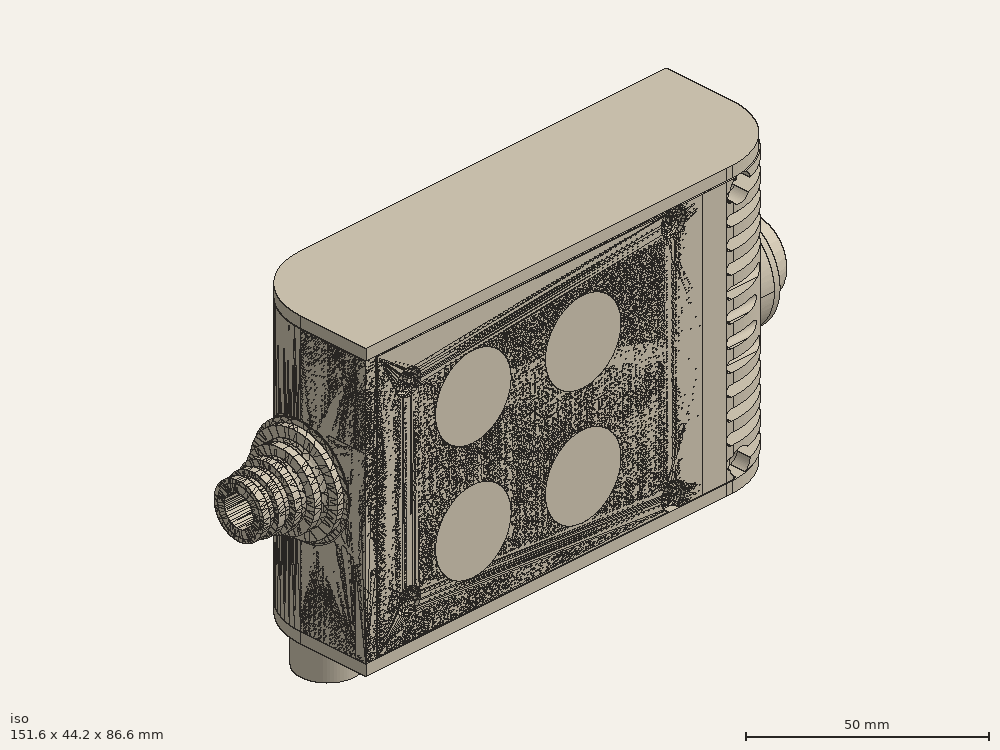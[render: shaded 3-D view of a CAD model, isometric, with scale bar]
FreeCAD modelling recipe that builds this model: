
FCSTD DOCUMENT  (FreeCAD 0.19R0.19.2)
Label: enclosure_207FCStd
License: All rights reserved
LicenseURL: http://en.wikipedia.org/wiki/All_rights_reserved
objects: Part::Revolution×152, Part::MultiFuse×146, Part::Feature×146, Sketcher::SketchObject×84, Part::Cut×70, Part::Cylinder×70, Part::Extrusion×69, Part::Fillet×58, Part::Box×36, App::MeasureDistance×4, Part::FeaturePython×2, Image::ImagePlane×1, PartDesign::Body×1, Part::Mirroring×1
note: 835 computed .brp shape members not serialized (recipe doc carries the construction recipe); baked Part::Feature solids carry a one-line shape summary decoded from their .brp

FEATURE [Sketcher::SketchObject] Sketch  label="topSketch"
  FullyConstrained = true
  sketch-geometry (20):
    g0: LineSegment StartX=5.21097e-06 StartY=3 StartZ=0 EndX=5.21097e-06 EndY=19 EndZ=0
    g1: ArcOfCircle CenterX=19 CenterY=19 CenterZ=0 NormalX=0 NormalY=0 NormalZ=1 AngleXU=0 Radius=19 StartAngle=1.5708 EndAngle=3.14159
    g2: ArcOfCircle CenterX=19 CenterY=19 CenterZ=0 NormalX=0 NormalY=0 NormalZ=1 AngleXU=0 Radius=16 StartAngle=1.5708 EndAngle=3.14159
    g3: LineSegment StartX=114 StartY=35 StartZ=0 EndX=19 EndY=35 EndZ=0
    g4: LineSegment StartX=5.21097e-06 StartY=3 StartZ=0 EndX=5.21097e-06 EndY=0 EndZ=0
    g5: LineSegment StartX=3 StartY=0 StartZ=0 EndX=5.21097e-06 EndY=0 EndZ=0
    g6: LineSegment StartX=3 StartY=19 StartZ=0 EndX=3 EndY=0 EndZ=0
    g7: LineSegment StartX=19 StartY=38 StartZ=0 EndX=124 EndY=38 EndZ=0
    g8: Circle CenterX=119 CenterY=35 CenterZ=0 NormalX=0 NormalY=0 NormalZ=1 AngleXU=0 Radius=1
    g9: Circle CenterX=121 CenterY=35 CenterZ=0 NormalX=0 NormalY=0 NormalZ=1 AngleXU=0 Radius=1
    g10: Circle CenterX=121 CenterY=33 CenterZ=0 NormalX=0 NormalY=0 NormalZ=1 AngleXU=0 Radius=1
    g11: BSplineCurve PolesCount=3 KnotsCount=2 Degree=2 IsPeriodic=0
    g12: GeomPoint X=119 Y=35 Z=0
    g13: GeomPoint X=121 Y=33 Z=0
    g14: LineSegment StartX=119 StartY=35 StartZ=0 EndX=114 EndY=35 EndZ=0
    g15: ArcOfCircle CenterX=105 CenterY=19 CenterZ=0 NormalX=0 NormalY=0 NormalZ=1 AngleXU=0 Radius=19 StartAngle=5.7297 EndAngle=6.28319
    g16: ArcOfCircle CenterX=105 CenterY=19 CenterZ=0 NormalX=0 NormalY=0 NormalZ=1 AngleXU=0 Radius=16 StartAngle=5.60905 EndAngle=6.28319
    g17: LineSegment StartX=121 StartY=33 StartZ=0 EndX=121 EndY=19 EndZ=0
    g18: LineSegment StartX=124 StartY=38 StartZ=0 EndX=124 EndY=19 EndZ=0
    g19: LineSegment StartX=117.5 StartY=9.01251 StartZ=0 EndX=121.163 EndY=9.0125 EndZ=0
  constraints (46):
    c: Vertical(g0)
    c: Block(g0)
    c: Coincident(g1,g0)
    c: Block(g1)
    c: Coincident(g2,g1)
    c: Block(g2)
    c: Coincident(g3,g2)
    c: Horizontal(g3)
    c: Tangent(g3,g2)
    c: Coincident(g4,g0)
    c: Distance(g4) = 3
    c: Vertical(g4)
    c: Coincident(g5,g4)
    c: Horizontal(g5)
    c: Coincident(g6,g2)
    c: Coincident(g6,g5)
    c: Vertical(g6)
    c: Horizontal(g7)
    c: Distance(g7) = 105
    c: Coincident(g7,g1)
    c: Block(g3)
    c: Weight(g8) = 1
    c: Equal(g8,g9)
    c: Equal(g8,g10)
    c: InternalAlignment(g8,g11)
    c: InternalAlignment(g9,g11)
    c: InternalAlignment(g10,g11)
    c: InternalAlignment(g12,g11)
    c: InternalAlignment(g13,g11)
    c: Block(g11)
    c: Coincident(g14,g11)
    c: Coincident(g14,g3)
    c: Horizontal(g14)
    c: Block(g15)
    c: Coincident(g16,g15)
    c: Block(g16)
    c: Coincident(g17,g11)
    c: Coincident(g17,g16)
    c: Vertical(g17)
    c: Distance(g17) = 14
    c: Coincident(g18,g7)
    c: Coincident(g18,g15)
    c: Vertical(g18)
    c: Distance(g18) = 19
    c: Coincident(g19,g16)
    c: Coincident(g19,g15)
FEATURE [Sketcher::SketchObject] Sketch001  label="bottomSketch"
  FullyConstrained = true
  sketch-geometry (32):
    g0: LineSegment StartX=3.3 StartY=-6.03275e-07 StartZ=0 EndX=98 EndY=-6.03275e-07 EndZ=0
    g1: ArcOfCircle CenterX=98 CenterY=19 CenterZ=0 NormalX=0 NormalY=0 NormalZ=1 AngleXU=0 Radius=19 StartAngle=4.71239 EndAngle=5.71103
    g2: LineSegment StartX=6.3 StartY=8 StartZ=0 EndX=3.3 EndY=8 EndZ=0
    g3: LineSegment StartX=3.3 StartY=8 StartZ=0 EndX=3.3 EndY=-6.03275e-07 EndZ=0
    g4: ArcOfCircle CenterX=8.3 CenterY=5 CenterZ=0 NormalX=0 NormalY=0 NormalZ=1 AngleXU=0 Radius=2 StartAngle=3.14159 EndAngle=4.71239
    g5: LineSegment StartX=6.3 StartY=8 StartZ=0 EndX=6.3 EndY=5 EndZ=0
    g6: ArcOfCircle CenterX=98 CenterY=19 CenterZ=0 NormalX=0 NormalY=0 NormalZ=1 AngleXU=0 Radius=12.7 StartAngle=4.71239 EndAngle=6.28319
    g7: LineSegment StartX=94.7 StartY=3 StartZ=0 EndX=8.3 EndY=3 EndZ=0
    g8-g12: Circle x5 (B-spline internal-alignment scaffolding for g13; pole/knot coordinates omitted)
    g13: BSplineCurve PolesCount=5 KnotsCount=3 Degree=3 IsPeriodic=0
    g14: GeomPoint X=98 Y=6.3 Z=0
    g15: GeomPoint X=96.3938 Y=4.71946 Z=0
    g16: GeomPoint X=94.7 Y=3 Z=0
    g17-g23: Circle x7 (B-spline internal-alignment scaffolding for g24; pole/knot coordinates omitted)
    g24: BSplineCurve PolesCount=7 KnotsCount=5 Degree=3 IsPeriodic=0
    g25-g29: GeomPoint x5 (B-spline internal-alignment scaffolding for g24; pole/knot coordinates omitted)
    g30: ArcOfCircle CenterX=98 CenterY=19 CenterZ=0 NormalX=0 NormalY=0 NormalZ=1 AngleXU=0 Radius=15.7 StartAngle=5.81226 EndAngle=6.28319
    g31: LineSegment StartX=110.7 StartY=19 StartZ=0 EndX=113.7 EndY=19 EndZ=0
  constraints (41):
    c: Horizontal(g0)
    c: Coincident(g1,g0)
    c: Block(g1)
    c: Horizontal(g2)
    c: Distance(g2) = 3
    c: Coincident(g3,g2)
    c: Vertical(g3)
    c: Coincident(g3,g0)
    c: Block(g4)
    c: Block(g2)
    c: Coincident(g5,g2)
    c: Coincident(g5,g4)
    c: Vertical(g5)
    c: Coincident(g6,g1)
    c: Block(g6)
    c: Coincident(g7,g4)
    c: Horizontal(g7)
    c: Block(g0)
    c: Block(g7)
    c: Block(g3)
    c: Coincident(g13,g6)
    c: Weight(g8) = 1
    c: Equal(g8, g9-g12) x4
    c: Coincident(g13,g7)
    c: InternalAlignment(g8-g12 -> g13) x5
    c: InternalAlignment(g14,g13)
    c: InternalAlignment(g15,g13)
    c: InternalAlignment(g16,g13)
    c: Block(g13)
    c: Weight(g17) = 1
    c: Equal(g17, g18-g23) x6
    c: Coincident(g24,g1)
    c: InternalAlignment(g17-g23 -> g24) x7
    c: InternalAlignment(g25-g29 -> g24) x5
    c: Block(g24)
    c: Coincident(g30,g24)
    c: Coincident(g31,g6)
    c: Coincident(g31,g30)
    c: Horizontal(g31)
    c: Block(g31)
    c: Block(g30)
FEATURE [Part::Extrusion] Extrude  label="top"
  Base = -> Sketch
  Dir = (0,0,1)
  DirMode = 2
  FaceMakerClass = Part::FaceMakerBullseye
  LengthFwd = 72
  LengthRev = 0
  Solid = true
  Symmetric = false
FEATURE [Part::Extrusion] Extrude001  label="bottom"
  Base = -> Sketch001
  Dir = (0,0,1)
  DirMode = 2
  FaceMakerClass = Part::FaceMakerBullseye
  LengthFwd = 71.4
  LengthRev = 0
  Placement = pos=(0,0,0.3) rot=(0,0,1;0rad)
  Solid = true
  Symmetric = false
FEATURE [Sketcher::SketchObject] Sketch002  label="topSketch001"
  FullyConstrained = true
  sketch-geometry (8):
    g0: ArcOfCircle CenterX=19 CenterY=19.0975 CenterZ=0 NormalX=0 NormalY=0 NormalZ=1 AngleXU=0 Radius=18.9025 StartAngle=1.5708 EndAngle=3.14674
    g1: LineSegment StartX=0.0977805 StartY=19.0003 StartZ=0 EndX=0.0977805 EndY=0.000251602 EndZ=0
    g2: LineSegment StartX=19 StartY=38 StartZ=0 EndX=124 EndY=38 EndZ=0
    g3: LineSegment StartX=0.0977805 StartY=0.000251602 StartZ=0 EndX=105.098 EndY=0.000251602 EndZ=0
    g4: LineSegment StartX=124 StartY=38 StartZ=0 EndX=125.616 EndY=38 EndZ=0
    g5: LineSegment StartX=105.098 StartY=0.000251602 StartZ=0 EndX=106.713 EndY=0.000251602 EndZ=0
    g6: ArcOfCircle CenterX=106.616 CenterY=19 CenterZ=0 NormalX=0 NormalY=0 NormalZ=1 AngleXU=0 Radius=19 StartAngle=4.71754 EndAngle=6.28319
    g7: LineSegment StartX=125.616 StartY=38 StartZ=0 EndX=125.616 EndY=19 EndZ=0
  constraints (21):
    c: Block(g0)
    c: Coincident(g1,g0)
    c: Vertical(g1)
    c: Horizontal(g2)
    c: Distance(g2) = 105
    c: Coincident(g2,g0)
    c: Distance(g1) = 19
    c: Coincident(g3,g1)
    c: Horizontal(g3)
    c: Distance(g3) = 105
    c: Coincident(g4,g2)
    c: Horizontal(g4)
    c: Distance(g4) = 1.61553
    c: Horizontal(g5)
    c: Equal(g4,g5) = 1.61553
    c: Coincident(g5,g3)
    c: Block(g6)
    c: Coincident(g6,g5)
    c: Coincident(g7,g4)
    c: Coincident(g7,g6)
    c: Vertical(g7)
FEATURE [Part::Extrusion] Extrude002  label="sideA"
  Base = -> Sketch002
  Dir = (0,0,1)
  DirMode = 2
  FaceMakerClass = Part::FaceMakerBullseye
  LengthFwd = 3
  LengthRev = 0
  Placement = pos=(0,0,-3) rot=(0,0,1;0rad)
  Solid = true
  Symmetric = false
FEATURE [Sketcher::SketchObject] Sketch003  label="topSketch002"
  FullyConstrained = true
  sketch-geometry (6):
    g0: LineSegment StartX=19 StartY=38 StartZ=0 EndX=117 EndY=38 EndZ=0
    g1: ArcOfCircle CenterX=19 CenterY=19 CenterZ=0 NormalX=0 NormalY=0 NormalZ=1 AngleXU=0 Radius=19 StartAngle=1.5708 EndAngle=3.14159
    g2: LineSegment StartX=117 StartY=38 StartZ=0 EndX=117 EndY=19 EndZ=0
    g3: LineSegment StartX=98 StartY=1.0161e-12 StartZ=0 EndX=5.22862e-06 EndY=1.0161e-12 EndZ=0
    g4: LineSegment StartX=5.22862e-06 StartY=19 StartZ=0 EndX=5.22862e-06 EndY=1.0161e-12 EndZ=0
    g5: ArcOfCircle CenterX=98 CenterY=19 CenterZ=0 NormalX=0 NormalY=0 NormalZ=1 AngleXU=0 Radius=19 StartAngle=4.71239 EndAngle=6.28319
  constraints (16):
    c: Horizontal(g0)
    c: Distance(g0) = 98
    c: Coincident(g1,g0)
    c: Block(g1)
    c: Coincident(g2,g0)
    c: Vertical(g2)
    c: Distance(g2) = 19
    c: Horizontal(g3)
    c: Coincident(g4,g1)
    c: Vertical(g4)
    c: Coincident(g3,g4)
    c: Block(g3)
    c: Coincident(g5,g2)
    c: Coincident(g5,g3)
    c: Block(g0)
    c: Block(g5)
FEATURE [Sketcher::SketchObject] Sketch004
  FullyConstrained = true
  MapMode = 3
  Placement = pos=(0,0,0) rot=(1,0,0;1.5708rad)
  Support = -> [Extrude]
  sketch-geometry (8):
    g0: Circle CenterX=80.351 CenterY=-67.6202 CenterZ=0 NormalX=0 NormalY=0 NormalZ=1 AngleXU=0 Radius=2
    g1: Circle CenterX=80.351 CenterY=-67.6202 CenterZ=0 NormalX=0 NormalY=0 NormalZ=1 AngleXU=0 Radius=3
    g2: Circle CenterX=80.351 CenterY=-4.92017 CenterZ=0 NormalX=0 NormalY=0 NormalZ=1 AngleXU=0 Radius=2
    g3: Circle CenterX=80.351 CenterY=-4.92017 CenterZ=0 NormalX=0 NormalY=0 NormalZ=1 AngleXU=0 Radius=3
    g4: Circle CenterX=23.851 CenterY=-4.92017 CenterZ=0 NormalX=0 NormalY=0 NormalZ=1 AngleXU=0 Radius=2
    g5: Circle CenterX=23.851 CenterY=-4.92017 CenterZ=0 NormalX=0 NormalY=0 NormalZ=1 AngleXU=0 Radius=3
    g6: Circle CenterX=23.851 CenterY=-67.6202 CenterZ=0 NormalX=0 NormalY=0 NormalZ=1 AngleXU=0 Radius=2
    g7: Circle CenterX=23.851 CenterY=-67.6202 CenterZ=0 NormalX=0 NormalY=0 NormalZ=1 AngleXU=0 Radius=3
  constraints (8):
    c: Block(g3)
    c: Block(g2)
    c: Block(g1)
    c: Block(g0)
    c: Block(g6)
    c: Block(g7)
    c: Block(g4)
    c: Block(g5)
FEATURE [Part::Extrusion] Extrude004
  Base = -> Sketch004
  Dir = (0,-1,2e-16)
  DirMode = 2
  FaceMakerClass = Part::FaceMakerBullseye
  LengthFwd = 6
  LengthRev = 0
  Placement = pos=(0,9,0) rot=(0,0,1;0rad)
  Solid = true
  Symmetric = false
FEATURE [Sketcher::SketchObject] Sketch005
  FullyConstrained = true
  MapMode = 3
  Placement = pos=(0,0,0) rot=(1,0,0;1.5708rad)
  Support = -> [Extrude]
  sketch-geometry (8):
    g0: Circle CenterX=80.351 CenterY=-67.6202 CenterZ=0 NormalX=0 NormalY=0 NormalZ=1 AngleXU=0 Radius=3
    g1: Circle CenterX=80.351 CenterY=-4.92017 CenterZ=0 NormalX=0 NormalY=0 NormalZ=1 AngleXU=0 Radius=3
    g2: Circle CenterX=23.851 CenterY=-4.92017 CenterZ=0 NormalX=0 NormalY=0 NormalZ=1 AngleXU=0 Radius=3
    g3: Circle CenterX=23.851 CenterY=-67.6202 CenterZ=0 NormalX=0 NormalY=0 NormalZ=1 AngleXU=0 Radius=3
    g4: Circle CenterX=23.851 CenterY=-67.6202 CenterZ=0 NormalX=0 NormalY=0 NormalZ=1 AngleXU=0 Radius=5
    g5: Circle CenterX=80.351 CenterY=-67.6202 CenterZ=0 NormalX=0 NormalY=0 NormalZ=1 AngleXU=0 Radius=5
    g6: Circle CenterX=23.851 CenterY=-4.92017 CenterZ=0 NormalX=0 NormalY=0 NormalZ=1 AngleXU=0 Radius=5
    g7: Circle CenterX=80.351 CenterY=-4.92017 CenterZ=0 NormalX=0 NormalY=0 NormalZ=1 AngleXU=0 Radius=5
  constraints (8):
    c: Block(g1)
    c: Block(g0)
    c: Block(g3)
    c: Block(g2)
    c: Block(g5)
    c: Block(g4)
    c: Block(g6)
    c: Block(g7)
FEATURE [Part::Extrusion] Extrude005
  Base = -> Sketch005
  Dir = (0,-1,2e-16)
  DirMode = 2
  FaceMakerClass = Part::FaceMakerBullseye
  LengthFwd = 2
  LengthRev = 0
  Solid = true
  Symmetric = false
FEATURE [Sketcher::SketchObject] Sketch006
  FullyConstrained = true
  MapMode = 3
  Placement = pos=(0,0,0) rot=(1,0,0;1.5708rad)
  sketch-geometry (8):
    g0: Circle CenterX=80.351 CenterY=-67.6202 CenterZ=0 NormalX=0 NormalY=0 NormalZ=1 AngleXU=0 Radius=3
    g1: Circle CenterX=80.351 CenterY=-4.92017 CenterZ=0 NormalX=0 NormalY=0 NormalZ=1 AngleXU=0 Radius=3
    g2: Circle CenterX=23.851 CenterY=-4.92017 CenterZ=0 NormalX=0 NormalY=0 NormalZ=1 AngleXU=0 Radius=3
    g3: Circle CenterX=23.851 CenterY=-67.6202 CenterZ=0 NormalX=0 NormalY=0 NormalZ=1 AngleXU=0 Radius=3
    g4: Circle CenterX=23.851 CenterY=-67.6202 CenterZ=0 NormalX=0 NormalY=0 NormalZ=1 AngleXU=0 Radius=5
    g5: Circle CenterX=80.351 CenterY=-67.6202 CenterZ=0 NormalX=0 NormalY=0 NormalZ=1 AngleXU=0 Radius=5
    g6: Circle CenterX=23.851 CenterY=-4.92017 CenterZ=0 NormalX=0 NormalY=0 NormalZ=1 AngleXU=0 Radius=5
    g7: Circle CenterX=80.351 CenterY=-4.92017 CenterZ=0 NormalX=0 NormalY=0 NormalZ=1 AngleXU=0 Radius=5
  constraints (8):
    c: Block(g1)
    c: Block(g0)
    c: Block(g3)
    c: Block(g2)
    c: Block(g5)
    c: Block(g4)
    c: Block(g6)
    c: Block(g7)
FEATURE [Part::Extrusion] Extrude007
  Base = -> Sketch006
  Dir = (0,-1,2e-16)
  DirMode = 2
  FaceMakerClass = Part::FaceMakerBullseye
  LengthFwd = 2
  LengthRev = 0
  Solid = true
  Symmetric = false
FEATURE [Part::Fillet] Fillet
  Base = -> Extrude007
  Edges = 4 edges r=1.99: [Edge6,Edge12,Edge18,Edge24]
FEATURE [Part::Cut] Cut
  Base = -> Extrude005
  Placement = pos=(0,5,0) rot=(0,0,1;0rad)
  Tool = -> Fillet
FEATURE [Part::MultiFuse] Fusion  label="pCBScrews"
  Placement = pos=(-2.5,0,72.3) rot=(0,0,1;0rad)
  Shapes = -> [Extrude004,Cut]
FEATURE [App::MeasureDistance] Distance  label="Distance: 0.69 mm"
  Distance = 0.685967
  P1 = (24.0138,2.9647,0.3)
  P2 = (23.8901,3,-0.373787)
FEATURE [App::MeasureDistance] Distance001  label="Distance: 0.53 mm"
  Distance = 0.533607
  P1 = (80.2939,3,72.2334)
  P2 = (80.281,2.99661,71.7)
FEATURE [Part::Fillet] Fillet001
  Base = -> Extrude001
  Edges = 1 edges r=2.4: [Edge17]
FEATURE [Part::Fillet] Fillet002  label="bottom001"
  Base = -> Fillet001
  Edges = 1 edges r=2.4: [Edge36]
FEATURE [Part::Fillet] Fillet003  label="top001"
  Base = -> Extrude
  Edges = 1 edges r=2: [Edge1]
FEATURE [Sketcher::SketchObject] Sketch007
  FullyConstrained = true
  sketch-geometry (16):
    g0: LineSegment StartX=4 StartY=0 StartZ=0 EndX=4 EndY=2.4 EndZ=0
    g1: LineSegment StartX=4 StartY=2.4 StartZ=0 EndX=7 EndY=2.4 EndZ=0
    g2: LineSegment StartX=4 StartY=0 StartZ=0 EndX=5.7 EndY=0 EndZ=0
    g3: LineSegment StartX=5.7 StartY=0 StartZ=0 EndX=5.7 EndY=-5.6 EndZ=0
    g4-g8: Circle x5 (B-spline internal-alignment scaffolding for g9; pole/knot coordinates omitted)
    g9: BSplineCurve PolesCount=5 KnotsCount=3 Degree=3 IsPeriodic=0
    g10: GeomPoint X=7 Y=2.4 Z=0
    g11: GeomPoint X=10.4582 Y=-1.55472 Z=0
    g12: GeomPoint X=14 Y=-5.6 Z=0
    g13: LineSegment StartX=14 StartY=-5.6 StartZ=0 EndX=14 EndY=-14.1 EndZ=0
    g14: LineSegment StartX=14 StartY=-14.1 StartZ=0 EndX=6.5 EndY=-14.1 EndZ=0
    g15: LineSegment StartX=5.7 StartY=-5.6 StartZ=0 EndX=6.5 EndY=-14.1 EndZ=0
  constraints (28):
    c: Distance(g0) = 2.4
    c: Vertical(g0)
    c: Block(g0)
    c: Coincident(g1,g0)
    c: Horizontal(g1)
    c: Distance(g1) = 3
    c: Coincident(g2,g0)
    c: Horizontal(g2)
    c: Distance(g2) = 1.7
    c: Coincident(g3,g2)
    c: Vertical(g3)
    c: Distance(g3) = 5.6
    c: Coincident(g9,g1)
    c: Weight(g4) = 1
    c: Equal(g4, g5-g8) x4
    c: InternalAlignment(g4-g8 -> g9) x5
    c: InternalAlignment(g10,g9)
    c: InternalAlignment(g11,g9)
    c: InternalAlignment(g12,g9)
    c: Block(g9)
    c: Coincident(g13,g9)
    c: Vertical(g13)
    c: Distance(g13) = 8.5
    c: Coincident(g14,g13)
    c: Horizontal(g14)
    c: Distance(g14) = 7.5
    c: Coincident(g15,g3)
    c: Coincident(g15,g14)
FEATURE [Part::Feature] Face
  shape: bbox 10 x 16.5 x 2e-07 mm, 1 faces, 0 solids (baked)
FEATURE [Part::Revolution] Revolve  label="plugHousing"
  Angle = 360
  Axis = (0,1,0)
  Base = (0,0,0)
  FaceMakerClass = Part::FaceMakerBullseye
  Placement = pos=(0,0,36.15) rot=(0,0,1;0rad)
  Solid = false
  Source = -> Face
  Symmetric = false
FEATURE [Part::Feature] Face001
  shape: bbox 10 x 16.5 x 2e-07 mm, 1 faces, 0 solids (baked)
FEATURE [Part::Revolution] Revolve001  label="plugHousing001"
  Angle = 360
  Axis = (0,1,0)
  Base = (0,0,0)
  FaceMakerClass = Part::FaceMakerBullseye
  Placement = pos=(0,0,36.15) rot=(0,0,1;0rad)
  Solid = false
  Source = -> Face001
  Symmetric = false
FEATURE [Part::MultiFuse] Fusion001  label="plugHousing002"
  Placement = pos=(0,0,0) rot=(0,0,1;1.5708rad)
  Shapes = -> [Revolve001,Revolve]
FEATURE [Part::Feature] Face002
  shape: bbox 10 x 16.5 x 2e-07 mm, 1 faces, 0 solids (baked)
FEATURE [Part::Revolution] Revolve003  label="plugHousing005"
  Angle = 360
  Axis = (0,1,0)
  Base = (0,0,0)
  FaceMakerClass = Part::FaceMakerBullseye
  Placement = pos=(0,0,36.15) rot=(0,0,1;0rad)
  Solid = false
  Source = -> Face002
  Symmetric = false
FEATURE [Part::Feature] Face003
  shape: bbox 10 x 16.5 x 2e-07 mm, 1 faces, 0 solids (baked)
FEATURE [Part::Revolution] Revolve002  label="plugHousing003"
  Angle = 360
  Axis = (0,1,0)
  Base = (0,0,0)
  FaceMakerClass = Part::FaceMakerBullseye
  Placement = pos=(0,0,36.15) rot=(0,0,1;0rad)
  Solid = false
  Source = -> Face003
  Symmetric = false
FEATURE [Part::MultiFuse] Fusion002  label="plugHousing004"
  Placement = pos=(0,0,0) rot=(0,0,1;1.5708rad)
  Shapes = -> [Revolve002,Revolve003]
FEATURE [Part::MultiFuse] Fusion003  label="plugHousing006"
  Placement = pos=(0,19,0) rot=(0,0,1;3.14159rad)
  Shapes = -> [Fusion002,Fusion001]
FEATURE [Part::Feature] Face004
  shape: bbox 10 x 16.5 x 2e-07 mm, 1 faces, 0 solids (baked)
FEATURE [Part::Revolution] Revolve006  label="plugHousing010"
  Angle = 360
  Axis = (0,1,0)
  Base = (0,0,0)
  FaceMakerClass = Part::FaceMakerBullseye
  Placement = pos=(0,0,36.15) rot=(0,0,1;0rad)
  Solid = false
  Source = -> Face004
  Symmetric = false
FEATURE [Part::Feature] Face005
  shape: bbox 10 x 16.5 x 2e-07 mm, 1 faces, 0 solids (baked)
FEATURE [Part::Revolution] Revolve007  label="plugHousing011"
  Angle = 360
  Axis = (0,1,0)
  Base = (0,0,0)
  FaceMakerClass = Part::FaceMakerBullseye
  Placement = pos=(0,0,36.15) rot=(0,0,1;0rad)
  Solid = false
  Source = -> Face005
  Symmetric = false
FEATURE [Part::Feature] Face006
  shape: bbox 10 x 16.5 x 2e-07 mm, 1 faces, 0 solids (baked)
FEATURE [Part::Revolution] Revolve004  label="plugHousing007"
  Angle = 360
  Axis = (0,1,0)
  Base = (0,0,0)
  FaceMakerClass = Part::FaceMakerBullseye
  Placement = pos=(0,0,36.15) rot=(0,0,1;0rad)
  Solid = false
  Source = -> Face006
  Symmetric = false
FEATURE [Part::MultiFuse] Fusion004  label="plugHousing009"
  Placement = pos=(0,0,0) rot=(0,0,1;1.5708rad)
  Shapes = -> [Revolve004,Revolve007]
FEATURE [Part::Feature] Face007
  shape: bbox 10 x 16.5 x 2e-07 mm, 1 faces, 0 solids (baked)
FEATURE [Part::Revolution] Revolve005  label="plugHousing008"
  Angle = 360
  Axis = (0,1,0)
  Base = (0,0,0)
  FaceMakerClass = Part::FaceMakerBullseye
  Placement = pos=(0,0,36.15) rot=(0,0,1;0rad)
  Solid = false
  Source = -> Face007
  Symmetric = false
FEATURE [Part::MultiFuse] Fusion005  label="plugHousing012"
  Placement = pos=(0,0,0) rot=(0,0,1;1.5708rad)
  Shapes = -> [Revolve006,Revolve005]
FEATURE [Part::MultiFuse] Fusion006  label="plugHousing013"
  Placement = pos=(0,19,0) rot=(0,0,1;3.14159rad)
  Shapes = -> [Fusion005,Fusion004]
FEATURE [Part::MultiFuse] Fusion007  label="plugHousing014"
  Placement = pos=(122.621,0,-0.15) rot=(0,0,1;0rad)
  Shapes = -> [Fusion003,Fusion006]
FEATURE [Part::Cylinder] Cylinder002
  Angle = 360
  AttacherType = Attacher::AttachEngine3D
  Height = 20
  Placement = pos=(0,0,36.15) rot=(0,0,1;0rad)
  Radius = 4
FEATURE [Part::Cylinder] Cylinder003
  Angle = 360
  AttacherType = Attacher::AttachEngine3D
  Height = 10
  Placement = pos=(0,0,36.15) rot=(0,0,1;0rad)
  Radius = 4
FEATURE [Part::MultiFuse] Fusion009  label="removeToCreateHoleForPlugHousing"
  Placement = pos=(70,19,36.15) rot=(0,1,0;1.5708rad)
  Shapes = -> [Cylinder002,Cylinder003]
FEATURE [Part::Cylinder] Cylinder004
  Angle = 360
  AttacherType = Attacher::AttachEngine3D
  Height = 20
  Placement = pos=(0,0,36.15) rot=(0,0,1;0rad)
  Radius = 4
FEATURE [Part::Cylinder] Cylinder005
  Angle = 360
  AttacherType = Attacher::AttachEngine3D
  Height = 10
  Placement = pos=(0,0,36.15) rot=(0,0,1;0rad)
  Radius = 4
FEATURE [Part::MultiFuse] Fusion010  label="removeToCreateHoleForPlugHousing001"
  Placement = pos=(70,19,36.15) rot=(0,1,0;1.5708rad)
  Shapes = -> [Cylinder004,Cylinder005]
FEATURE [Part::Cut] Cut001
  Base = -> Fillet003
  Tool = -> Fusion010
FEATURE [Part::Cut] Cut002  label="Bottom"
  Base = -> Fillet002
  Tool = -> Fusion009
FEATURE [Part::Feature] Face008
  shape: bbox 10 x 16.5 x 2e-07 mm, 1 faces, 0 solids (baked)
FEATURE [Part::Revolution] Revolve011  label="plugHousing021"
  Angle = 360
  Axis = (0,1,0)
  Base = (0,0,0)
  FaceMakerClass = Part::FaceMakerBullseye
  Placement = pos=(0,0,36.15) rot=(0,0,1;0rad)
  Solid = false
  Source = -> Face008
  Symmetric = false
FEATURE [Part::Feature] Face009
  shape: bbox 10 x 16.5 x 2e-07 mm, 1 faces, 0 solids (baked)
FEATURE [Part::Revolution] Revolve012  label="plugHousing022"
  Angle = 360
  Axis = (0,1,0)
  Base = (0,0,0)
  FaceMakerClass = Part::FaceMakerBullseye
  Placement = pos=(0,0,36.15) rot=(0,0,1;0rad)
  Solid = false
  Source = -> Face009
  Symmetric = false
FEATURE [Part::Feature] Face010 .. Face013  x4 (patterned run collapsed; names and placements below)
  shape: bbox 10 x 16.5 x 2e-07 mm, 1 faces, 0 solids (baked)
FEATURE [Part::Revolution] Revolve015  label="plugHousing027"
  Angle = 360
  Axis = (0,1,0)
  Base = (0,0,0)
  FaceMakerClass = Part::FaceMakerBullseye
  Placement = pos=(0,0,36.15) rot=(0,0,1;0rad)
  Solid = false
  Source = -> Face013
  Symmetric = false
FEATURE [Part::Feature] Face014
  shape: bbox 10 x 16.5 x 2e-07 mm, 1 faces, 0 solids (baked)
FEATURE [Part::Feature] Face015
  shape: bbox 10 x 16.5 x 2e-07 mm, 1 faces, 0 solids (baked)
FEATURE [Part::Feature] Face016
  shape: bbox 10 x 16.5 x 2e-07 mm, 1 faces, 0 solids (baked)
FEATURE [Part::Revolution] Revolve019  label="plugHousing033"
  Angle = 360
  Axis = (0,1,0)
  Base = (0,0,0)
  FaceMakerClass = Part::FaceMakerBullseye
  Placement = pos=(0,0,36.15) rot=(0,0,1;0rad)
  Solid = false
  Source = -> Face016
  Symmetric = false
FEATURE [Part::Feature] Face017
  shape: bbox 10 x 16.5 x 2e-07 mm, 1 faces, 0 solids (baked)
FEATURE [Part::Revolution] Revolve020  label="plugHousing034"
  Angle = 360
  Axis = (0,1,0)
  Base = (0,0,0)
  FaceMakerClass = Part::FaceMakerBullseye
  Placement = pos=(0,0,36.15) rot=(0,0,1;0rad)
  Solid = false
  Source = -> Face017
  Symmetric = false
FEATURE [Part::Feature] Face018
  shape: bbox 10 x 16.5 x 2e-07 mm, 1 faces, 0 solids (baked)
FEATURE [Part::Revolution] Revolve016  label="plugHousing030"
  Angle = 360
  Axis = (0,1,0)
  Base = (0,0,0)
  FaceMakerClass = Part::FaceMakerBullseye
  Placement = pos=(0,0,36.15) rot=(0,0,1;0rad)
  Solid = false
  Source = -> Face018
  Symmetric = false
FEATURE [Part::MultiFuse] Fusion020  label="plugHousing038"
  Placement = pos=(0,0,0) rot=(0,0,1;1.5708rad)
  Shapes = -> [Revolve016,Revolve020]
FEATURE [Part::Feature] Face019
  shape: bbox 10 x 16.5 x 2e-07 mm, 1 faces, 0 solids (baked)
FEATURE [Part::Feature] Face020
  shape: bbox 10 x 16.5 x 2e-07 mm, 1 faces, 0 solids (baked)
FEATURE [Part::Revolution] Revolve017  label="plugHousing031"
  Angle = 360
  Axis = (0,1,0)
  Base = (0,0,0)
  FaceMakerClass = Part::FaceMakerBullseye
  Placement = pos=(0,0,36.15) rot=(0,0,1;0rad)
  Solid = false
  Source = -> Face020
  Symmetric = false
FEATURE [Part::MultiFuse] Fusion021  label="plugHousing039"
  Placement = pos=(0,0,0) rot=(0,0,1;1.5708rad)
  Shapes = -> [Revolve019,Revolve017]
FEATURE [Part::MultiFuse] Fusion023  label="plugHousing041"
  Placement = pos=(0,19,0) rot=(0,0,1;3.14159rad)
  Shapes = -> [Fusion021,Fusion020]
FEATURE [Part::Revolution] Revolve022  label="plugHousing043"
  Angle = 360
  Axis = (0,1,0)
  Base = (0,0,0)
  FaceMakerClass = Part::FaceMakerBullseye
  Placement = pos=(0,0,36.15) rot=(0,0,1;0rad)
  Solid = false
  Source = -> Face019
  Symmetric = false
FEATURE [Part::Feature] Face021
  shape: bbox 10 x 16.5 x 2e-07 mm, 1 faces, 0 solids (baked)
FEATURE [Part::Revolution] Revolve023  label="plugHousing044"
  Angle = 360
  Axis = (0,1,0)
  Base = (0,0,0)
  FaceMakerClass = Part::FaceMakerBullseye
  Placement = pos=(0,0,36.15) rot=(0,0,1;0rad)
  Solid = false
  Source = -> Face021
  Symmetric = false
FEATURE [Part::Feature] Face022
  shape: bbox 10 x 16.5 x 2e-07 mm, 1 faces, 0 solids (baked)
FEATURE [Part::Revolution] Revolve018  label="plugHousing032"
  Angle = 360
  Axis = (0,1,0)
  Base = (0,0,0)
  FaceMakerClass = Part::FaceMakerBullseye
  Placement = pos=(0,0,36.15) rot=(0,0,1;0rad)
  Solid = false
  Source = -> Face022
  Symmetric = false
FEATURE [Part::MultiFuse] Fusion022  label="plugHousing040"
  Placement = pos=(0,0,0) rot=(0,0,1;1.5708rad)
  Shapes = -> [Revolve018,Revolve023]
FEATURE [Part::Feature] Face023
  shape: bbox 10 x 16.5 x 2e-07 mm, 1 faces, 0 solids (baked)
FEATURE [Part::Revolution] Revolve021  label="plugHousing035"
  Angle = 360
  Axis = (0,1,0)
  Base = (0,0,0)
  FaceMakerClass = Part::FaceMakerBullseye
  Placement = pos=(0,0,36.15) rot=(0,0,1;0rad)
  Solid = false
  Source = -> Face023
  Symmetric = false
FEATURE [Part::MultiFuse] Fusion018  label="plugHousing036"
  Placement = pos=(0,0,0) rot=(0,0,1;1.5708rad)
  Shapes = -> [Revolve022,Revolve021]
FEATURE [Part::MultiFuse] Fusion019  label="plugHousing037"
  Placement = pos=(0,19,0) rot=(0,0,1;3.14159rad)
  Shapes = -> [Fusion018,Fusion022]
FEATURE [Part::MultiFuse] Fusion024  label="plugHousing042"
  Placement = pos=(122.621,0,-0.15) rot=(0,0,1;0rad)
  Shapes = -> [Fusion023,Fusion019]
FEATURE [Part::Cylinder] Cylinder006
  Angle = 360
  AttacherType = Attacher::AttachEngine3D
  Height = 20
  Placement = pos=(0,0,36.15) rot=(0,0,1;0rad)
  Radius = 14.3
FEATURE [Part::Cylinder] Cylinder007
  Angle = 360
  AttacherType = Attacher::AttachEngine3D
  Height = 10
  Placement = pos=(0,0,36.15) rot=(0,0,1;0rad)
  Radius = 4
FEATURE [Part::MultiFuse] Fusion026  label="removeToCreteHoleForPlugHousing"
  Placement = pos=(70,19,36) rot=(0,1,0;1.5708rad)
  Shapes = -> [Cylinder006,Cylinder007]
FEATURE [Part::Box] Box001  label="Cube001"
  AttacherType = Attacher::AttachEngine3D
  Height = 28
  Length = 3
  Placement = pos=(110.7,19,22) rot=(0,0,1;0rad)
  Width = 15.7
FEATURE [Part::Cut] Cut003  label="top002"
  Base = -> Cut001
  Tool = -> Fusion007
FEATURE [Part::Revolution] Revolve008  label="plugHousing015"
  Angle = 360
  Axis = (0,1,0)
  Base = (0,0,0)
  FaceMakerClass = Part::FaceMakerBullseye
  Placement = pos=(0,0,36.15) rot=(0,0,1;0rad)
  Solid = false
  Source = -> Face010
  Symmetric = false
FEATURE [Part::MultiFuse] Fusion013  label="plugHousing020"
  Placement = pos=(0,0,0) rot=(0,0,1;1.5708rad)
  Shapes = -> [Revolve008,Revolve012]
FEATURE [Part::Cut] Cut004  label="top003"
  Base = -> Cut003
  Placement = pos=(1,0,0) rot=(0,0,1;0rad)
  Tool = -> Fusion026
FEATURE [Part::Cylinder] Cylinder008
  Angle = 360
  AttacherType = Attacher::AttachEngine3D
  Height = 20
  Placement = pos=(0,0,36.15) rot=(0,0,1;0rad)
  Radius = 10.3
FEATURE [Part::Cylinder] Cylinder009
  Angle = 360
  AttacherType = Attacher::AttachEngine3D
  Height = 10
  Placement = pos=(0,0,36.15) rot=(0,0,1;0rad)
  Radius = 4
FEATURE [Part::MultiFuse] Fusion027  label="removeToCreteHoleForPlugHousing001"
  Placement = pos=(70,19,36) rot=(0,1,0;1.5708rad)
  Shapes = -> [Cylinder008,Cylinder009]
FEATURE [Part::Cut] Cut005  label="plugHousingTab"
  Base = -> Box001
  Tool = -> Fusion027
FEATURE [Part::MultiFuse] Fusion028  label="plugHousing045"
  Shapes = -> [Fusion024,Cut005]
FEATURE [Part::Box] Box002  label="Cube002"
  AttacherType = Attacher::AttachEngine3D
  Height = 28.8
  Length = 3
  Placement = pos=(107.3,28,21.6) rot=(0,0,1;0rad)
  Width = 7
FEATURE [Part::Box] Box003  label="Cube003"
  AttacherType = Attacher::AttachEngine3D
  Height = 3
  Length = 6.4
  Placement = pos=(107.3,28,18.6) rot=(0,0,1;0rad)
  Width = 7
FEATURE [Part::Box] Box004  label="Cube004"
  AttacherType = Attacher::AttachEngine3D
  Height = 3
  Length = 6.4
  Placement = pos=(107.3,28,50.4) rot=(0,0,1;0rad)
  Width = 7
FEATURE [Part::MultiFuse] Fusion029  label="plugHousingBracketHolder"
  Shapes = -> [Box004,Box002,Box003]
FEATURE [Part::Cylinder] Cylinder010
  Angle = 360
  AttacherType = Attacher::AttachEngine3D
  Height = 20
  Placement = pos=(0,0,36.15) rot=(0,0,1;0rad)
  Radius = 14.3
FEATURE [Part::Cylinder] Cylinder011
  Angle = 360
  AttacherType = Attacher::AttachEngine3D
  Height = 10
  Placement = pos=(0,0,36.15) rot=(0,0,1;0rad)
  Radius = 4
FEATURE [Part::MultiFuse] Fusion030  label="removeToCreteHoleForPlugHousing002"
  Placement = pos=(70,19,36) rot=(0,1,0;1.5708rad)
  Shapes = -> [Cylinder010,Cylinder011]
FEATURE [Part::Cut] Cut006  label="plugHousingBracketHolder001"
  Base = -> Fusion029
  Tool = -> Fusion030
FEATURE [Part::Cylinder] Cylinder012
  Angle = 360
  AttacherType = Attacher::AttachEngine3D
  Height = 20
  Placement = pos=(0,0,36.15) rot=(0,0,1;0rad)
  Radius = 7
FEATURE [Part::Cylinder] Cylinder013
  Angle = 360
  AttacherType = Attacher::AttachEngine3D
  Height = 10
  Placement = pos=(0,0,36.15) rot=(0,0,1;0rad)
  Radius = 4
FEATURE [Part::MultiFuse] Fusion032  label="removeToCreteHoleForPlugHousing003"
  Placement = pos=(70,19,36) rot=(0,1,0;1.5708rad)
  Shapes = -> [Cylinder012,Cylinder013]
FEATURE [Part::Cut] Cut007  label="bottom002"
  Base = -> Cut002
  Tool = -> Fusion032
FEATURE [Sketcher::SketchObject] Sketch008
  FullyConstrained = true
  sketch-geometry (54):
    g0: LineSegment StartX=-4.2 StartY=0 StartZ=0 EndX=-6.2 EndY=0 EndZ=0
    g1: LineSegment StartX=-14 StartY=-18 StartZ=0 EndX=-14 EndY=-26.5 EndZ=0
    g2: LineSegment StartX=-4.2 StartY=0 StartZ=0 EndX=-4.2 EndY=-13.4877 EndZ=0
    g3: Circle CenterX=-4.2 CenterY=-13.4877 CenterZ=0 NormalX=0 NormalY=0 NormalZ=1 AngleXU=0 Radius=1
    g4: Circle CenterX=-4.2 CenterY=-26.5 CenterZ=0 NormalX=0 NormalY=0 NormalZ=1 AngleXU=0 Radius=1
    g5: Circle CenterX=-8.2 CenterY=-26.5 CenterZ=0 NormalX=0 NormalY=0 NormalZ=1 AngleXU=0 Radius=1
    g6: BSplineCurve PolesCount=3 KnotsCount=2 Degree=2 IsPeriodic=0
    g7: GeomPoint X=-4.2 Y=-13.4877 Z=0
    g8: GeomPoint X=-8.2 Y=-26.5 Z=0
    g9: LineSegment StartX=-14 StartY=-26.5 StartZ=0 EndX=-8.2 EndY=-26.5 EndZ=0
    g10: LineSegment StartX=-10.15 StartY=-12 StartZ=0 EndX=-10.15 EndY=-14 EndZ=0
    g11: LineSegment StartX=-12.8401 StartY=-16 StartZ=0 EndX=-10.1571 EndY=-16 EndZ=0
    g12: LineSegment StartX=-10.15 StartY=-14 StartZ=0 EndX=-8.70761 EndY=-14 EndZ=0
    g13: LineSegment StartX=-12.8401 StartY=-16 StartZ=0 EndX=-12.8401 EndY=-17.6958 EndZ=0
    g14: LineSegment StartX=-10.15 StartY=-12 StartZ=0 EndX=-7.79258 EndY=-12 EndZ=0
    g15: Circle CenterX=-6.2215 CenterY=-2 CenterZ=0 NormalX=0 NormalY=0 NormalZ=1 AngleXU=0 Radius=1
    g16: Circle CenterX=-6.22762 CenterY=-2.58724 CenterZ=0 NormalX=0 NormalY=0 NormalZ=1 AngleXU=0 Radius=1
    g17: Circle CenterX=-6.32538 CenterY=-4 CenterZ=0 NormalX=0 NormalY=0 NormalZ=1 AngleXU=0 Radius=1
    g18: BSplineCurve PolesCount=3 KnotsCount=2 Degree=2 IsPeriodic=0
    g19: GeomPoint X=-6.2215 Y=-2 Z=0
    g20: GeomPoint X=-6.32538 Y=-4 Z=0
    g21: Circle CenterX=-6.48644 CenterY=-5.99526 CenterZ=0 NormalX=0 NormalY=0 NormalZ=1 AngleXU=0 Radius=1
    g22: Circle CenterX=-6.58486 CenterY=-6.99526 CenterZ=0 NormalX=0 NormalY=0 NormalZ=1 AngleXU=0 Radius=1
    g23: Circle CenterX=-6.77343 CenterY=-8 CenterZ=0 NormalX=0 NormalY=0 NormalZ=1 AngleXU=0 Radius=1
    g24: BSplineCurve PolesCount=3 KnotsCount=2 Degree=2 IsPeriodic=0
    g25: GeomPoint X=-6.48644 Y=-5.99526 Z=0
    g26: GeomPoint X=-6.77343 Y=-8 Z=0
    g27: Circle CenterX=-7.19003 CenterY=-10 CenterZ=0 NormalX=0 NormalY=0 NormalZ=1 AngleXU=0 Radius=1
    g28: Circle CenterX=-7.44407 CenterY=-11.0915 CenterZ=0 NormalX=0 NormalY=0 NormalZ=1 AngleXU=0 Radius=1
    g29: Circle CenterX=-7.79258 CenterY=-12 CenterZ=0 NormalX=0 NormalY=0 NormalZ=1 AngleXU=0 Radius=1
    g30: BSplineCurve PolesCount=3 KnotsCount=2 Degree=2 IsPeriodic=0
    g31: GeomPoint X=-7.19003 Y=-10 Z=0
    g32: GeomPoint X=-7.79258 Y=-12 Z=0
    g33: Circle CenterX=-8.70761 CenterY=-14 CenterZ=0 NormalX=0 NormalY=0 NormalZ=1 AngleXU=0 Radius=1
    g34: Circle CenterX=-9.33087 CenterY=-15.1837 CenterZ=0 NormalX=0 NormalY=0 NormalZ=1 AngleXU=0 Radius=1
    g35: Circle CenterX=-10.1571 CenterY=-16 CenterZ=0 NormalX=0 NormalY=0 NormalZ=1 AngleXU=0 Radius=1
    g36: BSplineCurve PolesCount=3 KnotsCount=2 Degree=2 IsPeriodic=0
    g37: GeomPoint X=-8.70761 Y=-14 Z=0
    g38: GeomPoint X=-10.1571 Y=-16 Z=0
    g39: Circle CenterX=-12.8401 CenterY=-17.6958 CenterZ=0 NormalX=0 NormalY=0 NormalZ=1 AngleXU=0 Radius=1
    g40: Circle CenterX=-13.3521 CenterY=-17.9027 CenterZ=0 NormalX=0 NormalY=0 NormalZ=1 AngleXU=0 Radius=1
    g41: Circle CenterX=-14 CenterY=-18 CenterZ=0 NormalX=0 NormalY=0 NormalZ=1 AngleXU=0 Radius=1
    g42: BSplineCurve PolesCount=3 KnotsCount=2 Degree=2 IsPeriodic=0
    g43: GeomPoint X=-12.8401 Y=-17.6958 Z=0
    g44: GeomPoint X=-14 Y=-18 Z=0
    g45: LineSegment StartX=-6.2 StartY=0 StartZ=0 EndX=-7.2 EndY=0 EndZ=0
    g46: LineSegment StartX=-7.2 StartY=0 StartZ=0 EndX=-7.2 EndY=-2 EndZ=0
    g47: LineSegment StartX=-7.2 StartY=-2 StartZ=0 EndX=-6.2215 EndY=-2 EndZ=0
    g48: LineSegment StartX=-6.32538 StartY=-4 StartZ=0 EndX=-7.65538 EndY=-4 EndZ=0
    g49: LineSegment StartX=-7.65538 StartY=-4 StartZ=0 EndX=-7.65538 EndY=-5.99526 EndZ=0
    g50: LineSegment StartX=-7.65538 StartY=-5.99526 StartZ=0 EndX=-6.48644 EndY=-5.99526 EndZ=0
    g51: LineSegment StartX=-6.77343 StartY=-8 StartZ=0 EndX=-8.43343 EndY=-8 EndZ=0
    g52: LineSegment StartX=-8.43343 StartY=-8 StartZ=0 EndX=-8.43343 EndY=-10 EndZ=0
    g53: LineSegment StartX=-8.43343 StartY=-10 StartZ=0 EndX=-7.19003 EndY=-10 EndZ=0
  constraints (112):
    c: Horizontal(g0)
    c: Distance(g0) = 2
    c: Block(g0)
    c: Vertical(g1)
    c: Coincident(g2,g0)
    c: Vertical(g2)
    c: Block(g2)
    c: Coincident(g6,g2)
    c: Weight(g3) = 1
    c: Equal(g3,g4)
    c: Equal(g3,g5)
    c: InternalAlignment(g3,g6)
    c: InternalAlignment(g4,g6)
    c: InternalAlignment(g5,g6)
    c: InternalAlignment(g7,g6)
    c: InternalAlignment(g8,g6)
    c: Block(g6)
    c: Coincident(g9,g1)
    c: Coincident(g9,g6)
    c: Horizontal(g9)
    c: Vertical(g10)
    c: Block(g10)
    c: Horizontal(g11)
    c: Block(g11)
    c: Coincident(g12,g10)
    c: Horizontal(g12)
    c: Block(g12)
    c: Coincident(g13,g11)
    c: Vertical(g13)
    c: Block(g13)
    c: Coincident(g14,g10)
    c: Horizontal(g14)
    c: Block(g14)
    c: Block(g9)
    c: Block(g1)
    c: Weight(g15) = 1
    c: Equal(g15,g16)
    c: Equal(g15,g17)
    c: InternalAlignment(g15,g18)
    c: InternalAlignment(g16,g18)
    c: InternalAlignment(g17,g18)
    c: InternalAlignment(g19,g18)
    c: InternalAlignment(g20,g18)
    c: Weight(g21) = 1
    c: Equal(g21,g22)
    c: Equal(g21,g23)
    c: InternalAlignment(g21,g24)
    c: InternalAlignment(g22,g24)
    c: InternalAlignment(g23,g24)
    c: InternalAlignment(g25,g24)
    c: InternalAlignment(g26,g24)
    c: Weight(g27) = 1
    c: Equal(g27,g28)
    c: Equal(g27,g29)
    c: Coincident(g30,g14)
    c: InternalAlignment(g27,g30)
    c: InternalAlignment(g28,g30)
    c: InternalAlignment(g29,g30)
    c: InternalAlignment(g31,g30)
    c: InternalAlignment(g32,g30)
    c: Coincident(g36,g12)
    c: Weight(g33) = 1
    c: Equal(g33,g34)
    c: Equal(g33,g35)
    c: Coincident(g36,g11)
    c: InternalAlignment(g33,g36)
    c: InternalAlignment(g34,g36)
    c: InternalAlignment(g35,g36)
    c: InternalAlignment(g37,g36)
    c: InternalAlignment(g38,g36)
    c: Coincident(g42,g13)
    c: Weight(g39) = 1
    c: Equal(g39,g40)
    c: Equal(g39,g41)
    c: Coincident(g42,g1)
    c: InternalAlignment(g39,g42)
    c: InternalAlignment(g40,g42)
    c: InternalAlignment(g41,g42)
    c: InternalAlignment(g43,g42)
    c: InternalAlignment(g44,g42)
    c: Block(g18)
    c: Block(g24)
    c: Block(g30)
    c: Block(g36)
    c: Block(g42)
    c: Horizontal(g45)
    c: Coincident(g45,g0)
    c: Vertical(g46)
    c: Coincident(g46,g45)
    c: Coincident(g47,g46)
    c: Coincident(g47,g18)
    c: Horizontal(g47)
    c: Block(g46)
    c: Coincident(g48,g18)
    c: Horizontal(g48)
    c: Distance(g48) = 1.33
    c: Vertical(g49)
    c: Coincident(g49,g48)
    c: Coincident(g50,g49)
    c: Coincident(g50,g24)
    c: Horizontal(g50)
    c: Tangent(g50,g22)
    c: Horizontal(g51)
    c: Coincident(g51,g24)
    c: Block(g51)
    c: Vertical(g52)
    c: Block(g52)
    c: Coincident(g52,g51)
    c: Coincident(g53,g52)
    c: Coincident(g53,g30)
    c: Horizontal(g53)
    c: Distance(g1) = 8.5
FEATURE [Part::Feature] Face024
  shape: bbox 9.8 x 26.5 x 2e-07 mm, 1 faces, 0 solids (baked)
FEATURE [Part::Revolution] Revolve024
  Angle = 360
  Axis = (0,1,0)
  Base = (0,0,0)
  FaceMakerClass = Part::FaceMakerBullseye
  Placement = pos=(0,0,0) rot=(0,0,1;1.5708rad)
  Solid = false
  Source = -> Face024
  Symmetric = false
FEATURE [Part::Feature] Face025
  shape: bbox 9.8 x 26.5 x 2e-07 mm, 1 faces, 0 solids (baked)
FEATURE [Part::Revolution] Revolve025
  Angle = 360
  Axis = (0,1,0)
  Base = (0,0,0)
  FaceMakerClass = Part::FaceMakerBullseye
  Placement = pos=(0,0,0) rot=(0,0,1;1.5708rad)
  Solid = false
  Source = -> Face025
  Symmetric = false
FEATURE [Part::MultiFuse] Fusion033
  Placement = pos=(-18,19,36) rot=(0,0,1;0rad)
  Shapes = -> [Revolve025,Revolve024]
FEATURE [Part::Cylinder] Cylinder014
  Angle = 360
  AttacherType = Attacher::AttachEngine3D
  Height = 20
  Placement = pos=(0,0,36.15) rot=(0,0,1;0rad)
  Radius = 14.3
FEATURE [Part::Cylinder] Cylinder015
  Angle = 360
  AttacherType = Attacher::AttachEngine3D
  Height = 10
  Placement = pos=(0,0,36.15) rot=(0,0,1;0rad)
  Radius = 4
FEATURE [Part::MultiFuse] Fusion034  label="removeToCreteHoleForPlugHousing004"
  Placement = pos=(-42,19,36) rot=(0,1,0;1.5708rad)
  Shapes = -> [Cylinder014,Cylinder015]
FEATURE [Part::Cut] Cut008  label="top004"
  Base = -> Cut004
  Placement = pos=(-1,0,0) rot=(0,0,1;0rad)
  Tool = -> Fusion034
FEATURE [Part::Box] Box005  label="Cube005"
  AttacherType = Attacher::AttachEngine3D
  Height = 28
  Length = 3
  Placement = pos=(110.7,19,22) rot=(0,0,1;0rad)
  Width = 15.7
FEATURE [Part::Cylinder] Cylinder016
  Angle = 360
  AttacherType = Attacher::AttachEngine3D
  Height = 10
  Placement = pos=(0,0,36.15) rot=(0,0,1;0rad)
  Radius = 4
FEATURE [Part::Cylinder] Cylinder017
  Angle = 360
  AttacherType = Attacher::AttachEngine3D
  Height = 20
  Placement = pos=(0,0,36.15) rot=(0,0,1;0rad)
  Radius = 10.3
FEATURE [Part::MultiFuse] Fusion035  label="removeToCreteHoleForPlugHousing005"
  Placement = pos=(70,19,36) rot=(0,1,0;1.5708rad)
  Shapes = -> [Cylinder017,Cylinder016]
FEATURE [Part::Cut] Cut009  label="plugHousingTab001"
  Base = -> Box005
  Placement = pos=(-107.4,-14,0) rot=(0,0,1;0rad)
  Tool = -> Fusion035
FEATURE [Part::Box] Box006  label="Cube006"
  AttacherType = Attacher::AttachEngine3D
  Height = 28
  Length = 3
  Placement = pos=(110.7,19,22) rot=(0,0,1;0rad)
  Width = 15.7
FEATURE [Part::Cylinder] Cylinder018
  Angle = 360
  AttacherType = Attacher::AttachEngine3D
  Height = 10
  Placement = pos=(0,0,36.15) rot=(0,0,1;0rad)
  Radius = 4
FEATURE [Part::Cylinder] Cylinder019
  Angle = 360
  AttacherType = Attacher::AttachEngine3D
  Height = 20
  Placement = pos=(0,0,36.15) rot=(0,0,1;0rad)
  Radius = 10.3
FEATURE [Part::MultiFuse] Fusion036  label="removeToCreteHoleForPlugHousing006"
  Placement = pos=(70,19,36) rot=(0,1,0;1.5708rad)
  Shapes = -> [Cylinder019,Cylinder018]
FEATURE [Part::Cut] Cut010  label="plugHousingTab002"
  Base = -> Box006
  Placement = pos=(-107.4,-14,0) rot=(0,0,1;0rad)
  Tool = -> Fusion036
FEATURE [Part::MultiFuse] Fusion037
  Placement = pos=(9.6,23,0) rot=(0,0,1;3.14159rad)
  Shapes = -> [Cut009,Cut010]
FEATURE [Part::Box] Box  label="Cube"
  AttacherType = Attacher::AttachEngine3D
  Height = 10
  Length = 3
  Placement = pos=(3.3,4,12) rot=(0,0,1;0rad)
  Width = 10
FEATURE [Part::Fillet] Fillet004
  Base = -> Fusion028
  Edges = 1 edges r=2: [Edge25]
FEATURE [Part::Fillet] Fillet005  label="plugHousing046"
  Base = -> Fillet004
  Edges = 1 edges r=2: [Edge8]
FEATURE [Part::Fillet] Fillet006
  Base = -> Box
  Edges = 1 edges r=2: [Edge11]
FEATURE [Part::Box] Box007  label="Cube007"
  AttacherType = Attacher::AttachEngine3D
  Height = 10
  Length = 3
  Placement = pos=(3.3,4,50) rot=(0,0,1;0rad)
  Width = 10
FEATURE [Part::Fillet] Fillet007
  Base = -> Box007
  Edges = 1 edges r=2: [Edge12]
FEATURE [Part::Box] Box008  label="Cube008"
  AttacherType = Attacher::AttachEngine3D
  Height = 28
  Length = 4
  Placement = pos=(5,0,22) rot=(0,0,1;0rad)
  Width = 10
FEATURE [Part::Fillet] Fillet008
  Base = -> Box008
  Edges = 1 edges r=1: [Edge7]
FEATURE [Part::Fillet] Fillet009
  Base = -> Fillet008
  Edges = 1 edges r=2: [Edge5]
FEATURE [Part::Fillet] Fillet010
  Base = -> Fillet009
  Edges = 1 edges r=2: [Edge2]
FEATURE [Sketcher::SketchObject] Sketch009  label="topSketch003"
  FullyConstrained = true
  sketch-geometry (4):
    g0: LineSegment StartX=16.8446 StartY=31.512 StartZ=0 EndX=16.3251 EndY=34.4666 EndZ=0
    g1: ArcOfCircle CenterX=19 CenterY=19.2524 CenterZ=0 NormalX=0 NormalY=0 NormalZ=1 AngleXU=0 Radius=15.4476 StartAngle=1.74483 EndAngle=2.72717
    g2: ArcOfCircle CenterX=19 CenterY=19.2524 CenterZ=0 NormalX=0 NormalY=0 NormalZ=1 AngleXU=0 Radius=12.4476 StartAngle=1.74483 EndAngle=2.73189
    g3: LineSegment StartX=4.86004 StartY=25.4725 StartZ=0 EndX=7.58253 EndY=24.2107 EndZ=0
  constraints (7):
    c: Block(g0)
    c: Coincident(g1,g0)
    c: Coincident(g2,g0)
    c: Coincident(g3,g1)
    c: Coincident(g3,g2)
    c: Block(g1)
    c: Block(g2)
FEATURE [Part::Extrusion] Extrude008
  Base = -> Sketch009
  Dir = (0,0,1)
  DirMode = 2
  FaceMakerClass = Part::FaceMakerBullseye
  LengthFwd = 10
  LengthRev = 0
  Placement = pos=(0,0,31) rot=(0,0,1;0rad)
  Solid = true
  Symmetric = false
FEATURE [Part::Cylinder] Cylinder020
  Angle = 360
  AttacherType = Attacher::AttachEngine3D
  Height = 20
  Placement = pos=(0,0,36.15) rot=(0,0,1;0rad)
  Radius = 8.2
FEATURE [Part::Cylinder] Cylinder021
  Angle = 360
  AttacherType = Attacher::AttachEngine3D
  Height = 10
  Placement = pos=(0,0,36.15) rot=(0,0,1;0rad)
  Radius = 4
FEATURE [Part::MultiFuse] Fusion038  label="removeToCreteHoleForPlugHousing007"
  Placement = pos=(-42,19,36) rot=(0,1,0;1.5708rad)
  Shapes = -> [Cylinder020,Cylinder021]
FEATURE [Part::Cut] Cut011
  Base = -> Extrude008
  Tool = -> Fusion038
FEATURE [Part::Fillet] Fillet011
  Base = -> Cut011
  Edges = 1 edges r=2: [Edge1]
FEATURE [Part::Fillet] Fillet012
  Base = -> Fillet011
  Edges = 1 edges r=2.5: [Edge1]
FEATURE [Part::Fillet] Fillet013
  Base = -> Fillet012
  Edges = 1 edges r=2.5: [Edge2]
FEATURE [Part::Box] Box010  label="Cube010"
  AttacherType = Attacher::AttachEngine3D
  Height = 16
  Length = 8
  Placement = pos=(12.7,31.52,28) rot=(0,0,1;0rad)
  Width = 4
FEATURE [Sketcher::SketchObject] Sketch010  label="topSketch004"
  FullyConstrained = true
  sketch-geometry (4):
    g0: LineSegment StartX=16.8446 StartY=31.512 StartZ=0 EndX=16.3251 EndY=34.4666 EndZ=0
    g1: ArcOfCircle CenterX=19 CenterY=19.2524 CenterZ=0 NormalX=0 NormalY=0 NormalZ=1 AngleXU=0 Radius=15.4476 StartAngle=1.74483 EndAngle=2.72717
    g2: ArcOfCircle CenterX=19 CenterY=19.2524 CenterZ=0 NormalX=0 NormalY=0 NormalZ=1 AngleXU=0 Radius=12.4476 StartAngle=1.74483 EndAngle=2.73189
    g3: LineSegment StartX=4.86004 StartY=25.4725 StartZ=0 EndX=7.58253 EndY=24.2107 EndZ=0
  constraints (7):
    c: Block(g0)
    c: Coincident(g1,g0)
    c: Coincident(g2,g0)
    c: Coincident(g3,g1)
    c: Coincident(g3,g2)
    c: Block(g1)
    c: Block(g2)
FEATURE [Part::Cylinder] Cylinder022
  Angle = 360
  AttacherType = Attacher::AttachEngine3D
  Height = 10
  Placement = pos=(0,0,36.15) rot=(0,0,1;0rad)
  Radius = 4
FEATURE [Sketcher::SketchObject] Sketch011  label="topSketch005"
  FullyConstrained = true
  sketch-geometry (4):
    g0: LineSegment StartX=16.8446 StartY=31.512 StartZ=0 EndX=16.3251 EndY=34.4666 EndZ=0
    g1: ArcOfCircle CenterX=19 CenterY=19.2524 CenterZ=0 NormalX=0 NormalY=0 NormalZ=1 AngleXU=0 Radius=15.4476 StartAngle=1.74483 EndAngle=2.72717
    g2: ArcOfCircle CenterX=19 CenterY=19.2524 CenterZ=0 NormalX=0 NormalY=0 NormalZ=1 AngleXU=0 Radius=12.4476 StartAngle=1.74483 EndAngle=2.73189
    g3: LineSegment StartX=4.86004 StartY=25.4725 StartZ=0 EndX=7.58253 EndY=24.2107 EndZ=0
  constraints (7):
    c: Block(g0)
    c: Coincident(g1,g0)
    c: Coincident(g2,g0)
    c: Coincident(g3,g1)
    c: Coincident(g3,g2)
    c: Block(g1)
    c: Block(g2)
FEATURE [Part::Extrusion] Extrude010
  Base = -> Sketch011
  Dir = (0,0,1)
  DirMode = 2
  FaceMakerClass = Part::FaceMakerBullseye
  LengthFwd = 10.6
  LengthRev = 0
  Placement = pos=(0,0,31) rot=(0,0,1;0rad)
  Solid = true
  Symmetric = false
FEATURE [Part::Cylinder] Cylinder023
  Angle = 360
  AttacherType = Attacher::AttachEngine3D
  Height = 20
  Placement = pos=(0,0,36.15) rot=(0,0,1;0rad)
  Radius = 8.2
FEATURE [Part::MultiFuse] Fusion039  label="removeToCreteHoleForPlugHousing008"
  Placement = pos=(-42,19,36) rot=(0,1,0;1.5708rad)
  Shapes = -> [Cylinder023,Cylinder022]
FEATURE [Part::Cut] Cut012
  Base = -> Extrude010
  Placement = pos=(0,0,-0.3) rot=(0,0,1;0rad)
  Tool = -> Fusion039
FEATURE [Part::Cut] Cut013
  Base = -> Box010
  Tool = -> Cut012
FEATURE [Part::Fillet] Fillet014
  Base = -> Cut013
  Edges = 1 edges r=0.7: [Edge13]
FEATURE [Part::Fillet] Fillet015
  Base = -> Fillet014
  Edges = 1 edges r=0.7: [Edge13]
FEATURE [Part::Fillet] Fillet016
  Base = -> Fillet015
  Edges = 1 edges r=0.7: [Edge16]
FEATURE [Part::Fillet] Fillet017
  Base = -> Fillet016
  Edges = 1 edges r=0.7: [Edge11]
FEATURE [Part::Fillet] Fillet018
  Base = -> Fillet017
  Edges = 1 edges r=0.7: [Edge10]
FEATURE [Part::Fillet] Fillet019
  Base = -> Fillet018
  Edges = 1 edges r=1.2: [Edge5]
FEATURE [Part::Fillet] Fillet020
  Base = -> Fillet019
  Edges = 1 edges r=1.2: [Edge12]
FEATURE [Part::Fillet] Fillet021
  Base = -> Fillet020
  Edges = 1 edges r=2: [Edge1]
  Placement = pos=(0.3,0,0) rot=(0,0,1;0rad)
FEATURE [Part::MultiFuse] Fusion040  label="top005"
  Shapes = -> [Cut008,Fillet021]
FEATURE [Part::MultiFuse] Fusion041  label="wireHolder"
  Shapes = -> [Fusion033,Fillet013]
FEATURE [Part::MultiFuse] Fusion042
  Shapes = -> [Fillet007,Fusion041]
FEATURE [Part::MultiFuse] Fusion043  label="wireHolder001"
  Shapes = -> [Fusion042,Fillet010]
FEATURE [Part::MultiFuse] Fusion044  label="wireHolder002"
  Shapes = -> [Fillet006,Fusion037,Fusion043]
FEATURE [Part::Feature] Face026
  shape: bbox 11 x 6 x 2e-07 mm, 1 faces, 0 solids (baked)
FEATURE [Part::Revolution] Revolve026
  Angle = 360
  Axis = (0,1,0)
  Base = (0,0,0)
  FaceMakerClass = Part::FaceMakerBullseye
  Placement = pos=(30.3,-1,19.7) rot=(0,0,1;0rad)
  Solid = false
  Source = -> Face026
  Symmetric = false
FEATURE [Sketcher::SketchObject] Sketch013  label="topSketch006"
  FullyConstrained = true
  sketch-geometry (13):
    g0: LineSegment StartX=117 StartY=19 StartZ=0 EndX=117 EndY=38 EndZ=0
    g1: ArcOfCircle CenterX=98 CenterY=19 CenterZ=0 NormalX=0 NormalY=0 NormalZ=1 AngleXU=0 Radius=19 StartAngle=5.7297 EndAngle=6.28319
    g2: LineSegment StartX=0 StartY=3 StartZ=0 EndX=0 EndY=19 EndZ=0
    g3: LineSegment StartX=19 StartY=38 StartZ=0 EndX=117 EndY=38 EndZ=0
    g4: ArcOfCircle CenterX=19 CenterY=19 CenterZ=0 NormalX=0 NormalY=0 NormalZ=1 AngleXU=0 Radius=19 StartAngle=1.5708 EndAngle=3.14159
    g5: ArcOfCircle CenterX=19 CenterY=19 CenterZ=0 NormalX=0 NormalY=0 NormalZ=1 AngleXU=0 Radius=16 StartAngle=1.5708 EndAngle=3.14159
    g6: ArcOfCircle CenterX=98 CenterY=19 CenterZ=0 NormalX=0 NormalY=0 NormalZ=1 AngleXU=0 Radius=16 StartAngle=5.60905 EndAngle=6.28319
    g7: LineSegment StartX=114 StartY=19 StartZ=0 EndX=114 EndY=35 EndZ=0
    g8: LineSegment StartX=110.5 StartY=9.01251 StartZ=0 EndX=114.163 EndY=9.01251 EndZ=0
    g9: LineSegment StartX=114 StartY=35 StartZ=0 EndX=19 EndY=35 EndZ=0
    g10: LineSegment StartX=0 StartY=3 StartZ=0 EndX=0 EndY=0 EndZ=0
    g11: LineSegment StartX=3 StartY=0 StartZ=0 EndX=0 EndY=0 EndZ=0
    g12: LineSegment StartX=3 StartY=19 StartZ=0 EndX=3 EndY=0 EndZ=0
  constraints (33):
    c: Vertical(g0)
    c: Distance(g0) = 19
    c: Block(g0)
    c: Coincident(g1,g0)
    c: Block(g1)
    c: Vertical(g2)
    c: Block(g2)
    c: Coincident(g3,g0)
    c: Horizontal(g3)
    c: Distance(g3) = 98
    c: Coincident(g4,g3)
    c: Coincident(g4,g2)
    c: Block(g4)
    c: Coincident(g5,g4)
    c: Coincident(g6,g1)
    c: Block(g6)
    c: Block(g5)
    c: Coincident(g7,g6)
    c: Vertical(g7)
    c: Coincident(g8,g6)
    c: Coincident(g8,g1)
    c: Coincident(g9,g7)
    c: Coincident(g9,g5)
    c: Horizontal(g9)
    c: Tangent(g9,g5)
    c: Coincident(g10,g2)
    c: Distance(g10) = 3
    c: Vertical(g10)
    c: Coincident(g11,g10)
    c: Horizontal(g11)
    c: Coincident(g12,g5)
    c: Coincident(g12,g11)
    c: Vertical(g12)
FEATURE [Part::Extrusion] Extrude011  label="top006"
  Base = -> Sketch013
  Dir = (0,0,1)
  DirMode = 2
  FaceMakerClass = Part::FaceMakerBullseye
  LengthFwd = 72
  LengthRev = 0
  Solid = true
  Symmetric = false
FEATURE [Sketcher::SketchObject] Sketch014
  FullyConstrained = true
  MapMode = 3
  Placement = pos=(0,0,0) rot=(1,0,0;1.5708rad)
  Support = -> [Extrude011]
  sketch-geometry (8):
    g0: Circle CenterX=80.351 CenterY=-67.6202 CenterZ=0 NormalX=0 NormalY=0 NormalZ=1 AngleXU=0 Radius=2
    g1: Circle CenterX=80.351 CenterY=-67.6202 CenterZ=0 NormalX=0 NormalY=0 NormalZ=1 AngleXU=0 Radius=3
    g2: Circle CenterX=80.351 CenterY=-4.92017 CenterZ=0 NormalX=0 NormalY=0 NormalZ=1 AngleXU=0 Radius=2
    g3: Circle CenterX=80.351 CenterY=-4.92017 CenterZ=0 NormalX=0 NormalY=0 NormalZ=1 AngleXU=0 Radius=3
    g4: Circle CenterX=23.851 CenterY=-4.92017 CenterZ=0 NormalX=0 NormalY=0 NormalZ=1 AngleXU=0 Radius=2
    g5: Circle CenterX=23.851 CenterY=-4.92017 CenterZ=0 NormalX=0 NormalY=0 NormalZ=1 AngleXU=0 Radius=3
    g6: Circle CenterX=23.851 CenterY=-67.6202 CenterZ=0 NormalX=0 NormalY=0 NormalZ=1 AngleXU=0 Radius=2
    g7: Circle CenterX=23.851 CenterY=-67.6202 CenterZ=0 NormalX=0 NormalY=0 NormalZ=1 AngleXU=0 Radius=3
  constraints (8):
    c: Block(g3)
    c: Block(g2)
    c: Block(g1)
    c: Block(g0)
    c: Block(g6)
    c: Block(g7)
    c: Block(g4)
    c: Block(g5)
FEATURE [Part::Feature] Face027
  shape: bbox 11 x 6 x 2e-07 mm, 1 faces, 0 solids (baked)
FEATURE [Part::Revolution] Revolve027
  Angle = 360
  Axis = (0,1,0)
  Base = (0,0,0)
  FaceMakerClass = Part::FaceMakerBullseye
  Placement = pos=(30.3,-1,51.7) rot=(0,0,1;0rad)
  Solid = false
  Source = -> Face027
  Symmetric = false
FEATURE [Part::Feature] Face028
  shape: bbox 11 x 6 x 2e-07 mm, 1 faces, 0 solids (baked)
FEATURE [Part::Revolution] Revolve028
  Angle = 360
  Axis = (0,1,0)
  Base = (0,0,0)
  FaceMakerClass = Part::FaceMakerBullseye
  Placement = pos=(62.3,-1,19.7) rot=(0,0,1;0rad)
  Solid = false
  Source = -> Face028
  Symmetric = false
FEATURE [Part::Feature] Face029
  shape: bbox 11 x 6 x 2e-07 mm, 1 faces, 0 solids (baked)
FEATURE [Part::Revolution] Revolve029
  Angle = 360
  Axis = (0,1,0)
  Base = (0,0,0)
  FaceMakerClass = Part::FaceMakerBullseye
  Placement = pos=(62.3,-1,51.7) rot=(0,0,1;0rad)
  Solid = false
  Source = -> Face029
  Symmetric = false
FEATURE [Part::Feature] Wire
  shape: bbox 11 x 5.2 x 2e-07 mm, 0 faces, 0 solids (baked)
FEATURE [Part::Revolution] Revolve030
  Angle = 360
  Axis = (0,1,0)
  Base = (0,0,0)
  FaceMakerClass = Part::FaceMakerBullseye
  Placement = pos=(30.3,38,19.7) rot=(0,0,1;0rad)
  Solid = true
  Source = -> Wire
  Symmetric = false
FEATURE [Part::Feature] Wire001
  shape: bbox 11 x 5.2 x 2e-07 mm, 0 faces, 0 solids (baked)
FEATURE [Part::Revolution] Revolve031
  Angle = 360
  Axis = (0,1,0)
  Base = (0,0,0)
  FaceMakerClass = Part::FaceMakerBullseye
  Placement = pos=(30.3,38,51.7) rot=(0,0,1;0rad)
  Solid = true
  Source = -> Wire001
  Symmetric = false
FEATURE [Part::Feature] Wire002
  shape: bbox 11 x 5.2 x 2e-07 mm, 0 faces, 0 solids (baked)
FEATURE [Part::Revolution] Revolve032
  Angle = 360
  Axis = (0,1,0)
  Base = (0,0,0)
  FaceMakerClass = Part::FaceMakerBullseye
  Placement = pos=(62.3,38,51.7) rot=(0,0,1;0rad)
  Solid = true
  Source = -> Wire002
  Symmetric = false
FEATURE [Part::Feature] Wire003
  shape: bbox 11 x 5.2 x 2e-07 mm, 0 faces, 0 solids (baked)
FEATURE [Part::Revolution] Revolve033
  Angle = 360
  Axis = (0,1,0)
  Base = (0,0,0)
  FaceMakerClass = Part::FaceMakerBullseye
  Placement = pos=(62.3,38,19.7) rot=(0,0,1;0rad)
  Solid = true
  Source = -> Wire003
  Symmetric = false
FEATURE [Part::MultiFuse] Fusion045  label="altRandScrewHousing"
  Shapes = -> [Revolve029,Revolve027,Revolve028,Revolve026]
FEATURE [Part::MultiFuse] Fusion046  label="fanScrewHousing"
  Shapes = -> [Revolve033,Revolve032,Revolve031,Revolve030]
FEATURE [Sketcher::SketchObject] Sketch015
  FullyConstrained = true
  sketch-geometry (17):
    g0: Circle CenterX=-3.5 CenterY=23.5 CenterZ=0 NormalX=0 NormalY=0 NormalZ=1 AngleXU=0 Radius=1
    g1: Circle CenterX=-1 CenterY=15.25 CenterZ=0 NormalX=0 NormalY=0 NormalZ=1 AngleXU=0 Radius=1
    g2: Circle CenterX=-3.5 CenterY=7 CenterZ=0 NormalX=0 NormalY=0 NormalZ=1 AngleXU=0 Radius=1
    g3: BSplineCurve PolesCount=3 KnotsCount=2 Degree=2 IsPeriodic=0
    g4: GeomPoint X=-3.5 Y=23.5 Z=0
    g5: GeomPoint X=-3.5 Y=7 Z=0
    g6: Circle CenterX=-4.8 CenterY=30.5 CenterZ=0 NormalX=0 NormalY=0 NormalZ=1 AngleXU=0 Radius=1
    g7: Circle CenterX=-3.5 CenterY=30.5 CenterZ=0 NormalX=0 NormalY=0 NormalZ=1 AngleXU=0 Radius=1
    g8: Circle CenterX=-3.5 CenterY=29.2 CenterZ=0 NormalX=0 NormalY=0 NormalZ=1 AngleXU=0 Radius=1
    g9: BSplineCurve PolesCount=3 KnotsCount=2 Degree=2 IsPeriodic=0
    g10: GeomPoint X=-4.8 Y=30.5 Z=0
    g11: GeomPoint X=-3.5 Y=29.2 Z=0
    g12: LineSegment StartX=-3.5 StartY=29.2 StartZ=0 EndX=-3.5 EndY=23.5 EndZ=0
    g13: LineSegment StartX=-4.8 StartY=30.5 StartZ=0 EndX=0 EndY=30.5 EndZ=0
    g14: LineSegment StartX=-3.5 StartY=0.3 StartZ=0 EndX=0 EndY=0.3 EndZ=0
    g15: LineSegment StartX=-3.5 StartY=0.3 StartZ=0 EndX=-3.5 EndY=7 EndZ=0
    g16: LineSegment StartX=0 StartY=0.3 StartZ=0 EndX=0 EndY=30.5 EndZ=0
  constraints (33):
    c: Weight(g0) = 1
    c: Equal(g0,g1)
    c: Equal(g0,g2)
    c: InternalAlignment(g0,g3)
    c: InternalAlignment(g1,g3)
    c: InternalAlignment(g2,g3)
    c: InternalAlignment(g4,g3)
    c: InternalAlignment(g5,g3)
    c: Block(g3)
    c: Weight(g6) = 1
    c: Equal(g6,g7)
    c: Equal(g6,g8)
    c: InternalAlignment(g6,g9)
    c: InternalAlignment(g7,g9)
    c: InternalAlignment(g8,g9)
    c: InternalAlignment(g10,g9)
    c: InternalAlignment(g11,g9)
    c: Block(g9)
    c: Coincident(g12,g9)
    c: Coincident(g12,g3)
    c: Vertical(g12)
    c: Coincident(g13,g9)
    c: Horizontal(g13)
    c: Distance(g13) = 4.8
    c: Horizontal(g14)
    c: Block(g14)
    c: Coincident(g15,g14)
    c: Coincident(g15,g3)
    c: Vertical(g15)
    c: Coincident(g16,g14)
    c: Coincident(g16,g13)
    c: Vertical(g16)
    c: Tangent(g16,g1)
FEATURE [Sketcher::SketchObject] Sketch016
  FullyConstrained = true
  sketch-geometry (16):
    g0: Circle CenterX=-3.5 CenterY=23.5 CenterZ=0 NormalX=0 NormalY=0 NormalZ=1 AngleXU=0 Radius=1
    g1: Circle CenterX=-1 CenterY=15.25 CenterZ=0 NormalX=0 NormalY=0 NormalZ=1 AngleXU=0 Radius=1
    g2: Circle CenterX=-3.5 CenterY=7 CenterZ=0 NormalX=0 NormalY=0 NormalZ=1 AngleXU=0 Radius=1
    g3: BSplineCurve PolesCount=3 KnotsCount=2 Degree=2 IsPeriodic=0
    g4: GeomPoint X=-3.5 Y=23.5 Z=0
    g5: GeomPoint X=-3.5 Y=7 Z=0
    g6: LineSegment StartX=-3.5 StartY=28.2 StartZ=0 EndX=-3.5 EndY=23.5 EndZ=0
    g7: LineSegment StartX=0 StartY=29.5 StartZ=0 EndX=0 EndY=30 EndZ=0
    g8: LineSegment StartX=-3.5 StartY=28.2 StartZ=0 EndX=-3.5 EndY=30 EndZ=0
    g9: LineSegment StartX=0 StartY=30 StartZ=0 EndX=0 EndY=30.5 EndZ=0
    g10: LineSegment StartX=0 StartY=30.5 StartZ=0 EndX=-3.5 EndY=30.5 EndZ=0
    g11: LineSegment StartX=-3.5 StartY=30.5 StartZ=0 EndX=-3.5 EndY=30 EndZ=0
    g12: LineSegment StartX=0 StartY=29.5 StartZ=0 EndX=0 EndY=5 EndZ=0
    g13: LineSegment StartX=-3.5 StartY=0.3 StartZ=0 EndX=-3.5 EndY=7 EndZ=0
    g14: LineSegment StartX=-3.5 StartY=0.3 StartZ=0 EndX=0 EndY=0.3 EndZ=0
    g15: LineSegment StartX=0 StartY=5 StartZ=0 EndX=0 EndY=0.3 EndZ=0
  constraints (39):
    c: Weight(g0) = 1
    c: Equal(g0,g1)
    c: Equal(g0,g2)
    c: InternalAlignment(g0,g3)
    c: InternalAlignment(g1,g3)
    c: InternalAlignment(g2,g3)
    c: InternalAlignment(g4,g3)
    c: InternalAlignment(g5,g3)
    c: Block(g3)
    c: Coincident(g6,g3)
    c: Vertical(g6)
    c: Vertical(g7)
    c: Distance(g7) = 0.5
    c: Coincident(g8,g6)
    c: Vertical(g8)
    c: Block(g6)
    c: Block(g7)
    c: Vertical(g9)
    c: Equal(g7,g9) = 0.5
    c: Block(g9)
    c: Coincident(g9,g7)
    c: Horizontal(g10)
    c: Coincident(g10,g9)
    c: Coincident(g11,g10)
    c: Coincident(g11,g8)
    c: Vertical(g11)
    c: Block(g11)
    c: Coincident(g12,g7)
    c: Vertical(g12)
    c: Coincident(g13,g3)
    c: Vertical(g13)
    c: Distance(g13) = 6.7
    c: Coincident(g14,g13)
    c: Horizontal(g14)
    c: Block(g14)
    c: Coincident(g15,g12)
    c: Coincident(g15,g14)
    c: Vertical(g15)
    c: Block(g15)
FEATURE [Sketcher::SketchObject] Sketch017
  FullyConstrained = true
  sketch-geometry (11):
    g0: LineSegment StartX=-3.5 StartY=1e-16 StartZ=0 EndX=-1.6 EndY=1e-16 EndZ=0
    g1: LineSegment StartX=-1.6 StartY=1e-16 StartZ=0 EndX=-1.6 EndY=1.5 EndZ=0
    g2: LineSegment StartX=-3.5 StartY=1.5 StartZ=0 EndX=-1.6 EndY=1.5 EndZ=0
    g3: LineSegment StartX=-3.5 StartY=1e-16 StartZ=0 EndX=-4.8 EndY=1e-16 EndZ=0
    g4: Circle CenterX=-3.5 CenterY=1.3 CenterZ=0 NormalX=0 NormalY=0 NormalZ=1 AngleXU=0 Radius=1
    g5: Circle CenterX=-3.5 CenterY=1e-16 CenterZ=0 NormalX=0 NormalY=0 NormalZ=1 AngleXU=0 Radius=1
    g6: Circle CenterX=-4.8 CenterY=1e-16 CenterZ=0 NormalX=0 NormalY=0 NormalZ=1 AngleXU=0 Radius=1
    g7: BSplineCurve PolesCount=3 KnotsCount=2 Degree=2 IsPeriodic=0
    g8: GeomPoint X=-3.5 Y=1.3 Z=0
    g9: GeomPoint X=-4.8 Y=1e-16 Z=0
    g10: LineSegment StartX=-3.5 StartY=1.3 StartZ=0 EndX=-3.5 EndY=1.5 EndZ=0
  constraints (24):
    c: Horizontal(g0)
    c: Distance(g0) = 1.9
    c: Block(g0)
    c: Coincident(g1,g0)
    c: Vertical(g1)
    c: Coincident(g2,g1)
    c: Horizontal(g2)
    c: Coincident(g3,g0)
    c: Horizontal(g3)
    c: Distance(g3) = 1.3
    c: Weight(g4) = 1
    c: Equal(g4,g5)
    c: Coincident(g5,g0)
    c: Equal(g4,g6)
    c: Coincident(g7,g3)
    c: InternalAlignment(g4,g7)
    c: InternalAlignment(g5,g7)
    c: InternalAlignment(g6,g7)
    c: InternalAlignment(g8,g7)
    c: InternalAlignment(g9,g7)
    c: Coincident(g10,g7)
    c: Coincident(g10,g2)
    c: Vertical(g10)
    c: Block(g10)
FEATURE [Part::Feature] Face035
  shape: bbox 3.2 x 1.5 x 2e-07 mm, 1 faces, 0 solids (baked)
FEATURE [Part::Revolution] Revolve039  label="backCaseScrewRetainer"
  Angle = 360
  Axis = (0,1,0)
  Base = (0,0,0)
  FaceMakerClass = Part::FaceMakerBullseye
  Placement = pos=(12.5,3,62) rot=(0,0,1;0rad)
  Solid = false
  Source = -> Face035
  Symmetric = false
FEATURE [Part::Feature] Face036
  shape: bbox 3.2 x 1.5 x 2e-07 mm, 1 faces, 0 solids (baked)
FEATURE [Part::Feature] Face039
  shape: bbox 4.8 x 30.2 x 2e-07 mm, 1 faces, 0 solids (baked)
FEATURE [Part::Revolution] Revolve043  label="frontCaseScrewPost002"
  Angle = 360
  Axis = (0,1,0)
  Base = (0,0,0)
  FaceMakerClass = Part::FaceMakerBullseye
  Placement = pos=(89.5,4.5,3.5) rot=(0,0,1;0rad)
  Solid = false
  Source = -> Face039
  Symmetric = false
FEATURE [Part::Feature] Face042
  shape: bbox 4.8 x 30.2 x 2e-07 mm, 1 faces, 0 solids (baked)
FEATURE [Part::Revolution] Revolve046  label="frontCaseScrewPost003"
  Angle = 360
  Axis = (0,1,0)
  Base = (0,0,0)
  FaceMakerClass = Part::FaceMakerBullseye
  Placement = pos=(89.5,4.5,68.5) rot=(0,0,1;0rad)
  Solid = false
  Source = -> Face042
  Symmetric = false
FEATURE [Part::Feature] Face043
  shape: bbox 3.2 x 1.5 x 2e-07 mm, 1 faces, 0 solids (baked)
FEATURE [Part::Revolution] Revolve047  label="frontCaseScrewRetainer002"
  Angle = 360
  Axis = (0,1,0)
  Base = (0,0,0)
  FaceMakerClass = Part::FaceMakerBullseye
  Placement = pos=(89.5,3,68.5) rot=(0,0,1;0rad)
  Solid = false
  Source = -> Face043
  Symmetric = false
FEATURE [Part::Feature] Face044
  shape: bbox 3.2 x 1.5 x 2e-07 mm, 1 faces, 0 solids (baked)
FEATURE [Part::Revolution] Revolve048  label="frontCaseScrewRetainer003"
  Angle = 360
  Axis = (0,1,0)
  Base = (0,0,0)
  FaceMakerClass = Part::FaceMakerBullseye
  Placement = pos=(89.5,3,3.5) rot=(0,0,1;0rad)
  Solid = false
  Source = -> Face044
  Symmetric = false
FEATURE [App::MeasureDistance] Distance002  label="Distance: 1.67 mm"
  Distance = 1.66921
  P1 = (99.2361,4.7524,71.7)
  P2 = (99.2347,6.42161,71.7)
FEATURE [Sketcher::SketchObject] Sketch018
  FullyConstrained = true
  sketch-geometry (7):
    g0: LineSegment StartX=0 StartY=0 StartZ=0 EndX=0 EndY=6 EndZ=0
    g1: Circle CenterX=0 CenterY=0 CenterZ=0 NormalX=0 NormalY=0 NormalZ=1 AngleXU=0 Radius=1
    g2: Circle CenterX=8 CenterY=6 CenterZ=0 NormalX=0 NormalY=0 NormalZ=1 AngleXU=0 Radius=1
    g3: BSplineCurve PolesCount=3 KnotsCount=2 Degree=2 IsPeriodic=0
    g4: GeomPoint X=0 Y=0 Z=0
    g5: GeomPoint X=8 Y=6 Z=0
    g6: LineSegment StartX=0 StartY=6 StartZ=0 EndX=8 EndY=6 EndZ=0
  constraints (14):
    c: Coincident(g0,g-1)
    c: Distance(g0) = 6
    c: Vertical(g0)
    c: Coincident(g3,g0)
    c: Weight(g1) = 1
    c: Equal(g1,g2)
    c: InternalAlignment(g1,g3)
    c: InternalAlignment(g2,g3)
    c: InternalAlignment(g4,g3)
    c: InternalAlignment(g5,g3)
    c: Block(g3)
    c: Coincident(g6,g0)
    c: Coincident(g6,g3)
    c: Horizontal(g6)
FEATURE [Part::Extrusion] Extrude012  label="caseScrewPillarBracket"
  Base = -> Sketch018
  Dir = (0,0,1)
  DirMode = 2
  FaceMakerClass = Part::FaceMakerBullseye
  LengthFwd = 2.4
  LengthRev = 0
  Placement = pos=(15.76,29,8.8) rot=(0,1,0;0rad)
  Solid = true
  Symmetric = false
FEATURE [Sketcher::SketchObject] Sketch019
  FullyConstrained = true
  sketch-geometry (7):
    g0: LineSegment StartX=0 StartY=0 StartZ=0 EndX=0 EndY=6 EndZ=0
    g1: Circle CenterX=0 CenterY=0 CenterZ=0 NormalX=0 NormalY=0 NormalZ=1 AngleXU=0 Radius=1
    g2: Circle CenterX=8 CenterY=6 CenterZ=0 NormalX=0 NormalY=0 NormalZ=1 AngleXU=0 Radius=1
    g3: BSplineCurve PolesCount=3 KnotsCount=2 Degree=2 IsPeriodic=0
    g4: GeomPoint X=0 Y=0 Z=0
    g5: GeomPoint X=8 Y=6 Z=0
    g6: LineSegment StartX=0 StartY=6 StartZ=0 EndX=8 EndY=6 EndZ=0
  constraints (14):
    c: Coincident(g0,g-1)
    c: Distance(g0) = 6
    c: Vertical(g0)
    c: Coincident(g3,g0)
    c: Weight(g1) = 1
    c: Equal(g1,g2)
    c: InternalAlignment(g1,g3)
    c: InternalAlignment(g2,g3)
    c: InternalAlignment(g4,g3)
    c: InternalAlignment(g5,g3)
    c: Block(g3)
    c: Coincident(g6,g0)
    c: Coincident(g6,g3)
    c: Horizontal(g6)
FEATURE [Part::Extrusion] Extrude013  label="caseScrewPillarBracket001"
  Base = -> Sketch019
  Dir = (0,0,1)
  DirMode = 2
  FaceMakerClass = Part::FaceMakerBullseye
  LengthFwd = 2.4
  LengthRev = 0
  Placement = pos=(15.76,29,60.8) rot=(0,0,1;0rad)
  Solid = true
  Symmetric = false
FEATURE [Sketcher::SketchObject] Sketch020
  FullyConstrained = true
  sketch-geometry (7):
    g0: LineSegment StartX=0 StartY=0 StartZ=0 EndX=0 EndY=6 EndZ=0
    g1: Circle CenterX=0 CenterY=0 CenterZ=0 NormalX=0 NormalY=0 NormalZ=1 AngleXU=0 Radius=1
    g2: Circle CenterX=8 CenterY=6 CenterZ=0 NormalX=0 NormalY=0 NormalZ=1 AngleXU=0 Radius=1
    g3: BSplineCurve PolesCount=3 KnotsCount=2 Degree=2 IsPeriodic=0
    g4: GeomPoint X=0 Y=0 Z=0
    g5: GeomPoint X=8 Y=6 Z=0
    g6: LineSegment StartX=0 StartY=6 StartZ=0 EndX=8 EndY=6 EndZ=0
  constraints (14):
    c: Coincident(g0,g-1)
    c: Distance(g0) = 6
    c: Vertical(g0)
    c: Coincident(g3,g0)
    c: Weight(g1) = 1
    c: Equal(g1,g2)
    c: InternalAlignment(g1,g3)
    c: InternalAlignment(g2,g3)
    c: InternalAlignment(g4,g3)
    c: InternalAlignment(g5,g3)
    c: Block(g3)
    c: Coincident(g6,g0)
    c: Coincident(g6,g3)
    c: Horizontal(g6)
FEATURE [Part::Extrusion] Extrude014  label="caseScrewPillarBracket002"
  Base = -> Sketch020
  Dir = (0,0,1)
  DirMode = 2
  FaceMakerClass = Part::FaceMakerBullseye
  LengthFwd = 2.4
  LengthRev = 0
  Placement = pos=(13.7,29,13.26) rot=(0,-1,0;1.5708rad)
  Solid = true
  Symmetric = false
FEATURE [Sketcher::SketchObject] Sketch021
  FullyConstrained = true
  sketch-geometry (7):
    g0: LineSegment StartX=0 StartY=0 StartZ=0 EndX=0 EndY=6 EndZ=0
    g1: Circle CenterX=0 CenterY=0 CenterZ=0 NormalX=0 NormalY=0 NormalZ=1 AngleXU=0 Radius=1
    g2: Circle CenterX=8 CenterY=6 CenterZ=0 NormalX=0 NormalY=0 NormalZ=1 AngleXU=0 Radius=1
    g3: BSplineCurve PolesCount=3 KnotsCount=2 Degree=2 IsPeriodic=0
    g4: GeomPoint X=0 Y=0 Z=0
    g5: GeomPoint X=8 Y=6 Z=0
    g6: LineSegment StartX=0 StartY=6 StartZ=0 EndX=8 EndY=6 EndZ=0
  constraints (14):
    c: Coincident(g0,g-1)
    c: Distance(g0) = 6
    c: Vertical(g0)
    c: Coincident(g3,g0)
    c: Weight(g1) = 1
    c: Equal(g1,g2)
    c: InternalAlignment(g1,g3)
    c: InternalAlignment(g2,g3)
    c: InternalAlignment(g4,g3)
    c: InternalAlignment(g5,g3)
    c: Block(g3)
    c: Coincident(g6,g0)
    c: Coincident(g6,g3)
    c: Horizontal(g6)
FEATURE [Part::Extrusion] Extrude015  label="caseScrewPillarBracket003"
  Base = -> Sketch021
  Dir = (0,0,1)
  DirMode = 2
  FaceMakerClass = Part::FaceMakerBullseye
  LengthFwd = 2.4
  LengthRev = 0
  Placement = pos=(11.3,29,58.74) rot=(0,1,0;1.5708rad)
  Solid = true
  Symmetric = false
FEATURE [Sketcher::SketchObject] Sketch022
  FullyConstrained = true
  sketch-geometry (7):
    g0: LineSegment StartX=0 StartY=0 StartZ=0 EndX=0 EndY=6 EndZ=0
    g1: Circle CenterX=0 CenterY=0 CenterZ=0 NormalX=0 NormalY=0 NormalZ=1 AngleXU=0 Radius=1
    g2: Circle CenterX=8 CenterY=6 CenterZ=0 NormalX=0 NormalY=0 NormalZ=1 AngleXU=0 Radius=1
    g3: BSplineCurve PolesCount=3 KnotsCount=2 Degree=2 IsPeriodic=0
    g4: GeomPoint X=0 Y=0 Z=0
    g5: GeomPoint X=8 Y=6 Z=0
    g6: LineSegment StartX=0 StartY=6 StartZ=0 EndX=8 EndY=6 EndZ=0
  constraints (14):
    c: Coincident(g0,g-1)
    c: Distance(g0) = 6
    c: Vertical(g0)
    c: Coincident(g3,g0)
    c: Weight(g1) = 1
    c: Equal(g1,g2)
    c: InternalAlignment(g1,g3)
    c: InternalAlignment(g2,g3)
    c: InternalAlignment(g4,g3)
    c: InternalAlignment(g5,g3)
    c: Block(g3)
    c: Coincident(g6,g0)
    c: Coincident(g6,g3)
    c: Horizontal(g6)
FEATURE [Part::Extrusion] Extrude016  label="caseScrewPillarBracket004"
  Base = -> Sketch022
  Dir = (0,0,1)
  DirMode = 2
  FaceMakerClass = Part::FaceMakerBullseye
  LengthFwd = 2.4
  LengthRev = 0
  Placement = pos=(88.3,29,65.23) rot=(0,1,0;1.5708rad)
  Solid = true
  Symmetric = false
FEATURE [Sketcher::SketchObject] Sketch023
  FullyConstrained = true
  sketch-geometry (7):
    g0: LineSegment StartX=0 StartY=0 StartZ=0 EndX=0 EndY=6 EndZ=0
    g1: Circle CenterX=0 CenterY=0 CenterZ=0 NormalX=0 NormalY=0 NormalZ=1 AngleXU=0 Radius=1
    g2: Circle CenterX=8 CenterY=6 CenterZ=0 NormalX=0 NormalY=0 NormalZ=1 AngleXU=0 Radius=1
    g3: BSplineCurve PolesCount=3 KnotsCount=2 Degree=2 IsPeriodic=0
    g4: GeomPoint X=0 Y=0 Z=0
    g5: GeomPoint X=8 Y=6 Z=0
    g6: LineSegment StartX=0 StartY=6 StartZ=0 EndX=8 EndY=6 EndZ=0
  constraints (14):
    c: Coincident(g0,g-1)
    c: Distance(g0) = 6
    c: Vertical(g0)
    c: Coincident(g3,g0)
    c: Weight(g1) = 1
    c: Equal(g1,g2)
    c: InternalAlignment(g1,g3)
    c: InternalAlignment(g2,g3)
    c: InternalAlignment(g4,g3)
    c: InternalAlignment(g5,g3)
    c: Block(g3)
    c: Coincident(g6,g0)
    c: Coincident(g6,g3)
    c: Horizontal(g6)
FEATURE [Part::Extrusion] Extrude017  label="caseScrewPillarBracket005"
  Base = -> Sketch023
  Dir = (0,0,1)
  DirMode = 2
  FaceMakerClass = Part::FaceMakerBullseye
  LengthFwd = 2.4
  LengthRev = 0
  Placement = pos=(90.7,29,6.77) rot=(0,-1,0;1.5708rad)
  Solid = true
  Symmetric = false
FEATURE [Sketcher::SketchObject] Sketch024
  FullyConstrained = true
  sketch-geometry (7):
    g0: LineSegment StartX=0 StartY=0 StartZ=0 EndX=0 EndY=6 EndZ=0
    g1: Circle CenterX=0 CenterY=0 CenterZ=0 NormalX=0 NormalY=0 NormalZ=1 AngleXU=0 Radius=1
    g2: Circle CenterX=8 CenterY=6 CenterZ=0 NormalX=0 NormalY=0 NormalZ=1 AngleXU=0 Radius=1
    g3: BSplineCurve PolesCount=3 KnotsCount=2 Degree=2 IsPeriodic=0
    g4: GeomPoint X=0 Y=0 Z=0
    g5: GeomPoint X=8 Y=6 Z=0
    g6: LineSegment StartX=0 StartY=6 StartZ=0 EndX=8 EndY=6 EndZ=0
  constraints (14):
    c: Coincident(g0,g-1)
    c: Distance(g0) = 6
    c: Vertical(g0)
    c: Coincident(g3,g0)
    c: Weight(g1) = 1
    c: Equal(g1,g2)
    c: InternalAlignment(g1,g3)
    c: InternalAlignment(g2,g3)
    c: InternalAlignment(g4,g3)
    c: InternalAlignment(g5,g3)
    c: Block(g3)
    c: Coincident(g6,g0)
    c: Coincident(g6,g3)
    c: Horizontal(g6)
FEATURE [Part::Extrusion] Extrude018  label="caseScrewPillarBracket006"
  Base = -> Sketch024
  Dir = (0,0,1)
  DirMode = 2
  FaceMakerClass = Part::FaceMakerBullseye
  LengthFwd = 2.4
  LengthRev = 0
  Placement = pos=(103.7,29,6.77) rot=(0,-1,0;1.5708rad)
  Solid = true
  Symmetric = false
FEATURE [Sketcher::SketchObject] Sketch025
  FullyConstrained = true
  sketch-geometry (7):
    g0: LineSegment StartX=0 StartY=0 StartZ=0 EndX=0 EndY=6 EndZ=0
    g1: Circle CenterX=0 CenterY=0 CenterZ=0 NormalX=0 NormalY=0 NormalZ=1 AngleXU=0 Radius=1
    g2: Circle CenterX=8 CenterY=6 CenterZ=0 NormalX=0 NormalY=0 NormalZ=1 AngleXU=0 Radius=1
    g3: BSplineCurve PolesCount=3 KnotsCount=2 Degree=2 IsPeriodic=0
    g4: GeomPoint X=0 Y=0 Z=0
    g5: GeomPoint X=8 Y=6 Z=0
    g6: LineSegment StartX=0 StartY=6 StartZ=0 EndX=8 EndY=6 EndZ=0
  constraints (14):
    c: Coincident(g0,g-1)
    c: Distance(g0) = 6
    c: Vertical(g0)
    c: Coincident(g3,g0)
    c: Weight(g1) = 1
    c: Equal(g1,g2)
    c: InternalAlignment(g1,g3)
    c: InternalAlignment(g2,g3)
    c: InternalAlignment(g4,g3)
    c: InternalAlignment(g5,g3)
    c: Block(g3)
    c: Coincident(g6,g0)
    c: Coincident(g6,g3)
    c: Horizontal(g6)
FEATURE [Part::Extrusion] Extrude019  label="caseScrewPillarBracket007"
  Base = -> Sketch025
  Dir = (0,0,1)
  DirMode = 2
  FaceMakerClass = Part::FaceMakerBullseye
  LengthFwd = 2.4
  LengthRev = 0
  Placement = pos=(101.3,29,65.23) rot=(0,1,0;1.5708rad)
  Solid = true
  Symmetric = false
FEATURE [Part::Box] Box011  label="frontCaseScrewPillarBracket"
  AttacherType = Attacher::AttachEngine3D
  Height = 2.4
  Length = 16
  Placement = pos=(87,28,2.3) rot=(0,0,1;0rad)
  Width = 7
FEATURE [Part::Box] Box012  label="frontCaseScrewPillarBracket001"
  AttacherType = Attacher::AttachEngine3D
  Height = 2.4
  Length = 16
  Placement = pos=(87,28,67.3) rot=(0,0,1;0rad)
  Width = 7
FEATURE [Sketcher::SketchObject] Sketch026
  FullyConstrained = true
  sketch-geometry (17):
    g0: Circle CenterX=-3.5 CenterY=23.5 CenterZ=0 NormalX=0 NormalY=0 NormalZ=1 AngleXU=0 Radius=1
    g1: Circle CenterX=-1 CenterY=15.25 CenterZ=0 NormalX=0 NormalY=0 NormalZ=1 AngleXU=0 Radius=1
    g2: Circle CenterX=-3.5 CenterY=7 CenterZ=0 NormalX=0 NormalY=0 NormalZ=1 AngleXU=0 Radius=1
    g3: BSplineCurve PolesCount=3 KnotsCount=2 Degree=2 IsPeriodic=0
    g4: GeomPoint X=-3.5 Y=23.5 Z=0
    g5: GeomPoint X=-3.5 Y=7 Z=0
    g6: Circle CenterX=-4.8 CenterY=30.5 CenterZ=0 NormalX=0 NormalY=0 NormalZ=1 AngleXU=0 Radius=1
    g7: Circle CenterX=-3.5 CenterY=30.5 CenterZ=0 NormalX=0 NormalY=0 NormalZ=1 AngleXU=0 Radius=1
    g8: Circle CenterX=-3.5 CenterY=29.2 CenterZ=0 NormalX=0 NormalY=0 NormalZ=1 AngleXU=0 Radius=1
    g9: BSplineCurve PolesCount=3 KnotsCount=2 Degree=2 IsPeriodic=0
    g10: GeomPoint X=-4.8 Y=30.5 Z=0
    g11: GeomPoint X=-3.5 Y=29.2 Z=0
    g12: LineSegment StartX=-3.5 StartY=29.2 StartZ=0 EndX=-3.5 EndY=23.5 EndZ=0
    g13: LineSegment StartX=-4.8 StartY=30.5 StartZ=0 EndX=0 EndY=30.5 EndZ=0
    g14: LineSegment StartX=-3.5 StartY=5 StartZ=0 EndX=-3.5 EndY=7 EndZ=0
    g15: LineSegment StartX=0 StartY=5 StartZ=0 EndX=0 EndY=30.5 EndZ=0
    g16: LineSegment StartX=-3.5 StartY=5 StartZ=0 EndX=0 EndY=5 EndZ=0
  constraints (33):
    c: Weight(g0) = 1
    c: Equal(g0,g1)
    c: Equal(g0,g2)
    c: InternalAlignment(g0,g3)
    c: InternalAlignment(g1,g3)
    c: InternalAlignment(g2,g3)
    c: InternalAlignment(g4,g3)
    c: InternalAlignment(g5,g3)
    c: Block(g3)
    c: Weight(g6) = 1
    c: Equal(g6,g7)
    c: Equal(g6,g8)
    c: InternalAlignment(g6,g9)
    c: InternalAlignment(g7,g9)
    c: InternalAlignment(g8,g9)
    c: InternalAlignment(g10,g9)
    c: InternalAlignment(g11,g9)
    c: Block(g9)
    c: Coincident(g12,g9)
    c: Coincident(g12,g3)
    c: Vertical(g12)
    c: Coincident(g13,g9)
    c: Horizontal(g13)
    c: Distance(g13) = 4.8
    c: Coincident(g14,g3)
    c: Vertical(g14)
    c: Coincident(g15,g13)
    c: Vertical(g15)
    c: Tangent(g15,g1)
    c: Distance(g14) = 2
    c: Coincident(g16,g14)
    c: Horizontal(g16)
    c: Coincident(g15,g16)
FEATURE [Part::Feature] Face050
  shape: bbox 4.8 x 25.5 x 2e-07 mm, 1 faces, 0 solids (baked)
FEATURE [Part::Revolution] Revolve054  label="moreFrontCaseScrewPost001"
  Angle = 360
  Axis = (0,1,0)
  Base = (0,0,0)
  FaceMakerClass = Part::FaceMakerBullseye
  Placement = pos=(102.5,4.5,3.5) rot=(0,0,1;0rad)
  Solid = false
  Source = -> Face050
  Symmetric = false
FEATURE [Part::Feature] Face051
  shape: bbox 4.8 x 25.5 x 2e-07 mm, 1 faces, 0 solids (baked)
FEATURE [Part::Revolution] Revolve055  label="moreFrontCaseScrewPost002"
  Angle = 360
  Axis = (0,1,0)
  Base = (0,0,0)
  FaceMakerClass = Part::FaceMakerBullseye
  Placement = pos=(102.5,4.5,68.5) rot=(0,0,1;0rad)
  Solid = false
  Source = -> Face051
  Symmetric = false
FEATURE [Sketcher::SketchObject] Sketch027
  FullyConstrained = true
  sketch-geometry (10):
    g0: LineSegment StartX=-1.6 StartY=4.7 StartZ=0 EndX=-1.6 EndY=1.7 EndZ=0
    g1: LineSegment StartX=-3.5 StartY=4.7 StartZ=0 EndX=-1.6 EndY=4.7 EndZ=0
    g2: LineSegment StartX=-1.6 StartY=1.7 StartZ=0 EndX=-1.6 EndY=1.5 EndZ=0
    g3: LineSegment StartX=-1.6 StartY=1.5 StartZ=0 EndX=-5.2 EndY=1.5 EndZ=0
    g4: Circle CenterX=-3.5 CenterY=4.7 CenterZ=0 NormalX=0 NormalY=0 NormalZ=1 AngleXU=0 Radius=1
    g5: Circle CenterX=-3.59627 CenterY=2.99743 CenterZ=0 NormalX=0 NormalY=0 NormalZ=1 AngleXU=0 Radius=1
    g6: Circle CenterX=-5.2 CenterY=1.5 CenterZ=0 NormalX=0 NormalY=0 NormalZ=1 AngleXU=0 Radius=1
    g7: BSplineCurve PolesCount=3 KnotsCount=2 Degree=2 IsPeriodic=0
    g8: GeomPoint X=-3.5 Y=4.7 Z=0
    g9: GeomPoint X=-5.2 Y=1.5 Z=0
  constraints (23):
    c: Vertical(g0)
    c: Distance(g0) = 3
    c: Coincident(g1,g0)
    c: Horizontal(g1)
    c: Block(g0)
    c: Block(g1)
    c: Coincident(g2,g0)
    c: Vertical(g2)
    c: Distance(g2) = 0.2
    c: Coincident(g3,g2)
    c: Horizontal(g3)
    c: Block(g3)
    c: Coincident(g7,g1)
    c: Weight(g4) = 1
    c: Equal(g4,g5)
    c: Equal(g4,g6)
    c: Coincident(g7,g3)
    c: InternalAlignment(g4,g7)
    c: InternalAlignment(g5,g7)
    c: InternalAlignment(g6,g7)
    c: InternalAlignment(g8,g7)
    c: InternalAlignment(g9,g7)
    c: Block(g7)
FEATURE [Sketcher::SketchObject] Sketch028
  FullyConstrained = true
  sketch-geometry (18):
    g0: LineSegment StartX=0 StartY=3e-16 StartZ=0 EndX=0 EndY=1.7 EndZ=0
    g1: LineSegment StartX=-3.5 StartY=0 StartZ=0 EndX=-3.5 EndY=0.9 EndZ=0
    g2: Circle CenterX=-2.7 CenterY=1.7 CenterZ=0 NormalX=0 NormalY=0 NormalZ=1 AngleXU=0 Radius=1
    g3: Circle CenterX=-3.5 CenterY=1.7 CenterZ=0 NormalX=0 NormalY=0 NormalZ=1 AngleXU=0 Radius=1
    g4: Circle CenterX=-3.5 CenterY=0.9 CenterZ=0 NormalX=0 NormalY=0 NormalZ=1 AngleXU=0 Radius=1
    g5: BSplineCurve PolesCount=3 KnotsCount=2 Degree=2 IsPeriodic=0
    g6: GeomPoint X=-2.7 Y=1.7 Z=0
    g7: GeomPoint X=-3.5 Y=0.9 Z=0
    g8: LineSegment StartX=-3.5 StartY=0 StartZ=0 EndX=-3.5 EndY=-7 EndZ=0
    g9: LineSegment StartX=0 StartY=3e-16 StartZ=0 EndX=0 EndY=-7 EndZ=0
    g10: LineSegment StartX=-3.5 StartY=-7 StartZ=0 EndX=0 EndY=-7 EndZ=0
    g11: LineSegment StartX=-2.7 StartY=1.7 StartZ=0 EndX=-1.6 EndY=1.7 EndZ=0
    g12: LineSegment StartX=0 StartY=1.7 StartZ=0 EndX=0 EndY=4.5 EndZ=0
    g13: LineSegment StartX=0 StartY=4.5 StartZ=0 EndX=0 EndY=10.8 EndZ=0
    g14: LineSegment StartX=0 StartY=10.8 StartZ=0 EndX=-2 EndY=10.8 EndZ=0
    g15: LineSegment StartX=-1.6 StartY=4.7 StartZ=0 EndX=-1.6 EndY=1.7 EndZ=0
    g16: LineSegment StartX=-1.6 StartY=4.7 StartZ=0 EndX=-2 EndY=4.7 EndZ=0
    g17: LineSegment StartX=-2 StartY=4.7 StartZ=0 EndX=-2 EndY=10.8 EndZ=0
  constraints (44):
    c: Vertical(g0)
    c: Vertical(g1)
    c: Distance(g1) = 0.9
    c: Block(g0)
    c: Distance(g0) = 1.7
    c: Weight(g2) = 1
    c: Equal(g2,g3)
    c: Equal(g2,g4)
    c: Coincident(g5,g1)
    c: InternalAlignment(g2,g5)
    c: InternalAlignment(g3,g5)
    c: InternalAlignment(g4,g5)
    c: InternalAlignment(g6,g5)
    c: InternalAlignment(g7,g5)
    c: Block(g5)
    c: Coincident(g8,g1)
    c: Vertical(g8)
    c: Distance(g8) = 7
    c: Vertical(g9)
    c: Equal(g8,g9) = 7
    c: Coincident(g9,g0)
    c: Coincident(g10,g8)
    c: Coincident(g10,g9)
    c: Horizontal(g10)
    c: Coincident(g11,g5)
    c: Horizontal(g11)
    c: Coincident(g12,g0)
    c: Vertical(g12)
    c: Distance(g12) = 2.8
    c: Coincident(g13,g12)
    c: Vertical(g13)
    c: Distance(g13) = 6.3
    c: Coincident(g14,g13)
    c: Horizontal(g14)
    c: Distance(g14) = 2
    c: Vertical(g15)
    c: Distance(g15) = 3
    c: Block(g11)
    c: Coincident(g15,g11)
    c: Coincident(g16,g15)
    c: Horizontal(g16)
    c: Coincident(g17,g16)
    c: Coincident(g17,g14)
    c: Vertical(g17)
FEATURE [Part::Revolution] Revolve040  label="backCaseScrewRetainer001"
  Angle = 360
  Axis = (0,1,0)
  Base = (0,0,0)
  FaceMakerClass = Part::FaceMakerBullseye
  Placement = pos=(12.5,3,10) rot=(0,0,1;0rad)
  Solid = false
  Source = -> Face036
  Symmetric = false
FEATURE [Part::Feature] Face055
  shape: bbox 3.5 x 30.2 x 2e-07 mm, 1 faces, 0 solids (baked)
FEATURE [Part::Revolution] Revolve059  label="backCaseScrewPost"
  Angle = 360
  Axis = (0,1,0)
  Base = (0,0,0)
  FaceMakerClass = Part::FaceMakerBullseye
  Placement = pos=(12.5,4.5,10) rot=(0,0,1;0rad)
  Solid = false
  Source = -> Face055
  Symmetric = false
FEATURE [Part::Feature] Face056
  shape: bbox 3.5 x 30.2 x 2e-07 mm, 1 faces, 0 solids (baked)
FEATURE [Part::Revolution] Revolve060  label="backCaseScrewPost001"
  Angle = 360
  Axis = (0,1,0)
  Base = (0,0,0)
  FaceMakerClass = Part::FaceMakerBullseye
  Placement = pos=(12.5,4.5,62) rot=(0,0,1;0rad)
  Solid = false
  Source = -> Face056
  Symmetric = false
FEATURE [Part::Feature] Face057
  shape: bbox 3.5 x 17.8 x 2e-07 mm, 1 faces, 0 solids (baked)
FEATURE [Part::Revolution] Revolve061  label="removeToCreateScrewAndThreadedInsertHole"
  Angle = 360
  Axis = (0,1,0)
  Base = (0,0,0)
  FaceMakerClass = Part::FaceMakerBullseye
  Placement = pos=(12.5,0,10) rot=(0,0,1;0rad)
  Solid = false
  Source = -> Face057
  Symmetric = false
FEATURE [Part::Feature] Face058
  shape: bbox 3.5 x 17.8 x 2e-07 mm, 1 faces, 0 solids (baked)
FEATURE [Part::Revolution] Revolve062  label="removeToCreateScrewAndThreadedInsertHole001"
  Angle = 360
  Axis = (0,1,0)
  Base = (0,0,0)
  FaceMakerClass = Part::FaceMakerBullseye
  Placement = pos=(12.5,0,62) rot=(0,0,1;0rad)
  Solid = false
  Source = -> Face058
  Symmetric = false
FEATURE [Part::Feature] Face059
  shape: bbox 3.5 x 17.8 x 2e-07 mm, 1 faces, 0 solids (baked)
FEATURE [Part::Revolution] Revolve063  label="removeToCreateScrewAndThreadedInsertHole002"
  Angle = 360
  Axis = (0,1,0)
  Base = (0,0,0)
  FaceMakerClass = Part::FaceMakerBullseye
  Placement = pos=(89.5,0,68.5) rot=(0,0,1;0rad)
  Solid = false
  Source = -> Face059
  Symmetric = false
FEATURE [Part::Feature] Face060
  shape: bbox 3.5 x 17.8 x 2e-07 mm, 1 faces, 0 solids (baked)
FEATURE [Part::Revolution] Revolve064  label="removeToCreateScrewAndThreadedInsertHole003"
  Angle = 360
  Axis = (0,1,0)
  Base = (0,0,0)
  FaceMakerClass = Part::FaceMakerBullseye
  Placement = pos=(89.5,0,3.5) rot=(0,0,1;0rad)
  Solid = false
  Source = -> Face060
  Symmetric = false
FEATURE [Part::Feature] Face061
  shape: bbox 3.5 x 17.8 x 2e-07 mm, 1 faces, 0 solids (baked)
FEATURE [Part::Revolution] Revolve065  label="removeToCreateScrewAndThreadedInsertHole004"
  Angle = 360
  Axis = (0,1,0)
  Base = (0,0,0)
  FaceMakerClass = Part::FaceMakerBullseye
  Placement = pos=(102.5,4.7,3.5) rot=(0,0,1;0rad)
  Solid = false
  Source = -> Face061
  Symmetric = false
FEATURE [Part::Feature] Face062
  shape: bbox 3.5 x 17.8 x 2e-07 mm, 1 faces, 0 solids (baked)
FEATURE [Part::Revolution] Revolve066  label="removeToCreateScrewAndThreadedInsertHole005"
  Angle = 360
  Axis = (0,1,0)
  Base = (0,0,0)
  FaceMakerClass = Part::FaceMakerBullseye
  Placement = pos=(102.5,4.7,68.5) rot=(0,0,1;0rad)
  Solid = false
  Source = -> Face062
  Symmetric = false
FEATURE [Part::MultiFuse] Fusion047  label="makeHoles"
  Shapes = -> [Revolve066,Revolve065,Revolve064,Revolve063,Revolve062,Revolve061]
FEATURE [Part::Feature] Face063
  shape: bbox 3.6 x 3.2 x 2e-07 mm, 1 faces, 0 solids (baked)
FEATURE [Part::Revolution] Revolve067  label="moreFrontCaseScrewRetainer002"
  Angle = 360
  Axis = (0,1,0)
  Base = (0,0,0)
  FaceMakerClass = Part::FaceMakerBullseye
  Placement = pos=(102.5,4.5,68.5) rot=(0,0,1;0rad)
  Solid = false
  Source = -> Face063
  Symmetric = false
FEATURE [Part::Feature] Face064
  shape: bbox 3.6 x 3.2 x 2e-07 mm, 1 faces, 0 solids (baked)
FEATURE [Part::Revolution] Revolve068  label="moreFrontCaseScrewRetainer003"
  Angle = 360
  Axis = (0,1,0)
  Base = (0,0,0)
  FaceMakerClass = Part::FaceMakerBullseye
  Placement = pos=(102.5,4.5,3.5) rot=(0,0,1;0rad)
  Solid = false
  Source = -> Face064
  Symmetric = false
FEATURE [Part::Feature] Face065
  shape: bbox 3.5 x 17.8 x 2e-07 mm, 1 faces, 0 solids (baked)
FEATURE [Part::Revolution] Revolve069  label="removeToCreateScrewAndThreadedInsertHole006"
  Angle = 360
  Axis = (0,1,0)
  Base = (0,0,0)
  FaceMakerClass = Part::FaceMakerBullseye
  Placement = pos=(12.5,0,10) rot=(0,0,1;0rad)
  Solid = false
  Source = -> Face065
  Symmetric = false
FEATURE [Part::Feature] Face066
  shape: bbox 3.5 x 17.8 x 2e-07 mm, 1 faces, 0 solids (baked)
FEATURE [Part::Revolution] Revolve070  label="removeToCreateScrewAndThreadedInsertHole007"
  Angle = 360
  Axis = (0,1,0)
  Base = (0,0,0)
  FaceMakerClass = Part::FaceMakerBullseye
  Placement = pos=(12.5,0,62) rot=(0,0,1;0rad)
  Solid = false
  Source = -> Face066
  Symmetric = false
FEATURE [Part::Feature] Face067
  shape: bbox 3.5 x 17.8 x 2e-07 mm, 1 faces, 0 solids (baked)
FEATURE [Part::Revolution] Revolve071  label="removeToCreateScrewAndThreadedInsertHole008"
  Angle = 360
  Axis = (0,1,0)
  Base = (0,0,0)
  FaceMakerClass = Part::FaceMakerBullseye
  Placement = pos=(89.5,0,68.5) rot=(0,0,1;0rad)
  Solid = false
  Source = -> Face067
  Symmetric = false
FEATURE [Part::Feature] Face068
  shape: bbox 3.5 x 17.8 x 2e-07 mm, 1 faces, 0 solids (baked)
FEATURE [Part::Revolution] Revolve072  label="removeToCreateScrewAndThreadedInsertHole009"
  Angle = 360
  Axis = (0,1,0)
  Base = (0,0,0)
  FaceMakerClass = Part::FaceMakerBullseye
  Placement = pos=(89.5,0,3.5) rot=(0,0,1;0rad)
  Solid = false
  Source = -> Face068
  Symmetric = false
FEATURE [Part::Feature] Face069
  shape: bbox 3.5 x 17.8 x 2e-07 mm, 1 faces, 0 solids (baked)
FEATURE [Part::Feature] Face070
  shape: bbox 3.5 x 17.8 x 2e-07 mm, 1 faces, 0 solids (baked)
FEATURE [Part::Revolution] Revolve073  label="removeToCreateScrewAndThreadedInsertHole010"
  Angle = 360
  Axis = (0,1,0)
  Base = (0,0,0)
  FaceMakerClass = Part::FaceMakerBullseye
  Placement = pos=(102.5,4.7,3.5) rot=(0,0,1;0rad)
  Solid = false
  Source = -> Face069
  Symmetric = false
FEATURE [Part::Revolution] Revolve074  label="removeToCreateScrewAndThreadedInsertHole011"
  Angle = 360
  Axis = (0,1,0)
  Base = (0,0,0)
  FaceMakerClass = Part::FaceMakerBullseye
  Placement = pos=(102.5,4.7,68.5) rot=(0,0,1;0rad)
  Solid = false
  Source = -> Face070
  Symmetric = false
FEATURE [Part::MultiFuse] Fusion048  label="makeHoles001"
  Shapes = -> [Revolve074,Revolve073,Revolve072,Revolve071,Revolve070,Revolve069]
FEATURE [Part::MultiFuse] Fusion049  label="caseScrewRetainers"
  Shapes = -> [Revolve067,Revolve068,Revolve048,Revolve047,Revolve039,Revolve040]
FEATURE [Part::Cut] Cut015  label="caseScrewRetainers001"
  Base = -> Fusion049
  Tool = -> Fusion048
FEATURE [Part::MultiFuse] Fusion050  label="casePillars"
  Shapes = -> [Revolve055,Revolve054,Revolve043,Revolve046,Revolve059,Revolve060]
FEATURE [Part::Feature] Face071 .. Face076  x6 (patterned run collapsed; names and placements below)
  shape: bbox 3.5 x 17.8 x 2e-07 mm, 1 faces, 0 solids (baked)
FEATURE [Part::Revolution] Revolve075  label="removeToCreateScrewAndThreadedInsertHole012"
  Angle = 360
  Axis = (0,1,0)
  Base = (0,0,0)
  FaceMakerClass = Part::FaceMakerBullseye
  Placement = pos=(12.5,0,10) rot=(0,0,1;0rad)
  Solid = false
  Source = -> Face071
  Symmetric = false
FEATURE [Part::Revolution] Revolve076  label="removeToCreateScrewAndThreadedInsertHole013"
  Angle = 360
  Axis = (0,1,0)
  Base = (0,0,0)
  FaceMakerClass = Part::FaceMakerBullseye
  Placement = pos=(12.5,0,62) rot=(0,0,1;0rad)
  Solid = false
  Source = -> Face072
  Symmetric = false
FEATURE [Part::Revolution] Revolve077  label="removeToCreateScrewAndThreadedInsertHole014"
  Angle = 360
  Axis = (0,1,0)
  Base = (0,0,0)
  FaceMakerClass = Part::FaceMakerBullseye
  Placement = pos=(89.5,0,68.5) rot=(0,0,1;0rad)
  Solid = false
  Source = -> Face073
  Symmetric = false
FEATURE [Part::Revolution] Revolve078  label="removeToCreateScrewAndThreadedInsertHole015"
  Angle = 360
  Axis = (0,1,0)
  Base = (0,0,0)
  FaceMakerClass = Part::FaceMakerBullseye
  Placement = pos=(89.5,0,3.5) rot=(0,0,1;0rad)
  Solid = false
  Source = -> Face074
  Symmetric = false
FEATURE [Part::Revolution] Revolve079  label="removeToCreateScrewAndThreadedInsertHole016"
  Angle = 360
  Axis = (0,1,0)
  Base = (0,0,0)
  FaceMakerClass = Part::FaceMakerBullseye
  Placement = pos=(102.5,4.7,3.5) rot=(0,0,1;0rad)
  Solid = false
  Source = -> Face075
  Symmetric = false
FEATURE [Part::Revolution] Revolve080  label="removeToCreateScrewAndThreadedInsertHole017"
  Angle = 360
  Axis = (0,1,0)
  Base = (0,0,0)
  FaceMakerClass = Part::FaceMakerBullseye
  Placement = pos=(102.5,4.7,68.5) rot=(0,0,1;0rad)
  Solid = false
  Source = -> Face076
  Symmetric = false
FEATURE [Part::MultiFuse] Fusion051  label="makeHoles002"
  Shapes = -> [Revolve080,Revolve079,Revolve078,Revolve077,Revolve076,Revolve075]
FEATURE [Part::Cut] Cut016  label="caesPillars"
  Base = -> Fusion050
  Tool = -> Fusion051
FEATURE [Part::Revolution] Revolve009  label="plugHousing016"
  Angle = 360
  Axis = (0,1,0)
  Base = (0,0,0)
  FaceMakerClass = Part::FaceMakerBullseye
  Placement = pos=(0,0,36.15) rot=(0,0,1;0rad)
  Solid = false
  Source = -> Face012
  Symmetric = false
FEATURE [Part::MultiFuse] Fusion014  label="plugHousing023"
  Placement = pos=(0,0,0) rot=(0,0,1;1.5708rad)
  Shapes = -> [Revolve011,Revolve009]
FEATURE [Part::Revolution] Revolve010  label="plugHousing017"
  Angle = 360
  Axis = (0,1,0)
  Base = (0,0,0)
  FaceMakerClass = Part::FaceMakerBullseye
  Placement = pos=(0,0,36.15) rot=(0,0,1;0rad)
  Solid = false
  Source = -> Face014
  Symmetric = false
FEATURE [Part::MultiFuse] Fusion015  label="plugHousing024"
  Placement = pos=(0,0,0) rot=(0,0,1;1.5708rad)
  Shapes = -> [Revolve010,Revolve015]
FEATURE [Part::Revolution] Revolve014  label="plugHousing026"
  Angle = 360
  Axis = (0,1,0)
  Base = (0,0,0)
  FaceMakerClass = Part::FaceMakerBullseye
  Placement = pos=(0,0,36.15) rot=(0,0,1;0rad)
  Solid = false
  Source = -> Face011
  Symmetric = false
FEATURE [Part::Revolution] Revolve013  label="plugHousing025"
  Angle = 360
  Axis = (0,1,0)
  Base = (0,0,0)
  FaceMakerClass = Part::FaceMakerBullseye
  Placement = pos=(0,0,36.15) rot=(0,0,1;0rad)
  Solid = false
  Source = -> Face015
  Symmetric = false
FEATURE [Part::MultiFuse] Fusion016  label="plugHousing028"
  Placement = pos=(0,19,0) rot=(0,0,1;3.14159rad)
  Shapes = -> [Fusion014,Fusion013]
FEATURE [Part::MultiFuse] Fusion011  label="plugHousing018"
  Placement = pos=(0,0,0) rot=(0,0,1;1.5708rad)
  Shapes = -> [Revolve014,Revolve013]
FEATURE [Part::MultiFuse] Fusion012  label="plugHousing019"
  Placement = pos=(0,19,0) rot=(0,0,1;3.14159rad)
  Shapes = -> [Fusion011,Fusion015]
FEATURE [Part::MultiFuse] Fusion017  label="plugHousing029"
  Placement = pos=(122.621,0,-0.15) rot=(0,0,1;0rad)
  Shapes = -> [Fusion016,Fusion012]
FEATURE [Part::MultiFuse] Fusion052  label="casePillarRetainers"
  Shapes = -> [Extrude012,Extrude013,Extrude014,Extrude015,Extrude016,Extrude017,Extrude018,Extrude019,Box011,Box012]
FEATURE [Part::Feature] Face077
  shape: bbox 3.5 x 17.8 x 2e-07 mm, 1 faces, 0 solids (baked)
FEATURE [Part::Revolution] Revolve081  label="removeToCreateScrewAndThreadedInsertHole018"
  Angle = 360
  Axis = (0,1,0)
  Base = (0,0,0)
  FaceMakerClass = Part::FaceMakerBullseye
  Placement = pos=(62.3,30.3,19.7) rot=(0,0,1;0rad)
  Solid = false
  Source = -> Face077
  Symmetric = false
FEATURE [Part::Feature] Face078
  shape: bbox 3.5 x 17.8 x 2e-07 mm, 1 faces, 0 solids (baked)
FEATURE [Part::Revolution] Revolve082  label="removeToCreateScrewAndThreadedInsertHole019"
  Angle = 360
  Axis = (0,1,0)
  Base = (0,0,0)
  FaceMakerClass = Part::FaceMakerBullseye
  Placement = pos=(62.3,30.3,51.7) rot=(0,0,1;0rad)
  Solid = false
  Source = -> Face078
  Symmetric = false
FEATURE [Part::Feature] Face079
  shape: bbox 3.5 x 17.8 x 2e-07 mm, 1 faces, 0 solids (baked)
FEATURE [Part::Revolution] Revolve083  label="removeToCreateScrewAndThreadedInsertHole020"
  Angle = 360
  Axis = (0,1,0)
  Base = (0,0,0)
  FaceMakerClass = Part::FaceMakerBullseye
  Placement = pos=(30.3,30.3,19.7) rot=(0,0,1;0rad)
  Solid = false
  Source = -> Face079
  Symmetric = false
FEATURE [Part::Feature] Face080
  shape: bbox 3.5 x 17.8 x 2e-07 mm, 1 faces, 0 solids (baked)
FEATURE [Part::Revolution] Revolve084  label="removeToCreateScrewAndThreadedInsertHole021"
  Angle = 360
  Axis = (0,1,0)
  Base = (0,0,0)
  FaceMakerClass = Part::FaceMakerBullseye
  Placement = pos=(30.3,30.3,51.7) rot=(0,0,1;0rad)
  Solid = false
  Source = -> Face080
  Symmetric = false
FEATURE [Part::MultiFuse] Fusion053  label="createThreadedInsertHolesForFan"
  Shapes = -> [Revolve081,Revolve082,Revolve083,Revolve084]
FEATURE [Part::Cut] Cut017  label="fanScrewHousing001"
  Base = -> Fusion046
  Tool = -> Fusion053
FEATURE [Part::Feature] Face081
  shape: bbox 3.5 x 17.8 x 2e-07 mm, 1 faces, 0 solids (baked)
FEATURE [Part::Revolution] Revolve085  label="removeToCreateScrewAndThreadedInsertHole022"
  Angle = 360
  Axis = (0,1,0)
  Base = (0,0,0)
  FaceMakerClass = Part::FaceMakerBullseye
  Placement = pos=(62.3,30.3,19.7) rot=(0,0,1;0rad)
  Solid = false
  Source = -> Face081
  Symmetric = false
FEATURE [Part::Feature] Face082
  shape: bbox 3.5 x 17.8 x 2e-07 mm, 1 faces, 0 solids (baked)
FEATURE [Part::Revolution] Revolve086  label="removeToCreateScrewAndThreadedInsertHole023"
  Angle = 360
  Axis = (0,1,0)
  Base = (0,0,0)
  FaceMakerClass = Part::FaceMakerBullseye
  Placement = pos=(62.3,30.3,51.7) rot=(0,0,1;0rad)
  Solid = false
  Source = -> Face082
  Symmetric = false
FEATURE [Part::Feature] Face083
  shape: bbox 3.5 x 17.8 x 2e-07 mm, 1 faces, 0 solids (baked)
FEATURE [Part::Revolution] Revolve087  label="removeToCreateScrewAndThreadedInsertHole024"
  Angle = 360
  Axis = (0,1,0)
  Base = (0,0,0)
  FaceMakerClass = Part::FaceMakerBullseye
  Placement = pos=(30.3,30.3,19.7) rot=(0,0,1;0rad)
  Solid = false
  Source = -> Face083
  Symmetric = false
FEATURE [Part::Feature] Face084
  shape: bbox 3.5 x 17.8 x 2e-07 mm, 1 faces, 0 solids (baked)
FEATURE [Part::Revolution] Revolve088  label="removeToCreateScrewAndThreadedInsertHole025"
  Angle = 360
  Axis = (0,1,0)
  Base = (0,0,0)
  FaceMakerClass = Part::FaceMakerBullseye
  Placement = pos=(30.3,30.3,51.7) rot=(0,0,1;0rad)
  Solid = false
  Source = -> Face084
  Symmetric = false
FEATURE [Part::MultiFuse] Fusion054  label="createThreadedInsertHolesForFan001"
  Shapes = -> [Revolve085,Revolve086,Revolve087,Revolve088]
FEATURE [Part::Cut] Cut018  label="top007"
  Base = -> Fusion040
  Tool = -> Fusion054
FEATURE [Sketcher::SketchObject] Sketch029
  FullyConstrained = false
  Placement = pos=(0,0,0) rot=(1,0,0;1.5708rad)
  sketch-geometry (24):
    g0: ArcOfCircle CenterX=-4 CenterY=-10.5 CenterZ=0 NormalX=0 NormalY=0 NormalZ=1 AngleXU=0 Radius=1.5 StartAngle=6e-16 EndAngle=3.14159
    g1: ArcOfCircle CenterX=-34.2 CenterY=-10.5 CenterZ=0 NormalX=0 NormalY=0 NormalZ=1 AngleXU=0 Radius=1.5 StartAngle=0 EndAngle=3.14159
    g2: ArcOfCircle CenterX=-34.2 CenterY=-27.7 CenterZ=0 NormalX=0 NormalY=0 NormalZ=1 AngleXU=0 Radius=1.5 StartAngle=3.14159 EndAngle=6.28319
    g3: ArcOfCircle CenterX=-4 CenterY=-27.7 CenterZ=0 NormalX=0 NormalY=0 NormalZ=1 AngleXU=0 Radius=1.5 StartAngle=3.1416 EndAngle=6.28319
    g4: ArcOfCircle CenterX=-10 CenterY=-4.3 CenterZ=0 NormalX=0 NormalY=0 NormalZ=1 AngleXU=0 Radius=1.5 StartAngle=2e-16 EndAngle=3.14159
    g5: ArcOfCircle CenterX=-16.1 CenterY=-1.8 CenterZ=0 NormalX=0 NormalY=0 NormalZ=1 AngleXU=0 Radius=1.5 StartAngle=5e-16 EndAngle=3.14159
    g6: ArcOfCircle CenterX=-22.1 CenterY=-1.8 CenterZ=0 NormalX=0 NormalY=0 NormalZ=1 AngleXU=0 Radius=1.5 StartAngle=5e-16 EndAngle=3.14159
    g7: ArcOfCircle CenterX=-28.2 CenterY=-4.3 CenterZ=0 NormalX=0 NormalY=0 NormalZ=1 AngleXU=0 Radius=1.5 StartAngle=2e-16 EndAngle=3.14159
    g8: ArcOfCircle CenterX=-10 CenterY=-33.9 CenterZ=0 NormalX=0 NormalY=0 NormalZ=1 AngleXU=0 Radius=1.5 StartAngle=3.14159 EndAngle=6.28319
    g9: ArcOfCircle CenterX=-16.1 CenterY=-36.4 CenterZ=0 NormalX=0 NormalY=0 NormalZ=1 AngleXU=0 Radius=1.5 StartAngle=3.14159 EndAngle=6.28319
    g10: ArcOfCircle CenterX=-22.1 CenterY=-36.4 CenterZ=0 NormalX=0 NormalY=0 NormalZ=1 AngleXU=0 Radius=1.5 StartAngle=3.14159 EndAngle=6.28319
    g11: ArcOfCircle CenterX=-28.2 CenterY=-33.9 CenterZ=0 NormalX=0 NormalY=0 NormalZ=1 AngleXU=0 Radius=1.5 StartAngle=3.14159 EndAngle=6.28319
    g12: LineSegment StartX=-35.7 StartY=-10.5 StartZ=0 EndX=-35.7 EndY=-27.7 EndZ=0
    g13: LineSegment StartX=-32.7 StartY=-10.5 StartZ=0 EndX=-32.7 EndY=-27.7 EndZ=0
    g14: LineSegment StartX=-29.7 StartY=-33.9 StartZ=0 EndX=-29.7 EndY=-4.3 EndZ=0
    g15: LineSegment StartX=-26.7 StartY=-33.9 StartZ=0 EndX=-26.7 EndY=-4.3 EndZ=0
    g16: LineSegment StartX=-2.5 StartY=-10.5 StartZ=0 EndX=-2.5 EndY=-27.7 EndZ=0
    g17: LineSegment StartX=-8.5 StartY=-4.3 StartZ=0 EndX=-8.5 EndY=-33.9 EndZ=0
    g18: LineSegment StartX=-5.5 StartY=-10.5 StartZ=0 EndX=-5.5 EndY=-27.7 EndZ=0
    g19: LineSegment StartX=-11.5 StartY=-4.3 StartZ=0 EndX=-11.5 EndY=-33.9 EndZ=0
    g20: LineSegment StartX=-14.6 StartY=-1.8 StartZ=0 EndX=-14.6 EndY=-36.4 EndZ=0
    g21: LineSegment StartX=-17.6 StartY=-1.8 StartZ=0 EndX=-17.6 EndY=-36.4 EndZ=0
    g22: LineSegment StartX=-20.6 StartY=-36.4 StartZ=0 EndX=-20.6 EndY=-1.8 EndZ=0
    g23: LineSegment StartX=-23.6 StartY=-1.8 StartZ=0 EndX=-23.6 EndY=-36.4 EndZ=0
  constraints (48):
    c: Block(g0)
    c: Block(g1)
    c: Block(g2)
    c: Block(g3)
    c: Block(g4)
    c: Block(g5)
    c: Block(g6)
    c: Block(g7)
    c: Block(g8)
    c: Block(g9)
    c: Block(g10)
    c: Block(g11)
    c: Coincident(g12,g1)
    c: Coincident(g12,g2)
    c: Vertical(g12)
    c: Coincident(g13,g1)
    c: Coincident(g13,g2)
    c: Vertical(g13)
    c: Coincident(g14,g11)
    c: Coincident(g14,g7)
    c: Vertical(g14)
    c: Coincident(g15,g11)
    c: Coincident(g15,g7)
    c: Vertical(g15)
    c: Coincident(g16,g0)
    c: Coincident(g16,g3)
    c: Vertical(g16)
    c: Coincident(g17,g4)
    c: Coincident(g17,g8)
    c: Vertical(g17)
    c: Coincident(g18,g0)
    c: Coincident(g18,g3)
    c: Vertical(g18)
    c: Coincident(g19,g4)
    c: Coincident(g19,g8)
    c: Vertical(g19)
    c: Coincident(g20,g5)
    c: Coincident(g20,g9)
    c: Vertical(g20)
    c: Coincident(g21,g5)
    c: Coincident(g21,g9)
    c: Vertical(g21)
    c: Coincident(g22,g10)
    c: Coincident(g22,g6)
    c: Vertical(g22)
    c: Coincident(g23,g6)
    c: Coincident(g23,g10)
    c: Vertical(g23)
FEATURE [Part::Extrusion] Extrude020  label="removeToCreateFanGrillHoles"
  Base = -> Sketch029
  Dir = (0,-1,6e-16)
  DirMode = 2
  FaceMakerClass = Part::FaceMakerBullseye
  LengthFwd = 10
  LengthRev = 0
  Placement = pos=(65.4,44,54.82) rot=(0,0,1;0rad)
  Solid = true
  Symmetric = false
FEATURE [Part::MultiFuse] Fusion055  label="top008"
  Shapes = -> [Cut017,Cut018]
FEATURE [Part::Cut] Cut019  label="top009"
  Base = -> Fusion055
  Tool = -> Extrude020
FEATURE [App::MeasureDistance] Distance003  label="Distance: 71.95 mm"
  Distance = 71.9513
  P1 = (117,38,72)
  P2 = (117,38,0.0487319)
FEATURE [Sketcher::SketchObject] Sketch030
  FullyConstrained = true
  Placement = pos=(117,19,0) rot=(0.57735,0.57735,0.57735;2.0944rad)
  sketch-geometry (48):
    g0: LineSegment StartX=-49.19 StartY=69.25 StartZ=0 EndX=-49.19 EndY=66.25 EndZ=0
    g1: LineSegment StartX=-49.19 StartY=63.5 StartZ=0 EndX=-49.19 EndY=60.5 EndZ=0
    g2: LineSegment StartX=-49.19 StartY=57.75 StartZ=0 EndX=-49.19 EndY=54.75 EndZ=0
    g3: LineSegment StartX=-49.19 StartY=52 StartZ=0 EndX=-49.19 EndY=49 EndZ=0
    g4: LineSegment StartX=-49.19 StartY=46.25 StartZ=0 EndX=-49.19 EndY=43.25 EndZ=0
    g5: LineSegment StartX=-49.19 StartY=40.5 StartZ=0 EndX=-49.19 EndY=37.5 EndZ=0
    g6: LineSegment StartX=-49.19 StartY=34.5 StartZ=0 EndX=-49.19 EndY=31.5 EndZ=0
    g7: LineSegment StartX=-49.19 StartY=28.75 StartZ=0 EndX=-49.19 EndY=25.75 EndZ=0
    g8: LineSegment StartX=-49.19 StartY=23 StartZ=0 EndX=-49.19 EndY=20 EndZ=0
    g9: LineSegment StartX=-49.19 StartY=17.25 StartZ=0 EndX=-49.19 EndY=14.25 EndZ=0
    g10: LineSegment StartX=-49.19 StartY=11.5 StartZ=0 EndX=-49.19 EndY=8.5 EndZ=0
    g11: LineSegment StartX=-49.19 StartY=5.75 StartZ=0 EndX=-49.19 EndY=2.75 EndZ=0
    g12: ArcOfCircle CenterX=-1.5 CenterY=67.75 CenterZ=0 NormalX=0 NormalY=0 NormalZ=1 AngleXU=0 Radius=1.5 StartAngle=4.71239 EndAngle=7.85398
    g13: ArcOfCircle CenterX=-1.5 CenterY=62 CenterZ=0 NormalX=0 NormalY=0 NormalZ=1 AngleXU=0 Radius=1.5 StartAngle=4.71239 EndAngle=7.85398
    g14: ArcOfCircle CenterX=-1.5 CenterY=56.25 CenterZ=0 NormalX=0 NormalY=0 NormalZ=1 AngleXU=0 Radius=1.5 StartAngle=4.71239 EndAngle=7.85398
    g15: ArcOfCircle CenterX=-11.49 CenterY=50.5 CenterZ=0 NormalX=0 NormalY=0 NormalZ=1 AngleXU=0 Radius=1.5 StartAngle=4.71239 EndAngle=7.85398
    g16: ArcOfCircle CenterX=-16.28 CenterY=44.75 CenterZ=0 NormalX=0 NormalY=0 NormalZ=1 AngleXU=0 Radius=1.5 StartAngle=4.71239 EndAngle=7.85398
    g17: ArcOfCircle CenterX=-18.2337 CenterY=39 CenterZ=0 NormalX=0 NormalY=0 NormalZ=1 AngleXU=0 Radius=1.5 StartAngle=4.71485 EndAngle=7.85398
    g18: ArcOfCircle CenterX=-16.2837 CenterY=27.25 CenterZ=0 NormalX=0 NormalY=0 NormalZ=1 AngleXU=0 Radius=1.5 StartAngle=4.71485 EndAngle=7.85398
    g19: ArcOfCircle CenterX=-18.2337 CenterY=33 CenterZ=0 NormalX=0 NormalY=0 NormalZ=1 AngleXU=0 Radius=1.5 StartAngle=4.71485 EndAngle=7.85398
    g20: ArcOfCircle CenterX=-11.49 CenterY=21.5 CenterZ=0 NormalX=0 NormalY=0 NormalZ=1 AngleXU=0 Radius=1.5 StartAngle=4.71239 EndAngle=7.85398
    g21: ArcOfCircle CenterX=-1.5 CenterY=4.25 CenterZ=0 NormalX=0 NormalY=0 NormalZ=1 AngleXU=0 Radius=1.5 StartAngle=4.71239 EndAngle=7.85398
    g22: ArcOfCircle CenterX=-1.5 CenterY=10 CenterZ=0 NormalX=0 NormalY=0 NormalZ=1 AngleXU=0 Radius=1.5 StartAngle=4.71239 EndAngle=7.85398
    g23: ArcOfCircle CenterX=-1.5 CenterY=15.75 CenterZ=0 NormalX=0 NormalY=0 NormalZ=1 AngleXU=0 Radius=1.5 StartAngle=4.71239 EndAngle=7.85398
    g24: LineSegment StartX=-49.19 StartY=69.25 StartZ=0 EndX=-1.5 EndY=69.25 EndZ=0
    g25: LineSegment StartX=-49.19 StartY=66.25 StartZ=0 EndX=-1.5 EndY=66.25 EndZ=0
    g26: LineSegment StartX=-49.19 StartY=63.5 StartZ=0 EndX=-1.5 EndY=63.5 EndZ=0
    g27: LineSegment StartX=-49.19 StartY=60.5 StartZ=0 EndX=-1.5 EndY=60.5 EndZ=0
    g28: LineSegment StartX=-49.19 StartY=57.75 StartZ=0 EndX=-1.5 EndY=57.75 EndZ=0
    g29: LineSegment StartX=-49.19 StartY=54.75 StartZ=0 EndX=-1.5 EndY=54.75 EndZ=0
    g30: LineSegment StartX=-49.19 StartY=52 StartZ=0 EndX=-11.49 EndY=52 EndZ=0
    g31: LineSegment StartX=-49.19 StartY=49 StartZ=0 EndX=-11.49 EndY=49 EndZ=0
    g32: LineSegment StartX=-49.19 StartY=46.25 StartZ=0 EndX=-16.28 EndY=46.25 EndZ=0
    g33: LineSegment StartX=-49.19 StartY=43.25 StartZ=0 EndX=-16.28 EndY=43.25 EndZ=0
    g34: LineSegment StartX=-49.19 StartY=40.5 StartZ=0 EndX=-18.2337 EndY=40.5 EndZ=0
    g35: LineSegment StartX=-49.19 StartY=37.5 StartZ=0 EndX=-18.23 EndY=37.5 EndZ=0
    g36: LineSegment StartX=-49.19 StartY=34.5 StartZ=0 EndX=-18.2337 EndY=34.5 EndZ=0
    g37: LineSegment StartX=-49.19 StartY=31.5 StartZ=0 EndX=-18.23 EndY=31.5 EndZ=0
    g38: LineSegment StartX=-49.19 StartY=28.75 StartZ=0 EndX=-16.2837 EndY=28.75 EndZ=0
    g39: LineSegment StartX=-49.19 StartY=25.75 StartZ=0 EndX=-16.28 EndY=25.75 EndZ=0
    g40: LineSegment StartX=-49.19 StartY=23 StartZ=0 EndX=-11.49 EndY=23 EndZ=0
    g41: LineSegment StartX=-49.19 StartY=20 StartZ=0 EndX=-11.49 EndY=20 EndZ=0
    g42: LineSegment StartX=-49.19 StartY=17.25 StartZ=0 EndX=-1.5 EndY=17.25 EndZ=0
    g43: LineSegment StartX=-49.19 StartY=14.25 StartZ=0 EndX=-1.5 EndY=14.25 EndZ=0
    g44: LineSegment StartX=-49.19 StartY=11.5 StartZ=0 EndX=-1.5 EndY=11.5 EndZ=0
    g45: LineSegment StartX=-49.19 StartY=8.5 StartZ=0 EndX=-1.5 EndY=8.5 EndZ=0
    g46: LineSegment StartX=-49.19 StartY=5.75 StartZ=0 EndX=-1.5 EndY=5.75 EndZ=0
    g47: LineSegment StartX=-49.19 StartY=2.75 StartZ=0 EndX=-1.5 EndY=2.75 EndZ=0
  constraints (120):
    c: Vertical(g0)
    c: Distance(g0) = 3
    c: Block(g0)
    c: Vertical(g1)
    c: Distance(g1) = 3
    c: Vertical(g2)
    c: Equal(g0,g2) = 3
    c: Block(g2)
    c: Vertical(g3)
    c: Equal(g1,g3) = 3
    c: Vertical(g4)
    c: Equal(g0,g4) = 3
    c: Block(g4)
    c: Vertical(g5)
    c: Equal(g1,g5) = 3
    c: Vertical(g6)
    c: Equal(g0,g6) = 3
    c: Block(g6)
    c: Vertical(g7)
    c: Equal(g1,g7) = 3
    c: Vertical(g8)
    c: Equal(g0,g8) = 3
    c: Block(g8)
    c: Vertical(g9)
    c: Equal(g1,g9) = 3
    c: Vertical(g10)
    c: Equal(g0,g10) = 3
    c: Block(g10)
    c: Vertical(g11)
    c: Equal(g1,g11) = 3
    c: Block(g12)
    c: Block(g13)
    c: Block(g14)
    c: Block(g15)
    c: Block(g16)
    c: Block(g17)
    c: Block(g18)
    c: Block(g19)
    c: Block(g20)
    c: Block(g21)
    c: Block(g22)
    c: Block(g23)
    c: Block(g11)
    c: Block(g9)
    c: Block(g7)
    c: Block(g5)
    c: Block(g3)
    c: Block(g1)
    c: Coincident(g24,g0)
    c: Coincident(g24,g12)
    c: Horizontal(g24)
    c: Coincident(g25,g0)
    c: Coincident(g25,g12)
    c: Horizontal(g25)
    c: Coincident(g26,g1)
    c: Coincident(g26,g13)
    c: Horizontal(g26)
    c: Coincident(g27,g1)
    c: Coincident(g27,g13)
    c: Horizontal(g27)
    c: Coincident(g28,g2)
    c: Coincident(g28,g14)
    c: Horizontal(g28)
    c: Coincident(g29,g2)
    c: Coincident(g29,g14)
    c: Horizontal(g29)
    c: Coincident(g30,g3)
    c: Coincident(g30,g15)
    c: Horizontal(g30)
    c: Coincident(g31,g3)
    c: Coincident(g31,g15)
    c: Horizontal(g31)
    c: Coincident(g32,g4)
    c: Coincident(g32,g16)
    c: Horizontal(g32)
    c: Coincident(g33,g4)
    c: Coincident(g33,g16)
    c: Horizontal(g33)
    c: Coincident(g34,g5)
    c: Coincident(g34,g17)
    c: Horizontal(g34)
    c: Coincident(g35,g5)
    c: Coincident(g35,g17)
    c: Horizontal(g35)
    c: Coincident(g36,g6)
    c: Coincident(g36,g19)
    c: Horizontal(g36)
    c: Coincident(g37,g6)
    c: Coincident(g37,g19)
    c: Horizontal(g37)
    c: Coincident(g38,g7)
    c: Coincident(g38,g18)
    c: Horizontal(g38)
    c: Coincident(g39,g7)
    c: Coincident(g39,g18)
    c: Horizontal(g39)
    c: Coincident(g40,g8)
    c: Coincident(g40,g20)
    c: Horizontal(g40)
    c: Coincident(g41,g8)
    c: Coincident(g41,g20)
    c: Horizontal(g41)
    c: Coincident(g42,g9)
    c: Coincident(g42,g23)
    c: Horizontal(g42)
    c: Coincident(g43,g9)
    c: Coincident(g43,g23)
    c: Horizontal(g43)
    c: Coincident(g44,g10)
    c: Coincident(g44,g22)
    c: Horizontal(g44)
    c: Coincident(g45,g10)
    c: Coincident(g45,g22)
    c: Horizontal(g45)
    c: Coincident(g46,g11)
    c: Coincident(g46,g21)
    c: Horizontal(g46)
    c: Coincident(g47,g11)
    c: Coincident(g47,g21)
    c: Horizontal(g47)
FEATURE [Sketcher::SketchObject] Sketch031
  FullyConstrained = true
  Placement = pos=(117,19,0) rot=(0.57735,0.57735,0.57735;2.0944rad)
  sketch-geometry (24):
    g0: ArcOfCircle CenterX=-49.19 CenterY=67.75 CenterZ=0 NormalX=0 NormalY=0 NormalZ=1 AngleXU=0 Radius=1.5 StartAngle=1.5708 EndAngle=4.71239
    g1: ArcOfCircle CenterX=-49.19 CenterY=62 CenterZ=0 NormalX=0 NormalY=0 NormalZ=1 AngleXU=0 Radius=1.5 StartAngle=1.5708 EndAngle=4.71239
    g2: ArcOfCircle CenterX=-49.19 CenterY=56.25 CenterZ=0 NormalX=0 NormalY=0 NormalZ=1 AngleXU=0 Radius=1.5 StartAngle=1.5708 EndAngle=4.71239
    g3: ArcOfCircle CenterX=-49.19 CenterY=50.5 CenterZ=0 NormalX=0 NormalY=0 NormalZ=1 AngleXU=0 Radius=1.5 StartAngle=1.5708 EndAngle=4.71239
    g4: ArcOfCircle CenterX=-49.19 CenterY=44.75 CenterZ=0 NormalX=0 NormalY=0 NormalZ=1 AngleXU=0 Radius=1.5 StartAngle=1.5708 EndAngle=4.71239
    g5: ArcOfCircle CenterX=-49.19 CenterY=39 CenterZ=0 NormalX=0 NormalY=0 NormalZ=1 AngleXU=0 Radius=1.5 StartAngle=1.5708 EndAngle=4.71239
    g6: ArcOfCircle CenterX=-49.19 CenterY=33 CenterZ=0 NormalX=0 NormalY=0 NormalZ=1 AngleXU=0 Radius=1.5 StartAngle=1.5708 EndAngle=4.71239
    g7: ArcOfCircle CenterX=-49.19 CenterY=27.25 CenterZ=0 NormalX=0 NormalY=0 NormalZ=1 AngleXU=0 Radius=1.5 StartAngle=1.5708 EndAngle=4.71239
    g8: ArcOfCircle CenterX=-49.19 CenterY=21.5 CenterZ=0 NormalX=0 NormalY=0 NormalZ=1 AngleXU=0 Radius=1.5 StartAngle=1.5708 EndAngle=4.71239
    g9: ArcOfCircle CenterX=-49.19 CenterY=15.75 CenterZ=0 NormalX=0 NormalY=0 NormalZ=1 AngleXU=0 Radius=1.5 StartAngle=1.5708 EndAngle=4.71239
    g10: ArcOfCircle CenterX=-49.19 CenterY=10 CenterZ=0 NormalX=0 NormalY=0 NormalZ=1 AngleXU=0 Radius=1.5 StartAngle=1.5708 EndAngle=4.71239
    g11: ArcOfCircle CenterX=-49.19 CenterY=4.25 CenterZ=0 NormalX=0 NormalY=0 NormalZ=1 AngleXU=0 Radius=1.5 StartAngle=1.5708 EndAngle=4.71239
    g12: LineSegment StartX=-49.19 StartY=69.25 StartZ=0 EndX=-49.19 EndY=66.25 EndZ=0
    g13: LineSegment StartX=-49.19 StartY=63.5 StartZ=0 EndX=-49.19 EndY=60.5 EndZ=0
    g14: LineSegment StartX=-49.19 StartY=57.75 StartZ=0 EndX=-49.19 EndY=54.75 EndZ=0
    g15: LineSegment StartX=-49.19 StartY=52 StartZ=0 EndX=-49.19 EndY=49 EndZ=0
    g16: LineSegment StartX=-49.19 StartY=46.25 StartZ=0 EndX=-49.19 EndY=43.25 EndZ=0
    g17: LineSegment StartX=-49.19 StartY=40.5 StartZ=0 EndX=-49.19 EndY=37.5 EndZ=0
    g18: LineSegment StartX=-49.19 StartY=34.5 StartZ=0 EndX=-49.19 EndY=31.5 EndZ=0
    g19: LineSegment StartX=-49.19 StartY=28.75 StartZ=0 EndX=-49.19 EndY=25.75 EndZ=0
    g20: LineSegment StartX=-49.19 StartY=23 StartZ=0 EndX=-49.19 EndY=20 EndZ=0
    g21: LineSegment StartX=-49.19 StartY=17.25 StartZ=0 EndX=-49.19 EndY=14.25 EndZ=0
    g22: LineSegment StartX=-49.19 StartY=11.5 StartZ=0 EndX=-49.19 EndY=8.5 EndZ=0
    g23: LineSegment StartX=-49.19 StartY=5.75 StartZ=0 EndX=-49.19 EndY=2.75 EndZ=0
  constraints (48):
    c: Block(g0)
    c: Block(g1)
    c: Block(g2)
    c: Block(g3)
    c: Block(g4)
    c: Block(g5)
    c: Block(g6)
    c: Block(g7)
    c: Block(g8)
    c: Block(g9)
    c: Block(g10)
    c: Block(g11)
    c: Coincident(g12,g0)
    c: Coincident(g12,g0)
    c: Vertical(g12)
    c: Vertical(g13)
    c: Coincident(g13,g1)
    c: Vertical(g14)
    c: Coincident(g14,g2)
    c: Vertical(g15)
    c: Coincident(g15,g3)
    c: Vertical(g16)
    c: Coincident(g16,g4)
    c: Vertical(g17)
    c: Coincident(g17,g5)
    c: Vertical(g18)
    c: Coincident(g18,g6)
    c: Vertical(g19)
    c: Coincident(g19,g7)
    c: Vertical(g20)
    c: Coincident(g20,g8)
    c: Vertical(g21)
    c: Coincident(g21,g9)
    c: Vertical(g22)
    c: Coincident(g22,g10)
    c: Vertical(g23)
    c: Coincident(g23,g11)
    c: Block(g23)
    c: Block(g22)
    c: Block(g21)
    c: Block(g20)
    c: Block(g13)
    c: Block(g14)
    c: Block(g15)
    c: Block(g16)
    c: Block(g17)
    c: Block(g18)
    c: Block(g19)
FEATURE [Part::Extrusion] Extrude022
  Base = -> Sketch030
  Dir = (1,-2e-16,2e-16)
  DirMode = 2
  FaceMakerClass = Part::FaceMakerBullseye
  LengthFwd = 19
  LengthRev = 0
  Placement = pos=(-19,0,0) rot=(0,0,1;0rad)
  Solid = true
  Symmetric = false
FEATURE [Part::Fillet] Fillet022
  Base = -> Extrude022
  Edges = 24 edges r=1.49: [Edge6,Edge11,Edge18,Edge23,Edge30,Edge35,Edge42,Edge47,Edge54,Edge59,Edge66,Edge71,Edge78,Edge83,Edge90,Edge95,Edge102,Edge107,Edge114,Edge119,Edge126,Edge131,Edge138,Edge143]
FEATURE [Part::Cut] Cut020  label="top010"
  Base = -> Cut019
  Tool = -> Fillet022
FEATURE [Sketcher::SketchObject] Sketch032
  FullyConstrained = true
  Placement = pos=(117,19,0) rot=(0.57735,0.57735,0.57735;2.0944rad)
  sketch-geometry (48):
    g0: LineSegment StartX=-49.19 StartY=69.25 StartZ=0 EndX=-49.19 EndY=66.25 EndZ=0
    g1: LineSegment StartX=-49.19 StartY=63.5 StartZ=0 EndX=-49.19 EndY=60.5 EndZ=0
    g2: LineSegment StartX=-49.19 StartY=57.75 StartZ=0 EndX=-49.19 EndY=54.75 EndZ=0
    g3: LineSegment StartX=-49.19 StartY=52 StartZ=0 EndX=-49.19 EndY=49 EndZ=0
    g4: LineSegment StartX=-49.19 StartY=46.25 StartZ=0 EndX=-49.19 EndY=43.25 EndZ=0
    g5: LineSegment StartX=-49.19 StartY=40.5 StartZ=0 EndX=-49.19 EndY=37.5 EndZ=0
    g6: LineSegment StartX=-49.19 StartY=34.5 StartZ=0 EndX=-49.19 EndY=31.5 EndZ=0
    g7: LineSegment StartX=-49.19 StartY=28.75 StartZ=0 EndX=-49.19 EndY=25.75 EndZ=0
    g8: LineSegment StartX=-49.19 StartY=23 StartZ=0 EndX=-49.19 EndY=20 EndZ=0
    g9: LineSegment StartX=-49.19 StartY=17.25 StartZ=0 EndX=-49.19 EndY=14.25 EndZ=0
    g10: LineSegment StartX=-49.19 StartY=11.5 StartZ=0 EndX=-49.19 EndY=8.5 EndZ=0
    g11: LineSegment StartX=-49.19 StartY=5.75 StartZ=0 EndX=-49.19 EndY=2.75 EndZ=0
    g12: ArcOfCircle CenterX=-1.5 CenterY=67.75 CenterZ=0 NormalX=0 NormalY=0 NormalZ=1 AngleXU=0 Radius=1.5 StartAngle=4.71239 EndAngle=7.85398
    g13: ArcOfCircle CenterX=-1.5 CenterY=62 CenterZ=0 NormalX=0 NormalY=0 NormalZ=1 AngleXU=0 Radius=1.5 StartAngle=4.71239 EndAngle=7.85398
    g14: ArcOfCircle CenterX=-1.5 CenterY=56.25 CenterZ=0 NormalX=0 NormalY=0 NormalZ=1 AngleXU=0 Radius=1.5 StartAngle=4.71239 EndAngle=7.85398
    g15: ArcOfCircle CenterX=-11.49 CenterY=50.5 CenterZ=0 NormalX=0 NormalY=0 NormalZ=1 AngleXU=0 Radius=1.5 StartAngle=4.71239 EndAngle=7.85398
    g16: ArcOfCircle CenterX=-16.28 CenterY=44.75 CenterZ=0 NormalX=0 NormalY=0 NormalZ=1 AngleXU=0 Radius=1.5 StartAngle=4.71239 EndAngle=7.85398
    g17: ArcOfCircle CenterX=-18.2337 CenterY=39 CenterZ=0 NormalX=0 NormalY=0 NormalZ=1 AngleXU=0 Radius=1.5 StartAngle=4.71485 EndAngle=7.85398
    g18: ArcOfCircle CenterX=-16.2837 CenterY=27.25 CenterZ=0 NormalX=0 NormalY=0 NormalZ=1 AngleXU=0 Radius=1.5 StartAngle=4.71485 EndAngle=7.85398
    g19: ArcOfCircle CenterX=-18.2337 CenterY=33 CenterZ=0 NormalX=0 NormalY=0 NormalZ=1 AngleXU=0 Radius=1.5 StartAngle=4.71485 EndAngle=7.85398
    g20: ArcOfCircle CenterX=-11.49 CenterY=21.5 CenterZ=0 NormalX=0 NormalY=0 NormalZ=1 AngleXU=0 Radius=1.5 StartAngle=4.71239 EndAngle=7.85398
    g21: ArcOfCircle CenterX=-1.5 CenterY=4.25 CenterZ=0 NormalX=0 NormalY=0 NormalZ=1 AngleXU=0 Radius=1.5 StartAngle=4.71239 EndAngle=7.85398
    g22: ArcOfCircle CenterX=-1.5 CenterY=10 CenterZ=0 NormalX=0 NormalY=0 NormalZ=1 AngleXU=0 Radius=1.5 StartAngle=4.71239 EndAngle=7.85398
    g23: ArcOfCircle CenterX=-1.5 CenterY=15.75 CenterZ=0 NormalX=0 NormalY=0 NormalZ=1 AngleXU=0 Radius=1.5 StartAngle=4.71239 EndAngle=7.85398
    g24: LineSegment StartX=-49.19 StartY=69.25 StartZ=0 EndX=-1.5 EndY=69.25 EndZ=0
    g25: LineSegment StartX=-49.19 StartY=66.25 StartZ=0 EndX=-1.5 EndY=66.25 EndZ=0
    g26: LineSegment StartX=-49.19 StartY=63.5 StartZ=0 EndX=-1.5 EndY=63.5 EndZ=0
    g27: LineSegment StartX=-49.19 StartY=60.5 StartZ=0 EndX=-1.5 EndY=60.5 EndZ=0
    g28: LineSegment StartX=-49.19 StartY=57.75 StartZ=0 EndX=-1.5 EndY=57.75 EndZ=0
    g29: LineSegment StartX=-49.19 StartY=54.75 StartZ=0 EndX=-1.5 EndY=54.75 EndZ=0
    g30: LineSegment StartX=-49.19 StartY=52 StartZ=0 EndX=-11.49 EndY=52 EndZ=0
    g31: LineSegment StartX=-49.19 StartY=49 StartZ=0 EndX=-11.49 EndY=49 EndZ=0
    g32: LineSegment StartX=-49.19 StartY=46.25 StartZ=0 EndX=-16.28 EndY=46.25 EndZ=0
    g33: LineSegment StartX=-49.19 StartY=43.25 StartZ=0 EndX=-16.28 EndY=43.25 EndZ=0
    g34: LineSegment StartX=-49.19 StartY=40.5 StartZ=0 EndX=-18.2337 EndY=40.5 EndZ=0
    g35: LineSegment StartX=-49.19 StartY=37.5 StartZ=0 EndX=-18.23 EndY=37.5 EndZ=0
    g36: LineSegment StartX=-49.19 StartY=34.5 StartZ=0 EndX=-18.2337 EndY=34.5 EndZ=0
    g37: LineSegment StartX=-49.19 StartY=31.5 StartZ=0 EndX=-18.23 EndY=31.5 EndZ=0
    g38: LineSegment StartX=-49.19 StartY=28.75 StartZ=0 EndX=-16.2837 EndY=28.75 EndZ=0
    g39: LineSegment StartX=-49.19 StartY=25.75 StartZ=0 EndX=-16.28 EndY=25.75 EndZ=0
    g40: LineSegment StartX=-49.19 StartY=23 StartZ=0 EndX=-11.49 EndY=23 EndZ=0
    g41: LineSegment StartX=-49.19 StartY=20 StartZ=0 EndX=-11.49 EndY=20 EndZ=0
    g42: LineSegment StartX=-49.19 StartY=17.25 StartZ=0 EndX=-1.5 EndY=17.25 EndZ=0
    g43: LineSegment StartX=-49.19 StartY=14.25 StartZ=0 EndX=-1.5 EndY=14.25 EndZ=0
    g44: LineSegment StartX=-49.19 StartY=11.5 StartZ=0 EndX=-1.5 EndY=11.5 EndZ=0
    g45: LineSegment StartX=-49.19 StartY=8.5 StartZ=0 EndX=-1.5 EndY=8.5 EndZ=0
    g46: LineSegment StartX=-49.19 StartY=5.75 StartZ=0 EndX=-1.5 EndY=5.75 EndZ=0
    g47: LineSegment StartX=-49.19 StartY=2.75 StartZ=0 EndX=-1.5 EndY=2.75 EndZ=0
  constraints (120):
    c: Vertical(g0)
    c: Distance(g0) = 3
    c: Block(g0)
    c: Vertical(g1)
    c: Distance(g1) = 3
    c: Vertical(g2)
    c: Equal(g0,g2) = 3
    c: Block(g2)
    c: Vertical(g3)
    c: Equal(g1,g3) = 3
    c: Vertical(g4)
    c: Equal(g0,g4) = 3
    c: Block(g4)
    c: Vertical(g5)
    c: Equal(g1,g5) = 3
    c: Vertical(g6)
    c: Equal(g0,g6) = 3
    c: Block(g6)
    c: Vertical(g7)
    c: Equal(g1,g7) = 3
    c: Vertical(g8)
    c: Equal(g0,g8) = 3
    c: Block(g8)
    c: Vertical(g9)
    c: Equal(g1,g9) = 3
    c: Vertical(g10)
    c: Equal(g0,g10) = 3
    c: Block(g10)
    c: Vertical(g11)
    c: Equal(g1,g11) = 3
    c: Block(g12)
    c: Block(g13)
    c: Block(g14)
    c: Block(g15)
    c: Block(g16)
    c: Block(g17)
    c: Block(g18)
    c: Block(g19)
    c: Block(g20)
    c: Block(g21)
    c: Block(g22)
    c: Block(g23)
    c: Block(g11)
    c: Block(g9)
    c: Block(g7)
    c: Block(g5)
    c: Block(g3)
    c: Block(g1)
    c: Coincident(g24,g0)
    c: Coincident(g24,g12)
    c: Horizontal(g24)
    c: Coincident(g25,g0)
    c: Coincident(g25,g12)
    c: Horizontal(g25)
    c: Coincident(g26,g1)
    c: Coincident(g26,g13)
    c: Horizontal(g26)
    c: Coincident(g27,g1)
    c: Coincident(g27,g13)
    c: Horizontal(g27)
    c: Coincident(g28,g2)
    c: Coincident(g28,g14)
    c: Horizontal(g28)
    c: Coincident(g29,g2)
    c: Coincident(g29,g14)
    c: Horizontal(g29)
    c: Coincident(g30,g3)
    c: Coincident(g30,g15)
    c: Horizontal(g30)
    c: Coincident(g31,g3)
    c: Coincident(g31,g15)
    c: Horizontal(g31)
    c: Coincident(g32,g4)
    c: Coincident(g32,g16)
    c: Horizontal(g32)
    c: Coincident(g33,g4)
    c: Coincident(g33,g16)
    c: Horizontal(g33)
    c: Coincident(g34,g5)
    c: Coincident(g34,g17)
    c: Horizontal(g34)
    c: Coincident(g35,g5)
    c: Coincident(g35,g17)
    c: Horizontal(g35)
    c: Coincident(g36,g6)
    c: Coincident(g36,g19)
    c: Horizontal(g36)
    c: Coincident(g37,g6)
    c: Coincident(g37,g19)
    c: Horizontal(g37)
    c: Coincident(g38,g7)
    c: Coincident(g38,g18)
    c: Horizontal(g38)
    c: Coincident(g39,g7)
    c: Coincident(g39,g18)
    c: Horizontal(g39)
    c: Coincident(g40,g8)
    c: Coincident(g40,g20)
    c: Horizontal(g40)
    c: Coincident(g41,g8)
    c: Coincident(g41,g20)
    c: Horizontal(g41)
    c: Coincident(g42,g9)
    c: Coincident(g42,g23)
    c: Horizontal(g42)
    c: Coincident(g43,g9)
    c: Coincident(g43,g23)
    c: Horizontal(g43)
    c: Coincident(g44,g10)
    c: Coincident(g44,g22)
    c: Horizontal(g44)
    c: Coincident(g45,g10)
    c: Coincident(g45,g22)
    c: Horizontal(g45)
    c: Coincident(g46,g11)
    c: Coincident(g46,g21)
    c: Horizontal(g46)
    c: Coincident(g47,g11)
    c: Coincident(g47,g21)
    c: Horizontal(g47)
FEATURE [Part::Extrusion] Extrude023
  Base = -> Sketch032
  Dir = (1,-2e-16,2e-16)
  DirMode = 2
  FaceMakerClass = Part::FaceMakerBullseye
  LengthFwd = 19
  LengthRev = 0
  Placement = pos=(-19,0,0) rot=(0,0,1;0rad)
  Solid = true
  Symmetric = false
FEATURE [Part::Fillet] Fillet023
  Base = -> Extrude023
  Edges = <same value as first occurrence — deduplicated (x6 in doc)>
  Placement = pos=(0,0.05,0) rot=(0,0,1;0rad)
FEATURE [Part::Cut] Cut014  label="bottom003"
  Base = -> Cut007
  Tool = -> Fusion047
FEATURE [Part::Cut] Cut021  label="bottom004"
  Base = -> Cut014
  Tool = -> Fillet023
FEATURE [Sketcher::SketchObject] Sketch033
  FullyConstrained = true
  Placement = pos=(117,19,0) rot=(0.57735,0.57735,0.57735;2.0944rad)
  sketch-geometry (8):
    g0: LineSegment StartX=-49.19 StartY=69.25 StartZ=0 EndX=-49.19 EndY=66.25 EndZ=0
    g1: LineSegment StartX=-49.19 StartY=5.75 StartZ=0 EndX=-49.19 EndY=2.75 EndZ=0
    g2: ArcOfCircle CenterX=-1.5 CenterY=67.75 CenterZ=0 NormalX=0 NormalY=0 NormalZ=1 AngleXU=0 Radius=1.5 StartAngle=4.71239 EndAngle=7.85398
    g3: ArcOfCircle CenterX=-1.5 CenterY=4.25 CenterZ=0 NormalX=0 NormalY=0 NormalZ=1 AngleXU=0 Radius=1.5 StartAngle=4.71239 EndAngle=7.85398
    g4: LineSegment StartX=-49.19 StartY=69.25 StartZ=0 EndX=-1.5 EndY=69.25 EndZ=0
    g5: LineSegment StartX=-49.19 StartY=66.25 StartZ=0 EndX=-1.5 EndY=66.25 EndZ=0
    g6: LineSegment StartX=-49.19 StartY=5.75 StartZ=0 EndX=-1.5 EndY=5.75 EndZ=0
    g7: LineSegment StartX=-49.19 StartY=2.75 StartZ=0 EndX=-1.5 EndY=2.75 EndZ=0
  constraints (19):
    c: Vertical(g0)
    c: Distance(g0) = 3
    c: Block(g0)
    c: Vertical(g1)
    c: Block(g2)
    c: Block(g3)
    c: Block(g1)
    c: Coincident(g4,g0)
    c: Coincident(g4,g2)
    c: Horizontal(g4)
    c: Coincident(g5,g0)
    c: Coincident(g5,g2)
    c: Horizontal(g5)
    c: Coincident(g6,g1)
    c: Coincident(g6,g3)
    c: Horizontal(g6)
    c: Coincident(g7,g1)
    c: Coincident(g7,g3)
    c: Horizontal(g7)
FEATURE [Sketcher::SketchObject] Sketch034
  FullyConstrained = true
  Placement = pos=(117,19,0) rot=(0.57735,0.57735,0.57735;2.0944rad)
  sketch-geometry (8):
    g0: LineSegment StartX=-49.19 StartY=63.5 StartZ=0 EndX=-49.19 EndY=60.5 EndZ=0
    g1: LineSegment StartX=-49.19 StartY=11.5 StartZ=0 EndX=-49.19 EndY=8.5 EndZ=0
    g2: ArcOfCircle CenterX=-1.5 CenterY=62 CenterZ=0 NormalX=0 NormalY=0 NormalZ=1 AngleXU=0 Radius=1.5 StartAngle=4.71239 EndAngle=7.85398
    g3: ArcOfCircle CenterX=-1.5 CenterY=10 CenterZ=0 NormalX=0 NormalY=0 NormalZ=1 AngleXU=0 Radius=1.5 StartAngle=4.71239 EndAngle=7.85398
    g4: LineSegment StartX=-49.19 StartY=63.5 StartZ=0 EndX=-1.5 EndY=63.5 EndZ=0
    g5: LineSegment StartX=-49.19 StartY=60.5 StartZ=0 EndX=-1.5 EndY=60.5 EndZ=0
    g6: LineSegment StartX=-49.19 StartY=11.5 StartZ=0 EndX=-1.5 EndY=11.5 EndZ=0
    g7: LineSegment StartX=-49.19 StartY=8.5 StartZ=0 EndX=-1.5 EndY=8.5 EndZ=0
  constraints (19):
    c: Vertical(g0)
    c: Distance(g0) = 3
    c: Vertical(g1)
    c: Block(g1)
    c: Block(g2)
    c: Block(g3)
    c: Block(g0)
    c: Coincident(g4,g0)
    c: Coincident(g4,g2)
    c: Horizontal(g4)
    c: Coincident(g5,g0)
    c: Coincident(g5,g2)
    c: Horizontal(g5)
    c: Coincident(g6,g1)
    c: Coincident(g6,g3)
    c: Horizontal(g6)
    c: Coincident(g7,g1)
    c: Coincident(g7,g3)
    c: Horizontal(g7)
FEATURE [Part::Extrusion] Extrude024
  Base = -> Sketch033
  Dir = (1,0,0)
  DirMode = 2
  FaceMakerClass = Part::FaceMakerBullseye
  LengthFwd = 10
  LengthRev = 0
  Solid = true
  Symmetric = false
FEATURE [Part::Extrusion] Extrude025
  Base = -> Sketch034
  Dir = (1,0,0)
  DirMode = 2
  FaceMakerClass = Part::FaceMakerBullseye
  LengthFwd = 10
  LengthRev = 0
  Solid = true
  Symmetric = false
FEATURE [Part::Fillet] Fillet024  label="removeFromtMoreFrontCaseScrewRetainers"
  Base = -> Extrude024
  Edges = 4 edges r=1.49: [Edge6,Edge11,Edge18,Edge23]
  Placement = pos=(-11,0,0) rot=(0,0,1;0rad)
FEATURE [Part::Fillet] Fillet025  label="removeFromtMoreFrontCaseScrewRetainers001"
  Base = -> Extrude025
  Edges = 4 edges r=1.49: [Edge6,Edge11,Edge18,Edge23]
  Placement = pos=(-19,0,0) rot=(0,0,1;0rad)
FEATURE [Part::Cut] Cut022
  Base = -> Cut015
  Tool = -> Fillet025
FEATURE [Part::Cut] Cut023  label="screwRetainers"
  Base = -> Cut022
  Tool = -> Fillet024
FEATURE [Part::MultiFuse] Fusion056  label="bottom005"
  Shapes = -> [Fusion044,Cut021]
FEATURE [Part::MultiFuse] Fusion057  label="casePillars001"
  Shapes = -> [Cut016,Fusion052]
FEATURE [Part::MultiFuse] Fusion058  label="bottom006"
  Shapes = -> [Fusion056,Cut023]
FEATURE [Part::MultiFuse] Fusion059  label="bottom007"
  Shapes = -> [Fusion058,Fillet005]
FEATURE [Part::MultiFuse] Fusion060  label="bottom008"
  Shapes = -> [Fusion059,Fusion]
FEATURE [Part::MultiFuse] Fusion061  label="top011"
  Shapes = -> [Cut006,Cut020]
FEATURE [Part::MultiFuse] Fusion062  label="top012"
  Shapes = -> [Fusion057,Fusion061]
FEATURE [Sketcher::SketchObject] Sketch035  label="topSketch007"
  FullyConstrained = true
  sketch-geometry (6):
    g0: LineSegment StartX=19 StartY=38 StartZ=0 EndX=117 EndY=38 EndZ=0
    g1: ArcOfCircle CenterX=19 CenterY=19 CenterZ=0 NormalX=0 NormalY=0 NormalZ=1 AngleXU=0 Radius=19 StartAngle=1.5708 EndAngle=3.14159
    g2: LineSegment StartX=117 StartY=38 StartZ=0 EndX=117 EndY=19 EndZ=0
    g3: LineSegment StartX=98 StartY=1.0161e-12 StartZ=0 EndX=5.22862e-06 EndY=1.0161e-12 EndZ=0
    g4: LineSegment StartX=5.22862e-06 StartY=19 StartZ=0 EndX=5.22862e-06 EndY=1.0161e-12 EndZ=0
    g5: ArcOfCircle CenterX=98 CenterY=19 CenterZ=0 NormalX=0 NormalY=0 NormalZ=1 AngleXU=0 Radius=19 StartAngle=4.71239 EndAngle=6.28319
  constraints (16):
    c: Horizontal(g0)
    c: Distance(g0) = 98
    c: Coincident(g1,g0)
    c: Block(g1)
    c: Coincident(g2,g0)
    c: Vertical(g2)
    c: Distance(g2) = 19
    c: Horizontal(g3)
    c: Coincident(g4,g1)
    c: Vertical(g4)
    c: Coincident(g3,g4)
    c: Block(g3)
    c: Coincident(g5,g2)
    c: Coincident(g5,g3)
    c: Block(g0)
    c: Block(g5)
FEATURE [Part::Extrusion] Extrude026  label="sideA001"
  Base = -> Sketch035
  Dir = (0,0,1)
  DirMode = 2
  FaceMakerClass = Part::FaceMakerBullseye
  LengthFwd = 3
  LengthRev = 0
  Placement = pos=(0,0,-2.7) rot=(0,0,1;0rad)
  Solid = true
  Symmetric = false
FEATURE [Sketcher::SketchObject] Sketch036  label="topSketch008"
  FullyConstrained = true
  sketch-geometry (6):
    g0: LineSegment StartX=19 StartY=38 StartZ=0 EndX=117 EndY=38 EndZ=0
    g1: ArcOfCircle CenterX=19 CenterY=19 CenterZ=0 NormalX=0 NormalY=0 NormalZ=1 AngleXU=0 Radius=19 StartAngle=1.5708 EndAngle=3.14159
    g2: LineSegment StartX=117 StartY=38 StartZ=0 EndX=117 EndY=19 EndZ=0
    g3: LineSegment StartX=98 StartY=1.0161e-12 StartZ=0 EndX=5.22862e-06 EndY=1.0161e-12 EndZ=0
    g4: LineSegment StartX=5.22862e-06 StartY=19 StartZ=0 EndX=5.22862e-06 EndY=1.0161e-12 EndZ=0
    g5: ArcOfCircle CenterX=98 CenterY=19 CenterZ=0 NormalX=0 NormalY=0 NormalZ=1 AngleXU=0 Radius=19 StartAngle=4.71239 EndAngle=6.28319
  constraints (16):
    c: Horizontal(g0)
    c: Distance(g0) = 98
    c: Coincident(g1,g0)
    c: Block(g1)
    c: Coincident(g2,g0)
    c: Vertical(g2)
    c: Distance(g2) = 19
    c: Horizontal(g3)
    c: Coincident(g4,g1)
    c: Vertical(g4)
    c: Coincident(g3,g4)
    c: Block(g3)
    c: Coincident(g5,g2)
    c: Coincident(g5,g3)
    c: Block(g0)
    c: Block(g5)
FEATURE [Part::Extrusion] Extrude027  label="sideB001"
  Base = -> Sketch036
  Dir = (0,0,1)
  DirMode = 2
  FaceMakerClass = Part::FaceMakerBullseye
  LengthFwd = 3
  LengthRev = 0
  Placement = pos=(0,0,71.7) rot=(0,0,1;0rad)
  Solid = true
  Symmetric = false
FEATURE [Part::MultiFuse] Fusion064  label="removeFromBottom"
  Shapes = -> [Extrude026,Extrude027]
FEATURE [Part::Cut] Cut024  label="bottom009"
  Base = -> Fusion060
  Tool = -> Fusion064
FEATURE [Sketcher::SketchObject] Sketch037  label="topSketch009"
  FullyConstrained = true
  sketch-geometry (8):
    g0: ArcOfCircle CenterX=19 CenterY=19.1201 CenterZ=0 NormalX=0 NormalY=0 NormalZ=1 AngleXU=0 Radius=18.8799 StartAngle=1.5708 EndAngle=3.14793
    g1: LineSegment StartX=0.120501 StartY=19.0004 StartZ=0 EndX=0.120501 EndY=0.000382114 EndZ=0
    g2: LineSegment StartX=19 StartY=38 StartZ=0 EndX=124 EndY=38 EndZ=0
    g3: LineSegment StartX=0.120501 StartY=0.000382114 StartZ=0 EndX=105.121 EndY=0.000382114 EndZ=0
    g4: LineSegment StartX=124 StartY=38 StartZ=0 EndX=125.616 EndY=38 EndZ=0
    g5: LineSegment StartX=105.121 StartY=0.000382114 StartZ=0 EndX=106.736 EndY=0.000382114 EndZ=0
    g6: ArcOfCircle CenterX=106.616 CenterY=19 CenterZ=0 NormalX=0 NormalY=0 NormalZ=1 AngleXU=0 Radius=19 StartAngle=4.71873 EndAngle=6.28319
    g7: LineSegment StartX=125.616 StartY=38 StartZ=0 EndX=125.616 EndY=19 EndZ=0
  constraints (21):
    c: Block(g0)
    c: Coincident(g1,g0)
    c: Vertical(g1)
    c: Horizontal(g2)
    c: Distance(g2) = 105
    c: Coincident(g2,g0)
    c: Distance(g1) = 19
    c: Coincident(g3,g1)
    c: Horizontal(g3)
    c: Distance(g3) = 105
    c: Coincident(g4,g2)
    c: Horizontal(g4)
    c: Distance(g4) = 1.61553
    c: Horizontal(g5)
    c: Equal(g4,g5) = 1.61553
    c: Coincident(g5,g3)
    c: Block(g6)
    c: Coincident(g6,g5)
    c: Coincident(g7,g4)
    c: Coincident(g7,g6)
    c: Vertical(g7)
FEATURE [Part::Extrusion] Extrude028  label="sideB"
  Base = -> Sketch037
  Dir = (0,0,1)
  DirMode = 2
  FaceMakerClass = Part::FaceMakerBullseye
  LengthFwd = 3
  LengthRev = 0
  Placement = pos=(0,0,72) rot=(0,0,1;0rad)
  Solid = true
  Symmetric = false
FEATURE [Sketcher::SketchObject] Sketch038  label="topSketch010"
  FullyConstrained = true
  sketch-geometry (22):
    g0: LineSegment StartX=5.21097e-06 StartY=3 StartZ=0 EndX=5.21097e-06 EndY=19 EndZ=0
    g1: ArcOfCircle CenterX=19 CenterY=19 CenterZ=0 NormalX=0 NormalY=0 NormalZ=1 AngleXU=0 Radius=19 StartAngle=1.5708 EndAngle=3.14159
    g2: ArcOfCircle CenterX=19 CenterY=19 CenterZ=0 NormalX=0 NormalY=0 NormalZ=1 AngleXU=0 Radius=16 StartAngle=1.5708 EndAngle=3.14159
    g3: LineSegment StartX=114 StartY=35 StartZ=0 EndX=19 EndY=35 EndZ=0
    g4: LineSegment StartX=5.21097e-06 StartY=3 StartZ=0 EndX=5.21097e-06 EndY=0 EndZ=0
    g5: LineSegment StartX=3 StartY=0 StartZ=0 EndX=5.21097e-06 EndY=0 EndZ=0
    g6: LineSegment StartX=3 StartY=19 StartZ=0 EndX=3 EndY=0 EndZ=0
    g7: LineSegment StartX=19 StartY=38 StartZ=0 EndX=124 EndY=38 EndZ=0
    g8: Circle CenterX=119 CenterY=35 CenterZ=0 NormalX=0 NormalY=0 NormalZ=1 AngleXU=0 Radius=1
    g9: Circle CenterX=121 CenterY=35 CenterZ=0 NormalX=0 NormalY=0 NormalZ=1 AngleXU=0 Radius=1
    g10: Circle CenterX=121 CenterY=33 CenterZ=0 NormalX=0 NormalY=0 NormalZ=1 AngleXU=0 Radius=1
    g11: BSplineCurve PolesCount=3 KnotsCount=2 Degree=2 IsPeriodic=0
    g12: GeomPoint X=119 Y=35 Z=0
    g13: GeomPoint X=121 Y=33 Z=0
    g14: LineSegment StartX=119 StartY=35 StartZ=0 EndX=114 EndY=35 EndZ=0
    g15: ArcOfCircle CenterX=105 CenterY=19 CenterZ=0 NormalX=0 NormalY=0 NormalZ=1 AngleXU=0 Radius=16 StartAngle=5.60905 EndAngle=6.28319
    g16: LineSegment StartX=121 StartY=33 StartZ=0 EndX=121 EndY=19 EndZ=0
    g17: LineSegment StartX=117.5 StartY=9.01251 StartZ=0 EndX=121.163 EndY=9.0125 EndZ=0
    g18: ArcOfCircle CenterX=105 CenterY=19 CenterZ=0 NormalX=0 NormalY=0 NormalZ=1 AngleXU=0 Radius=20.6155 StartAngle=5.7297 EndAngle=6.28319
    g19: LineSegment StartX=121.163 StartY=9.0125 StartZ=0 EndX=122.538 EndY=8.16329 EndZ=0
    g20: LineSegment StartX=124 StartY=38 StartZ=0 EndX=125.616 EndY=38 EndZ=0
    g21: LineSegment StartX=125.616 StartY=19 StartZ=0 EndX=125.616 EndY=38 EndZ=0
  constraints (49):
    c: Vertical(g0)
    c: Block(g0)
    c: Coincident(g1,g0)
    c: Block(g1)
    c: Coincident(g2,g1)
    c: Block(g2)
    c: Coincident(g3,g2)
    c: Horizontal(g3)
    c: Tangent(g3,g2)
    c: Coincident(g4,g0)
    c: Distance(g4) = 3
    c: Vertical(g4)
    c: Coincident(g5,g4)
    c: Horizontal(g5)
    c: Coincident(g6,g2)
    c: Coincident(g6,g5)
    c: Vertical(g6)
    c: Horizontal(g7)
    c: Distance(g7) = 105
    c: Coincident(g7,g1)
    c: Block(g3)
    c: Weight(g8) = 1
    c: Equal(g8,g9)
    c: Equal(g8,g10)
    c: InternalAlignment(g8,g11)
    c: InternalAlignment(g9,g11)
    c: InternalAlignment(g10,g11)
    c: InternalAlignment(g12,g11)
    c: InternalAlignment(g13,g11)
    c: Block(g11)
    c: Coincident(g14,g11)
    c: Coincident(g14,g3)
    c: Horizontal(g14)
    c: Block(g15)
    c: Coincident(g16,g11)
    c: Coincident(g16,g15)
    c: Vertical(g16)
    c: Distance(g16) = 14
    c: Coincident(g17,g15)
    c: Block(g18)
    c: Coincident(g19,g18)
    c: Coincident(g20,g7)
    c: Horizontal(g20)
    c: Vertical(g21)
    c: Coincident(g20,g21)
    c: Block(g20)
    c: Block(g21)
    c: Block(g19)
    c: Block(g17)
FEATURE [Part::Extrusion] Extrude029
  Base = -> Sketch038
  Dir = (0,0,1)
  DirMode = 2
  FaceMakerClass = Part::FaceMakerBullseye
  LengthFwd = 72
  LengthRev = 0
  Solid = true
  Symmetric = false
FEATURE [Part::Feature] Face085
  shape: bbox 4.8 x 25.5 x 2e-07 mm, 1 faces, 0 solids (baked)
FEATURE [Part::Revolution] Revolve089  label="moreFrontCaseScrewPost003"
  Angle = 360
  Axis = (0,1,0)
  Base = (0,0,0)
  FaceMakerClass = Part::FaceMakerBullseye
  Placement = pos=(109.5,4.5,3.5) rot=(0,0,1;0rad)
  Solid = false
  Source = -> Face085
  Symmetric = false
FEATURE [Part::Feature] Face086
  shape: bbox 4.8 x 25.5 x 2e-07 mm, 1 faces, 0 solids (baked)
FEATURE [Part::Revolution] Revolve090  label="moreFrontCaseScrewPost004"
  Angle = 360
  Axis = (0,1,0)
  Base = (0,0,0)
  FaceMakerClass = Part::FaceMakerBullseye
  Placement = pos=(109.5,4.5,68.5) rot=(0,0,1;0rad)
  Solid = false
  Source = -> Face086
  Symmetric = false
FEATURE [Part::Fillet] Fillet026  label="top013"
  Base = -> Extrude029
  Edges = 1 edges r=2: [Edge35]
FEATURE [Sketcher::SketchObject] Sketch039
  FullyConstrained = true
  sketch-geometry (7):
    g0: LineSegment StartX=0 StartY=0 StartZ=0 EndX=0 EndY=6 EndZ=0
    g1: Circle CenterX=0 CenterY=0 CenterZ=0 NormalX=0 NormalY=0 NormalZ=1 AngleXU=0 Radius=1
    g2: Circle CenterX=8 CenterY=6 CenterZ=0 NormalX=0 NormalY=0 NormalZ=1 AngleXU=0 Radius=1
    g3: BSplineCurve PolesCount=3 KnotsCount=2 Degree=2 IsPeriodic=0
    g4: GeomPoint X=0 Y=0 Z=0
    g5: GeomPoint X=8 Y=6 Z=0
    g6: LineSegment StartX=0 StartY=6 StartZ=0 EndX=8 EndY=6 EndZ=0
  constraints (14):
    c: Coincident(g0,g-1)
    c: Distance(g0) = 6
    c: Vertical(g0)
    c: Coincident(g3,g0)
    c: Weight(g1) = 1
    c: Equal(g1,g2)
    c: InternalAlignment(g1,g3)
    c: InternalAlignment(g2,g3)
    c: InternalAlignment(g4,g3)
    c: InternalAlignment(g5,g3)
    c: Block(g3)
    c: Coincident(g6,g0)
    c: Coincident(g6,g3)
    c: Horizontal(g6)
FEATURE [Sketcher::SketchObject] Sketch040
  FullyConstrained = true
  sketch-geometry (7):
    g0: LineSegment StartX=0 StartY=0 StartZ=0 EndX=0 EndY=6 EndZ=0
    g1: Circle CenterX=0 CenterY=0 CenterZ=0 NormalX=0 NormalY=0 NormalZ=1 AngleXU=0 Radius=1
    g2: Circle CenterX=8 CenterY=6 CenterZ=0 NormalX=0 NormalY=0 NormalZ=1 AngleXU=0 Radius=1
    g3: BSplineCurve PolesCount=3 KnotsCount=2 Degree=2 IsPeriodic=0
    g4: GeomPoint X=0 Y=0 Z=0
    g5: GeomPoint X=8 Y=6 Z=0
    g6: LineSegment StartX=0 StartY=6 StartZ=0 EndX=8 EndY=6 EndZ=0
  constraints (14):
    c: Coincident(g0,g-1)
    c: Distance(g0) = 6
    c: Vertical(g0)
    c: Coincident(g3,g0)
    c: Weight(g1) = 1
    c: Equal(g1,g2)
    c: InternalAlignment(g1,g3)
    c: InternalAlignment(g2,g3)
    c: InternalAlignment(g4,g3)
    c: InternalAlignment(g5,g3)
    c: Block(g3)
    c: Coincident(g6,g0)
    c: Coincident(g6,g3)
    c: Horizontal(g6)
FEATURE [Sketcher::SketchObject] Sketch041
  FullyConstrained = true
  sketch-geometry (7):
    g0: LineSegment StartX=0 StartY=0 StartZ=0 EndX=0 EndY=6 EndZ=0
    g1: Circle CenterX=0 CenterY=0 CenterZ=0 NormalX=0 NormalY=0 NormalZ=1 AngleXU=0 Radius=1
    g2: Circle CenterX=8 CenterY=6 CenterZ=0 NormalX=0 NormalY=0 NormalZ=1 AngleXU=0 Radius=1
    g3: BSplineCurve PolesCount=3 KnotsCount=2 Degree=2 IsPeriodic=0
    g4: GeomPoint X=0 Y=0 Z=0
    g5: GeomPoint X=8 Y=6 Z=0
    g6: LineSegment StartX=0 StartY=6 StartZ=0 EndX=8 EndY=6 EndZ=0
  constraints (14):
    c: Coincident(g0,g-1)
    c: Distance(g0) = 6
    c: Vertical(g0)
    c: Coincident(g3,g0)
    c: Weight(g1) = 1
    c: Equal(g1,g2)
    c: InternalAlignment(g1,g3)
    c: InternalAlignment(g2,g3)
    c: InternalAlignment(g4,g3)
    c: InternalAlignment(g5,g3)
    c: Block(g3)
    c: Coincident(g6,g0)
    c: Coincident(g6,g3)
    c: Horizontal(g6)
FEATURE [Sketcher::SketchObject] Sketch042
  FullyConstrained = true
  sketch-geometry (7):
    g0: LineSegment StartX=0 StartY=0 StartZ=0 EndX=0 EndY=6 EndZ=0
    g1: Circle CenterX=0 CenterY=0 CenterZ=0 NormalX=0 NormalY=0 NormalZ=1 AngleXU=0 Radius=1
    g2: Circle CenterX=8 CenterY=6 CenterZ=0 NormalX=0 NormalY=0 NormalZ=1 AngleXU=0 Radius=1
    g3: BSplineCurve PolesCount=3 KnotsCount=2 Degree=2 IsPeriodic=0
    g4: GeomPoint X=0 Y=0 Z=0
    g5: GeomPoint X=8 Y=6 Z=0
    g6: LineSegment StartX=0 StartY=6 StartZ=0 EndX=8 EndY=6 EndZ=0
  constraints (14):
    c: Coincident(g0,g-1)
    c: Distance(g0) = 6
    c: Vertical(g0)
    c: Coincident(g3,g0)
    c: Weight(g1) = 1
    c: Equal(g1,g2)
    c: InternalAlignment(g1,g3)
    c: InternalAlignment(g2,g3)
    c: InternalAlignment(g4,g3)
    c: InternalAlignment(g5,g3)
    c: Block(g3)
    c: Coincident(g6,g0)
    c: Coincident(g6,g3)
    c: Horizontal(g6)
FEATURE [Part::Extrusion] Extrude030  label="caseScrewPillarBracket008"
  Base = -> Sketch039
  Dir = (0,0,1)
  DirMode = 2
  FaceMakerClass = Part::FaceMakerBullseye
  LengthFwd = 2.4
  LengthRev = 0
  Placement = pos=(15.76,29,8.8) rot=(0,1,0;0rad)
  Solid = true
  Symmetric = false
FEATURE [Part::Extrusion] Extrude031  label="caseScrewPillarBracket009"
  Base = -> Sketch040
  Dir = (0,0,1)
  DirMode = 2
  FaceMakerClass = Part::FaceMakerBullseye
  LengthFwd = 2.4
  LengthRev = 0
  Placement = pos=(15.76,29,60.8) rot=(0,0,1;0rad)
  Solid = true
  Symmetric = false
FEATURE [Part::Extrusion] Extrude032  label="caseScrewPillarBracket010"
  Base = -> Sketch041
  Dir = (0,0,1)
  DirMode = 2
  FaceMakerClass = Part::FaceMakerBullseye
  LengthFwd = 2.4
  LengthRev = 0
  Placement = pos=(13.7,29,13.26) rot=(0,-1,0;1.5708rad)
  Solid = true
  Symmetric = false
FEATURE [Part::Extrusion] Extrude033  label="caseScrewPillarBracket011"
  Base = -> Sketch042
  Dir = (0,0,1)
  DirMode = 2
  FaceMakerClass = Part::FaceMakerBullseye
  LengthFwd = 2.4
  LengthRev = 0
  Placement = pos=(11.3,29,58.74) rot=(0,1,0;1.5708rad)
  Solid = true
  Symmetric = false
FEATURE [Sketcher::SketchObject] Sketch043
  FullyConstrained = true
  sketch-geometry (7):
    g0: LineSegment StartX=0 StartY=0 StartZ=0 EndX=0 EndY=6 EndZ=0
    g1: Circle CenterX=0 CenterY=0 CenterZ=0 NormalX=0 NormalY=0 NormalZ=1 AngleXU=0 Radius=1
    g2: Circle CenterX=8 CenterY=6 CenterZ=0 NormalX=0 NormalY=0 NormalZ=1 AngleXU=0 Radius=1
    g3: BSplineCurve PolesCount=3 KnotsCount=2 Degree=2 IsPeriodic=0
    g4: GeomPoint X=0 Y=0 Z=0
    g5: GeomPoint X=8 Y=6 Z=0
    g6: LineSegment StartX=0 StartY=6 StartZ=0 EndX=8 EndY=6 EndZ=0
  constraints (14):
    c: Coincident(g0,g-1)
    c: Distance(g0) = 6
    c: Vertical(g0)
    c: Coincident(g3,g0)
    c: Weight(g1) = 1
    c: Equal(g1,g2)
    c: InternalAlignment(g1,g3)
    c: InternalAlignment(g2,g3)
    c: InternalAlignment(g4,g3)
    c: InternalAlignment(g5,g3)
    c: Block(g3)
    c: Coincident(g6,g0)
    c: Coincident(g6,g3)
    c: Horizontal(g6)
FEATURE [Part::Extrusion] Extrude034  label="caseScrewPillarBracket012"
  Base = -> Sketch043
  Dir = (0,0,1)
  DirMode = 2
  FaceMakerClass = Part::FaceMakerBullseye
  LengthFwd = 2.4
  LengthRev = 0
  Placement = pos=(88.3,29,65.23) rot=(0,1,0;1.5708rad)
  Solid = true
  Symmetric = false
FEATURE [Sketcher::SketchObject] Sketch044
  FullyConstrained = true
  sketch-geometry (7):
    g0: LineSegment StartX=0 StartY=0 StartZ=0 EndX=0 EndY=6 EndZ=0
    g1: Circle CenterX=0 CenterY=0 CenterZ=0 NormalX=0 NormalY=0 NormalZ=1 AngleXU=0 Radius=1
    g2: Circle CenterX=8 CenterY=6 CenterZ=0 NormalX=0 NormalY=0 NormalZ=1 AngleXU=0 Radius=1
    g3: BSplineCurve PolesCount=3 KnotsCount=2 Degree=2 IsPeriodic=0
    g4: GeomPoint X=0 Y=0 Z=0
    g5: GeomPoint X=8 Y=6 Z=0
    g6: LineSegment StartX=0 StartY=6 StartZ=0 EndX=8 EndY=6 EndZ=0
  constraints (14):
    c: Coincident(g0,g-1)
    c: Distance(g0) = 6
    c: Vertical(g0)
    c: Coincident(g3,g0)
    c: Weight(g1) = 1
    c: Equal(g1,g2)
    c: InternalAlignment(g1,g3)
    c: InternalAlignment(g2,g3)
    c: InternalAlignment(g4,g3)
    c: InternalAlignment(g5,g3)
    c: Block(g3)
    c: Coincident(g6,g0)
    c: Coincident(g6,g3)
    c: Horizontal(g6)
FEATURE [Part::Extrusion] Extrude035  label="caseScrewPillarBracket013"
  Base = -> Sketch044
  Dir = (0,0,1)
  DirMode = 2
  FaceMakerClass = Part::FaceMakerBullseye
  LengthFwd = 2.4
  LengthRev = 0
  Placement = pos=(90.7,29,6.77) rot=(0,-1,0;1.5708rad)
  Solid = true
  Symmetric = false
FEATURE [Sketcher::SketchObject] Sketch045
  FullyConstrained = true
  sketch-geometry (7):
    g0: LineSegment StartX=0 StartY=0 StartZ=0 EndX=0 EndY=6 EndZ=0
    g1: Circle CenterX=0 CenterY=0 CenterZ=0 NormalX=0 NormalY=0 NormalZ=1 AngleXU=0 Radius=1
    g2: Circle CenterX=8 CenterY=6 CenterZ=0 NormalX=0 NormalY=0 NormalZ=1 AngleXU=0 Radius=1
    g3: BSplineCurve PolesCount=3 KnotsCount=2 Degree=2 IsPeriodic=0
    g4: GeomPoint X=0 Y=0 Z=0
    g5: GeomPoint X=8 Y=6 Z=0
    g6: LineSegment StartX=0 StartY=6 StartZ=0 EndX=8 EndY=6 EndZ=0
  constraints (14):
    c: Coincident(g0,g-1)
    c: Distance(g0) = 6
    c: Vertical(g0)
    c: Coincident(g3,g0)
    c: Weight(g1) = 1
    c: Equal(g1,g2)
    c: InternalAlignment(g1,g3)
    c: InternalAlignment(g2,g3)
    c: InternalAlignment(g4,g3)
    c: InternalAlignment(g5,g3)
    c: Block(g3)
    c: Coincident(g6,g0)
    c: Coincident(g6,g3)
    c: Horizontal(g6)
FEATURE [Sketcher::SketchObject] Sketch046
  FullyConstrained = true
  sketch-geometry (7):
    g0: LineSegment StartX=0 StartY=0 StartZ=0 EndX=0 EndY=6 EndZ=0
    g1: Circle CenterX=0 CenterY=0 CenterZ=0 NormalX=0 NormalY=0 NormalZ=1 AngleXU=0 Radius=1
    g2: Circle CenterX=8 CenterY=6 CenterZ=0 NormalX=0 NormalY=0 NormalZ=1 AngleXU=0 Radius=1
    g3: BSplineCurve PolesCount=3 KnotsCount=2 Degree=2 IsPeriodic=0
    g4: GeomPoint X=0 Y=0 Z=0
    g5: GeomPoint X=8 Y=6 Z=0
    g6: LineSegment StartX=0 StartY=6 StartZ=0 EndX=8 EndY=6 EndZ=0
  constraints (14):
    c: Coincident(g0,g-1)
    c: Distance(g0) = 6
    c: Vertical(g0)
    c: Coincident(g3,g0)
    c: Weight(g1) = 1
    c: Equal(g1,g2)
    c: InternalAlignment(g1,g3)
    c: InternalAlignment(g2,g3)
    c: InternalAlignment(g4,g3)
    c: InternalAlignment(g5,g3)
    c: Block(g3)
    c: Coincident(g6,g0)
    c: Coincident(g6,g3)
    c: Horizontal(g6)
FEATURE [Part::Extrusion] Extrude036  label="caseScrewPillarBracket014"
  Base = -> Sketch045
  Dir = (0,0,1)
  DirMode = 2
  FaceMakerClass = Part::FaceMakerBullseye
  LengthFwd = 2.4
  LengthRev = 0
  Placement = pos=(110.7,29,6.77) rot=(0,-1,0;1.5708rad)
  Solid = true
  Symmetric = false
FEATURE [Part::Extrusion] Extrude037  label="caseScrewPillarBracket015"
  Base = -> Sketch046
  Dir = (0,0,1)
  DirMode = 2
  FaceMakerClass = Part::FaceMakerBullseye
  LengthFwd = 2.4
  LengthRev = 0
  Placement = pos=(108.3,29,65.23) rot=(0,1,0;1.5708rad)
  Solid = true
  Symmetric = false
FEATURE [Part::Box] Box013  label="frontCaseScrewPillarBracket002"
  AttacherType = Attacher::AttachEngine3D
  Height = 2.4
  Length = 22
  Placement = pos=(87,28,2.3) rot=(0,0,1;0rad)
  Width = 7
FEATURE [Part::Box] Box014  label="frontCaseScrewPillarBracket003"
  AttacherType = Attacher::AttachEngine3D
  Height = 2.4
  Length = 22
  Placement = pos=(87,28,67.3) rot=(0,0,1;0rad)
  Width = 7
FEATURE [Part::Feature] Face087
  shape: bbox 4.8 x 30.2 x 2e-07 mm, 1 faces, 0 solids (baked)
FEATURE [Part::Revolution] Revolve091  label="frontCaseScrewPost004"
  Angle = 360
  Axis = (0,1,0)
  Base = (0,0,0)
  FaceMakerClass = Part::FaceMakerBullseye
  Placement = pos=(89.5,4.5,3.5) rot=(0,0,1;0rad)
  Solid = false
  Source = -> Face087
  Symmetric = false
FEATURE [Part::Feature] Face088
  shape: bbox 4.8 x 30.2 x 2e-07 mm, 1 faces, 0 solids (baked)
FEATURE [Part::Revolution] Revolve092  label="frontCaseScrewPost005"
  Angle = 360
  Axis = (0,1,0)
  Base = (0,0,0)
  FaceMakerClass = Part::FaceMakerBullseye
  Placement = pos=(89.5,4.5,68.5) rot=(0,0,1;0rad)
  Solid = false
  Source = -> Face088
  Symmetric = false
FEATURE [Part::Feature] Face089
  shape: bbox 3.5 x 30.2 x 2e-07 mm, 1 faces, 0 solids (baked)
FEATURE [Part::Revolution] Revolve093  label="backCaseScrewPost002"
  Angle = 360
  Axis = (0,1,0)
  Base = (0,0,0)
  FaceMakerClass = Part::FaceMakerBullseye
  Placement = pos=(12.5,4.5,10) rot=(0,0,1;0rad)
  Solid = false
  Source = -> Face089
  Symmetric = false
FEATURE [Part::Feature] Face090
  shape: bbox 3.5 x 30.2 x 2e-07 mm, 1 faces, 0 solids (baked)
FEATURE [Part::Revolution] Revolve094  label="backCaseScrewPost003"
  Angle = 360
  Axis = (0,1,0)
  Base = (0,0,0)
  FaceMakerClass = Part::FaceMakerBullseye
  Placement = pos=(12.5,4.5,62) rot=(0,0,1;0rad)
  Solid = false
  Source = -> Face090
  Symmetric = false
FEATURE [Part::Box] Box015  label="Cube011"
  AttacherType = Attacher::AttachEngine3D
  Height = 28.8
  Length = 3
  Placement = pos=(107.3,28,21.6) rot=(0,0,1;0rad)
  Width = 7
FEATURE [Part::Box] Box016  label="Cube012"
  AttacherType = Attacher::AttachEngine3D
  Height = 3
  Length = 7.4
  Placement = pos=(107.3,28,18.6) rot=(0,0,1;0rad)
  Width = 7
FEATURE [Part::Box] Box017  label="Cube013"
  AttacherType = Attacher::AttachEngine3D
  Height = 3
  Length = 7.4
  Placement = pos=(107.3,28,50.4) rot=(0,0,1;0rad)
  Width = 7
FEATURE [Part::Cylinder] Cylinder024
  Angle = 360
  AttacherType = Attacher::AttachEngine3D
  Height = 20
  Placement = pos=(0,0,36.15) rot=(0,0,1;0rad)
  Radius = 14.3
FEATURE [Part::Cylinder] Cylinder025
  Angle = 360
  AttacherType = Attacher::AttachEngine3D
  Height = 10
  Placement = pos=(0,0,36.15) rot=(0,0,1;0rad)
  Radius = 4
FEATURE [Part::MultiFuse] Fusion066  label="removeToCreteHoleForPlugHousing009"
  Placement = pos=(70,19,36) rot=(0,1,0;1.5708rad)
  Shapes = -> [Cylinder024,Cylinder025]
FEATURE [Part::MultiFuse] Fusion065  label="plugHousingBracketHolder002"
  Shapes = -> [Box017,Box015,Box016]
FEATURE [Part::Cut] Cut025  label="plugHousingBracketHolder003"
  Base = -> Fusion065
  Placement = pos=(7,0,0) rot=(0,0,1;0rad)
  Tool = -> Fusion066
FEATURE [Sketcher::SketchObject] Sketch047
  FullyConstrained = false
  Placement = pos=(0,0,0) rot=(1,0,0;1.5708rad)
  sketch-geometry (24):
    g0: ArcOfCircle CenterX=-4 CenterY=-10.5 CenterZ=0 NormalX=0 NormalY=0 NormalZ=1 AngleXU=0 Radius=1.5 StartAngle=6e-16 EndAngle=3.14159
    g1: ArcOfCircle CenterX=-34.2 CenterY=-10.5 CenterZ=0 NormalX=0 NormalY=0 NormalZ=1 AngleXU=0 Radius=1.5 StartAngle=0 EndAngle=3.14159
    g2: ArcOfCircle CenterX=-34.2 CenterY=-27.7 CenterZ=0 NormalX=0 NormalY=0 NormalZ=1 AngleXU=0 Radius=1.5 StartAngle=3.14159 EndAngle=6.28319
    g3: ArcOfCircle CenterX=-4 CenterY=-27.7 CenterZ=0 NormalX=0 NormalY=0 NormalZ=1 AngleXU=0 Radius=1.5 StartAngle=3.1416 EndAngle=6.28319
    g4: ArcOfCircle CenterX=-10 CenterY=-4.3 CenterZ=0 NormalX=0 NormalY=0 NormalZ=1 AngleXU=0 Radius=1.5 StartAngle=2e-16 EndAngle=3.14159
    g5: ArcOfCircle CenterX=-16.1 CenterY=-1.8 CenterZ=0 NormalX=0 NormalY=0 NormalZ=1 AngleXU=0 Radius=1.5 StartAngle=5e-16 EndAngle=3.14159
    g6: ArcOfCircle CenterX=-22.1 CenterY=-1.8 CenterZ=0 NormalX=0 NormalY=0 NormalZ=1 AngleXU=0 Radius=1.5 StartAngle=5e-16 EndAngle=3.14159
    g7: ArcOfCircle CenterX=-28.2 CenterY=-4.3 CenterZ=0 NormalX=0 NormalY=0 NormalZ=1 AngleXU=0 Radius=1.5 StartAngle=2e-16 EndAngle=3.14159
    g8: ArcOfCircle CenterX=-10 CenterY=-33.9 CenterZ=0 NormalX=0 NormalY=0 NormalZ=1 AngleXU=0 Radius=1.5 StartAngle=3.14159 EndAngle=6.28319
    g9: ArcOfCircle CenterX=-16.1 CenterY=-36.4 CenterZ=0 NormalX=0 NormalY=0 NormalZ=1 AngleXU=0 Radius=1.5 StartAngle=3.14159 EndAngle=6.28319
    g10: ArcOfCircle CenterX=-22.1 CenterY=-36.4 CenterZ=0 NormalX=0 NormalY=0 NormalZ=1 AngleXU=0 Radius=1.5 StartAngle=3.14159 EndAngle=6.28319
    g11: ArcOfCircle CenterX=-28.2 CenterY=-33.9 CenterZ=0 NormalX=0 NormalY=0 NormalZ=1 AngleXU=0 Radius=1.5 StartAngle=3.14159 EndAngle=6.28319
    g12: LineSegment StartX=-35.7 StartY=-10.5 StartZ=0 EndX=-35.7 EndY=-27.7 EndZ=0
    g13: LineSegment StartX=-32.7 StartY=-10.5 StartZ=0 EndX=-32.7 EndY=-27.7 EndZ=0
    g14: LineSegment StartX=-29.7 StartY=-33.9 StartZ=0 EndX=-29.7 EndY=-4.3 EndZ=0
    g15: LineSegment StartX=-26.7 StartY=-33.9 StartZ=0 EndX=-26.7 EndY=-4.3 EndZ=0
    g16: LineSegment StartX=-2.5 StartY=-10.5 StartZ=0 EndX=-2.5 EndY=-27.7 EndZ=0
    g17: LineSegment StartX=-8.5 StartY=-4.3 StartZ=0 EndX=-8.5 EndY=-33.9 EndZ=0
    g18: LineSegment StartX=-5.5 StartY=-10.5 StartZ=0 EndX=-5.5 EndY=-27.7 EndZ=0
    g19: LineSegment StartX=-11.5 StartY=-4.3 StartZ=0 EndX=-11.5 EndY=-33.9 EndZ=0
    g20: LineSegment StartX=-14.6 StartY=-1.8 StartZ=0 EndX=-14.6 EndY=-36.4 EndZ=0
    g21: LineSegment StartX=-17.6 StartY=-1.8 StartZ=0 EndX=-17.6 EndY=-36.4 EndZ=0
    g22: LineSegment StartX=-20.6 StartY=-36.4 StartZ=0 EndX=-20.6 EndY=-1.8 EndZ=0
    g23: LineSegment StartX=-23.6 StartY=-1.8 StartZ=0 EndX=-23.6 EndY=-36.4 EndZ=0
  constraints (48):
    c: Block(g0)
    c: Block(g1)
    c: Block(g2)
    c: Block(g3)
    c: Block(g4)
    c: Block(g5)
    c: Block(g6)
    c: Block(g7)
    c: Block(g8)
    c: Block(g9)
    c: Block(g10)
    c: Block(g11)
    c: Coincident(g12,g1)
    c: Coincident(g12,g2)
    c: Vertical(g12)
    c: Coincident(g13,g1)
    c: Coincident(g13,g2)
    c: Vertical(g13)
    c: Coincident(g14,g11)
    c: Coincident(g14,g7)
    c: Vertical(g14)
    c: Coincident(g15,g11)
    c: Coincident(g15,g7)
    c: Vertical(g15)
    c: Coincident(g16,g0)
    c: Coincident(g16,g3)
    c: Vertical(g16)
    c: Coincident(g17,g4)
    c: Coincident(g17,g8)
    c: Vertical(g17)
    c: Coincident(g18,g0)
    c: Coincident(g18,g3)
    c: Vertical(g18)
    c: Coincident(g19,g4)
    c: Coincident(g19,g8)
    c: Vertical(g19)
    c: Coincident(g20,g5)
    c: Coincident(g20,g9)
    c: Vertical(g20)
    c: Coincident(g21,g5)
    c: Coincident(g21,g9)
    c: Vertical(g21)
    c: Coincident(g22,g10)
    c: Coincident(g22,g6)
    c: Vertical(g22)
    c: Coincident(g23,g6)
    c: Coincident(g23,g10)
    c: Vertical(g23)
FEATURE [Part::Extrusion] Extrude038  label="removeToCreateFanGrillHoles001"
  Base = -> Sketch047
  Dir = (0,-1,6e-16)
  DirMode = 2
  FaceMakerClass = Part::FaceMakerBullseye
  LengthFwd = 10
  LengthRev = 0
  Placement = pos=(65.4,44,54.82) rot=(0,0,1;0rad)
  Solid = true
  Symmetric = false
FEATURE [Part::Feature] Wire004
  shape: bbox 11 x 5.2 x 2e-07 mm, 0 faces, 0 solids (baked)
FEATURE [Part::Revolution] Revolve095
  Angle = 360
  Axis = (0,1,0)
  Base = (0,0,0)
  FaceMakerClass = Part::FaceMakerBullseye
  Placement = pos=(30.3,38,19.7) rot=(0,0,1;0rad)
  Solid = true
  Source = -> Wire004
  Symmetric = false
FEATURE [Part::Feature] Wire005
  shape: bbox 11 x 5.2 x 2e-07 mm, 0 faces, 0 solids (baked)
FEATURE [Part::Revolution] Revolve096
  Angle = 360
  Axis = (0,1,0)
  Base = (0,0,0)
  FaceMakerClass = Part::FaceMakerBullseye
  Placement = pos=(30.3,38,51.7) rot=(0,0,1;0rad)
  Solid = true
  Source = -> Wire005
  Symmetric = false
FEATURE [Part::Feature] Wire006
  shape: bbox 11 x 5.2 x 2e-07 mm, 0 faces, 0 solids (baked)
FEATURE [Part::Revolution] Revolve097
  Angle = 360
  Axis = (0,1,0)
  Base = (0,0,0)
  FaceMakerClass = Part::FaceMakerBullseye
  Placement = pos=(62.3,38,51.7) rot=(0,0,1;0rad)
  Solid = true
  Source = -> Wire006
  Symmetric = false
FEATURE [Part::Feature] Wire007
  shape: bbox 11 x 5.2 x 2e-07 mm, 0 faces, 0 solids (baked)
FEATURE [Part::Revolution] Revolve098
  Angle = 360
  Axis = (0,1,0)
  Base = (0,0,0)
  FaceMakerClass = Part::FaceMakerBullseye
  Placement = pos=(62.3,38,19.7) rot=(0,0,1;0rad)
  Solid = true
  Source = -> Wire007
  Symmetric = false
FEATURE [Part::MultiFuse] Fusion067  label="fanScrewHousing002"
  Shapes = -> [Revolve098,Revolve097,Revolve096,Revolve095]
FEATURE [Part::Feature] Face091 .. Face094  x4 (patterned run collapsed; names and placements below)
  shape: bbox 3.5 x 17.8 x 2e-07 mm, 1 faces, 0 solids (baked)
FEATURE [Part::Revolution] Revolve099  label="removeToCreateScrewAndThreadedInsertHole026"
  Angle = 360
  Axis = (0,1,0)
  Base = (0,0,0)
  FaceMakerClass = Part::FaceMakerBullseye
  Placement = pos=(62.3,30.3,19.7) rot=(0,0,1;0rad)
  Solid = false
  Source = -> Face091
  Symmetric = false
FEATURE [Part::Revolution] Revolve100  label="removeToCreateScrewAndThreadedInsertHole027"
  Angle = 360
  Axis = (0,1,0)
  Base = (0,0,0)
  FaceMakerClass = Part::FaceMakerBullseye
  Placement = pos=(62.3,30.3,51.7) rot=(0,0,1;0rad)
  Solid = false
  Source = -> Face092
  Symmetric = false
FEATURE [Part::Revolution] Revolve101  label="removeToCreateScrewAndThreadedInsertHole028"
  Angle = 360
  Axis = (0,1,0)
  Base = (0,0,0)
  FaceMakerClass = Part::FaceMakerBullseye
  Placement = pos=(30.3,30.3,19.7) rot=(0,0,1;0rad)
  Solid = false
  Source = -> Face093
  Symmetric = false
FEATURE [Part::Revolution] Revolve102  label="removeToCreateScrewAndThreadedInsertHole029"
  Angle = 360
  Axis = (0,1,0)
  Base = (0,0,0)
  FaceMakerClass = Part::FaceMakerBullseye
  Placement = pos=(30.3,30.3,51.7) rot=(0,0,1;0rad)
  Solid = false
  Source = -> Face094
  Symmetric = false
FEATURE [Part::MultiFuse] Fusion068  label="createThreadedInsertHolesForFan002"
  Shapes = -> [Revolve099,Revolve100,Revolve101,Revolve102]
FEATURE [Part::Cut] Cut026  label="fanScrewHousing003"
  Base = -> Fusion067
  Tool = -> Fusion068
FEATURE [Sketcher::SketchObject] Sketch048
  FullyConstrained = false
  Placement = pos=(0,0,0) rot=(1,0,0;1.5708rad)
  sketch-geometry (24):
    g0: ArcOfCircle CenterX=-4 CenterY=-10.5 CenterZ=0 NormalX=0 NormalY=0 NormalZ=1 AngleXU=0 Radius=1.5 StartAngle=6e-16 EndAngle=3.14159
    g1: ArcOfCircle CenterX=-34.2 CenterY=-10.5 CenterZ=0 NormalX=0 NormalY=0 NormalZ=1 AngleXU=0 Radius=1.5 StartAngle=0 EndAngle=3.14159
    g2: ArcOfCircle CenterX=-34.2 CenterY=-27.7 CenterZ=0 NormalX=0 NormalY=0 NormalZ=1 AngleXU=0 Radius=1.5 StartAngle=3.14159 EndAngle=6.28319
    g3: ArcOfCircle CenterX=-4 CenterY=-27.7 CenterZ=0 NormalX=0 NormalY=0 NormalZ=1 AngleXU=0 Radius=1.5 StartAngle=3.1416 EndAngle=6.28319
    g4: ArcOfCircle CenterX=-10 CenterY=-4.3 CenterZ=0 NormalX=0 NormalY=0 NormalZ=1 AngleXU=0 Radius=1.5 StartAngle=2e-16 EndAngle=3.14159
    g5: ArcOfCircle CenterX=-16.1 CenterY=-1.8 CenterZ=0 NormalX=0 NormalY=0 NormalZ=1 AngleXU=0 Radius=1.5 StartAngle=5e-16 EndAngle=3.14159
    g6: ArcOfCircle CenterX=-22.1 CenterY=-1.8 CenterZ=0 NormalX=0 NormalY=0 NormalZ=1 AngleXU=0 Radius=1.5 StartAngle=5e-16 EndAngle=3.14159
    g7: ArcOfCircle CenterX=-28.2 CenterY=-4.3 CenterZ=0 NormalX=0 NormalY=0 NormalZ=1 AngleXU=0 Radius=1.5 StartAngle=2e-16 EndAngle=3.14159
    g8: ArcOfCircle CenterX=-10 CenterY=-33.9 CenterZ=0 NormalX=0 NormalY=0 NormalZ=1 AngleXU=0 Radius=1.5 StartAngle=3.14159 EndAngle=6.28319
    g9: ArcOfCircle CenterX=-16.1 CenterY=-36.4 CenterZ=0 NormalX=0 NormalY=0 NormalZ=1 AngleXU=0 Radius=1.5 StartAngle=3.14159 EndAngle=6.28319
    g10: ArcOfCircle CenterX=-22.1 CenterY=-36.4 CenterZ=0 NormalX=0 NormalY=0 NormalZ=1 AngleXU=0 Radius=1.5 StartAngle=3.14159 EndAngle=6.28319
    g11: ArcOfCircle CenterX=-28.2 CenterY=-33.9 CenterZ=0 NormalX=0 NormalY=0 NormalZ=1 AngleXU=0 Radius=1.5 StartAngle=3.14159 EndAngle=6.28319
    g12: LineSegment StartX=-35.7 StartY=-10.5 StartZ=0 EndX=-35.7 EndY=-27.7 EndZ=0
    g13: LineSegment StartX=-32.7 StartY=-10.5 StartZ=0 EndX=-32.7 EndY=-27.7 EndZ=0
    g14: LineSegment StartX=-29.7 StartY=-33.9 StartZ=0 EndX=-29.7 EndY=-4.3 EndZ=0
    g15: LineSegment StartX=-26.7 StartY=-33.9 StartZ=0 EndX=-26.7 EndY=-4.3 EndZ=0
    g16: LineSegment StartX=-2.5 StartY=-10.5 StartZ=0 EndX=-2.5 EndY=-27.7 EndZ=0
    g17: LineSegment StartX=-8.5 StartY=-4.3 StartZ=0 EndX=-8.5 EndY=-33.9 EndZ=0
    g18: LineSegment StartX=-5.5 StartY=-10.5 StartZ=0 EndX=-5.5 EndY=-27.7 EndZ=0
    g19: LineSegment StartX=-11.5 StartY=-4.3 StartZ=0 EndX=-11.5 EndY=-33.9 EndZ=0
    g20: LineSegment StartX=-14.6 StartY=-1.8 StartZ=0 EndX=-14.6 EndY=-36.4 EndZ=0
    g21: LineSegment StartX=-17.6 StartY=-1.8 StartZ=0 EndX=-17.6 EndY=-36.4 EndZ=0
    g22: LineSegment StartX=-20.6 StartY=-36.4 StartZ=0 EndX=-20.6 EndY=-1.8 EndZ=0
    g23: LineSegment StartX=-23.6 StartY=-1.8 StartZ=0 EndX=-23.6 EndY=-36.4 EndZ=0
  constraints (48):
    c: Block(g0)
    c: Block(g1)
    c: Block(g2)
    c: Block(g3)
    c: Block(g4)
    c: Block(g5)
    c: Block(g6)
    c: Block(g7)
    c: Block(g8)
    c: Block(g9)
    c: Block(g10)
    c: Block(g11)
    c: Coincident(g12,g1)
    c: Coincident(g12,g2)
    c: Vertical(g12)
    c: Coincident(g13,g1)
    c: Coincident(g13,g2)
    c: Vertical(g13)
    c: Coincident(g14,g11)
    c: Coincident(g14,g7)
    c: Vertical(g14)
    c: Coincident(g15,g11)
    c: Coincident(g15,g7)
    c: Vertical(g15)
    c: Coincident(g16,g0)
    c: Coincident(g16,g3)
    c: Vertical(g16)
    c: Coincident(g17,g4)
    c: Coincident(g17,g8)
    c: Vertical(g17)
    c: Coincident(g18,g0)
    c: Coincident(g18,g3)
    c: Vertical(g18)
    c: Coincident(g19,g4)
    c: Coincident(g19,g8)
    c: Vertical(g19)
    c: Coincident(g20,g5)
    c: Coincident(g20,g9)
    c: Vertical(g20)
    c: Coincident(g21,g5)
    c: Coincident(g21,g9)
    c: Vertical(g21)
    c: Coincident(g22,g10)
    c: Coincident(g22,g6)
    c: Vertical(g22)
    c: Coincident(g23,g6)
    c: Coincident(g23,g10)
    c: Vertical(g23)
FEATURE [Part::Extrusion] Extrude039  label="removeToCreateFanGrillHoles002"
  Base = -> Sketch048
  Dir = (0,-1,6e-16)
  DirMode = 2
  FaceMakerClass = Part::FaceMakerBullseye
  LengthFwd = 10
  LengthRev = 0
  Placement = pos=(65.4,44,54.82) rot=(0,0,1;0rad)
  Solid = true
  Symmetric = false
FEATURE [Part::Cut] Cut027  label="fanScrewHousing004"
  Base = -> Cut026
  Tool = -> Extrude038
FEATURE [Part::Cut] Cut028  label="top014"
  Base = -> Fillet026
  Tool = -> Extrude039
FEATURE [Part::Feature] Face095 .. Face098  x4 (patterned run collapsed; names and placements below)
  shape: bbox 3.5 x 17.8 x 2e-07 mm, 1 faces, 0 solids (baked)
FEATURE [Part::Revolution] Revolve103  label="removeToCreateScrewAndThreadedInsertHole030"
  Angle = 360
  Axis = (0,1,0)
  Base = (0,0,0)
  FaceMakerClass = Part::FaceMakerBullseye
  Placement = pos=(62.3,30.3,19.7) rot=(0,0,1;0rad)
  Solid = false
  Source = -> Face095
  Symmetric = false
FEATURE [Part::Revolution] Revolve104  label="removeToCreateScrewAndThreadedInsertHole031"
  Angle = 360
  Axis = (0,1,0)
  Base = (0,0,0)
  FaceMakerClass = Part::FaceMakerBullseye
  Placement = pos=(62.3,30.3,51.7) rot=(0,0,1;0rad)
  Solid = false
  Source = -> Face096
  Symmetric = false
FEATURE [Part::Revolution] Revolve105  label="removeToCreateScrewAndThreadedInsertHole032"
  Angle = 360
  Axis = (0,1,0)
  Base = (0,0,0)
  FaceMakerClass = Part::FaceMakerBullseye
  Placement = pos=(30.3,30.3,19.7) rot=(0,0,1;0rad)
  Solid = false
  Source = -> Face097
  Symmetric = false
FEATURE [Part::Revolution] Revolve106  label="removeToCreateScrewAndThreadedInsertHole033"
  Angle = 360
  Axis = (0,1,0)
  Base = (0,0,0)
  FaceMakerClass = Part::FaceMakerBullseye
  Placement = pos=(30.3,30.3,51.7) rot=(0,0,1;0rad)
  Solid = false
  Source = -> Face098
  Symmetric = false
FEATURE [Part::MultiFuse] Fusion069  label="createThreadedInsertHolesForFan003"
  Shapes = -> [Revolve103,Revolve104,Revolve105,Revolve106]
FEATURE [Part::Cut] Cut029  label="top015"
  Base = -> Cut028
  Tool = -> Fusion054
FEATURE [Part::Cut] Cut030  label="fanScrewHousing005"
  Base = -> Cut027
  Tool = -> Fusion069
FEATURE [Part::Cylinder] Cylinder026  label="removeToCreteHoleForPlugHousing010"
  Angle = 360
  AttacherType = Attacher::AttachEngine3D
  Height = 20
  Placement = pos=(-2,19,36) rot=(0,1,0;1.5708rad)
  Radius = 14.3
FEATURE [Part::Box] Box018  label="removeToCreteHoleForPlugHousing011"
  AttacherType = Attacher::AttachEngine3D
  Height = 28.6
  Length = 10
  Placement = pos=(-2,0,21.7) rot=(0,0,1;0rad)
  Width = 19
FEATURE [Part::Box] Box019  label="wireHolderBottomCaseBit"
  AttacherType = Attacher::AttachEngine3D
  Height = 28
  Length = 3
  Placement = pos=(0,0,22) rot=(0,0,1;0rad)
  Width = 21
FEATURE [Part::Cylinder] Cylinder027  label="removeToCreteHoleForPlugHousing012"
  Angle = 360
  AttacherType = Attacher::AttachEngine3D
  Height = 20
  Placement = pos=(-2,19,36) rot=(0,1,0;1.5708rad)
  Radius = 14.3
FEATURE [Part::Cut] Cut031  label="wireHolderBottomCaseBit001"
  Base = -> Box019
  Tool = -> Cylinder027
FEATURE [Part::MultiFuse] Fusion070  label="removeToCreteHoleForPlugHousing013"
  Shapes = -> [Box018,Cylinder026]
FEATURE [Part::Cut] Cut032  label="top016"
  Base = -> Cut029
  Tool = -> Fusion070
FEATURE [Part::Cylinder] Cylinder028
  Angle = 360
  AttacherType = Attacher::AttachEngine3D
  Height = 20
  Placement = pos=(0,0,36.15) rot=(0,0,1;0rad)
  Radius = 14.3
FEATURE [Part::Cylinder] Cylinder029
  Angle = 360
  AttacherType = Attacher::AttachEngine3D
  Height = 10
  Placement = pos=(0,0,36.15) rot=(0,0,1;0rad)
  Radius = 4
FEATURE [Part::MultiFuse] Fusion071  label="removeToCreteHoleForPlugHousing014"
  Placement = pos=(70,19,36) rot=(0,1,0;1.5708rad)
  Shapes = -> [Cylinder028,Cylinder029]
FEATURE [Sketcher::SketchObject] Sketch049  label="topSketch011"
  FullyConstrained = true
  sketch-geometry (4):
    g0: ArcOfCircle CenterX=105 CenterY=19 CenterZ=0 NormalX=0 NormalY=0 NormalZ=1 AngleXU=0 Radius=20.6155 StartAngle=5.54125 EndAngle=6.28319
    g1: ArcOfCircle CenterX=105 CenterY=19 CenterZ=0 NormalX=0 NormalY=0 NormalZ=1 AngleXU=0 Radius=13 StartAngle=5.54125 EndAngle=6.28319
    g2: LineSegment StartX=118 StartY=19 StartZ=0 EndX=125.616 EndY=19 EndZ=0
    g3: LineSegment StartX=114.583 StartY=10.2157 StartZ=0 EndX=120.197 EndY=5.06982 EndZ=0
  constraints (7):
    c: Block(g0)
    c: Block(g1)
    c: Coincident(g2,g1)
    c: Coincident(g2,g0)
    c: Horizontal(g2)
    c: Coincident(g3,g1)
    c: Coincident(g3,g0)
FEATURE [Part::Box] Box020  label="removeToCreteHoleForPlugHousing015"
  AttacherType = Attacher::AttachEngine3D
  Height = 28.6
  Length = 20
  Placement = pos=(106.15,0,21.7) rot=(0,0,1;0rad)
  Width = 19
FEATURE [Part::MultiFuse] Fusion072  label="removeToCreteHoleForPlugHousing016"
  Shapes = -> [Box020,Fusion071]
FEATURE [Part::Cut] Cut033  label="removeToCreteHoleForPlugHousing017"
  Base = -> Cut032
  Tool = -> Fusion072
FEATURE [Part::Cylinder] Cylinder030
  Angle = 360
  AttacherType = Attacher::AttachEngine3D
  Height = 20
  Placement = pos=(0,0,36.15) rot=(0,0,1;0rad)
  Radius = 14.3
FEATURE [Part::Cylinder] Cylinder031
  Angle = 360
  AttacherType = Attacher::AttachEngine3D
  Height = 10
  Placement = pos=(0,0,36.15) rot=(0,0,1;0rad)
  Radius = 4
FEATURE [Part::Box] Box021  label="removeToCreteHoleForPlugHousing019"
  AttacherType = Attacher::AttachEngine3D
  Height = 28.6
  Length = 20
  Placement = pos=(106.15,0,21.7) rot=(0,0,1;0rad)
  Width = 19
FEATURE [Part::MultiFuse] Fusion074  label="removeToCreteHoleForPlugHousing020"
  Placement = pos=(70,19,36) rot=(0,1,0;1.5708rad)
  Shapes = -> [Cylinder030,Cylinder031]
FEATURE [Part::MultiFuse] Fusion073  label="removeToCreteHoleForPlugHousing018"
  Placement = pos=(0,0,28.3) rot=(0,0,1;0rad)
  Shapes = -> [Box021,Fusion074]
FEATURE [Part::Cylinder] Cylinder032
  Angle = 360
  AttacherType = Attacher::AttachEngine3D
  Height = 20
  Placement = pos=(0,0,36.15) rot=(0,0,1;0rad)
  Radius = 14.3
FEATURE [Part::Cylinder] Cylinder033
  Angle = 360
  AttacherType = Attacher::AttachEngine3D
  Height = 10
  Placement = pos=(0,0,36.15) rot=(0,0,1;0rad)
  Radius = 4
FEATURE [Part::Box] Box022  label="removeToCreteHoleForPlugHousing021"
  AttacherType = Attacher::AttachEngine3D
  Height = 28.6
  Length = 20
  Placement = pos=(106.15,0,21.7) rot=(0,0,1;0rad)
  Width = 19
FEATURE [Part::MultiFuse] Fusion076  label="removeToCreteHoleForPlugHousing023"
  Placement = pos=(70,19,36) rot=(0,1,0;1.5708rad)
  Shapes = -> [Cylinder032,Cylinder033]
FEATURE [Part::MultiFuse] Fusion075  label="removeToCreteHoleForPlugHousing022"
  Placement = pos=(0,0,-28.3) rot=(0,0,1;0rad)
  Shapes = -> [Box022,Fusion076]
FEATURE [Part::MultiFuse] Fusion077  label="removeToCreatePlugHousingBottomBit"
  Shapes = -> [Fusion075,Fusion073]
FEATURE [Part::Cylinder] Cylinder034
  Angle = 360
  AttacherType = Attacher::AttachEngine3D
  Height = 20
  Placement = pos=(0,0,36.15) rot=(0,0,1;0rad)
  Radius = 14
FEATURE [Part::Cylinder] Cylinder035
  Angle = 360
  AttacherType = Attacher::AttachEngine3D
  Height = 10
  Placement = pos=(0,0,36.15) rot=(0,0,1;0rad)
  Radius = 4
FEATURE [Part::MultiFuse] Fusion078  label="removeToCreteHoleForPlugHousing024"
  Placement = pos=(70,19,36) rot=(0,1,0;1.5708rad)
  Shapes = -> [Cylinder034,Cylinder035]
FEATURE [Part::MultiFuse] Fusion079  label="removeToCreatePlugHousingBottomBit001"
  Shapes = -> [Fusion078,Fusion077]
FEATURE [Part::Extrusion] Extrude040  label="bottomPlugHousingBit"
  Base = -> Sketch049
  Dir = (0,0,1)
  DirMode = 2
  FaceMakerClass = Part::FaceMakerBullseye
  LengthFwd = 72
  LengthRev = 0
  Solid = true
  Symmetric = false
FEATURE [Part::Cut] Cut034  label="bottomPlugHousingBit001"
  Base = -> Extrude040
  Placement = pos=(-0.09,0,0) rot=(0,0,1;0rad)
  Tool = -> Fusion079
FEATURE [Part::Box] Box023  label="Cube014"
  AttacherType = Attacher::AttachEngine3D
  Height = 16
  Length = 8
  Placement = pos=(12.7,31.52,28) rot=(0,0,1;0rad)
  Width = 4
FEATURE [Part::Cylinder] Cylinder036
  Angle = 360
  AttacherType = Attacher::AttachEngine3D
  Height = 10
  Placement = pos=(0,0,36.15) rot=(0,0,1;0rad)
  Radius = 4
FEATURE [Part::Cylinder] Cylinder037
  Angle = 360
  AttacherType = Attacher::AttachEngine3D
  Height = 20
  Placement = pos=(0,0,36.15) rot=(0,0,1;0rad)
  Radius = 8.2
FEATURE [Part::MultiFuse] Fusion080  label="removeToCreteHoleForPlugHousing025"
  Placement = pos=(-42,19,36) rot=(0,1,0;1.5708rad)
  Shapes = -> [Cylinder037,Cylinder036]
FEATURE [Sketcher::SketchObject] Sketch050  label="topSketch012"
  FullyConstrained = true
  sketch-geometry (4):
    g0: LineSegment StartX=16.8446 StartY=31.512 StartZ=0 EndX=16.3251 EndY=34.4666 EndZ=0
    g1: ArcOfCircle CenterX=19 CenterY=19.2524 CenterZ=0 NormalX=0 NormalY=0 NormalZ=1 AngleXU=0 Radius=15.4476 StartAngle=1.74483 EndAngle=2.72717
    g2: ArcOfCircle CenterX=19 CenterY=19.2524 CenterZ=0 NormalX=0 NormalY=0 NormalZ=1 AngleXU=0 Radius=12.4476 StartAngle=1.74483 EndAngle=2.73189
    g3: LineSegment StartX=4.86004 StartY=25.4725 StartZ=0 EndX=7.58253 EndY=24.2107 EndZ=0
  constraints (7):
    c: Block(g0)
    c: Coincident(g1,g0)
    c: Coincident(g2,g0)
    c: Coincident(g3,g1)
    c: Coincident(g3,g2)
    c: Block(g1)
    c: Block(g2)
FEATURE [Part::Extrusion] Extrude041
  Base = -> Sketch050
  Dir = (0,0,1)
  DirMode = 2
  FaceMakerClass = Part::FaceMakerBullseye
  LengthFwd = 10.6
  LengthRev = 0
  Placement = pos=(0,0,31) rot=(0,0,1;0rad)
  Solid = true
  Symmetric = false
FEATURE [Part::Cut] Cut035
  Base = -> Extrude041
  Placement = pos=(0,0,-0.3) rot=(0,0,1;0rad)
  Tool = -> Fusion080
FEATURE [Part::Cut] Cut036
  Base = -> Box023
  Tool = -> Cut035
FEATURE [Part::Fillet] Fillet027
  Base = -> Cut036
  Edges = 1 edges r=0.7: [Edge13]
FEATURE [Part::Fillet] Fillet028
  Base = -> Fillet027
  Edges = 1 edges r=0.7: [Edge13]
FEATURE [Part::Fillet] Fillet029
  Base = -> Fillet028
  Edges = 1 edges r=0.7: [Edge16]
FEATURE [Part::Fillet] Fillet030
  Base = -> Fillet029
  Edges = 1 edges r=0.7: [Edge11]
FEATURE [Part::Fillet] Fillet031
  Base = -> Fillet030
  Edges = 1 edges r=0.7: [Edge10]
FEATURE [Part::Fillet] Fillet032
  Base = -> Fillet031
  Edges = 1 edges r=1.2: [Edge5]
FEATURE [Part::Fillet] Fillet033
  Base = -> Fillet032
  Edges = 1 edges r=1.2: [Edge12]
FEATURE [Part::Fillet] Fillet034  label="wireHousingRetainer"
  Base = -> Fillet033
  Edges = 1 edges r=2: [Edge1]
  Placement = pos=(0.3,0,0) rot=(0,0,1;0rad)
FEATURE [Part::Feature] Face099
  shape: bbox 3.5 x 17.8 x 2e-07 mm, 1 faces, 0 solids (baked)
FEATURE [Part::Revolution] Revolve107  label="removeToCreateScrewAndThreadedInsertHole034"
  Angle = 360
  Axis = (0,1,0)
  Base = (0,0,0)
  FaceMakerClass = Part::FaceMakerBullseye
  Placement = pos=(12.5,0,10) rot=(0,0,1;0rad)
  Solid = false
  Source = -> Face099
  Symmetric = false
FEATURE [Part::Feature] Face100
  shape: bbox 3.5 x 17.8 x 2e-07 mm, 1 faces, 0 solids (baked)
FEATURE [Part::Revolution] Revolve108  label="removeToCreateScrewAndThreadedInsertHole035"
  Angle = 360
  Axis = (0,1,0)
  Base = (0,0,0)
  FaceMakerClass = Part::FaceMakerBullseye
  Placement = pos=(12.5,0,62) rot=(0,0,1;0rad)
  Solid = false
  Source = -> Face100
  Symmetric = false
FEATURE [Part::Feature] Face101
  shape: bbox 3.5 x 17.8 x 2e-07 mm, 1 faces, 0 solids (baked)
FEATURE [Part::Revolution] Revolve109  label="removeToCreateScrewAndThreadedInsertHole036"
  Angle = 360
  Axis = (0,1,0)
  Base = (0,0,0)
  FaceMakerClass = Part::FaceMakerBullseye
  Placement = pos=(89.5,0,68.5) rot=(0,0,1;0rad)
  Solid = false
  Source = -> Face101
  Symmetric = false
FEATURE [Part::Feature] Face102
  shape: bbox 3.5 x 17.8 x 2e-07 mm, 1 faces, 0 solids (baked)
FEATURE [Part::Revolution] Revolve110  label="removeToCreateScrewAndThreadedInsertHole037"
  Angle = 360
  Axis = (0,1,0)
  Base = (0,0,0)
  FaceMakerClass = Part::FaceMakerBullseye
  Placement = pos=(89.5,0,3.5) rot=(0,0,1;0rad)
  Solid = false
  Source = -> Face102
  Symmetric = false
FEATURE [Part::Feature] Face103
  shape: bbox 3.5 x 17.8 x 2e-07 mm, 1 faces, 0 solids (baked)
FEATURE [Part::Revolution] Revolve111  label="removeToCreateScrewAndThreadedInsertHole038"
  Angle = 360
  Axis = (0,1,0)
  Base = (0,0,0)
  FaceMakerClass = Part::FaceMakerBullseye
  Placement = pos=(109.5,4.7,3.5) rot=(0,0,1;0rad)
  Solid = false
  Source = -> Face103
  Symmetric = false
FEATURE [Part::Feature] Face104
  shape: bbox 3.5 x 17.8 x 2e-07 mm, 1 faces, 0 solids (baked)
FEATURE [Part::Revolution] Revolve112  label="removeToCreateScrewAndThreadedInsertHole039"
  Angle = 360
  Axis = (0,1,0)
  Base = (0,0,0)
  FaceMakerClass = Part::FaceMakerBullseye
  Placement = pos=(109.5,4.7,68.5) rot=(0,0,1;0rad)
  Solid = false
  Source = -> Face104
  Symmetric = false
FEATURE [Part::MultiFuse] Fusion081  label="removeToCreateScrewAndThreadedInsertHole040"
  Shapes = -> [Revolve107,Revolve108,Revolve109,Revolve110,Revolve111,Revolve112]
FEATURE [Part::MultiFuse] Fusion082  label="casePillars002"
  Shapes = -> [Revolve094,Revolve092,Revolve090,Revolve089,Revolve091,Revolve093]
FEATURE [Part::Cut] Cut037  label="casePillars003"
  Base = -> Fusion082
  Tool = -> Fusion081
FEATURE [Sketcher::SketchObject] Sketch051
  FullyConstrained = true
  Placement = pos=(117,19,0) rot=(0.57735,0.57735,0.57735;2.0944rad)
  sketch-geometry (48):
    g0: LineSegment StartX=-49.19 StartY=69.25 StartZ=0 EndX=-49.19 EndY=66.25 EndZ=0
    g1: LineSegment StartX=-49.19 StartY=63.5 StartZ=0 EndX=-49.19 EndY=60.5 EndZ=0
    g2: LineSegment StartX=-49.19 StartY=57.75 StartZ=0 EndX=-49.19 EndY=54.75 EndZ=0
    g3: LineSegment StartX=-49.19 StartY=52 StartZ=0 EndX=-49.19 EndY=49 EndZ=0
    g4: LineSegment StartX=-49.19 StartY=46.25 StartZ=0 EndX=-49.19 EndY=43.25 EndZ=0
    g5: LineSegment StartX=-49.19 StartY=40.5 StartZ=0 EndX=-49.19 EndY=37.5 EndZ=0
    g6: LineSegment StartX=-49.19 StartY=34.5 StartZ=0 EndX=-49.19 EndY=31.5 EndZ=0
    g7: LineSegment StartX=-49.19 StartY=28.75 StartZ=0 EndX=-49.19 EndY=25.75 EndZ=0
    g8: LineSegment StartX=-49.19 StartY=23 StartZ=0 EndX=-49.19 EndY=20 EndZ=0
    g9: LineSegment StartX=-49.19 StartY=17.25 StartZ=0 EndX=-49.19 EndY=14.25 EndZ=0
    g10: LineSegment StartX=-49.19 StartY=11.5 StartZ=0 EndX=-49.19 EndY=8.5 EndZ=0
    g11: LineSegment StartX=-49.19 StartY=5.75 StartZ=0 EndX=-49.19 EndY=2.75 EndZ=0
    g12: ArcOfCircle CenterX=-1.5 CenterY=67.75 CenterZ=0 NormalX=0 NormalY=0 NormalZ=1 AngleXU=0 Radius=1.5 StartAngle=4.71239 EndAngle=7.85398
    g13: ArcOfCircle CenterX=-1.5 CenterY=62 CenterZ=0 NormalX=0 NormalY=0 NormalZ=1 AngleXU=0 Radius=1.5 StartAngle=4.71239 EndAngle=7.85398
    g14: ArcOfCircle CenterX=-1.5 CenterY=56.25 CenterZ=0 NormalX=0 NormalY=0 NormalZ=1 AngleXU=0 Radius=1.5 StartAngle=4.71239 EndAngle=7.85398
    g15: ArcOfCircle CenterX=-11.49 CenterY=50.5 CenterZ=0 NormalX=0 NormalY=0 NormalZ=1 AngleXU=0 Radius=1.5 StartAngle=4.71239 EndAngle=7.85398
    g16: ArcOfCircle CenterX=-16.28 CenterY=44.75 CenterZ=0 NormalX=0 NormalY=0 NormalZ=1 AngleXU=0 Radius=1.5 StartAngle=4.71239 EndAngle=7.85398
    g17: ArcOfCircle CenterX=-18.2337 CenterY=39 CenterZ=0 NormalX=0 NormalY=0 NormalZ=1 AngleXU=0 Radius=1.5 StartAngle=4.71485 EndAngle=7.85398
    g18: ArcOfCircle CenterX=-16.2837 CenterY=27.25 CenterZ=0 NormalX=0 NormalY=0 NormalZ=1 AngleXU=0 Radius=1.5 StartAngle=4.71485 EndAngle=7.85398
    g19: ArcOfCircle CenterX=-18.2337 CenterY=33 CenterZ=0 NormalX=0 NormalY=0 NormalZ=1 AngleXU=0 Radius=1.5 StartAngle=4.71485 EndAngle=7.85398
    g20: ArcOfCircle CenterX=-11.49 CenterY=21.5 CenterZ=0 NormalX=0 NormalY=0 NormalZ=1 AngleXU=0 Radius=1.5 StartAngle=4.71239 EndAngle=7.85398
    g21: ArcOfCircle CenterX=-1.5 CenterY=4.25 CenterZ=0 NormalX=0 NormalY=0 NormalZ=1 AngleXU=0 Radius=1.5 StartAngle=4.71239 EndAngle=7.85398
    g22: ArcOfCircle CenterX=-1.5 CenterY=10 CenterZ=0 NormalX=0 NormalY=0 NormalZ=1 AngleXU=0 Radius=1.5 StartAngle=4.71239 EndAngle=7.85398
    g23: ArcOfCircle CenterX=-1.5 CenterY=15.75 CenterZ=0 NormalX=0 NormalY=0 NormalZ=1 AngleXU=0 Radius=1.5 StartAngle=4.71239 EndAngle=7.85398
    g24: LineSegment StartX=-49.19 StartY=69.25 StartZ=0 EndX=-1.5 EndY=69.25 EndZ=0
    g25: LineSegment StartX=-49.19 StartY=66.25 StartZ=0 EndX=-1.5 EndY=66.25 EndZ=0
    g26: LineSegment StartX=-49.19 StartY=63.5 StartZ=0 EndX=-1.5 EndY=63.5 EndZ=0
    g27: LineSegment StartX=-49.19 StartY=60.5 StartZ=0 EndX=-1.5 EndY=60.5 EndZ=0
    g28: LineSegment StartX=-49.19 StartY=57.75 StartZ=0 EndX=-1.5 EndY=57.75 EndZ=0
    g29: LineSegment StartX=-49.19 StartY=54.75 StartZ=0 EndX=-1.5 EndY=54.75 EndZ=0
    g30: LineSegment StartX=-49.19 StartY=52 StartZ=0 EndX=-11.49 EndY=52 EndZ=0
    g31: LineSegment StartX=-49.19 StartY=49 StartZ=0 EndX=-11.49 EndY=49 EndZ=0
    g32: LineSegment StartX=-49.19 StartY=46.25 StartZ=0 EndX=-16.28 EndY=46.25 EndZ=0
    g33: LineSegment StartX=-49.19 StartY=43.25 StartZ=0 EndX=-16.28 EndY=43.25 EndZ=0
    g34: LineSegment StartX=-49.19 StartY=40.5 StartZ=0 EndX=-18.2337 EndY=40.5 EndZ=0
    g35: LineSegment StartX=-49.19 StartY=37.5 StartZ=0 EndX=-18.23 EndY=37.5 EndZ=0
    g36: LineSegment StartX=-49.19 StartY=34.5 StartZ=0 EndX=-18.2337 EndY=34.5 EndZ=0
    g37: LineSegment StartX=-49.19 StartY=31.5 StartZ=0 EndX=-18.23 EndY=31.5 EndZ=0
    g38: LineSegment StartX=-49.19 StartY=28.75 StartZ=0 EndX=-16.2837 EndY=28.75 EndZ=0
    g39: LineSegment StartX=-49.19 StartY=25.75 StartZ=0 EndX=-16.28 EndY=25.75 EndZ=0
    g40: LineSegment StartX=-49.19 StartY=23 StartZ=0 EndX=-11.49 EndY=23 EndZ=0
    g41: LineSegment StartX=-49.19 StartY=20 StartZ=0 EndX=-11.49 EndY=20 EndZ=0
    g42: LineSegment StartX=-49.19 StartY=17.25 StartZ=0 EndX=-1.5 EndY=17.25 EndZ=0
    g43: LineSegment StartX=-49.19 StartY=14.25 StartZ=0 EndX=-1.5 EndY=14.25 EndZ=0
    g44: LineSegment StartX=-49.19 StartY=11.5 StartZ=0 EndX=-1.5 EndY=11.5 EndZ=0
    g45: LineSegment StartX=-49.19 StartY=8.5 StartZ=0 EndX=-1.5 EndY=8.5 EndZ=0
    g46: LineSegment StartX=-49.19 StartY=5.75 StartZ=0 EndX=-1.5 EndY=5.75 EndZ=0
    g47: LineSegment StartX=-49.19 StartY=2.75 StartZ=0 EndX=-1.5 EndY=2.75 EndZ=0
  constraints (120):
    c: Vertical(g0)
    c: Distance(g0) = 3
    c: Block(g0)
    c: Vertical(g1)
    c: Distance(g1) = 3
    c: Vertical(g2)
    c: Equal(g0,g2) = 3
    c: Block(g2)
    c: Vertical(g3)
    c: Equal(g1,g3) = 3
    c: Vertical(g4)
    c: Equal(g0,g4) = 3
    c: Block(g4)
    c: Vertical(g5)
    c: Equal(g1,g5) = 3
    c: Vertical(g6)
    c: Equal(g0,g6) = 3
    c: Block(g6)
    c: Vertical(g7)
    c: Equal(g1,g7) = 3
    c: Vertical(g8)
    c: Equal(g0,g8) = 3
    c: Block(g8)
    c: Vertical(g9)
    c: Equal(g1,g9) = 3
    c: Vertical(g10)
    c: Equal(g0,g10) = 3
    c: Block(g10)
    c: Vertical(g11)
    c: Equal(g1,g11) = 3
    c: Block(g12)
    c: Block(g13)
    c: Block(g14)
    c: Block(g15)
    c: Block(g16)
    c: Block(g17)
    c: Block(g18)
    c: Block(g19)
    c: Block(g20)
    c: Block(g21)
    c: Block(g22)
    c: Block(g23)
    c: Block(g11)
    c: Block(g9)
    c: Block(g7)
    c: Block(g5)
    c: Block(g3)
    c: Block(g1)
    c: Coincident(g24,g0)
    c: Coincident(g24,g12)
    c: Horizontal(g24)
    c: Coincident(g25,g0)
    c: Coincident(g25,g12)
    c: Horizontal(g25)
    c: Coincident(g26,g1)
    c: Coincident(g26,g13)
    c: Horizontal(g26)
    c: Coincident(g27,g1)
    c: Coincident(g27,g13)
    c: Horizontal(g27)
    c: Coincident(g28,g2)
    c: Coincident(g28,g14)
    c: Horizontal(g28)
    c: Coincident(g29,g2)
    c: Coincident(g29,g14)
    c: Horizontal(g29)
    c: Coincident(g30,g3)
    c: Coincident(g30,g15)
    c: Horizontal(g30)
    c: Coincident(g31,g3)
    c: Coincident(g31,g15)
    c: Horizontal(g31)
    c: Coincident(g32,g4)
    c: Coincident(g32,g16)
    c: Horizontal(g32)
    c: Coincident(g33,g4)
    c: Coincident(g33,g16)
    c: Horizontal(g33)
    c: Coincident(g34,g5)
    c: Coincident(g34,g17)
    c: Horizontal(g34)
    c: Coincident(g35,g5)
    c: Coincident(g35,g17)
    c: Horizontal(g35)
    c: Coincident(g36,g6)
    c: Coincident(g36,g19)
    c: Horizontal(g36)
    c: Coincident(g37,g6)
    c: Coincident(g37,g19)
    c: Horizontal(g37)
    c: Coincident(g38,g7)
    c: Coincident(g38,g18)
    c: Horizontal(g38)
    c: Coincident(g39,g7)
    c: Coincident(g39,g18)
    c: Horizontal(g39)
    c: Coincident(g40,g8)
    c: Coincident(g40,g20)
    c: Horizontal(g40)
    c: Coincident(g41,g8)
    c: Coincident(g41,g20)
    c: Horizontal(g41)
    c: Coincident(g42,g9)
    c: Coincident(g42,g23)
    c: Horizontal(g42)
    c: Coincident(g43,g9)
    c: Coincident(g43,g23)
    c: Horizontal(g43)
    c: Coincident(g44,g10)
    c: Coincident(g44,g22)
    c: Horizontal(g44)
    c: Coincident(g45,g10)
    c: Coincident(g45,g22)
    c: Horizontal(g45)
    c: Coincident(g46,g11)
    c: Coincident(g46,g21)
    c: Horizontal(g46)
    c: Coincident(g47,g11)
    c: Coincident(g47,g21)
    c: Horizontal(g47)
FEATURE [Part::Extrusion] Extrude042
  Base = -> Sketch051
  Dir = (1,-2e-16,2e-16)
  DirMode = 2
  FaceMakerClass = Part::FaceMakerBullseye
  LengthFwd = 19
  LengthRev = 0
  Placement = pos=(-19,0,0) rot=(0,0,1;0rad)
  Solid = true
  Symmetric = false
FEATURE [Part::Fillet] Fillet035  label="removeToCreateVentalationHoles"
  Base = -> Extrude042
  Edges = <same value as first occurrence — deduplicated (x6 in doc)>
  Placement = pos=(7,0,0) rot=(0,0,1;0rad)
FEATURE [Part::Cut] Cut038  label="top017"
  Base = -> Cut033
  Tool = -> Fillet035
FEATURE [Sketcher::SketchObject] Sketch052  label="bottomSketch001"
  FullyConstrained = true
  sketch-geometry (45):
    g0: LineSegment StartX=6.29999 StartY=8 StartZ=0 EndX=3.29999 EndY=8 EndZ=0
    g1: LineSegment StartX=3.29999 StartY=8 StartZ=0 EndX=3.29999 EndY=-6.03275e-07 EndZ=0
    g2: ArcOfCircle CenterX=8.29999 CenterY=5 CenterZ=0 NormalX=0 NormalY=0 NormalZ=1 AngleXU=0 Radius=2 StartAngle=3.14159 EndAngle=4.71239
    g3: LineSegment StartX=6.29999 StartY=8 StartZ=0 EndX=6.29999 EndY=5 EndZ=0
    g4: ArcOfCircle CenterX=105 CenterY=19 CenterZ=0 NormalX=0 NormalY=0 NormalZ=1 AngleXU=0 Radius=12.7 StartAngle=4.71239 EndAngle=5.94289
    g5-g11: Circle x7 (B-spline internal-alignment scaffolding for g12; pole/knot coordinates omitted)
    g12: BSplineCurve PolesCount=7 KnotsCount=5 Degree=3 IsPeriodic=0
    g13-g17: GeomPoint x5 (B-spline internal-alignment scaffolding for g12; pole/knot coordinates omitted)
    g18: ArcOfCircle CenterX=105 CenterY=19 CenterZ=0 NormalX=0 NormalY=0 NormalZ=1 AngleXU=0 Radius=15.7 StartAngle=5.81226 EndAngle=6.28319
    g19: BSplineCurve PolesCount=5 KnotsCount=3 Degree=3 IsPeriodic=0
    g20: LineSegment StartX=8.29999 StartY=3 StartZ=0 EndX=101.7 EndY=3 EndZ=0
    g21: LineSegment StartX=3.29999 StartY=-6.03275e-07 StartZ=0 EndX=105 EndY=-6.03275e-07 EndZ=0
    g22: LineSegment StartX=120.974 StartY=8.71251 StartZ=0 EndX=122.332 EndY=7.83778 EndZ=0
    g23: LineSegment StartX=105 StartY=-6.03274e-07 StartZ=0 EndX=113 EndY=-6.03274e-07 EndZ=0
    g24: ArcOfCircle CenterX=105 CenterY=19 CenterZ=0 NormalX=0 NormalY=0 NormalZ=1 AngleXU=0 Radius=20.6155 StartAngle=5.11091 EndAngle=5.71103
    g25: ArcOfCircle CenterX=117.7 CenterY=19 CenterZ=0 NormalX=0 NormalY=0 NormalZ=1 AngleXU=0 Radius=3 StartAngle=1.2e-15 EndAngle=2.10468
    g26: Circle CenterX=116.345 CenterY=16.3232 CenterZ=0 NormalX=0 NormalY=0 NormalZ=1 AngleXU=0 Radius=1
    g27: Circle CenterX=117.24 CenterY=15.7584 CenterZ=0 NormalX=0 NormalY=0 NormalZ=1 AngleXU=0 Radius=1
    g28: Circle CenterX=116.972 CenterY=14.7612 CenterZ=0 NormalX=0 NormalY=0 NormalZ=1 AngleXU=0 Radius=1
    g29: BSplineCurve PolesCount=3 KnotsCount=2 Degree=2 IsPeriodic=0
    g30: GeomPoint X=116.345 Y=16.3232 Z=0
    g31: GeomPoint X=116.972 Y=14.7612 Z=0
    g32: Circle CenterX=115.828 CenterY=17.157 CenterZ=0 NormalX=0 NormalY=0 NormalZ=1 AngleXU=0 Radius=1
    g33: Circle CenterX=115.841 CenterY=16.639 CenterZ=0 NormalX=0 NormalY=0 NormalZ=1 AngleXU=0 Radius=1
    g34: Circle CenterX=116.345 CenterY=16.3232 CenterZ=0 NormalX=0 NormalY=0 NormalZ=1 AngleXU=0 Radius=1
    g35: BSplineCurve PolesCount=3 KnotsCount=2 Degree=2 IsPeriodic=0
    g36: GeomPoint X=115.828 Y=17.157 Z=0
    g37: GeomPoint X=116.345 Y=16.3232 Z=0
    g38: LineSegment StartX=115.828 StartY=17.157 StartZ=0 EndX=115.828 EndY=20.8307 EndZ=0
    g39: Circle CenterX=115.828 CenterY=20.8307 CenterZ=0 NormalX=0 NormalY=0 NormalZ=1 AngleXU=0 Radius=1
    g40: Circle CenterX=115.831 CenterY=21.3396 CenterZ=0 NormalX=0 NormalY=0 NormalZ=1 AngleXU=0 Radius=1
    g41: Circle CenterX=116.173 CenterY=21.5825 CenterZ=0 NormalX=0 NormalY=0 NormalZ=1 AngleXU=0 Radius=1
    g42: BSplineCurve PolesCount=3 KnotsCount=2 Degree=2 IsPeriodic=0
    g43: GeomPoint X=115.828 Y=20.8307 Z=0
    g44: GeomPoint X=116.173 Y=21.5825 Z=0
  constraints (70):
    c: Horizontal(g0)
    c: Distance(g0) = 3
    c: Coincident(g1,g0)
    c: Vertical(g1)
    c: Block(g2)
    c: Block(g0)
    c: Coincident(g3,g0)
    c: Coincident(g3,g2)
    c: Vertical(g3)
    c: Block(g1)
    c: Block(g4)
    c: Coincident(g19,g4)
    c: Block(g19)
    c: Equal(g5, g6-g11) x6
    c: InternalAlignment(g5-g11 -> g12) x7
    c: InternalAlignment(g13-g17 -> g12) x5
    c: Block(g12)
    c: Coincident(g18,g12)
    c: Block(g18)
    c: Coincident(g20,g2)
    c: Coincident(g20,g19)
    c: Horizontal(g20)
    c: Distance(g20) = 93.4
    c: Coincident(g21,g1)
    c: Horizontal(g21)
    c: Distance(g21) = 101.7
    c: Horizontal(g23)
    c: Distance(g23) = 8
    c: Coincident(g24,g23)
    c: Block(g23)
    c: Coincident(g22,g24)
    c: Block(g24)
    c: Block(g22)
    c: Distance(g22) = 1.61553
    c: Coincident(g25,g18)
    c: Block(g25)
    c: Weight(g26) = 1
    c: Equal(g26,g27)
    c: Equal(g26,g28)
    c: Coincident(g29,g4)
    c: InternalAlignment(g26,g29)
    c: InternalAlignment(g27,g29)
    c: InternalAlignment(g28,g29)
    c: InternalAlignment(g30,g29)
    c: InternalAlignment(g31,g29)
    c: Block(g29)
    c: Weight(g32) = 1
    c: Equal(g32,g33)
    c: Equal(g32,g34)
    c: Coincident(g35,g29)
    c: InternalAlignment(g32,g35)
    c: InternalAlignment(g33,g35)
    c: InternalAlignment(g34,g35)
    c: InternalAlignment(g36,g35)
    c: InternalAlignment(g37,g35)
    c: Block(g35)
    c: Coincident(g38,g35)
    c: Vertical(g38)
    c: Block(g38)
    c: Coincident(g42,g38)
    c: Weight(g39) = 1
    c: Equal(g39,g40)
    c: Equal(g39,g41)
    c: Coincident(g42,g25)
    c: InternalAlignment(g39,g42)
    c: InternalAlignment(g40,g42)
    c: InternalAlignment(g41,g42)
    c: InternalAlignment(g43,g42)
    c: InternalAlignment(g44,g42)
    c: Block(g42)
FEATURE [Part::Extrusion] Extrude043  label="bottom010"
  Base = -> Sketch052
  Dir = (0,0,1)
  DirMode = 2
  FaceMakerClass = Part::FaceMakerBullseye
  LengthFwd = 71.4
  LengthRev = 0
  Placement = pos=(0,0,0.3) rot=(0,0,1;0rad)
  Solid = true
  Symmetric = false
FEATURE [Sketcher::SketchObject] Sketch053  label="topSketch013"
  FullyConstrained = true
  sketch-geometry (22):
    g0: LineSegment StartX=5.21097e-06 StartY=3 StartZ=0 EndX=5.21097e-06 EndY=19 EndZ=0
    g1: ArcOfCircle CenterX=19 CenterY=19 CenterZ=0 NormalX=0 NormalY=0 NormalZ=1 AngleXU=0 Radius=19 StartAngle=1.5708 EndAngle=3.14159
    g2: ArcOfCircle CenterX=19 CenterY=19 CenterZ=0 NormalX=0 NormalY=0 NormalZ=1 AngleXU=0 Radius=16 StartAngle=1.5708 EndAngle=3.14159
    g3: LineSegment StartX=114 StartY=35 StartZ=0 EndX=19 EndY=35 EndZ=0
    g4: LineSegment StartX=5.21097e-06 StartY=3 StartZ=0 EndX=5.21097e-06 EndY=0 EndZ=0
    g5: LineSegment StartX=3 StartY=0 StartZ=0 EndX=5.21097e-06 EndY=0 EndZ=0
    g6: LineSegment StartX=3 StartY=19 StartZ=0 EndX=3 EndY=0 EndZ=0
    g7: LineSegment StartX=19 StartY=38 StartZ=0 EndX=124 EndY=38 EndZ=0
    g8: Circle CenterX=119 CenterY=35 CenterZ=0 NormalX=0 NormalY=0 NormalZ=1 AngleXU=0 Radius=1
    g9: Circle CenterX=121 CenterY=35 CenterZ=0 NormalX=0 NormalY=0 NormalZ=1 AngleXU=0 Radius=1
    g10: Circle CenterX=121 CenterY=33 CenterZ=0 NormalX=0 NormalY=0 NormalZ=1 AngleXU=0 Radius=1
    g11: BSplineCurve PolesCount=3 KnotsCount=2 Degree=2 IsPeriodic=0
    g12: GeomPoint X=119 Y=35 Z=0
    g13: GeomPoint X=121 Y=33 Z=0
    g14: LineSegment StartX=119 StartY=35 StartZ=0 EndX=114 EndY=35 EndZ=0
    g15: ArcOfCircle CenterX=105 CenterY=19 CenterZ=0 NormalX=0 NormalY=0 NormalZ=1 AngleXU=0 Radius=16 StartAngle=5.60905 EndAngle=6.28319
    g16: LineSegment StartX=121 StartY=33 StartZ=0 EndX=121 EndY=19 EndZ=0
    g17: LineSegment StartX=117.5 StartY=9.01251 StartZ=0 EndX=121.163 EndY=9.0125 EndZ=0
    g18: ArcOfCircle CenterX=105 CenterY=19 CenterZ=0 NormalX=0 NormalY=0 NormalZ=1 AngleXU=0 Radius=20.6155 StartAngle=5.7297 EndAngle=6.28319
    g19: LineSegment StartX=121.163 StartY=9.0125 StartZ=0 EndX=122.538 EndY=8.16329 EndZ=0
    g20: LineSegment StartX=124 StartY=38 StartZ=0 EndX=125.616 EndY=38 EndZ=0
    g21: LineSegment StartX=125.616 StartY=19 StartZ=0 EndX=125.616 EndY=38 EndZ=0
  constraints (50):
    c: Vertical(g0)
    c: Block(g0)
    c: Coincident(g1,g0)
    c: Block(g1)
    c: Coincident(g2,g1)
    c: Block(g2)
    c: Coincident(g3,g2)
    c: Horizontal(g3)
    c: Tangent(g3,g2)
    c: Coincident(g4,g0)
    c: Distance(g4) = 3
    c: Vertical(g4)
    c: Coincident(g5,g4)
    c: Horizontal(g5)
    c: Coincident(g6,g2)
    c: Coincident(g6,g5)
    c: Vertical(g6)
    c: Horizontal(g7)
    c: Distance(g7) = 105
    c: Coincident(g7,g1)
    c: Block(g3)
    c: Weight(g8) = 1
    c: Equal(g8,g9)
    c: Equal(g8,g10)
    c: InternalAlignment(g8,g11)
    c: InternalAlignment(g9,g11)
    c: InternalAlignment(g10,g11)
    c: InternalAlignment(g12,g11)
    c: InternalAlignment(g13,g11)
    c: Block(g11)
    c: Coincident(g14,g11)
    c: Coincident(g14,g3)
    c: Horizontal(g14)
    c: Block(g15)
    c: Coincident(g16,g11)
    c: Coincident(g16,g15)
    c: Vertical(g16)
    c: Distance(g16) = 14
    c: Coincident(g17,g15)
    c: Block(g18)
    c: Coincident(g19,g18)
    c: Coincident(g20,g7)
    c: Horizontal(g20)
    c: Vertical(g21)
    c: Coincident(g20,g21)
    c: Block(g20)
    c: Block(g21)
    c: Block(g19)
    c: Block(g17)
    c: Distance(g20) = 1.61553
FEATURE [Part::Extrusion] Extrude044
  Base = -> Sketch053
  Dir = (0,0,1)
  DirMode = 2
  FaceMakerClass = Part::FaceMakerBullseye
  LengthFwd = 72
  LengthRev = 0
  Solid = true
  Symmetric = false
FEATURE [Part::Fillet] Fillet036  label="top018"
  Base = -> Extrude044
  Edges = 1 edges r=2: [Edge41]
FEATURE [Sketcher::SketchObject] Sketch054
  FullyConstrained = false
  Placement = pos=(0,0,0) rot=(1,0,0;1.5708rad)
  sketch-geometry (24):
    g0: ArcOfCircle CenterX=-4 CenterY=-10.5 CenterZ=0 NormalX=0 NormalY=0 NormalZ=1 AngleXU=0 Radius=1.5 StartAngle=6e-16 EndAngle=3.14159
    g1: ArcOfCircle CenterX=-34.2 CenterY=-10.5 CenterZ=0 NormalX=0 NormalY=0 NormalZ=1 AngleXU=0 Radius=1.5 StartAngle=0 EndAngle=3.14159
    g2: ArcOfCircle CenterX=-34.2 CenterY=-27.7 CenterZ=0 NormalX=0 NormalY=0 NormalZ=1 AngleXU=0 Radius=1.5 StartAngle=3.14159 EndAngle=6.28319
    g3: ArcOfCircle CenterX=-4 CenterY=-27.7 CenterZ=0 NormalX=0 NormalY=0 NormalZ=1 AngleXU=0 Radius=1.5 StartAngle=3.1416 EndAngle=6.28319
    g4: ArcOfCircle CenterX=-10 CenterY=-4.3 CenterZ=0 NormalX=0 NormalY=0 NormalZ=1 AngleXU=0 Radius=1.5 StartAngle=2e-16 EndAngle=3.14159
    g5: ArcOfCircle CenterX=-16.1 CenterY=-1.8 CenterZ=0 NormalX=0 NormalY=0 NormalZ=1 AngleXU=0 Radius=1.5 StartAngle=5e-16 EndAngle=3.14159
    g6: ArcOfCircle CenterX=-22.1 CenterY=-1.8 CenterZ=0 NormalX=0 NormalY=0 NormalZ=1 AngleXU=0 Radius=1.5 StartAngle=5e-16 EndAngle=3.14159
    g7: ArcOfCircle CenterX=-28.2 CenterY=-4.3 CenterZ=0 NormalX=0 NormalY=0 NormalZ=1 AngleXU=0 Radius=1.5 StartAngle=2e-16 EndAngle=3.14159
    g8: ArcOfCircle CenterX=-10 CenterY=-33.9 CenterZ=0 NormalX=0 NormalY=0 NormalZ=1 AngleXU=0 Radius=1.5 StartAngle=3.14159 EndAngle=6.28319
    g9: ArcOfCircle CenterX=-16.1 CenterY=-36.4 CenterZ=0 NormalX=0 NormalY=0 NormalZ=1 AngleXU=0 Radius=1.5 StartAngle=3.14159 EndAngle=6.28319
    g10: ArcOfCircle CenterX=-22.1 CenterY=-36.4 CenterZ=0 NormalX=0 NormalY=0 NormalZ=1 AngleXU=0 Radius=1.5 StartAngle=3.14159 EndAngle=6.28319
    g11: ArcOfCircle CenterX=-28.2 CenterY=-33.9 CenterZ=0 NormalX=0 NormalY=0 NormalZ=1 AngleXU=0 Radius=1.5 StartAngle=3.14159 EndAngle=6.28319
    g12: LineSegment StartX=-35.7 StartY=-10.5 StartZ=0 EndX=-35.7 EndY=-27.7 EndZ=0
    g13: LineSegment StartX=-32.7 StartY=-10.5 StartZ=0 EndX=-32.7 EndY=-27.7 EndZ=0
    g14: LineSegment StartX=-29.7 StartY=-33.9 StartZ=0 EndX=-29.7 EndY=-4.3 EndZ=0
    g15: LineSegment StartX=-26.7 StartY=-33.9 StartZ=0 EndX=-26.7 EndY=-4.3 EndZ=0
    g16: LineSegment StartX=-2.5 StartY=-10.5 StartZ=0 EndX=-2.5 EndY=-27.7 EndZ=0
    g17: LineSegment StartX=-8.5 StartY=-4.3 StartZ=0 EndX=-8.5 EndY=-33.9 EndZ=0
    g18: LineSegment StartX=-5.5 StartY=-10.5 StartZ=0 EndX=-5.5 EndY=-27.7 EndZ=0
    g19: LineSegment StartX=-11.5 StartY=-4.3 StartZ=0 EndX=-11.5 EndY=-33.9 EndZ=0
    g20: LineSegment StartX=-14.6 StartY=-1.8 StartZ=0 EndX=-14.6 EndY=-36.4 EndZ=0
    g21: LineSegment StartX=-17.6 StartY=-1.8 StartZ=0 EndX=-17.6 EndY=-36.4 EndZ=0
    g22: LineSegment StartX=-20.6 StartY=-36.4 StartZ=0 EndX=-20.6 EndY=-1.8 EndZ=0
    g23: LineSegment StartX=-23.6 StartY=-1.8 StartZ=0 EndX=-23.6 EndY=-36.4 EndZ=0
  constraints (48):
    c: Block(g0)
    c: Block(g1)
    c: Block(g2)
    c: Block(g3)
    c: Block(g4)
    c: Block(g5)
    c: Block(g6)
    c: Block(g7)
    c: Block(g8)
    c: Block(g9)
    c: Block(g10)
    c: Block(g11)
    c: Coincident(g12,g1)
    c: Coincident(g12,g2)
    c: Vertical(g12)
    c: Coincident(g13,g1)
    c: Coincident(g13,g2)
    c: Vertical(g13)
    c: Coincident(g14,g11)
    c: Coincident(g14,g7)
    c: Vertical(g14)
    c: Coincident(g15,g11)
    c: Coincident(g15,g7)
    c: Vertical(g15)
    c: Coincident(g16,g0)
    c: Coincident(g16,g3)
    c: Vertical(g16)
    c: Coincident(g17,g4)
    c: Coincident(g17,g8)
    c: Vertical(g17)
    c: Coincident(g18,g0)
    c: Coincident(g18,g3)
    c: Vertical(g18)
    c: Coincident(g19,g4)
    c: Coincident(g19,g8)
    c: Vertical(g19)
    c: Coincident(g20,g5)
    c: Coincident(g20,g9)
    c: Vertical(g20)
    c: Coincident(g21,g5)
    c: Coincident(g21,g9)
    c: Vertical(g21)
    c: Coincident(g22,g10)
    c: Coincident(g22,g6)
    c: Vertical(g22)
    c: Coincident(g23,g6)
    c: Coincident(g23,g10)
    c: Vertical(g23)
FEATURE [Part::Extrusion] Extrude045  label="removeToCreateFanGrillHoles003"
  Base = -> Sketch054
  Dir = (0,-1,6e-16)
  DirMode = 2
  FaceMakerClass = Part::FaceMakerBullseye
  LengthFwd = 10
  LengthRev = 0
  Placement = pos=(65.4,44,54.82) rot=(0,0,1;0rad)
  Solid = true
  Symmetric = false
FEATURE [Part::Feature] Face105 .. Face108  x4 (patterned run collapsed; names and placements below)
  shape: bbox 3.5 x 17.8 x 2e-07 mm, 1 faces, 0 solids (baked)
FEATURE [Part::Revolution] Revolve113  label="removeToCreateScrewAndThreadedInsertHole041"
  Angle = 360
  Axis = (0,1,0)
  Base = (0,0,0)
  FaceMakerClass = Part::FaceMakerBullseye
  Placement = pos=(62.3,30.3,19.7) rot=(0,0,1;0rad)
  Solid = false
  Source = -> Face105
  Symmetric = false
FEATURE [Part::Revolution] Revolve114  label="removeToCreateScrewAndThreadedInsertHole042"
  Angle = 360
  Axis = (0,1,0)
  Base = (0,0,0)
  FaceMakerClass = Part::FaceMakerBullseye
  Placement = pos=(62.3,30.3,51.7) rot=(0,0,1;0rad)
  Solid = false
  Source = -> Face106
  Symmetric = false
FEATURE [Part::Revolution] Revolve115  label="removeToCreateScrewAndThreadedInsertHole043"
  Angle = 360
  Axis = (0,1,0)
  Base = (0,0,0)
  FaceMakerClass = Part::FaceMakerBullseye
  Placement = pos=(30.3,30.3,19.7) rot=(0,0,1;0rad)
  Solid = false
  Source = -> Face107
  Symmetric = false
FEATURE [Part::Revolution] Revolve116  label="removeToCreateScrewAndThreadedInsertHole044"
  Angle = 360
  Axis = (0,1,0)
  Base = (0,0,0)
  FaceMakerClass = Part::FaceMakerBullseye
  Placement = pos=(30.3,30.3,51.7) rot=(0,0,1;0rad)
  Solid = false
  Source = -> Face108
  Symmetric = false
FEATURE [Part::MultiFuse] Fusion083  label="createThreadedInsertHolesForFan004"
  Shapes = -> [Revolve113,Revolve114,Revolve115,Revolve116]
FEATURE [Part::Box] Box024  label="removeToCreteHoleForPlugHousing026"
  AttacherType = Attacher::AttachEngine3D
  Height = 28.6
  Length = 10
  Placement = pos=(-2,0,21.7) rot=(0,0,1;0rad)
  Width = 19
FEATURE [Part::Cylinder] Cylinder038  label="removeToCreteHoleForPlugHousing027"
  Angle = 360
  AttacherType = Attacher::AttachEngine3D
  Height = 20
  Placement = pos=(-2,19,36) rot=(0,1,0;1.5708rad)
  Radius = 14.3
FEATURE [Part::MultiFuse] Fusion084  label="removeToCreteHoleForPlugHousing028"
  Shapes = -> [Box024,Cylinder038]
FEATURE [Part::Cylinder] Cylinder039
  Angle = 360
  AttacherType = Attacher::AttachEngine3D
  Height = 20
  Placement = pos=(0,0,36.15) rot=(0,0,1;0rad)
  Radius = 14.3
FEATURE [Part::Cylinder] Cylinder040
  Angle = 360
  AttacherType = Attacher::AttachEngine3D
  Height = 10
  Placement = pos=(0,0,36.15) rot=(0,0,1;0rad)
  Radius = 4
FEATURE [Part::Box] Box025  label="removeToCreteHoleForPlugHousing030"
  AttacherType = Attacher::AttachEngine3D
  Height = 28.6
  Length = 20
  Placement = pos=(106.15,0,21.7) rot=(0,0,1;0rad)
  Width = 19
FEATURE [Part::MultiFuse] Fusion086  label="removeToCreteHoleForPlugHousing031"
  Placement = pos=(70,19,36) rot=(0,1,0;1.5708rad)
  Shapes = -> [Cylinder039,Cylinder040]
FEATURE [Part::MultiFuse] Fusion085  label="removeToCreteHoleForPlugHousing029"
  Shapes = -> [Box025,Fusion086]
FEATURE [Sketcher::SketchObject] Sketch055
  FullyConstrained = true
  Placement = pos=(117,19,0) rot=(0.57735,0.57735,0.57735;2.0944rad)
  sketch-geometry (48):
    g0: LineSegment StartX=-49.19 StartY=69.25 StartZ=0 EndX=-49.19 EndY=66.25 EndZ=0
    g1: LineSegment StartX=-49.19 StartY=63.5 StartZ=0 EndX=-49.19 EndY=60.5 EndZ=0
    g2: LineSegment StartX=-49.19 StartY=57.75 StartZ=0 EndX=-49.19 EndY=54.75 EndZ=0
    g3: LineSegment StartX=-49.19 StartY=52 StartZ=0 EndX=-49.19 EndY=49 EndZ=0
    g4: LineSegment StartX=-49.19 StartY=46.25 StartZ=0 EndX=-49.19 EndY=43.25 EndZ=0
    g5: LineSegment StartX=-49.19 StartY=40.5 StartZ=0 EndX=-49.19 EndY=37.5 EndZ=0
    g6: LineSegment StartX=-49.19 StartY=34.5 StartZ=0 EndX=-49.19 EndY=31.5 EndZ=0
    g7: LineSegment StartX=-49.19 StartY=28.75 StartZ=0 EndX=-49.19 EndY=25.75 EndZ=0
    g8: LineSegment StartX=-49.19 StartY=23 StartZ=0 EndX=-49.19 EndY=20 EndZ=0
    g9: LineSegment StartX=-49.19 StartY=17.25 StartZ=0 EndX=-49.19 EndY=14.25 EndZ=0
    g10: LineSegment StartX=-49.19 StartY=11.5 StartZ=0 EndX=-49.19 EndY=8.5 EndZ=0
    g11: LineSegment StartX=-49.19 StartY=5.75 StartZ=0 EndX=-49.19 EndY=2.75 EndZ=0
    g12: ArcOfCircle CenterX=-1.5 CenterY=67.75 CenterZ=0 NormalX=0 NormalY=0 NormalZ=1 AngleXU=0 Radius=1.5 StartAngle=4.71239 EndAngle=7.85398
    g13: ArcOfCircle CenterX=-1.5 CenterY=62 CenterZ=0 NormalX=0 NormalY=0 NormalZ=1 AngleXU=0 Radius=1.5 StartAngle=4.71239 EndAngle=7.85398
    g14: ArcOfCircle CenterX=-1.5 CenterY=56.25 CenterZ=0 NormalX=0 NormalY=0 NormalZ=1 AngleXU=0 Radius=1.5 StartAngle=4.71239 EndAngle=7.85398
    g15: ArcOfCircle CenterX=-11.49 CenterY=50.5 CenterZ=0 NormalX=0 NormalY=0 NormalZ=1 AngleXU=0 Radius=1.5 StartAngle=4.71239 EndAngle=7.85398
    g16: ArcOfCircle CenterX=-16.28 CenterY=44.75 CenterZ=0 NormalX=0 NormalY=0 NormalZ=1 AngleXU=0 Radius=1.5 StartAngle=4.71239 EndAngle=7.85398
    g17: ArcOfCircle CenterX=-18.2337 CenterY=39 CenterZ=0 NormalX=0 NormalY=0 NormalZ=1 AngleXU=0 Radius=1.5 StartAngle=4.71485 EndAngle=7.85398
    g18: ArcOfCircle CenterX=-16.2837 CenterY=27.25 CenterZ=0 NormalX=0 NormalY=0 NormalZ=1 AngleXU=0 Radius=1.5 StartAngle=4.71485 EndAngle=7.85398
    g19: ArcOfCircle CenterX=-18.2337 CenterY=33 CenterZ=0 NormalX=0 NormalY=0 NormalZ=1 AngleXU=0 Radius=1.5 StartAngle=4.71485 EndAngle=7.85398
    g20: ArcOfCircle CenterX=-11.49 CenterY=21.5 CenterZ=0 NormalX=0 NormalY=0 NormalZ=1 AngleXU=0 Radius=1.5 StartAngle=4.71239 EndAngle=7.85398
    g21: ArcOfCircle CenterX=-1.5 CenterY=4.25 CenterZ=0 NormalX=0 NormalY=0 NormalZ=1 AngleXU=0 Radius=1.5 StartAngle=4.71239 EndAngle=7.85398
    g22: ArcOfCircle CenterX=-1.5 CenterY=10 CenterZ=0 NormalX=0 NormalY=0 NormalZ=1 AngleXU=0 Radius=1.5 StartAngle=4.71239 EndAngle=7.85398
    g23: ArcOfCircle CenterX=-1.5 CenterY=15.75 CenterZ=0 NormalX=0 NormalY=0 NormalZ=1 AngleXU=0 Radius=1.5 StartAngle=4.71239 EndAngle=7.85398
    g24: LineSegment StartX=-49.19 StartY=69.25 StartZ=0 EndX=-1.5 EndY=69.25 EndZ=0
    g25: LineSegment StartX=-49.19 StartY=66.25 StartZ=0 EndX=-1.5 EndY=66.25 EndZ=0
    g26: LineSegment StartX=-49.19 StartY=63.5 StartZ=0 EndX=-1.5 EndY=63.5 EndZ=0
    g27: LineSegment StartX=-49.19 StartY=60.5 StartZ=0 EndX=-1.5 EndY=60.5 EndZ=0
    g28: LineSegment StartX=-49.19 StartY=57.75 StartZ=0 EndX=-1.5 EndY=57.75 EndZ=0
    g29: LineSegment StartX=-49.19 StartY=54.75 StartZ=0 EndX=-1.5 EndY=54.75 EndZ=0
    g30: LineSegment StartX=-49.19 StartY=52 StartZ=0 EndX=-11.49 EndY=52 EndZ=0
    g31: LineSegment StartX=-49.19 StartY=49 StartZ=0 EndX=-11.49 EndY=49 EndZ=0
    g32: LineSegment StartX=-49.19 StartY=46.25 StartZ=0 EndX=-16.28 EndY=46.25 EndZ=0
    g33: LineSegment StartX=-49.19 StartY=43.25 StartZ=0 EndX=-16.28 EndY=43.25 EndZ=0
    g34: LineSegment StartX=-49.19 StartY=40.5 StartZ=0 EndX=-18.2337 EndY=40.5 EndZ=0
    g35: LineSegment StartX=-49.19 StartY=37.5 StartZ=0 EndX=-18.23 EndY=37.5 EndZ=0
    g36: LineSegment StartX=-49.19 StartY=34.5 StartZ=0 EndX=-18.2337 EndY=34.5 EndZ=0
    g37: LineSegment StartX=-49.19 StartY=31.5 StartZ=0 EndX=-18.23 EndY=31.5 EndZ=0
    g38: LineSegment StartX=-49.19 StartY=28.75 StartZ=0 EndX=-16.2837 EndY=28.75 EndZ=0
    g39: LineSegment StartX=-49.19 StartY=25.75 StartZ=0 EndX=-16.28 EndY=25.75 EndZ=0
    g40: LineSegment StartX=-49.19 StartY=23 StartZ=0 EndX=-11.49 EndY=23 EndZ=0
    g41: LineSegment StartX=-49.19 StartY=20 StartZ=0 EndX=-11.49 EndY=20 EndZ=0
    g42: LineSegment StartX=-49.19 StartY=17.25 StartZ=0 EndX=-1.5 EndY=17.25 EndZ=0
    g43: LineSegment StartX=-49.19 StartY=14.25 StartZ=0 EndX=-1.5 EndY=14.25 EndZ=0
    g44: LineSegment StartX=-49.19 StartY=11.5 StartZ=0 EndX=-1.5 EndY=11.5 EndZ=0
    g45: LineSegment StartX=-49.19 StartY=8.5 StartZ=0 EndX=-1.5 EndY=8.5 EndZ=0
    g46: LineSegment StartX=-49.19 StartY=5.75 StartZ=0 EndX=-1.5 EndY=5.75 EndZ=0
    g47: LineSegment StartX=-49.19 StartY=2.75 StartZ=0 EndX=-1.5 EndY=2.75 EndZ=0
  constraints (120):
    c: Vertical(g0)
    c: Distance(g0) = 3
    c: Block(g0)
    c: Vertical(g1)
    c: Distance(g1) = 3
    c: Vertical(g2)
    c: Equal(g0,g2) = 3
    c: Block(g2)
    c: Vertical(g3)
    c: Equal(g1,g3) = 3
    c: Vertical(g4)
    c: Equal(g0,g4) = 3
    c: Block(g4)
    c: Vertical(g5)
    c: Equal(g1,g5) = 3
    c: Vertical(g6)
    c: Equal(g0,g6) = 3
    c: Block(g6)
    c: Vertical(g7)
    c: Equal(g1,g7) = 3
    c: Vertical(g8)
    c: Equal(g0,g8) = 3
    c: Block(g8)
    c: Vertical(g9)
    c: Equal(g1,g9) = 3
    c: Vertical(g10)
    c: Equal(g0,g10) = 3
    c: Block(g10)
    c: Vertical(g11)
    c: Equal(g1,g11) = 3
    c: Block(g12)
    c: Block(g13)
    c: Block(g14)
    c: Block(g15)
    c: Block(g16)
    c: Block(g17)
    c: Block(g18)
    c: Block(g19)
    c: Block(g20)
    c: Block(g21)
    c: Block(g22)
    c: Block(g23)
    c: Block(g11)
    c: Block(g9)
    c: Block(g7)
    c: Block(g5)
    c: Block(g3)
    c: Block(g1)
    c: Coincident(g24,g0)
    c: Coincident(g24,g12)
    c: Horizontal(g24)
    c: Coincident(g25,g0)
    c: Coincident(g25,g12)
    c: Horizontal(g25)
    c: Coincident(g26,g1)
    c: Coincident(g26,g13)
    c: Horizontal(g26)
    c: Coincident(g27,g1)
    c: Coincident(g27,g13)
    c: Horizontal(g27)
    c: Coincident(g28,g2)
    c: Coincident(g28,g14)
    c: Horizontal(g28)
    c: Coincident(g29,g2)
    c: Coincident(g29,g14)
    c: Horizontal(g29)
    c: Coincident(g30,g3)
    c: Coincident(g30,g15)
    c: Horizontal(g30)
    c: Coincident(g31,g3)
    c: Coincident(g31,g15)
    c: Horizontal(g31)
    c: Coincident(g32,g4)
    c: Coincident(g32,g16)
    c: Horizontal(g32)
    c: Coincident(g33,g4)
    c: Coincident(g33,g16)
    c: Horizontal(g33)
    c: Coincident(g34,g5)
    c: Coincident(g34,g17)
    c: Horizontal(g34)
    c: Coincident(g35,g5)
    c: Coincident(g35,g17)
    c: Horizontal(g35)
    c: Coincident(g36,g6)
    c: Coincident(g36,g19)
    c: Horizontal(g36)
    c: Coincident(g37,g6)
    c: Coincident(g37,g19)
    c: Horizontal(g37)
    c: Coincident(g38,g7)
    c: Coincident(g38,g18)
    c: Horizontal(g38)
    c: Coincident(g39,g7)
    c: Coincident(g39,g18)
    c: Horizontal(g39)
    c: Coincident(g40,g8)
    c: Coincident(g40,g20)
    c: Horizontal(g40)
    c: Coincident(g41,g8)
    c: Coincident(g41,g20)
    c: Horizontal(g41)
    c: Coincident(g42,g9)
    c: Coincident(g42,g23)
    c: Horizontal(g42)
    c: Coincident(g43,g9)
    c: Coincident(g43,g23)
    c: Horizontal(g43)
    c: Coincident(g44,g10)
    c: Coincident(g44,g22)
    c: Horizontal(g44)
    c: Coincident(g45,g10)
    c: Coincident(g45,g22)
    c: Horizontal(g45)
    c: Coincident(g46,g11)
    c: Coincident(g46,g21)
    c: Horizontal(g46)
    c: Coincident(g47,g11)
    c: Coincident(g47,g21)
    c: Horizontal(g47)
FEATURE [Part::Extrusion] Extrude046
  Base = -> Sketch055
  Dir = (1,0,0)
  DirMode = 2
  FaceMakerClass = Part::FaceMakerBullseye
  LengthFwd = 23
  LengthRev = 0
  Placement = pos=(-19,0,0) rot=(0,0,1;0rad)
  Solid = true
  Symmetric = false
FEATURE [Part::Fillet] Fillet038  label="removeToCreateVentalationHoles001"
  Base = -> Extrude046
  Edges = <same value as first occurrence — deduplicated (x6 in doc)>
  Placement = pos=(7,0,0) rot=(0,0,1;0rad)
FEATURE [Sketcher::SketchObject] Sketch056  label="topSketch014"
  FullyConstrained = true
  sketch-geometry (22):
    g0: LineSegment StartX=5.21097e-06 StartY=3 StartZ=0 EndX=5.21097e-06 EndY=19 EndZ=0
    g1: ArcOfCircle CenterX=19 CenterY=19 CenterZ=0 NormalX=0 NormalY=0 NormalZ=1 AngleXU=0 Radius=19 StartAngle=1.5708 EndAngle=3.14159
    g2: ArcOfCircle CenterX=19 CenterY=19 CenterZ=0 NormalX=0 NormalY=0 NormalZ=1 AngleXU=0 Radius=16 StartAngle=1.5708 EndAngle=3.14159
    g3: LineSegment StartX=114 StartY=35 StartZ=0 EndX=19 EndY=35 EndZ=0
    g4: LineSegment StartX=5.21097e-06 StartY=3 StartZ=0 EndX=5.21097e-06 EndY=0 EndZ=0
    g5: LineSegment StartX=3 StartY=0 StartZ=0 EndX=5.21097e-06 EndY=0 EndZ=0
    g6: LineSegment StartX=3 StartY=19 StartZ=0 EndX=3 EndY=0 EndZ=0
    g7: LineSegment StartX=19 StartY=38 StartZ=0 EndX=124 EndY=38 EndZ=0
    g8: Circle CenterX=119 CenterY=35 CenterZ=0 NormalX=0 NormalY=0 NormalZ=1 AngleXU=0 Radius=1
    g9: Circle CenterX=121 CenterY=35 CenterZ=0 NormalX=0 NormalY=0 NormalZ=1 AngleXU=0 Radius=1
    g10: Circle CenterX=121 CenterY=33 CenterZ=0 NormalX=0 NormalY=0 NormalZ=1 AngleXU=0 Radius=1
    g11: BSplineCurve PolesCount=3 KnotsCount=2 Degree=2 IsPeriodic=0
    g12: GeomPoint X=119 Y=35 Z=0
    g13: GeomPoint X=121 Y=33 Z=0
    g14: LineSegment StartX=119 StartY=35 StartZ=0 EndX=114 EndY=35 EndZ=0
    g15: ArcOfCircle CenterX=105 CenterY=19 CenterZ=0 NormalX=0 NormalY=0 NormalZ=1 AngleXU=0 Radius=16 StartAngle=5.60905 EndAngle=6.28319
    g16: LineSegment StartX=121 StartY=33 StartZ=0 EndX=121 EndY=19 EndZ=0
    g17: LineSegment StartX=117.5 StartY=9.01251 StartZ=0 EndX=121.163 EndY=9.0125 EndZ=0
    g18: ArcOfCircle CenterX=105 CenterY=19 CenterZ=0 NormalX=0 NormalY=0 NormalZ=1 AngleXU=0 Radius=20.6155 StartAngle=5.7297 EndAngle=6.28319
    g19: LineSegment StartX=121.163 StartY=9.0125 StartZ=0 EndX=122.538 EndY=8.16329 EndZ=0
    g20: LineSegment StartX=124 StartY=38 StartZ=0 EndX=125.616 EndY=38 EndZ=0
    g21: LineSegment StartX=125.616 StartY=19 StartZ=0 EndX=125.616 EndY=38 EndZ=0
  constraints (49):
    c: Vertical(g0)
    c: Block(g0)
    c: Coincident(g1,g0)
    c: Block(g1)
    c: Coincident(g2,g1)
    c: Block(g2)
    c: Coincident(g3,g2)
    c: Horizontal(g3)
    c: Tangent(g3,g2)
    c: Coincident(g4,g0)
    c: Distance(g4) = 3
    c: Vertical(g4)
    c: Coincident(g5,g4)
    c: Horizontal(g5)
    c: Coincident(g6,g2)
    c: Coincident(g6,g5)
    c: Vertical(g6)
    c: Horizontal(g7)
    c: Distance(g7) = 105
    c: Coincident(g7,g1)
    c: Block(g3)
    c: Weight(g8) = 1
    c: Equal(g8,g9)
    c: Equal(g8,g10)
    c: InternalAlignment(g8,g11)
    c: InternalAlignment(g9,g11)
    c: InternalAlignment(g10,g11)
    c: InternalAlignment(g12,g11)
    c: InternalAlignment(g13,g11)
    c: Block(g11)
    c: Coincident(g14,g11)
    c: Coincident(g14,g3)
    c: Horizontal(g14)
    c: Block(g15)
    c: Coincident(g16,g11)
    c: Coincident(g16,g15)
    c: Vertical(g16)
    c: Distance(g16) = 14
    c: Coincident(g17,g15)
    c: Block(g18)
    c: Coincident(g19,g18)
    c: Coincident(g20,g7)
    c: Horizontal(g20)
    c: Vertical(g21)
    c: Coincident(g20,g21)
    c: Block(g20)
    c: Block(g21)
    c: Block(g19)
    c: Block(g17)
FEATURE [Part::Box] Box026  label="removeToCreteHoleForPlugHousing032"
  AttacherType = Attacher::AttachEngine3D
  Height = 28.6
  Length = 10
  Placement = pos=(-2,0,21.7) rot=(0,0,1;0rad)
  Width = 19
FEATURE [Part::Feature] Face109 .. Face112  x4 (patterned run collapsed; names and placements below)
  shape: bbox 3.5 x 17.8 x 2e-07 mm, 1 faces, 0 solids (baked)
FEATURE [Part::Revolution] Revolve117  label="removeToCreateScrewAndThreadedInsertHole045"
  Angle = 360
  Axis = (0,1,0)
  Base = (0,0,0)
  FaceMakerClass = Part::FaceMakerBullseye
  Placement = pos=(62.3,30.3,19.7) rot=(0,0,1;0rad)
  Solid = false
  Source = -> Face109
  Symmetric = false
FEATURE [Part::Revolution] Revolve118  label="removeToCreateScrewAndThreadedInsertHole046"
  Angle = 360
  Axis = (0,1,0)
  Base = (0,0,0)
  FaceMakerClass = Part::FaceMakerBullseye
  Placement = pos=(62.3,30.3,51.7) rot=(0,0,1;0rad)
  Solid = false
  Source = -> Face110
  Symmetric = false
FEATURE [Part::Revolution] Revolve119  label="removeToCreateScrewAndThreadedInsertHole047"
  Angle = 360
  Axis = (0,1,0)
  Base = (0,0,0)
  FaceMakerClass = Part::FaceMakerBullseye
  Placement = pos=(30.3,30.3,19.7) rot=(0,0,1;0rad)
  Solid = false
  Source = -> Face111
  Symmetric = false
FEATURE [Part::Revolution] Revolve120  label="removeToCreateScrewAndThreadedInsertHole048"
  Angle = 360
  Axis = (0,1,0)
  Base = (0,0,0)
  FaceMakerClass = Part::FaceMakerBullseye
  Placement = pos=(30.3,30.3,51.7) rot=(0,0,1;0rad)
  Solid = false
  Source = -> Face112
  Symmetric = false
FEATURE [Part::MultiFuse] Fusion087  label="createThreadedInsertHolesForFan005"
  Shapes = -> [Revolve117,Revolve118,Revolve119,Revolve120]
FEATURE [Part::Extrusion] Extrude047
  Base = -> Sketch056
  Dir = (0,0,1)
  DirMode = 2
  FaceMakerClass = Part::FaceMakerBullseye
  LengthFwd = 72
  LengthRev = 0
  Solid = true
  Symmetric = false
FEATURE [Part::Fillet] Fillet039  label="top019"
  Base = -> Extrude047
  Edges = 1 edges r=2: [Edge35]
FEATURE [Sketcher::SketchObject] Sketch057
  FullyConstrained = false
  Placement = pos=(0,0,0) rot=(1,0,0;1.5708rad)
  sketch-geometry (24):
    g0: ArcOfCircle CenterX=-4 CenterY=-10.5 CenterZ=0 NormalX=0 NormalY=0 NormalZ=1 AngleXU=0 Radius=1.5 StartAngle=6e-16 EndAngle=3.14159
    g1: ArcOfCircle CenterX=-34.2 CenterY=-10.5 CenterZ=0 NormalX=0 NormalY=0 NormalZ=1 AngleXU=0 Radius=1.5 StartAngle=0 EndAngle=3.14159
    g2: ArcOfCircle CenterX=-34.2 CenterY=-27.7 CenterZ=0 NormalX=0 NormalY=0 NormalZ=1 AngleXU=0 Radius=1.5 StartAngle=3.14159 EndAngle=6.28319
    g3: ArcOfCircle CenterX=-4 CenterY=-27.7 CenterZ=0 NormalX=0 NormalY=0 NormalZ=1 AngleXU=0 Radius=1.5 StartAngle=3.1416 EndAngle=6.28319
    g4: ArcOfCircle CenterX=-10 CenterY=-4.3 CenterZ=0 NormalX=0 NormalY=0 NormalZ=1 AngleXU=0 Radius=1.5 StartAngle=2e-16 EndAngle=3.14159
    g5: ArcOfCircle CenterX=-16.1 CenterY=-1.8 CenterZ=0 NormalX=0 NormalY=0 NormalZ=1 AngleXU=0 Radius=1.5 StartAngle=5e-16 EndAngle=3.14159
    g6: ArcOfCircle CenterX=-22.1 CenterY=-1.8 CenterZ=0 NormalX=0 NormalY=0 NormalZ=1 AngleXU=0 Radius=1.5 StartAngle=5e-16 EndAngle=3.14159
    g7: ArcOfCircle CenterX=-28.2 CenterY=-4.3 CenterZ=0 NormalX=0 NormalY=0 NormalZ=1 AngleXU=0 Radius=1.5 StartAngle=2e-16 EndAngle=3.14159
    g8: ArcOfCircle CenterX=-10 CenterY=-33.9 CenterZ=0 NormalX=0 NormalY=0 NormalZ=1 AngleXU=0 Radius=1.5 StartAngle=3.14159 EndAngle=6.28319
    g9: ArcOfCircle CenterX=-16.1 CenterY=-36.4 CenterZ=0 NormalX=0 NormalY=0 NormalZ=1 AngleXU=0 Radius=1.5 StartAngle=3.14159 EndAngle=6.28319
    g10: ArcOfCircle CenterX=-22.1 CenterY=-36.4 CenterZ=0 NormalX=0 NormalY=0 NormalZ=1 AngleXU=0 Radius=1.5 StartAngle=3.14159 EndAngle=6.28319
    g11: ArcOfCircle CenterX=-28.2 CenterY=-33.9 CenterZ=0 NormalX=0 NormalY=0 NormalZ=1 AngleXU=0 Radius=1.5 StartAngle=3.14159 EndAngle=6.28319
    g12: LineSegment StartX=-35.7 StartY=-10.5 StartZ=0 EndX=-35.7 EndY=-27.7 EndZ=0
    g13: LineSegment StartX=-32.7 StartY=-10.5 StartZ=0 EndX=-32.7 EndY=-27.7 EndZ=0
    g14: LineSegment StartX=-29.7 StartY=-33.9 StartZ=0 EndX=-29.7 EndY=-4.3 EndZ=0
    g15: LineSegment StartX=-26.7 StartY=-33.9 StartZ=0 EndX=-26.7 EndY=-4.3 EndZ=0
    g16: LineSegment StartX=-2.5 StartY=-10.5 StartZ=0 EndX=-2.5 EndY=-27.7 EndZ=0
    g17: LineSegment StartX=-8.5 StartY=-4.3 StartZ=0 EndX=-8.5 EndY=-33.9 EndZ=0
    g18: LineSegment StartX=-5.5 StartY=-10.5 StartZ=0 EndX=-5.5 EndY=-27.7 EndZ=0
    g19: LineSegment StartX=-11.5 StartY=-4.3 StartZ=0 EndX=-11.5 EndY=-33.9 EndZ=0
    g20: LineSegment StartX=-14.6 StartY=-1.8 StartZ=0 EndX=-14.6 EndY=-36.4 EndZ=0
    g21: LineSegment StartX=-17.6 StartY=-1.8 StartZ=0 EndX=-17.6 EndY=-36.4 EndZ=0
    g22: LineSegment StartX=-20.6 StartY=-36.4 StartZ=0 EndX=-20.6 EndY=-1.8 EndZ=0
    g23: LineSegment StartX=-23.6 StartY=-1.8 StartZ=0 EndX=-23.6 EndY=-36.4 EndZ=0
  constraints (48):
    c: Block(g0)
    c: Block(g1)
    c: Block(g2)
    c: Block(g3)
    c: Block(g4)
    c: Block(g5)
    c: Block(g6)
    c: Block(g7)
    c: Block(g8)
    c: Block(g9)
    c: Block(g10)
    c: Block(g11)
    c: Coincident(g12,g1)
    c: Coincident(g12,g2)
    c: Vertical(g12)
    c: Coincident(g13,g1)
    c: Coincident(g13,g2)
    c: Vertical(g13)
    c: Coincident(g14,g11)
    c: Coincident(g14,g7)
    c: Vertical(g14)
    c: Coincident(g15,g11)
    c: Coincident(g15,g7)
    c: Vertical(g15)
    c: Coincident(g16,g0)
    c: Coincident(g16,g3)
    c: Vertical(g16)
    c: Coincident(g17,g4)
    c: Coincident(g17,g8)
    c: Vertical(g17)
    c: Coincident(g18,g0)
    c: Coincident(g18,g3)
    c: Vertical(g18)
    c: Coincident(g19,g4)
    c: Coincident(g19,g8)
    c: Vertical(g19)
    c: Coincident(g20,g5)
    c: Coincident(g20,g9)
    c: Vertical(g20)
    c: Coincident(g21,g5)
    c: Coincident(g21,g9)
    c: Vertical(g21)
    c: Coincident(g22,g10)
    c: Coincident(g22,g6)
    c: Vertical(g22)
    c: Coincident(g23,g6)
    c: Coincident(g23,g10)
    c: Vertical(g23)
FEATURE [Part::Extrusion] Extrude048  label="removeToCreateFanGrillHoles004"
  Base = -> Sketch057
  Dir = (0,-1,6e-16)
  DirMode = 2
  FaceMakerClass = Part::FaceMakerBullseye
  LengthFwd = 10
  LengthRev = 0
  Placement = pos=(65.4,44,54.82) rot=(0,0,1;0rad)
  Solid = true
  Symmetric = false
FEATURE [Part::Cut] Cut040  label="top021"
  Base = -> Fillet039
  Tool = -> Extrude048
FEATURE [Part::Cylinder] Cylinder041  label="removeToCreteHoleForPlugHousing034"
  Angle = 360
  AttacherType = Attacher::AttachEngine3D
  Height = 20
  Placement = pos=(-2,19,36) rot=(0,1,0;1.5708rad)
  Radius = 14.3
FEATURE [Part::MultiFuse] Fusion089  label="removeToCreteHoleForPlugHousing035"
  Shapes = -> [Box026,Cylinder041]
FEATURE [Part::Cylinder] Cylinder042
  Angle = 360
  AttacherType = Attacher::AttachEngine3D
  Height = 20
  Placement = pos=(0,0,36.15) rot=(0,0,1;0rad)
  Radius = 14.3
FEATURE [Part::Cylinder] Cylinder043
  Angle = 360
  AttacherType = Attacher::AttachEngine3D
  Height = 10
  Placement = pos=(0,0,36.15) rot=(0,0,1;0rad)
  Radius = 4
FEATURE [Part::Box] Box027  label="removeToCreteHoleForPlugHousing036"
  AttacherType = Attacher::AttachEngine3D
  Height = 28.6
  Length = 20
  Placement = pos=(106.15,0,21.7) rot=(0,0,1;0rad)
  Width = 19
FEATURE [Part::Cut] Cut041  label="top022"
  Base = -> Cut040
  Tool = -> Fusion087
FEATURE [Part::Cut] Cut039  label="top020"
  Base = -> Cut041
  Tool = -> Fusion089
FEATURE [Part::MultiFuse] Fusion090  label="removeToCreteHoleForPlugHousing037"
  Placement = pos=(70,19,36) rot=(0,1,0;1.5708rad)
  Shapes = -> [Cylinder042,Cylinder043]
FEATURE [Part::MultiFuse] Fusion088  label="removeToCreteHoleForPlugHousing033"
  Shapes = -> [Box027,Fusion090]
FEATURE [Part::Cut] Cut042  label="removeToCreteHoleForPlugHousing038"
  Base = -> Cut039
  Tool = -> Fusion088
FEATURE [Part::MultiFuse] Fusion091  label="removeFromTop"
  Shapes = -> [Fillet038,Fusion085,Fusion084,Fusion083,Extrude045]
FEATURE [Part::Cut] Cut043  label="REAL TOP ====="
  Base = -> Fillet036
  Tool = -> Fusion091
FEATURE [Part::MultiFuse] Fusion092  label="caseScrewPillarBracket016"
  Shapes = -> [Extrude030,Extrude031,Extrude032,Extrude033,Extrude034,Extrude035,Extrude036,Extrude037,Box013,Box014]
FEATURE [Sketcher::SketchObject] Sketch058  label="topSketch015"
  FullyConstrained = true
  sketch-geometry (20):
    g0: LineSegment StartX=5.21097e-06 StartY=3 StartZ=0 EndX=5.21097e-06 EndY=19 EndZ=0
    g1: ArcOfCircle CenterX=19 CenterY=19 CenterZ=0 NormalX=0 NormalY=0 NormalZ=1 AngleXU=0 Radius=19 StartAngle=1.5708 EndAngle=3.14159
    g2: ArcOfCircle CenterX=19 CenterY=19 CenterZ=0 NormalX=0 NormalY=0 NormalZ=1 AngleXU=0 Radius=16 StartAngle=1.5708 EndAngle=3.14159
    g3: LineSegment StartX=114 StartY=35 StartZ=0 EndX=19 EndY=35 EndZ=0
    g4: LineSegment StartX=5.21097e-06 StartY=3 StartZ=0 EndX=5.21097e-06 EndY=0 EndZ=0
    g5: LineSegment StartX=3 StartY=0 StartZ=0 EndX=5.21097e-06 EndY=0 EndZ=0
    g6: LineSegment StartX=3 StartY=19 StartZ=0 EndX=3 EndY=0 EndZ=0
    g7: LineSegment StartX=19 StartY=38 StartZ=0 EndX=124 EndY=38 EndZ=0
    g8: Circle CenterX=119 CenterY=35 CenterZ=0 NormalX=0 NormalY=0 NormalZ=1 AngleXU=0 Radius=1
    g9: Circle CenterX=121 CenterY=35 CenterZ=0 NormalX=0 NormalY=0 NormalZ=1 AngleXU=0 Radius=1
    g10: Circle CenterX=121 CenterY=33 CenterZ=0 NormalX=0 NormalY=0 NormalZ=1 AngleXU=0 Radius=1
    g11: BSplineCurve PolesCount=3 KnotsCount=2 Degree=2 IsPeriodic=0
    g12: GeomPoint X=119 Y=35 Z=0
    g13: GeomPoint X=121 Y=33 Z=0
    g14: LineSegment StartX=119 StartY=35 StartZ=0 EndX=114 EndY=35 EndZ=0
    g15: ArcOfCircle CenterX=105 CenterY=19 CenterZ=0 NormalX=0 NormalY=0 NormalZ=1 AngleXU=0 Radius=19 StartAngle=5.7297 EndAngle=6.28319
    g16: ArcOfCircle CenterX=105 CenterY=19 CenterZ=0 NormalX=0 NormalY=0 NormalZ=1 AngleXU=0 Radius=16 StartAngle=5.60905 EndAngle=6.28319
    g17: LineSegment StartX=121 StartY=33 StartZ=0 EndX=121 EndY=19 EndZ=0
    g18: LineSegment StartX=124 StartY=38 StartZ=0 EndX=124 EndY=19 EndZ=0
    g19: LineSegment StartX=117.5 StartY=9.01251 StartZ=0 EndX=121.163 EndY=9.0125 EndZ=0
  constraints (46):
    c: Vertical(g0)
    c: Block(g0)
    c: Coincident(g1,g0)
    c: Block(g1)
    c: Coincident(g2,g1)
    c: Block(g2)
    c: Coincident(g3,g2)
    c: Horizontal(g3)
    c: Tangent(g3,g2)
    c: Coincident(g4,g0)
    c: Distance(g4) = 3
    c: Vertical(g4)
    c: Coincident(g5,g4)
    c: Horizontal(g5)
    c: Coincident(g6,g2)
    c: Coincident(g6,g5)
    c: Vertical(g6)
    c: Horizontal(g7)
    c: Distance(g7) = 105
    c: Coincident(g7,g1)
    c: Block(g3)
    c: Weight(g8) = 1
    c: Equal(g8,g9)
    c: Equal(g8,g10)
    c: InternalAlignment(g8,g11)
    c: InternalAlignment(g9,g11)
    c: InternalAlignment(g10,g11)
    c: InternalAlignment(g12,g11)
    c: InternalAlignment(g13,g11)
    c: Block(g11)
    c: Coincident(g14,g11)
    c: Coincident(g14,g3)
    c: Horizontal(g14)
    c: Block(g15)
    c: Coincident(g16,g15)
    c: Block(g16)
    c: Coincident(g17,g11)
    c: Coincident(g17,g16)
    c: Vertical(g17)
    c: Distance(g17) = 14
    c: Coincident(g18,g7)
    c: Coincident(g18,g15)
    c: Vertical(g18)
    c: Distance(g18) = 19
    c: Coincident(g19,g16)
    c: Coincident(g19,g15)
FEATURE [Part::Extrusion] Extrude049  label="top023"
  Base = -> Sketch058
  Dir = (0,0,1)
  DirMode = 2
  FaceMakerClass = Part::FaceMakerBullseye
  LengthFwd = 72
  LengthRev = 0
  Solid = true
  Symmetric = false
FEATURE [Sketcher::SketchObject] Sketch059
  FullyConstrained = true
  MapMode = 3
  Placement = pos=(0,0,0) rot=(1,0,0;1.5708rad)
  Support = -> [Extrude049]
  sketch-geometry (8):
    g0: Circle CenterX=80.351 CenterY=-67.6202 CenterZ=0 NormalX=0 NormalY=0 NormalZ=1 AngleXU=0 Radius=2
    g1: Circle CenterX=80.351 CenterY=-67.6202 CenterZ=0 NormalX=0 NormalY=0 NormalZ=1 AngleXU=0 Radius=3
    g2: Circle CenterX=80.351 CenterY=-4.92017 CenterZ=0 NormalX=0 NormalY=0 NormalZ=1 AngleXU=0 Radius=2
    g3: Circle CenterX=80.351 CenterY=-4.92017 CenterZ=0 NormalX=0 NormalY=0 NormalZ=1 AngleXU=0 Radius=3
    g4: Circle CenterX=23.851 CenterY=-4.92017 CenterZ=0 NormalX=0 NormalY=0 NormalZ=1 AngleXU=0 Radius=2
    g5: Circle CenterX=23.851 CenterY=-4.92017 CenterZ=0 NormalX=0 NormalY=0 NormalZ=1 AngleXU=0 Radius=3
    g6: Circle CenterX=23.851 CenterY=-67.6202 CenterZ=0 NormalX=0 NormalY=0 NormalZ=1 AngleXU=0 Radius=2
    g7: Circle CenterX=23.851 CenterY=-67.6202 CenterZ=0 NormalX=0 NormalY=0 NormalZ=1 AngleXU=0 Radius=3
  constraints (8):
    c: Block(g3)
    c: Block(g2)
    c: Block(g1)
    c: Block(g0)
    c: Block(g6)
    c: Block(g7)
    c: Block(g4)
    c: Block(g5)
FEATURE [Sketcher::SketchObject] Sketch060
  FullyConstrained = true
  MapMode = 3
  Placement = pos=(0,0,0) rot=(1,0,0;1.5708rad)
  Support = -> [Extrude049]
  sketch-geometry (8):
    g0: Circle CenterX=80.351 CenterY=-67.6202 CenterZ=0 NormalX=0 NormalY=0 NormalZ=1 AngleXU=0 Radius=3
    g1: Circle CenterX=80.351 CenterY=-4.92017 CenterZ=0 NormalX=0 NormalY=0 NormalZ=1 AngleXU=0 Radius=3
    g2: Circle CenterX=23.851 CenterY=-4.92017 CenterZ=0 NormalX=0 NormalY=0 NormalZ=1 AngleXU=0 Radius=3
    g3: Circle CenterX=23.851 CenterY=-67.6202 CenterZ=0 NormalX=0 NormalY=0 NormalZ=1 AngleXU=0 Radius=3
    g4: Circle CenterX=23.851 CenterY=-67.6202 CenterZ=0 NormalX=0 NormalY=0 NormalZ=1 AngleXU=0 Radius=5
    g5: Circle CenterX=80.351 CenterY=-67.6202 CenterZ=0 NormalX=0 NormalY=0 NormalZ=1 AngleXU=0 Radius=5
    g6: Circle CenterX=23.851 CenterY=-4.92017 CenterZ=0 NormalX=0 NormalY=0 NormalZ=1 AngleXU=0 Radius=5
    g7: Circle CenterX=80.351 CenterY=-4.92017 CenterZ=0 NormalX=0 NormalY=0 NormalZ=1 AngleXU=0 Radius=5
  constraints (8):
    c: Block(g1)
    c: Block(g0)
    c: Block(g3)
    c: Block(g2)
    c: Block(g5)
    c: Block(g4)
    c: Block(g6)
    c: Block(g7)
FEATURE [Sketcher::SketchObject] Sketch061
  FullyConstrained = true
  MapMode = 3
  Placement = pos=(0,0,0) rot=(1,0,0;1.5708rad)
  sketch-geometry (8):
    g0: Circle CenterX=80.351 CenterY=-67.6202 CenterZ=0 NormalX=0 NormalY=0 NormalZ=1 AngleXU=0 Radius=3
    g1: Circle CenterX=80.351 CenterY=-4.92017 CenterZ=0 NormalX=0 NormalY=0 NormalZ=1 AngleXU=0 Radius=3
    g2: Circle CenterX=23.851 CenterY=-4.92017 CenterZ=0 NormalX=0 NormalY=0 NormalZ=1 AngleXU=0 Radius=3
    g3: Circle CenterX=23.851 CenterY=-67.6202 CenterZ=0 NormalX=0 NormalY=0 NormalZ=1 AngleXU=0 Radius=3
    g4: Circle CenterX=23.851 CenterY=-67.6202 CenterZ=0 NormalX=0 NormalY=0 NormalZ=1 AngleXU=0 Radius=5
    g5: Circle CenterX=80.351 CenterY=-67.6202 CenterZ=0 NormalX=0 NormalY=0 NormalZ=1 AngleXU=0 Radius=5
    g6: Circle CenterX=23.851 CenterY=-4.92017 CenterZ=0 NormalX=0 NormalY=0 NormalZ=1 AngleXU=0 Radius=5
    g7: Circle CenterX=80.351 CenterY=-4.92017 CenterZ=0 NormalX=0 NormalY=0 NormalZ=1 AngleXU=0 Radius=5
  constraints (8):
    c: Block(g1)
    c: Block(g0)
    c: Block(g3)
    c: Block(g2)
    c: Block(g5)
    c: Block(g4)
    c: Block(g6)
    c: Block(g7)
FEATURE [Sketcher::SketchObject] Sketch062  label="topSketch016"
  FullyConstrained = true
  sketch-geometry (20):
    g0: LineSegment StartX=5.21097e-06 StartY=3 StartZ=0 EndX=5.21097e-06 EndY=19 EndZ=0
    g1: ArcOfCircle CenterX=19 CenterY=19 CenterZ=0 NormalX=0 NormalY=0 NormalZ=1 AngleXU=0 Radius=19 StartAngle=1.5708 EndAngle=3.14159
    g2: ArcOfCircle CenterX=19 CenterY=19 CenterZ=0 NormalX=0 NormalY=0 NormalZ=1 AngleXU=0 Radius=16 StartAngle=1.5708 EndAngle=3.14159
    g3: LineSegment StartX=114 StartY=35 StartZ=0 EndX=19 EndY=35 EndZ=0
    g4: LineSegment StartX=5.21097e-06 StartY=3 StartZ=0 EndX=5.21097e-06 EndY=0 EndZ=0
    g5: LineSegment StartX=3 StartY=0 StartZ=0 EndX=5.21097e-06 EndY=0 EndZ=0
    g6: LineSegment StartX=3 StartY=19 StartZ=0 EndX=3 EndY=0 EndZ=0
    g7: LineSegment StartX=19 StartY=38 StartZ=0 EndX=124 EndY=38 EndZ=0
    g8: Circle CenterX=119 CenterY=35 CenterZ=0 NormalX=0 NormalY=0 NormalZ=1 AngleXU=0 Radius=1
    g9: Circle CenterX=121 CenterY=35 CenterZ=0 NormalX=0 NormalY=0 NormalZ=1 AngleXU=0 Radius=1
    g10: Circle CenterX=121 CenterY=33 CenterZ=0 NormalX=0 NormalY=0 NormalZ=1 AngleXU=0 Radius=1
    g11: BSplineCurve PolesCount=3 KnotsCount=2 Degree=2 IsPeriodic=0
    g12: GeomPoint X=119 Y=35 Z=0
    g13: GeomPoint X=121 Y=33 Z=0
    g14: LineSegment StartX=119 StartY=35 StartZ=0 EndX=114 EndY=35 EndZ=0
    g15: ArcOfCircle CenterX=105 CenterY=19 CenterZ=0 NormalX=0 NormalY=0 NormalZ=1 AngleXU=0 Radius=19 StartAngle=5.7297 EndAngle=6.28319
    g16: ArcOfCircle CenterX=105 CenterY=19 CenterZ=0 NormalX=0 NormalY=0 NormalZ=1 AngleXU=0 Radius=16 StartAngle=5.60905 EndAngle=6.28319
    g17: LineSegment StartX=121 StartY=33 StartZ=0 EndX=121 EndY=19 EndZ=0
    g18: LineSegment StartX=124 StartY=38 StartZ=0 EndX=124 EndY=19 EndZ=0
    g19: LineSegment StartX=117.5 StartY=9.01251 StartZ=0 EndX=121.163 EndY=9.0125 EndZ=0
  constraints (46):
    c: Vertical(g0)
    c: Block(g0)
    c: Coincident(g1,g0)
    c: Block(g1)
    c: Coincident(g2,g1)
    c: Block(g2)
    c: Coincident(g3,g2)
    c: Horizontal(g3)
    c: Tangent(g3,g2)
    c: Coincident(g4,g0)
    c: Distance(g4) = 3
    c: Vertical(g4)
    c: Coincident(g5,g4)
    c: Horizontal(g5)
    c: Coincident(g6,g2)
    c: Coincident(g6,g5)
    c: Vertical(g6)
    c: Horizontal(g7)
    c: Distance(g7) = 105
    c: Coincident(g7,g1)
    c: Block(g3)
    c: Weight(g8) = 1
    c: Equal(g8,g9)
    c: Equal(g8,g10)
    c: InternalAlignment(g8,g11)
    c: InternalAlignment(g9,g11)
    c: InternalAlignment(g10,g11)
    c: InternalAlignment(g12,g11)
    c: InternalAlignment(g13,g11)
    c: Block(g11)
    c: Coincident(g14,g11)
    c: Coincident(g14,g3)
    c: Horizontal(g14)
    c: Block(g15)
    c: Coincident(g16,g15)
    c: Block(g16)
    c: Coincident(g17,g11)
    c: Coincident(g17,g16)
    c: Vertical(g17)
    c: Distance(g17) = 14
    c: Coincident(g18,g7)
    c: Coincident(g18,g15)
    c: Vertical(g18)
    c: Distance(g18) = 19
    c: Coincident(g19,g16)
    c: Coincident(g19,g15)
FEATURE [Part::Extrusion] Extrude053  label="top024"
  Base = -> Sketch062
  Dir = (0,0,1)
  DirMode = 2
  FaceMakerClass = Part::FaceMakerBullseye
  LengthFwd = 72
  LengthRev = 0
  Solid = true
  Symmetric = false
FEATURE [Sketcher::SketchObject] Sketch063
  FullyConstrained = true
  MapMode = 3
  Placement = pos=(0,0,0) rot=(1,0,0;1.5708rad)
  Support = -> [Extrude053]
  sketch-geometry (8):
    g0: Circle CenterX=80.351 CenterY=-67.6202 CenterZ=0 NormalX=0 NormalY=0 NormalZ=1 AngleXU=0 Radius=2
    g1: Circle CenterX=80.351 CenterY=-67.6202 CenterZ=0 NormalX=0 NormalY=0 NormalZ=1 AngleXU=0 Radius=3
    g2: Circle CenterX=80.351 CenterY=-4.92017 CenterZ=0 NormalX=0 NormalY=0 NormalZ=1 AngleXU=0 Radius=2
    g3: Circle CenterX=80.351 CenterY=-4.92017 CenterZ=0 NormalX=0 NormalY=0 NormalZ=1 AngleXU=0 Radius=3
    g4: Circle CenterX=23.851 CenterY=-4.92017 CenterZ=0 NormalX=0 NormalY=0 NormalZ=1 AngleXU=0 Radius=2
    g5: Circle CenterX=23.851 CenterY=-4.92017 CenterZ=0 NormalX=0 NormalY=0 NormalZ=1 AngleXU=0 Radius=3
    g6: Circle CenterX=23.851 CenterY=-67.6202 CenterZ=0 NormalX=0 NormalY=0 NormalZ=1 AngleXU=0 Radius=2
    g7: Circle CenterX=23.851 CenterY=-67.6202 CenterZ=0 NormalX=0 NormalY=0 NormalZ=1 AngleXU=0 Radius=3
  constraints (8):
    c: Block(g3)
    c: Block(g2)
    c: Block(g1)
    c: Block(g0)
    c: Block(g6)
    c: Block(g7)
    c: Block(g4)
    c: Block(g5)
FEATURE [Part::Extrusion] Extrude054
  Base = -> Sketch063
  Dir = (0,-1,2e-16)
  DirMode = 2
  FaceMakerClass = Part::FaceMakerBullseye
  LengthFwd = 6
  LengthRev = 0
  Placement = pos=(0,9,0) rot=(0,0,1;0rad)
  Solid = true
  Symmetric = false
FEATURE [Sketcher::SketchObject] Sketch064  label="topSketch017"
  FullyConstrained = true
  sketch-geometry (20):
    g0: LineSegment StartX=5.21097e-06 StartY=3 StartZ=0 EndX=5.21097e-06 EndY=19 EndZ=0
    g1: ArcOfCircle CenterX=19 CenterY=19 CenterZ=0 NormalX=0 NormalY=0 NormalZ=1 AngleXU=0 Radius=19 StartAngle=1.5708 EndAngle=3.14159
    g2: ArcOfCircle CenterX=19 CenterY=19 CenterZ=0 NormalX=0 NormalY=0 NormalZ=1 AngleXU=0 Radius=16 StartAngle=1.5708 EndAngle=3.14159
    g3: LineSegment StartX=114 StartY=35 StartZ=0 EndX=19 EndY=35 EndZ=0
    g4: LineSegment StartX=5.21097e-06 StartY=3 StartZ=0 EndX=5.21097e-06 EndY=0 EndZ=0
    g5: LineSegment StartX=3 StartY=0 StartZ=0 EndX=5.21097e-06 EndY=0 EndZ=0
    g6: LineSegment StartX=3 StartY=19 StartZ=0 EndX=3 EndY=0 EndZ=0
    g7: LineSegment StartX=19 StartY=38 StartZ=0 EndX=124 EndY=38 EndZ=0
    g8: Circle CenterX=119 CenterY=35 CenterZ=0 NormalX=0 NormalY=0 NormalZ=1 AngleXU=0 Radius=1
    g9: Circle CenterX=121 CenterY=35 CenterZ=0 NormalX=0 NormalY=0 NormalZ=1 AngleXU=0 Radius=1
    g10: Circle CenterX=121 CenterY=33 CenterZ=0 NormalX=0 NormalY=0 NormalZ=1 AngleXU=0 Radius=1
    g11: BSplineCurve PolesCount=3 KnotsCount=2 Degree=2 IsPeriodic=0
    g12: GeomPoint X=119 Y=35 Z=0
    g13: GeomPoint X=121 Y=33 Z=0
    g14: LineSegment StartX=119 StartY=35 StartZ=0 EndX=114 EndY=35 EndZ=0
    g15: ArcOfCircle CenterX=105 CenterY=19 CenterZ=0 NormalX=0 NormalY=0 NormalZ=1 AngleXU=0 Radius=19 StartAngle=5.7297 EndAngle=6.28319
    g16: ArcOfCircle CenterX=105 CenterY=19 CenterZ=0 NormalX=0 NormalY=0 NormalZ=1 AngleXU=0 Radius=16 StartAngle=5.60905 EndAngle=6.28319
    g17: LineSegment StartX=121 StartY=33 StartZ=0 EndX=121 EndY=19 EndZ=0
    g18: LineSegment StartX=124 StartY=38 StartZ=0 EndX=124 EndY=19 EndZ=0
    g19: LineSegment StartX=117.5 StartY=9.01251 StartZ=0 EndX=121.163 EndY=9.0125 EndZ=0
  constraints (46):
    c: Vertical(g0)
    c: Block(g0)
    c: Coincident(g1,g0)
    c: Block(g1)
    c: Coincident(g2,g1)
    c: Block(g2)
    c: Coincident(g3,g2)
    c: Horizontal(g3)
    c: Tangent(g3,g2)
    c: Coincident(g4,g0)
    c: Distance(g4) = 3
    c: Vertical(g4)
    c: Coincident(g5,g4)
    c: Horizontal(g5)
    c: Coincident(g6,g2)
    c: Coincident(g6,g5)
    c: Vertical(g6)
    c: Horizontal(g7)
    c: Distance(g7) = 105
    c: Coincident(g7,g1)
    c: Block(g3)
    c: Weight(g8) = 1
    c: Equal(g8,g9)
    c: Equal(g8,g10)
    c: InternalAlignment(g8,g11)
    c: InternalAlignment(g9,g11)
    c: InternalAlignment(g10,g11)
    c: InternalAlignment(g12,g11)
    c: InternalAlignment(g13,g11)
    c: Block(g11)
    c: Coincident(g14,g11)
    c: Coincident(g14,g3)
    c: Horizontal(g14)
    c: Block(g15)
    c: Coincident(g16,g15)
    c: Block(g16)
    c: Coincident(g17,g11)
    c: Coincident(g17,g16)
    c: Vertical(g17)
    c: Distance(g17) = 14
    c: Coincident(g18,g7)
    c: Coincident(g18,g15)
    c: Vertical(g18)
    c: Distance(g18) = 19
    c: Coincident(g19,g16)
    c: Coincident(g19,g15)
FEATURE [Sketcher::SketchObject] Sketch065
  FullyConstrained = true
  MapMode = 3
  Placement = pos=(0,0,0) rot=(1,0,0;1.5708rad)
  sketch-geometry (8):
    g0: Circle CenterX=80.351 CenterY=-67.6202 CenterZ=0 NormalX=0 NormalY=0 NormalZ=1 AngleXU=0 Radius=3
    g1: Circle CenterX=80.351 CenterY=-4.92017 CenterZ=0 NormalX=0 NormalY=0 NormalZ=1 AngleXU=0 Radius=3
    g2: Circle CenterX=23.851 CenterY=-4.92017 CenterZ=0 NormalX=0 NormalY=0 NormalZ=1 AngleXU=0 Radius=3
    g3: Circle CenterX=23.851 CenterY=-67.6202 CenterZ=0 NormalX=0 NormalY=0 NormalZ=1 AngleXU=0 Radius=3
    g4: Circle CenterX=23.851 CenterY=-67.6202 CenterZ=0 NormalX=0 NormalY=0 NormalZ=1 AngleXU=0 Radius=5
    g5: Circle CenterX=80.351 CenterY=-67.6202 CenterZ=0 NormalX=0 NormalY=0 NormalZ=1 AngleXU=0 Radius=5
    g6: Circle CenterX=23.851 CenterY=-4.92017 CenterZ=0 NormalX=0 NormalY=0 NormalZ=1 AngleXU=0 Radius=5
    g7: Circle CenterX=80.351 CenterY=-4.92017 CenterZ=0 NormalX=0 NormalY=0 NormalZ=1 AngleXU=0 Radius=5
  constraints (8):
    c: Block(g1)
    c: Block(g0)
    c: Block(g3)
    c: Block(g2)
    c: Block(g5)
    c: Block(g4)
    c: Block(g6)
    c: Block(g7)
FEATURE [Part::Extrusion] Extrude056
  Base = -> Sketch065
  Dir = (0,-1,2e-16)
  DirMode = 2
  FaceMakerClass = Part::FaceMakerBullseye
  LengthFwd = 2
  LengthRev = 0
  Solid = true
  Symmetric = false
FEATURE [Part::Extrusion] Extrude057  label="top025"
  Base = -> Sketch064
  Dir = (0,0,1)
  DirMode = 2
  FaceMakerClass = Part::FaceMakerBullseye
  LengthFwd = 72
  LengthRev = 0
  Solid = true
  Symmetric = false
FEATURE [Sketcher::SketchObject] Sketch066
  FullyConstrained = true
  MapMode = 3
  Placement = pos=(0,0,0) rot=(1,0,0;1.5708rad)
  Support = -> [Extrude057]
  sketch-geometry (8):
    g0: Circle CenterX=80.351 CenterY=-67.6202 CenterZ=0 NormalX=0 NormalY=0 NormalZ=1 AngleXU=0 Radius=3
    g1: Circle CenterX=80.351 CenterY=-4.92017 CenterZ=0 NormalX=0 NormalY=0 NormalZ=1 AngleXU=0 Radius=3
    g2: Circle CenterX=23.851 CenterY=-4.92017 CenterZ=0 NormalX=0 NormalY=0 NormalZ=1 AngleXU=0 Radius=3
    g3: Circle CenterX=23.851 CenterY=-67.6202 CenterZ=0 NormalX=0 NormalY=0 NormalZ=1 AngleXU=0 Radius=3
    g4: Circle CenterX=23.851 CenterY=-67.6202 CenterZ=0 NormalX=0 NormalY=0 NormalZ=1 AngleXU=0 Radius=5
    g5: Circle CenterX=80.351 CenterY=-67.6202 CenterZ=0 NormalX=0 NormalY=0 NormalZ=1 AngleXU=0 Radius=5
    g6: Circle CenterX=23.851 CenterY=-4.92017 CenterZ=0 NormalX=0 NormalY=0 NormalZ=1 AngleXU=0 Radius=5
    g7: Circle CenterX=80.351 CenterY=-4.92017 CenterZ=0 NormalX=0 NormalY=0 NormalZ=1 AngleXU=0 Radius=5
  constraints (8):
    c: Block(g1)
    c: Block(g0)
    c: Block(g3)
    c: Block(g2)
    c: Block(g5)
    c: Block(g4)
    c: Block(g6)
    c: Block(g7)
FEATURE [Part::Extrusion] Extrude055
  Base = -> Sketch066
  Dir = (0,-1,2e-16)
  DirMode = 2
  FaceMakerClass = Part::FaceMakerBullseye
  LengthFwd = 2
  LengthRev = 0
  Solid = true
  Symmetric = false
FEATURE [Part::Fillet] Fillet041
  Base = -> Extrude056
  Edges = 4 edges r=1.99: [Edge6,Edge12,Edge18,Edge24]
FEATURE [Part::Cut] Cut045
  Base = -> Extrude055
  Placement = pos=(0,6,0) rot=(0,0,1;0rad)
  Tool = -> Fillet041
FEATURE [Part::MultiFuse] Fusion095  label="pcbScrewPillars"
  Placement = pos=(-3.2,-1,72.3) rot=(0,0,1;0rad)
  Shapes = -> [Cut045,Extrude054]
FEATURE [Part::Feature] Face113
  shape: bbox 3.2 x 1.5 x 2e-07 mm, 1 faces, 0 solids (baked)
FEATURE [Part::Revolution] Revolve121  label="backCaseScrewRetainer002"
  Angle = 360
  Axis = (0,1,0)
  Base = (0,0,0)
  FaceMakerClass = Part::FaceMakerBullseye
  Placement = pos=(12.5,3,62) rot=(0,0,1;0rad)
  Solid = false
  Source = -> Face113
  Symmetric = false
FEATURE [Part::Feature] Face114
  shape: bbox 3.2 x 1.5 x 2e-07 mm, 1 faces, 0 solids (baked)
FEATURE [Part::Feature] Face115
  shape: bbox 3.2 x 1.5 x 2e-07 mm, 1 faces, 0 solids (baked)
FEATURE [Part::Feature] Face116
  shape: bbox 3.2 x 1.5 x 2e-07 mm, 1 faces, 0 solids (baked)
FEATURE [Part::Revolution] Revolve122  label="frontCaseScrewRetainer004"
  Angle = 360
  Axis = (0,1,0)
  Base = (0,0,0)
  FaceMakerClass = Part::FaceMakerBullseye
  Placement = pos=(89.5,3,68.5) rot=(0,0,1;0rad)
  Solid = false
  Source = -> Face115
  Symmetric = false
FEATURE [Part::Revolution] Revolve123  label="frontCaseScrewRetainer005"
  Angle = 360
  Axis = (0,1,0)
  Base = (0,0,0)
  FaceMakerClass = Part::FaceMakerBullseye
  Placement = pos=(89.5,3,3.5) rot=(0,0,1;0rad)
  Solid = false
  Source = -> Face116
  Symmetric = false
FEATURE [Part::Revolution] Revolve124  label="backCaseScrewRetainer003"
  Angle = 360
  Axis = (0,1,0)
  Base = (0,0,0)
  FaceMakerClass = Part::FaceMakerBullseye
  Placement = pos=(12.5,3,10) rot=(0,0,1;0rad)
  Solid = false
  Source = -> Face114
  Symmetric = false
FEATURE [Part::Feature] Face117
  shape: bbox 3.6 x 3.2 x 2e-07 mm, 1 faces, 0 solids (baked)
FEATURE [Part::Revolution] Revolve125  label="moreFrontCaseScrewRetainer004"
  Angle = 360
  Axis = (0,1,0)
  Base = (0,0,0)
  FaceMakerClass = Part::FaceMakerBullseye
  Placement = pos=(109.5,4.5,68.5) rot=(0,0,1;0rad)
  Solid = false
  Source = -> Face117
  Symmetric = false
FEATURE [Part::Feature] Face118
  shape: bbox 3.6 x 3.2 x 2e-07 mm, 1 faces, 0 solids (baked)
FEATURE [Part::Revolution] Revolve126  label="moreFrontCaseScrewRetainer005"
  Angle = 360
  Axis = (0,1,0)
  Base = (0,0,0)
  FaceMakerClass = Part::FaceMakerBullseye
  Placement = pos=(109.5,4.5,3.5) rot=(0,0,1;0rad)
  Solid = false
  Source = -> Face118
  Symmetric = false
FEATURE [Part::MultiFuse] Fusion096  label="screwRetainers001"
  Shapes = -> [Revolve126,Revolve125,Revolve124,Revolve123,Revolve122,Revolve121]
FEATURE [Part::Feature] Face119
  shape: bbox 10 x 16.5 x 2e-07 mm, 1 faces, 0 solids (baked)
FEATURE [Part::Revolution] Revolve130  label="plugHousing050"
  Angle = 360
  Axis = (0,1,0)
  Base = (0,0,0)
  FaceMakerClass = Part::FaceMakerBullseye
  Placement = pos=(0,0,36.15) rot=(0,0,1;0rad)
  Solid = false
  Source = -> Face119
  Symmetric = false
FEATURE [Part::Feature] Face120
  shape: bbox 10 x 16.5 x 2e-07 mm, 1 faces, 0 solids (baked)
FEATURE [Part::Feature] Face121
  shape: bbox 10 x 16.5 x 2e-07 mm, 1 faces, 0 solids (baked)
FEATURE [Part::Revolution] Revolve127  label="plugHousing047"
  Angle = 360
  Axis = (0,1,0)
  Base = (0,0,0)
  FaceMakerClass = Part::FaceMakerBullseye
  Placement = pos=(0,0,36.15) rot=(0,0,1;0rad)
  Solid = false
  Source = -> Face121
  Symmetric = false
FEATURE [Part::Feature] Face122
  shape: bbox 10 x 16.5 x 2e-07 mm, 1 faces, 0 solids (baked)
FEATURE [Part::Feature] Face123
  shape: bbox 10 x 16.5 x 2e-07 mm, 1 faces, 0 solids (baked)
FEATURE [Part::Revolution] Revolve128  label="plugHousing048"
  Angle = 360
  Axis = (0,1,0)
  Base = (0,0,0)
  FaceMakerClass = Part::FaceMakerBullseye
  Placement = pos=(0,0,36.15) rot=(0,0,1;0rad)
  Solid = false
  Source = -> Face123
  Symmetric = false
FEATURE [Part::MultiFuse] Fusion100  label="plugHousing054"
  Placement = pos=(0,0,0) rot=(0,0,1;1.5708rad)
  Shapes = -> [Revolve130,Revolve128]
FEATURE [Part::Feature] Face124
  shape: bbox 10 x 16.5 x 2e-07 mm, 1 faces, 0 solids (baked)
FEATURE [Part::Feature] Face125
  shape: bbox 10 x 16.5 x 2e-07 mm, 1 faces, 0 solids (baked)
FEATURE [Part::Revolution] Revolve129  label="plugHousing049"
  Angle = 360
  Axis = (0,1,0)
  Base = (0,0,0)
  FaceMakerClass = Part::FaceMakerBullseye
  Placement = pos=(0,0,36.15) rot=(0,0,1;0rad)
  Solid = false
  Source = -> Face125
  Symmetric = false
FEATURE [Part::Feature] Face126
  shape: bbox 10 x 16.5 x 2e-07 mm, 1 faces, 0 solids (baked)
FEATURE [Part::Revolution] Revolve131  label="plugHousing058"
  Angle = 360
  Axis = (0,1,0)
  Base = (0,0,0)
  FaceMakerClass = Part::FaceMakerBullseye
  Placement = pos=(0,0,36.15) rot=(0,0,1;0rad)
  Solid = false
  Source = -> Face120
  Symmetric = false
FEATURE [Part::MultiFuse] Fusion099  label="plugHousing053"
  Placement = pos=(0,0,0) rot=(0,0,1;1.5708rad)
  Shapes = -> [Revolve127,Revolve131]
FEATURE [Part::MultiFuse] Fusion102  label="plugHousing056"
  Placement = pos=(0,19,0) rot=(0,0,1;3.14159rad)
  Shapes = -> [Fusion100,Fusion099]
FEATURE [Part::Revolution] Revolve132  label="plugHousing059"
  Angle = 360
  Axis = (0,1,0)
  Base = (0,0,0)
  FaceMakerClass = Part::FaceMakerBullseye
  Placement = pos=(0,0,36.15) rot=(0,0,1;0rad)
  Solid = false
  Source = -> Face126
  Symmetric = false
FEATURE [Part::Revolution] Revolve133  label="plugHousing060"
  Angle = 360
  Axis = (0,1,0)
  Base = (0,0,0)
  FaceMakerClass = Part::FaceMakerBullseye
  Placement = pos=(0,0,36.15) rot=(0,0,1;0rad)
  Solid = false
  Source = -> Face122
  Symmetric = false
FEATURE [Part::MultiFuse] Fusion097  label="plugHousing051"
  Placement = pos=(0,0,0) rot=(0,0,1;1.5708rad)
  Shapes = -> [Revolve133,Revolve132]
FEATURE [Part::Revolution] Revolve134  label="plugHousing061"
  Angle = 360
  Axis = (0,1,0)
  Base = (0,0,0)
  FaceMakerClass = Part::FaceMakerBullseye
  Placement = pos=(0,0,36.15) rot=(0,0,1;0rad)
  Solid = false
  Source = -> Face124
  Symmetric = false
FEATURE [Part::MultiFuse] Fusion101  label="plugHousing055"
  Placement = pos=(0,0,0) rot=(0,0,1;1.5708rad)
  Shapes = -> [Revolve129,Revolve134]
FEATURE [Part::MultiFuse] Fusion098  label="plugHousing052"
  Placement = pos=(0,19,0) rot=(0,0,1;3.14159rad)
  Shapes = -> [Fusion097,Fusion101]
FEATURE [Part::MultiFuse] Fusion103  label="plugHousing057"
  Placement = pos=(122.621,0,-0.15) rot=(0,0,1;0rad)
  Shapes = -> [Fusion102,Fusion098]
FEATURE [Part::Box] Box028  label="Cube015"
  AttacherType = Attacher::AttachEngine3D
  Height = 28
  Length = 3
  Placement = pos=(110.7,19,22) rot=(0,0,1;0rad)
  Width = 15.7
FEATURE [Part::Cylinder] Cylinder044
  Angle = 360
  AttacherType = Attacher::AttachEngine3D
  Height = 20
  Placement = pos=(0,0,36.15) rot=(0,0,1;0rad)
  Radius = 10.3
FEATURE [Part::Cylinder] Cylinder045
  Angle = 360
  AttacherType = Attacher::AttachEngine3D
  Height = 10
  Placement = pos=(0,0,36.15) rot=(0,0,1;0rad)
  Radius = 4
FEATURE [Part::MultiFuse] Fusion104  label="removeToCreteHoleForPlugHousing040"
  Placement = pos=(70,19,36) rot=(0,1,0;1.5708rad)
  Shapes = -> [Cylinder044,Cylinder045]
FEATURE [Part::Cut] Cut046  label="plugHousingTab003"
  Base = -> Box028
  Tool = -> Fusion104
FEATURE [Part::MultiFuse] Fusion105  label="plugHousing062"
  Shapes = -> [Fusion103,Cut046]
FEATURE [Part::Fillet] Fillet042
  Base = -> Fusion105
  Edges = 1 edges r=2: [Edge25]
FEATURE [Part::Fillet] Fillet043  label="plugHousing063"
  Base = -> Fillet042
  Edges = 1 edges r=2: [Edge8]
  Placement = pos=(7,0,0) rot=(0,0,1;0rad)
FEATURE [Part::Feature] Face127
  shape: bbox 10 x 16.5 x 2e-07 mm, 1 faces, 0 solids (baked)
FEATURE [Part::Feature] Face128
  shape: bbox 10 x 16.5 x 2e-07 mm, 1 faces, 0 solids (baked)
FEATURE [Part::Revolution] Revolve137  label="plugHousing070"
  Angle = 360
  Axis = (0,1,0)
  Base = (0,0,0)
  FaceMakerClass = Part::FaceMakerBullseye
  Placement = pos=(0,0,36.15) rot=(0,0,1;0rad)
  Solid = false
  Source = -> Face127
  Symmetric = false
FEATURE [Part::Revolution] Revolve140  label="plugHousing073"
  Angle = 360
  Axis = (0,1,0)
  Base = (0,0,0)
  FaceMakerClass = Part::FaceMakerBullseye
  Placement = pos=(0,0,36.15) rot=(0,0,1;0rad)
  Solid = false
  Source = -> Face128
  Symmetric = false
FEATURE [Part::Feature] Face129
  shape: bbox 10 x 16.5 x 2e-07 mm, 1 faces, 0 solids (baked)
FEATURE [Part::Revolution] Revolve138  label="plugHousing071"
  Angle = 360
  Axis = (0,1,0)
  Base = (0,0,0)
  FaceMakerClass = Part::FaceMakerBullseye
  Placement = pos=(0,0,36.15) rot=(0,0,1;0rad)
  Solid = false
  Source = -> Face129
  Symmetric = false
FEATURE [Part::Feature] Face130
  shape: bbox 10 x 16.5 x 2e-07 mm, 1 faces, 0 solids (baked)
FEATURE [Part::Revolution] Revolve139  label="plugHousing072"
  Angle = 360
  Axis = (0,1,0)
  Base = (0,0,0)
  FaceMakerClass = Part::FaceMakerBullseye
  Placement = pos=(0,0,36.15) rot=(0,0,1;0rad)
  Solid = false
  Source = -> Face130
  Symmetric = false
FEATURE [Part::Feature] Face131
  shape: bbox 10 x 16.5 x 2e-07 mm, 1 faces, 0 solids (baked)
FEATURE [Part::Revolution] Revolve135  label="plugHousing068"
  Angle = 360
  Axis = (0,1,0)
  Base = (0,0,0)
  FaceMakerClass = Part::FaceMakerBullseye
  Placement = pos=(0,0,36.15) rot=(0,0,1;0rad)
  Solid = false
  Source = -> Face131
  Symmetric = false
FEATURE [Part::MultiFuse] Fusion112  label="plugHousing078"
  Placement = pos=(0,0,0) rot=(0,0,1;1.5708rad)
  Shapes = -> [Revolve135,Revolve139]
FEATURE [Part::Feature] Face132
  shape: bbox 10 x 16.5 x 2e-07 mm, 1 faces, 0 solids (baked)
FEATURE [Part::Revolution] Revolve141  label="plugHousing074"
  Angle = 360
  Axis = (0,1,0)
  Base = (0,0,0)
  FaceMakerClass = Part::FaceMakerBullseye
  Placement = pos=(0,0,36.15) rot=(0,0,1;0rad)
  Solid = false
  Source = -> Face132
  Symmetric = false
FEATURE [Part::MultiFuse] Fusion110  label="plugHousing076"
  Placement = pos=(0,0,0) rot=(0,0,1;1.5708rad)
  Shapes = -> [Revolve141,Revolve140]
FEATURE [Part::Feature] Face133
  shape: bbox 10 x 16.5 x 2e-07 mm, 1 faces, 0 solids (baked)
FEATURE [Part::Revolution] Revolve136  label="plugHousing069"
  Angle = 360
  Axis = (0,1,0)
  Base = (0,0,0)
  FaceMakerClass = Part::FaceMakerBullseye
  Placement = pos=(0,0,36.15) rot=(0,0,1;0rad)
  Solid = false
  Source = -> Face133
  Symmetric = false
FEATURE [Part::MultiFuse] Fusion106  label="plugHousing064"
  Placement = pos=(0,0,0) rot=(0,0,1;1.5708rad)
  Shapes = -> [Revolve138,Revolve136]
FEATURE [Part::MultiFuse] Fusion108  label="plugHousing066"
  Placement = pos=(0,19,0) rot=(0,0,1;3.14159rad)
  Shapes = -> [Fusion106,Fusion112]
FEATURE [Part::Feature] Face134
  shape: bbox 10 x 16.5 x 2e-07 mm, 1 faces, 0 solids (baked)
FEATURE [Part::Revolution] Revolve142  label="plugHousing075"
  Angle = 360
  Axis = (0,1,0)
  Base = (0,0,0)
  FaceMakerClass = Part::FaceMakerBullseye
  Placement = pos=(0,0,36.15) rot=(0,0,1;0rad)
  Solid = false
  Source = -> Face134
  Symmetric = false
FEATURE [Part::MultiFuse] Fusion107  label="plugHousing065"
  Placement = pos=(0,0,0) rot=(0,0,1;1.5708rad)
  Shapes = -> [Revolve137,Revolve142]
FEATURE [Part::MultiFuse] Fusion111  label="plugHousing077"
  Placement = pos=(0,19,0) rot=(0,0,1;3.14159rad)
  Shapes = -> [Fusion110,Fusion107]
FEATURE [Part::MultiFuse] Fusion109  label="plugHousing067"
  Placement = pos=(131.236,0,-0.15) rot=(0,0,1;0rad)
  Shapes = -> [Fusion108,Fusion111]
FEATURE [Part::MultiFuse] Fusion113  label="plugHousing079"
  Shapes = -> [Fillet043,Fusion109]
FEATURE [Part::Feature] Face135
  shape: bbox 3.5 x 17.8 x 2e-07 mm, 1 faces, 0 solids (baked)
FEATURE [Part::Revolution] Revolve143  label="removeToCreateScrewAndThreadedInsertHole049"
  Angle = 360
  Axis = (0,1,0)
  Base = (0,0,0)
  FaceMakerClass = Part::FaceMakerBullseye
  Placement = pos=(12.5,0,10) rot=(0,0,1;0rad)
  Solid = false
  Source = -> Face135
  Symmetric = false
FEATURE [Part::Feature] Face136
  shape: bbox 3.5 x 17.8 x 2e-07 mm, 1 faces, 0 solids (baked)
FEATURE [Part::Revolution] Revolve144  label="removeToCreateScrewAndThreadedInsertHole050"
  Angle = 360
  Axis = (0,1,0)
  Base = (0,0,0)
  FaceMakerClass = Part::FaceMakerBullseye
  Placement = pos=(12.5,0,62) rot=(0,0,1;0rad)
  Solid = false
  Source = -> Face136
  Symmetric = false
FEATURE [Part::Feature] Face137
  shape: bbox 3.5 x 17.8 x 2e-07 mm, 1 faces, 0 solids (baked)
FEATURE [Part::Revolution] Revolve145  label="removeToCreateScrewAndThreadedInsertHole051"
  Angle = 360
  Axis = (0,1,0)
  Base = (0,0,0)
  FaceMakerClass = Part::FaceMakerBullseye
  Placement = pos=(89.5,0,68.5) rot=(0,0,1;0rad)
  Solid = false
  Source = -> Face137
  Symmetric = false
FEATURE [Part::Feature] Face138
  shape: bbox 3.5 x 17.8 x 2e-07 mm, 1 faces, 0 solids (baked)
FEATURE [Part::Revolution] Revolve146  label="removeToCreateScrewAndThreadedInsertHole052"
  Angle = 360
  Axis = (0,1,0)
  Base = (0,0,0)
  FaceMakerClass = Part::FaceMakerBullseye
  Placement = pos=(89.5,0,3.5) rot=(0,0,1;0rad)
  Solid = false
  Source = -> Face138
  Symmetric = false
FEATURE [Part::Feature] Face139
  shape: bbox 3.5 x 17.8 x 2e-07 mm, 1 faces, 0 solids (baked)
FEATURE [Part::Revolution] Revolve147  label="removeToCreateScrewAndThreadedInsertHole053"
  Angle = 360
  Axis = (0,1,0)
  Base = (0,0,0)
  FaceMakerClass = Part::FaceMakerBullseye
  Placement = pos=(109.5,4.7,3.5) rot=(0,0,1;0rad)
  Solid = false
  Source = -> Face139
  Symmetric = false
FEATURE [Part::Feature] Face140
  shape: bbox 3.5 x 17.8 x 2e-07 mm, 1 faces, 0 solids (baked)
FEATURE [Part::Revolution] Revolve148  label="removeToCreateScrewAndThreadedInsertHole054"
  Angle = 360
  Axis = (0,1,0)
  Base = (0,0,0)
  FaceMakerClass = Part::FaceMakerBullseye
  Placement = pos=(109.5,4.7,68.5) rot=(0,0,1;0rad)
  Solid = false
  Source = -> Face140
  Symmetric = false
FEATURE [Part::MultiFuse] Fusion114  label="removeToCreateScrewAndThreadedInsertHole055"
  Shapes = -> [Revolve148,Revolve147,Revolve146,Revolve145,Revolve144,Revolve143]
FEATURE [Part::Cut] Cut047  label="casePillars004"
  Base = -> Cut037
  Tool = -> Fusion114
FEATURE [Part::Feature] Face141
  shape: bbox 3.5 x 17.8 x 2e-07 mm, 1 faces, 0 solids (baked)
FEATURE [Part::Feature] Face142
  shape: bbox 3.5 x 17.8 x 2e-07 mm, 1 faces, 0 solids (baked)
FEATURE [Part::Feature] Face143
  shape: bbox 3.5 x 17.8 x 2e-07 mm, 1 faces, 0 solids (baked)
FEATURE [Part::Revolution] Revolve149  label="removeToCreateScrewAndThreadedInsertHole057"
  Angle = 360
  Axis = (0,1,0)
  Base = (0,0,0)
  FaceMakerClass = Part::FaceMakerBullseye
  Placement = pos=(12.5,0,10) rot=(0,0,1;0rad)
  Solid = false
  Source = -> Face141
  Symmetric = false
FEATURE [Part::Feature] Face144
  shape: bbox 3.5 x 17.8 x 2e-07 mm, 1 faces, 0 solids (baked)
FEATURE [Part::Feature] Face145
  shape: bbox 3.5 x 17.8 x 2e-07 mm, 1 faces, 0 solids (baked)
FEATURE [Part::Feature] Face146
  shape: bbox 3.5 x 17.8 x 2e-07 mm, 1 faces, 0 solids (baked)
FEATURE [Part::Revolution] Revolve150  label="removeToCreateScrewAndThreadedInsertHole058"
  Angle = 360
  Axis = (0,1,0)
  Base = (0,0,0)
  FaceMakerClass = Part::FaceMakerBullseye
  Placement = pos=(12.5,0,62) rot=(0,0,1;0rad)
  Solid = false
  Source = -> Face146
  Symmetric = false
FEATURE [Part::Revolution] Revolve151  label="removeToCreateScrewAndThreadedInsertHole059"
  Angle = 360
  Axis = (0,1,0)
  Base = (0,0,0)
  FaceMakerClass = Part::FaceMakerBullseye
  Placement = pos=(89.5,0,68.5) rot=(0,0,1;0rad)
  Solid = false
  Source = -> Face143
  Symmetric = false
FEATURE [Part::Revolution] Revolve152  label="removeToCreateScrewAndThreadedInsertHole060"
  Angle = 360
  Axis = (0,1,0)
  Base = (0,0,0)
  FaceMakerClass = Part::FaceMakerBullseye
  Placement = pos=(89.5,0,3.5) rot=(0,0,1;0rad)
  Solid = false
  Source = -> Face142
  Symmetric = false
FEATURE [Part::Revolution] Revolve153  label="removeToCreateScrewAndThreadedInsertHole061"
  Angle = 360
  Axis = (0,1,0)
  Base = (0,0,0)
  FaceMakerClass = Part::FaceMakerBullseye
  Placement = pos=(109.5,4.7,3.5) rot=(0,0,1;0rad)
  Solid = false
  Source = -> Face145
  Symmetric = false
FEATURE [Part::Revolution] Revolve154  label="removeToCreateScrewAndThreadedInsertHole062"
  Angle = 360
  Axis = (0,1,0)
  Base = (0,0,0)
  FaceMakerClass = Part::FaceMakerBullseye
  Placement = pos=(109.5,4.7,68.5) rot=(0,0,1;0rad)
  Solid = false
  Source = -> Face144
  Symmetric = false
FEATURE [Part::MultiFuse] Fusion115  label="removeToCreateScrewAndThreadedInsertHole056"
  Shapes = -> [Revolve154,Revolve153,Revolve152,Revolve151,Revolve150,Revolve149]
FEATURE [Part::Feature] Face147
  shape: bbox 9.8 x 26.5 x 2e-07 mm, 1 faces, 0 solids (baked)
FEATURE [Part::Revolution] Revolve155
  Angle = 360
  Axis = (0,1,0)
  Base = (0,0,0)
  FaceMakerClass = Part::FaceMakerBullseye
  Placement = pos=(0,0,0) rot=(0,0,1;1.5708rad)
  Solid = false
  Source = -> Face147
  Symmetric = false
FEATURE [Part::Feature] Face148
  shape: bbox 9.8 x 26.5 x 2e-07 mm, 1 faces, 0 solids (baked)
FEATURE [Part::Revolution] Revolve156
  Angle = 360
  Axis = (0,1,0)
  Base = (0,0,0)
  FaceMakerClass = Part::FaceMakerBullseye
  Placement = pos=(0,0,0) rot=(0,0,1;1.5708rad)
  Solid = false
  Source = -> Face148
  Symmetric = false
FEATURE [Part::MultiFuse] Fusion116
  Placement = pos=(-18,19,36) rot=(0,0,1;0rad)
  Shapes = -> [Revolve156,Revolve155]
FEATURE [Part::Box] Box029  label="Cube016"
  AttacherType = Attacher::AttachEngine3D
  Height = 28
  Length = 3
  Placement = pos=(110.7,19,22) rot=(0,0,1;0rad)
  Width = 15.7
FEATURE [Part::Cylinder] Cylinder046
  Angle = 360
  AttacherType = Attacher::AttachEngine3D
  Height = 10
  Placement = pos=(0,0,36.15) rot=(0,0,1;0rad)
  Radius = 4
FEATURE [Part::Cylinder] Cylinder047
  Angle = 360
  AttacherType = Attacher::AttachEngine3D
  Height = 20
  Placement = pos=(0,0,36.15) rot=(0,0,1;0rad)
  Radius = 10.3
FEATURE [Part::MultiFuse] Fusion117  label="removeToCreteHoleForPlugHousing041"
  Placement = pos=(70,19,36) rot=(0,1,0;1.5708rad)
  Shapes = -> [Cylinder047,Cylinder046]
FEATURE [Part::Cut] Cut049  label="plugHousingTab004"
  Base = -> Box029
  Placement = pos=(-107.4,-14,0) rot=(0,0,1;0rad)
  Tool = -> Fusion117
FEATURE [Part::Box] Box030  label="Cube017"
  AttacherType = Attacher::AttachEngine3D
  Height = 28
  Length = 3
  Placement = pos=(110.7,19,22) rot=(0,0,1;0rad)
  Width = 15.7
FEATURE [Part::Cylinder] Cylinder048
  Angle = 360
  AttacherType = Attacher::AttachEngine3D
  Height = 10
  Placement = pos=(0,0,36.15) rot=(0,0,1;0rad)
  Radius = 4
FEATURE [Part::Cylinder] Cylinder049
  Angle = 360
  AttacherType = Attacher::AttachEngine3D
  Height = 20
  Placement = pos=(0,0,36.15) rot=(0,0,1;0rad)
  Radius = 10.3
FEATURE [Part::MultiFuse] Fusion118  label="removeToCreteHoleForPlugHousing042"
  Placement = pos=(70,19,36) rot=(0,1,0;1.5708rad)
  Shapes = -> [Cylinder049,Cylinder048]
FEATURE [Part::Cut] Cut050  label="plugHousingTab005"
  Base = -> Box030
  Placement = pos=(-107.4,-14,0) rot=(0,0,1;0rad)
  Tool = -> Fusion118
FEATURE [Part::MultiFuse] Fusion119
  Placement = pos=(9.6,23,0) rot=(0,0,1;3.14159rad)
  Shapes = -> [Cut049,Cut050]
FEATURE [Part::Box] Box031  label="Cube018"
  AttacherType = Attacher::AttachEngine3D
  Height = 10
  Length = 3
  Placement = pos=(3.3,4,12) rot=(0,0,1;0rad)
  Width = 10
FEATURE [Part::Fillet] Fillet044
  Base = -> Box031
  Edges = 1 edges r=2: [Edge11]
FEATURE [Part::Box] Box032  label="Cube019"
  AttacherType = Attacher::AttachEngine3D
  Height = 10
  Length = 3
  Placement = pos=(3.3,4,50) rot=(0,0,1;0rad)
  Width = 10
FEATURE [Part::Fillet] Fillet045
  Base = -> Box032
  Edges = 1 edges r=2: [Edge12]
FEATURE [Part::Box] Box033  label="Cube020"
  AttacherType = Attacher::AttachEngine3D
  Height = 28
  Length = 4
  Placement = pos=(5,0,22) rot=(0,0,1;0rad)
  Width = 10
FEATURE [Part::Fillet] Fillet046
  Base = -> Box033
  Edges = 1 edges r=1: [Edge7]
FEATURE [Part::Fillet] Fillet047
  Base = -> Fillet046
  Edges = 1 edges r=2: [Edge5]
FEATURE [Part::Fillet] Fillet048
  Base = -> Fillet047
  Edges = 1 edges r=2: [Edge2]
FEATURE [Part::Cylinder] Cylinder050
  Angle = 360
  AttacherType = Attacher::AttachEngine3D
  Height = 20
  Placement = pos=(0,0,36.15) rot=(0,0,1;0rad)
  Radius = 8.2
FEATURE [Part::Cylinder] Cylinder051
  Angle = 360
  AttacherType = Attacher::AttachEngine3D
  Height = 10
  Placement = pos=(0,0,36.15) rot=(0,0,1;0rad)
  Radius = 4
FEATURE [Part::MultiFuse] Fusion120  label="removeToCreteHoleForPlugHousing043"
  Placement = pos=(-42,19,36) rot=(0,1,0;1.5708rad)
  Shapes = -> [Cylinder050,Cylinder051]
FEATURE [Sketcher::SketchObject] Sketch067  label="topSketch018"
  FullyConstrained = true
  sketch-geometry (4):
    g0: LineSegment StartX=16.8446 StartY=31.512 StartZ=0 EndX=16.3251 EndY=34.4666 EndZ=0
    g1: ArcOfCircle CenterX=19 CenterY=19.2524 CenterZ=0 NormalX=0 NormalY=0 NormalZ=1 AngleXU=0 Radius=15.4476 StartAngle=1.74483 EndAngle=2.72717
    g2: ArcOfCircle CenterX=19 CenterY=19.2524 CenterZ=0 NormalX=0 NormalY=0 NormalZ=1 AngleXU=0 Radius=12.4476 StartAngle=1.74483 EndAngle=2.73189
    g3: LineSegment StartX=4.86004 StartY=25.4725 StartZ=0 EndX=7.58253 EndY=24.2107 EndZ=0
  constraints (7):
    c: Block(g0)
    c: Coincident(g1,g0)
    c: Coincident(g2,g0)
    c: Coincident(g3,g1)
    c: Coincident(g3,g2)
    c: Block(g1)
    c: Block(g2)
FEATURE [Part::Extrusion] Extrude058
  Base = -> Sketch067
  Dir = (0,0,1)
  DirMode = 2
  FaceMakerClass = Part::FaceMakerBullseye
  LengthFwd = 10
  LengthRev = 0
  Placement = pos=(0,0,31) rot=(0,0,1;0rad)
  Solid = true
  Symmetric = false
FEATURE [Part::Cut] Cut051
  Base = -> Extrude058
  Tool = -> Fusion120
FEATURE [Part::Fillet] Fillet049
  Base = -> Cut051
  Edges = 1 edges r=2: [Edge1]
FEATURE [Part::Fillet] Fillet050
  Base = -> Fillet049
  Edges = 1 edges r=2.5: [Edge1]
FEATURE [Part::Fillet] Fillet051
  Base = -> Fillet050
  Edges = 1 edges r=2.5: [Edge2]
FEATURE [Part::MultiFuse] Fusion121  label="wireHolder003"
  Shapes = -> [Fusion116,Fillet051]
FEATURE [Part::MultiFuse] Fusion122
  Shapes = -> [Fillet045,Fusion121]
FEATURE [Part::MultiFuse] Fusion123  label="wireHolder004"
  Shapes = -> [Fusion122,Fillet048]
FEATURE [Part::MultiFuse] Fusion124  label="wireHolder005"
  Shapes = -> [Fillet044,Fusion119,Fusion123]
FEATURE [Sketcher::SketchObject] Sketch068  label="topSketch019"
  FullyConstrained = true
  sketch-geometry (6):
    g0: LineSegment StartX=19 StartY=38 StartZ=0 EndX=117 EndY=38 EndZ=0
    g1: ArcOfCircle CenterX=19 CenterY=19 CenterZ=0 NormalX=0 NormalY=0 NormalZ=1 AngleXU=0 Radius=19 StartAngle=1.5708 EndAngle=3.14159
    g2: LineSegment StartX=117 StartY=38 StartZ=0 EndX=117 EndY=19 EndZ=0
    g3: LineSegment StartX=98 StartY=1.0161e-12 StartZ=0 EndX=5.22862e-06 EndY=1.0161e-12 EndZ=0
    g4: LineSegment StartX=5.22862e-06 StartY=19 StartZ=0 EndX=5.22862e-06 EndY=1.0161e-12 EndZ=0
    g5: ArcOfCircle CenterX=98 CenterY=19 CenterZ=0 NormalX=0 NormalY=0 NormalZ=1 AngleXU=0 Radius=19 StartAngle=4.71239 EndAngle=6.28319
  constraints (16):
    c: Horizontal(g0)
    c: Distance(g0) = 98
    c: Coincident(g1,g0)
    c: Block(g1)
    c: Coincident(g2,g0)
    c: Vertical(g2)
    c: Distance(g2) = 19
    c: Horizontal(g3)
    c: Coincident(g4,g1)
    c: Vertical(g4)
    c: Coincident(g3,g4)
    c: Block(g3)
    c: Coincident(g5,g2)
    c: Coincident(g5,g3)
    c: Block(g0)
    c: Block(g5)
FEATURE [Part::Extrusion] Extrude059  label="sideA002"
  Base = -> Sketch068
  Dir = (0,0,1)
  DirMode = 2
  FaceMakerClass = Part::FaceMakerBullseye
  LengthFwd = 3
  LengthRev = 0
  Placement = pos=(0,0,-2.7) rot=(0,0,1;0rad)
  Solid = true
  Symmetric = false
FEATURE [Sketcher::SketchObject] Sketch069  label="topSketch020"
  FullyConstrained = true
  sketch-geometry (6):
    g0: LineSegment StartX=19 StartY=38 StartZ=0 EndX=117 EndY=38 EndZ=0
    g1: ArcOfCircle CenterX=19 CenterY=19 CenterZ=0 NormalX=0 NormalY=0 NormalZ=1 AngleXU=0 Radius=19 StartAngle=1.5708 EndAngle=3.14159
    g2: LineSegment StartX=117 StartY=38 StartZ=0 EndX=117 EndY=19 EndZ=0
    g3: LineSegment StartX=98 StartY=1.0161e-12 StartZ=0 EndX=5.22862e-06 EndY=1.0161e-12 EndZ=0
    g4: LineSegment StartX=5.22862e-06 StartY=19 StartZ=0 EndX=5.22862e-06 EndY=1.0161e-12 EndZ=0
    g5: ArcOfCircle CenterX=98 CenterY=19 CenterZ=0 NormalX=0 NormalY=0 NormalZ=1 AngleXU=0 Radius=19 StartAngle=4.71239 EndAngle=6.28319
  constraints (16):
    c: Horizontal(g0)
    c: Distance(g0) = 98
    c: Coincident(g1,g0)
    c: Block(g1)
    c: Coincident(g2,g0)
    c: Vertical(g2)
    c: Distance(g2) = 19
    c: Horizontal(g3)
    c: Coincident(g4,g1)
    c: Vertical(g4)
    c: Coincident(g3,g4)
    c: Block(g3)
    c: Coincident(g5,g2)
    c: Coincident(g5,g3)
    c: Block(g0)
    c: Block(g5)
FEATURE [Part::Extrusion] Extrude060  label="sideB002"
  Base = -> Sketch069
  Dir = (0,0,1)
  DirMode = 2
  FaceMakerClass = Part::FaceMakerBullseye
  LengthFwd = 3
  LengthRev = 0
  Placement = pos=(0,0,71.7) rot=(0,0,1;0rad)
  Solid = true
  Symmetric = false
FEATURE [Part::MultiFuse] Fusion127  label="removeFromBottom001"
  Placement = pos=(2,0,0) rot=(0,0,1;0rad)
  Shapes = -> [Extrude059,Extrude060]
FEATURE [Part::Cylinder] Cylinder052
  Angle = 360
  AttacherType = Attacher::AttachEngine3D
  Height = 20
  Placement = pos=(0,0,36.15) rot=(0,0,1;0rad)
  Radius = 14
FEATURE [Part::Cylinder] Cylinder053
  Angle = 360
  AttacherType = Attacher::AttachEngine3D
  Height = 10
  Placement = pos=(0,0,36.15) rot=(0,0,1;0rad)
  Radius = 4
FEATURE [Part::MultiFuse] Fusion128  label="removeToCreteHoleForPlugHousing044"
  Placement = pos=(70,19,36) rot=(0,1,0;1.5708rad)
  Shapes = -> [Cylinder052,Cylinder053]
FEATURE [Part::Cut] Cut052  label="bottom011"
  Base = -> Extrude043
  Tool = -> Fusion128
FEATURE [Part::Cut] Cut054  label="bottom012"
  Base = -> Cut052
  Tool = -> Fusion115
FEATURE [Sketcher::SketchObject] Sketch070
  FullyConstrained = true
  Placement = pos=(117,19,0) rot=(0.57735,0.57735,0.57735;2.0944rad)
  sketch-geometry (48):
    g0: LineSegment StartX=-49.19 StartY=69.25 StartZ=0 EndX=-49.19 EndY=66.25 EndZ=0
    g1: LineSegment StartX=-49.19 StartY=63.5 StartZ=0 EndX=-49.19 EndY=60.5 EndZ=0
    g2: LineSegment StartX=-49.19 StartY=57.75 StartZ=0 EndX=-49.19 EndY=54.75 EndZ=0
    g3: LineSegment StartX=-49.19 StartY=52 StartZ=0 EndX=-49.19 EndY=49 EndZ=0
    g4: LineSegment StartX=-49.19 StartY=46.25 StartZ=0 EndX=-49.19 EndY=43.25 EndZ=0
    g5: LineSegment StartX=-49.19 StartY=40.5 StartZ=0 EndX=-49.19 EndY=37.5 EndZ=0
    g6: LineSegment StartX=-49.19 StartY=34.5 StartZ=0 EndX=-49.19 EndY=31.5 EndZ=0
    g7: LineSegment StartX=-49.19 StartY=28.75 StartZ=0 EndX=-49.19 EndY=25.75 EndZ=0
    g8: LineSegment StartX=-49.19 StartY=23 StartZ=0 EndX=-49.19 EndY=20 EndZ=0
    g9: LineSegment StartX=-49.19 StartY=17.25 StartZ=0 EndX=-49.19 EndY=14.25 EndZ=0
    g10: LineSegment StartX=-49.19 StartY=11.5 StartZ=0 EndX=-49.19 EndY=8.5 EndZ=0
    g11: LineSegment StartX=-49.19 StartY=5.75 StartZ=0 EndX=-49.19 EndY=2.75 EndZ=0
    g12: ArcOfCircle CenterX=-1.5 CenterY=67.75 CenterZ=0 NormalX=0 NormalY=0 NormalZ=1 AngleXU=0 Radius=1.5 StartAngle=4.71239 EndAngle=7.85398
    g13: ArcOfCircle CenterX=-1.5 CenterY=62 CenterZ=0 NormalX=0 NormalY=0 NormalZ=1 AngleXU=0 Radius=1.5 StartAngle=4.71239 EndAngle=7.85398
    g14: ArcOfCircle CenterX=-1.5 CenterY=56.25 CenterZ=0 NormalX=0 NormalY=0 NormalZ=1 AngleXU=0 Radius=1.5 StartAngle=4.71239 EndAngle=7.85398
    g15: ArcOfCircle CenterX=-11.49 CenterY=50.5 CenterZ=0 NormalX=0 NormalY=0 NormalZ=1 AngleXU=0 Radius=1.5 StartAngle=4.71239 EndAngle=7.85398
    g16: ArcOfCircle CenterX=-16.28 CenterY=44.75 CenterZ=0 NormalX=0 NormalY=0 NormalZ=1 AngleXU=0 Radius=1.5 StartAngle=4.71239 EndAngle=7.85398
    g17: ArcOfCircle CenterX=-18.2337 CenterY=39 CenterZ=0 NormalX=0 NormalY=0 NormalZ=1 AngleXU=0 Radius=1.5 StartAngle=4.71485 EndAngle=7.85398
    g18: ArcOfCircle CenterX=-16.2837 CenterY=27.25 CenterZ=0 NormalX=0 NormalY=0 NormalZ=1 AngleXU=0 Radius=1.5 StartAngle=4.71485 EndAngle=7.85398
    g19: ArcOfCircle CenterX=-18.2337 CenterY=33 CenterZ=0 NormalX=0 NormalY=0 NormalZ=1 AngleXU=0 Radius=1.5 StartAngle=4.71485 EndAngle=7.85398
    g20: ArcOfCircle CenterX=-11.49 CenterY=21.5 CenterZ=0 NormalX=0 NormalY=0 NormalZ=1 AngleXU=0 Radius=1.5 StartAngle=4.71239 EndAngle=7.85398
    g21: ArcOfCircle CenterX=-1.5 CenterY=4.25 CenterZ=0 NormalX=0 NormalY=0 NormalZ=1 AngleXU=0 Radius=1.5 StartAngle=4.71239 EndAngle=7.85398
    g22: ArcOfCircle CenterX=-1.5 CenterY=10 CenterZ=0 NormalX=0 NormalY=0 NormalZ=1 AngleXU=0 Radius=1.5 StartAngle=4.71239 EndAngle=7.85398
    g23: ArcOfCircle CenterX=-1.5 CenterY=15.75 CenterZ=0 NormalX=0 NormalY=0 NormalZ=1 AngleXU=0 Radius=1.5 StartAngle=4.71239 EndAngle=7.85398
    g24: LineSegment StartX=-49.19 StartY=69.25 StartZ=0 EndX=-1.5 EndY=69.25 EndZ=0
    g25: LineSegment StartX=-49.19 StartY=66.25 StartZ=0 EndX=-1.5 EndY=66.25 EndZ=0
    g26: LineSegment StartX=-49.19 StartY=63.5 StartZ=0 EndX=-1.5 EndY=63.5 EndZ=0
    g27: LineSegment StartX=-49.19 StartY=60.5 StartZ=0 EndX=-1.5 EndY=60.5 EndZ=0
    g28: LineSegment StartX=-49.19 StartY=57.75 StartZ=0 EndX=-1.5 EndY=57.75 EndZ=0
    g29: LineSegment StartX=-49.19 StartY=54.75 StartZ=0 EndX=-1.5 EndY=54.75 EndZ=0
    g30: LineSegment StartX=-49.19 StartY=52 StartZ=0 EndX=-11.49 EndY=52 EndZ=0
    g31: LineSegment StartX=-49.19 StartY=49 StartZ=0 EndX=-11.49 EndY=49 EndZ=0
    g32: LineSegment StartX=-49.19 StartY=46.25 StartZ=0 EndX=-16.28 EndY=46.25 EndZ=0
    g33: LineSegment StartX=-49.19 StartY=43.25 StartZ=0 EndX=-16.28 EndY=43.25 EndZ=0
    g34: LineSegment StartX=-49.19 StartY=40.5 StartZ=0 EndX=-18.2337 EndY=40.5 EndZ=0
    g35: LineSegment StartX=-49.19 StartY=37.5 StartZ=0 EndX=-18.23 EndY=37.5 EndZ=0
    g36: LineSegment StartX=-49.19 StartY=34.5 StartZ=0 EndX=-18.2337 EndY=34.5 EndZ=0
    g37: LineSegment StartX=-49.19 StartY=31.5 StartZ=0 EndX=-18.23 EndY=31.5 EndZ=0
    g38: LineSegment StartX=-49.19 StartY=28.75 StartZ=0 EndX=-16.2837 EndY=28.75 EndZ=0
    g39: LineSegment StartX=-49.19 StartY=25.75 StartZ=0 EndX=-16.28 EndY=25.75 EndZ=0
    g40: LineSegment StartX=-49.19 StartY=23 StartZ=0 EndX=-11.49 EndY=23 EndZ=0
    g41: LineSegment StartX=-49.19 StartY=20 StartZ=0 EndX=-11.49 EndY=20 EndZ=0
    g42: LineSegment StartX=-49.19 StartY=17.25 StartZ=0 EndX=-1.5 EndY=17.25 EndZ=0
    g43: LineSegment StartX=-49.19 StartY=14.25 StartZ=0 EndX=-1.5 EndY=14.25 EndZ=0
    g44: LineSegment StartX=-49.19 StartY=11.5 StartZ=0 EndX=-1.5 EndY=11.5 EndZ=0
    g45: LineSegment StartX=-49.19 StartY=8.5 StartZ=0 EndX=-1.5 EndY=8.5 EndZ=0
    g46: LineSegment StartX=-49.19 StartY=5.75 StartZ=0 EndX=-1.5 EndY=5.75 EndZ=0
    g47: LineSegment StartX=-49.19 StartY=2.75 StartZ=0 EndX=-1.5 EndY=2.75 EndZ=0
  constraints (120):
    c: Vertical(g0)
    c: Distance(g0) = 3
    c: Block(g0)
    c: Vertical(g1)
    c: Distance(g1) = 3
    c: Vertical(g2)
    c: Equal(g0,g2) = 3
    c: Block(g2)
    c: Vertical(g3)
    c: Equal(g1,g3) = 3
    c: Vertical(g4)
    c: Equal(g0,g4) = 3
    c: Block(g4)
    c: Vertical(g5)
    c: Equal(g1,g5) = 3
    c: Vertical(g6)
    c: Equal(g0,g6) = 3
    c: Block(g6)
    c: Vertical(g7)
    c: Equal(g1,g7) = 3
    c: Vertical(g8)
    c: Equal(g0,g8) = 3
    c: Block(g8)
    c: Vertical(g9)
    c: Equal(g1,g9) = 3
    c: Vertical(g10)
    c: Equal(g0,g10) = 3
    c: Block(g10)
    c: Vertical(g11)
    c: Equal(g1,g11) = 3
    c: Block(g12)
    c: Block(g13)
    c: Block(g14)
    c: Block(g15)
    c: Block(g16)
    c: Block(g17)
    c: Block(g18)
    c: Block(g19)
    c: Block(g20)
    c: Block(g21)
    c: Block(g22)
    c: Block(g23)
    c: Block(g11)
    c: Block(g9)
    c: Block(g7)
    c: Block(g5)
    c: Block(g3)
    c: Block(g1)
    c: Coincident(g24,g0)
    c: Coincident(g24,g12)
    c: Horizontal(g24)
    c: Coincident(g25,g0)
    c: Coincident(g25,g12)
    c: Horizontal(g25)
    c: Coincident(g26,g1)
    c: Coincident(g26,g13)
    c: Horizontal(g26)
    c: Coincident(g27,g1)
    c: Coincident(g27,g13)
    c: Horizontal(g27)
    c: Coincident(g28,g2)
    c: Coincident(g28,g14)
    c: Horizontal(g28)
    c: Coincident(g29,g2)
    c: Coincident(g29,g14)
    c: Horizontal(g29)
    c: Coincident(g30,g3)
    c: Coincident(g30,g15)
    c: Horizontal(g30)
    c: Coincident(g31,g3)
    c: Coincident(g31,g15)
    c: Horizontal(g31)
    c: Coincident(g32,g4)
    c: Coincident(g32,g16)
    c: Horizontal(g32)
    c: Coincident(g33,g4)
    c: Coincident(g33,g16)
    c: Horizontal(g33)
    c: Coincident(g34,g5)
    c: Coincident(g34,g17)
    c: Horizontal(g34)
    c: Coincident(g35,g5)
    c: Coincident(g35,g17)
    c: Horizontal(g35)
    c: Coincident(g36,g6)
    c: Coincident(g36,g19)
    c: Horizontal(g36)
    c: Coincident(g37,g6)
    c: Coincident(g37,g19)
    c: Horizontal(g37)
    c: Coincident(g38,g7)
    c: Coincident(g38,g18)
    c: Horizontal(g38)
    c: Coincident(g39,g7)
    c: Coincident(g39,g18)
    c: Horizontal(g39)
    c: Coincident(g40,g8)
    c: Coincident(g40,g20)
    c: Horizontal(g40)
    c: Coincident(g41,g8)
    c: Coincident(g41,g20)
    c: Horizontal(g41)
    c: Coincident(g42,g9)
    c: Coincident(g42,g23)
    c: Horizontal(g42)
    c: Coincident(g43,g9)
    c: Coincident(g43,g23)
    c: Horizontal(g43)
    c: Coincident(g44,g10)
    c: Coincident(g44,g22)
    c: Horizontal(g44)
    c: Coincident(g45,g10)
    c: Coincident(g45,g22)
    c: Horizontal(g45)
    c: Coincident(g46,g11)
    c: Coincident(g46,g21)
    c: Horizontal(g46)
    c: Coincident(g47,g11)
    c: Coincident(g47,g21)
    c: Horizontal(g47)
FEATURE [Part::Extrusion] Extrude061
  Base = -> Sketch070
  Dir = (1,0,0)
  DirMode = 2
  FaceMakerClass = Part::FaceMakerBullseye
  LengthFwd = 23
  LengthRev = 0
  Placement = pos=(-19,0,0) rot=(0,0,1;0rad)
  Solid = true
  Symmetric = false
FEATURE [Part::Fillet] Fillet052  label="removeToCreateVentalationHoles002"
  Base = -> Extrude061
  Edges = <same value as first occurrence — deduplicated (x6 in doc)>
  Placement = pos=(7,0.02,0) rot=(0,0,1;0rad)
FEATURE [Part::MultiFuse] Fusion130  label="bottom013"
  Shapes = -> [Cut054,Cut034]
FEATURE [Part::Cut] Cut055
  Base = -> Fusion130
  Tool = -> Fillet052
FEATURE [Part::Cylinder] Cylinder054
  Angle = 360
  AttacherType = Attacher::AttachEngine3D
  Height = 20
  Placement = pos=(0,0,36.15) rot=(0,0,1;0rad)
  Radius = 4
FEATURE [Sketcher::SketchObject] Sketch071  label="bottomSketch002"
  FullyConstrained = true
  sketch-geometry (32):
    g0: LineSegment StartX=3.3 StartY=-6.03275e-07 StartZ=0 EndX=98 EndY=-6.03275e-07 EndZ=0
    g1: ArcOfCircle CenterX=98 CenterY=19 CenterZ=0 NormalX=0 NormalY=0 NormalZ=1 AngleXU=0 Radius=19 StartAngle=4.71239 EndAngle=5.71103
    g2: LineSegment StartX=6.3 StartY=8 StartZ=0 EndX=3.3 EndY=8 EndZ=0
    g3: LineSegment StartX=3.3 StartY=8 StartZ=0 EndX=3.3 EndY=-6.03275e-07 EndZ=0
    g4: ArcOfCircle CenterX=8.3 CenterY=5 CenterZ=0 NormalX=0 NormalY=0 NormalZ=1 AngleXU=0 Radius=2 StartAngle=3.14159 EndAngle=4.71239
    g5: LineSegment StartX=6.3 StartY=8 StartZ=0 EndX=6.3 EndY=5 EndZ=0
    g6: ArcOfCircle CenterX=98 CenterY=19 CenterZ=0 NormalX=0 NormalY=0 NormalZ=1 AngleXU=0 Radius=12.7 StartAngle=4.71239 EndAngle=6.28319
    g7: LineSegment StartX=94.7 StartY=3 StartZ=0 EndX=8.3 EndY=3 EndZ=0
    g8-g12: Circle x5 (B-spline internal-alignment scaffolding for g13; pole/knot coordinates omitted)
    g13: BSplineCurve PolesCount=5 KnotsCount=3 Degree=3 IsPeriodic=0
    g14: GeomPoint X=98 Y=6.3 Z=0
    g15: GeomPoint X=96.3938 Y=4.71946 Z=0
    g16: GeomPoint X=94.7 Y=3 Z=0
    g17-g23: Circle x7 (B-spline internal-alignment scaffolding for g24; pole/knot coordinates omitted)
    g24: BSplineCurve PolesCount=7 KnotsCount=5 Degree=3 IsPeriodic=0
    g25-g29: GeomPoint x5 (B-spline internal-alignment scaffolding for g24; pole/knot coordinates omitted)
    g30: ArcOfCircle CenterX=98 CenterY=19 CenterZ=0 NormalX=0 NormalY=0 NormalZ=1 AngleXU=0 Radius=15.7 StartAngle=5.81226 EndAngle=6.28319
    g31: LineSegment StartX=110.7 StartY=19 StartZ=0 EndX=113.7 EndY=19 EndZ=0
  constraints (41):
    c: Horizontal(g0)
    c: Coincident(g1,g0)
    c: Block(g1)
    c: Horizontal(g2)
    c: Distance(g2) = 3
    c: Coincident(g3,g2)
    c: Vertical(g3)
    c: Coincident(g3,g0)
    c: Block(g4)
    c: Block(g2)
    c: Coincident(g5,g2)
    c: Coincident(g5,g4)
    c: Vertical(g5)
    c: Coincident(g6,g1)
    c: Block(g6)
    c: Coincident(g7,g4)
    c: Horizontal(g7)
    c: Block(g0)
    c: Block(g7)
    c: Block(g3)
    c: Coincident(g13,g6)
    c: Weight(g8) = 1
    c: Equal(g8, g9-g12) x4
    c: Coincident(g13,g7)
    c: InternalAlignment(g8-g12 -> g13) x5
    c: InternalAlignment(g14,g13)
    c: InternalAlignment(g15,g13)
    c: InternalAlignment(g16,g13)
    c: Block(g13)
    c: Weight(g17) = 1
    c: Equal(g17, g18-g23) x6
    c: Coincident(g24,g1)
    c: InternalAlignment(g17-g23 -> g24) x7
    c: InternalAlignment(g25-g29 -> g24) x5
    c: Block(g24)
    c: Coincident(g30,g24)
    c: Coincident(g31,g6)
    c: Coincident(g31,g30)
    c: Horizontal(g31)
    c: Block(g31)
    c: Block(g30)
FEATURE [Part::Extrusion] Extrude062  label="bottom014"
  Base = -> Sketch071
  Dir = (0,0,1)
  DirMode = 2
  FaceMakerClass = Part::FaceMakerBullseye
  LengthFwd = 71.4
  LengthRev = 0
  Placement = pos=(0,0,0.3) rot=(0,0,1;0rad)
  Solid = true
  Symmetric = false
FEATURE [Part::Fillet] Fillet054
  Base = -> Extrude062
  Edges = 1 edges r=2.4: [Edge17]
FEATURE [Part::Fillet] Fillet055  label="bottom015"
  Base = -> Fillet054
  Edges = 1 edges r=2.4: [Edge36]
FEATURE [Part::Cylinder] Cylinder055
  Angle = 360
  AttacherType = Attacher::AttachEngine3D
  Height = 10
  Placement = pos=(0,0,36.15) rot=(0,0,1;0rad)
  Radius = 4
FEATURE [Part::MultiFuse] Fusion131  label="removeToCreateHoleForPlugHousing002"
  Placement = pos=(70,19,36.15) rot=(0,1,0;1.5708rad)
  Shapes = -> [Cylinder054,Cylinder055]
FEATURE [Part::Cut] Cut056  label="Bottom001"
  Base = -> Fillet055
  Placement = pos=(9,0,0) rot=(0,0,1;0rad)
  Tool = -> Fusion131
FEATURE [Part::Cut] Cut057
  Base = -> Cut055
  Tool = -> Cut056
FEATURE [Sketcher::SketchObject] Sketch072  label="topSketch021"
  FullyConstrained = true
  sketch-geometry (4):
    g0: ArcOfCircle CenterX=105 CenterY=19 CenterZ=0 NormalX=0 NormalY=0 NormalZ=1 AngleXU=0 Radius=20.6155 StartAngle=5.54125 EndAngle=6.28319
    g1: ArcOfCircle CenterX=105 CenterY=19 CenterZ=0 NormalX=0 NormalY=0 NormalZ=1 AngleXU=0 Radius=13 StartAngle=5.54125 EndAngle=6.28319
    g2: LineSegment StartX=118 StartY=19 StartZ=0 EndX=125.616 EndY=19 EndZ=0
    g3: LineSegment StartX=114.583 StartY=10.2157 StartZ=0 EndX=120.197 EndY=5.06982 EndZ=0
  constraints (7):
    c: Block(g0)
    c: Block(g1)
    c: Coincident(g2,g1)
    c: Coincident(g2,g0)
    c: Horizontal(g2)
    c: Coincident(g3,g1)
    c: Coincident(g3,g0)
FEATURE [Part::Extrusion] Extrude063  label="bottomPlugHousingBit003"
  Base = -> Sketch072
  Dir = (0,0,1)
  DirMode = 2
  FaceMakerClass = Part::FaceMakerBullseye
  LengthFwd = 72
  LengthRev = 0
  Solid = true
  Symmetric = false
FEATURE [Part::Cylinder] Cylinder056
  Angle = 360
  AttacherType = Attacher::AttachEngine3D
  Height = 20
  Placement = pos=(0,0,36.15) rot=(0,0,1;0rad)
  Radius = 14.3
FEATURE [Part::Cylinder] Cylinder057
  Angle = 360
  AttacherType = Attacher::AttachEngine3D
  Height = 10
  Placement = pos=(0,0,36.15) rot=(0,0,1;0rad)
  Radius = 4
FEATURE [Part::Box] Box034  label="removeToCreteHoleForPlugHousing047"
  AttacherType = Attacher::AttachEngine3D
  Height = 28.6
  Length = 20
  Placement = pos=(106.15,0,21.7) rot=(0,0,1;0rad)
  Width = 19
FEATURE [Part::Cylinder] Cylinder058
  Angle = 360
  AttacherType = Attacher::AttachEngine3D
  Height = 20
  Placement = pos=(0,0,36.15) rot=(0,0,1;0rad)
  Radius = 14.3
FEATURE [Part::Cylinder] Cylinder059
  Angle = 360
  AttacherType = Attacher::AttachEngine3D
  Height = 10
  Placement = pos=(0,0,36.15) rot=(0,0,1;0rad)
  Radius = 4
FEATURE [Part::MultiFuse] Fusion134  label="removeToCreteHoleForPlugHousing046"
  Placement = pos=(70,19,36) rot=(0,1,0;1.5708rad)
  Shapes = -> [Cylinder058,Cylinder059]
FEATURE [Part::Cylinder] Cylinder060
  Angle = 360
  AttacherType = Attacher::AttachEngine3D
  Height = 20
  Placement = pos=(0,0,36.15) rot=(0,0,1;0rad)
  Radius = 14
FEATURE [Part::Cylinder] Cylinder061
  Angle = 360
  AttacherType = Attacher::AttachEngine3D
  Height = 10
  Placement = pos=(0,0,36.15) rot=(0,0,1;0rad)
  Radius = 4
FEATURE [Part::MultiFuse] Fusion135  label="removeToCreteHoleForPlugHousing048"
  Placement = pos=(70,19,36) rot=(0,1,0;1.5708rad)
  Shapes = -> [Cylinder060,Cylinder061]
FEATURE [Part::Box] Box035  label="removeToCreteHoleForPlugHousing049"
  AttacherType = Attacher::AttachEngine3D
  Height = 28.6
  Length = 20
  Placement = pos=(106.15,0,21.7) rot=(0,0,1;0rad)
  Width = 19
FEATURE [Part::MultiFuse] Fusion133  label="removeToCreteHoleForPlugHousing045"
  Placement = pos=(0,0,-28.3) rot=(0,0,1;0rad)
  Shapes = -> [Box035,Fusion134]
FEATURE [Part::MultiFuse] Fusion138  label="removeToCreteHoleForPlugHousing051"
  Placement = pos=(70,19,36) rot=(0,1,0;1.5708rad)
  Shapes = -> [Cylinder056,Cylinder057]
FEATURE [Part::MultiFuse] Fusion137  label="removeToCreteHoleForPlugHousing050"
  Placement = pos=(0,0,28.3) rot=(0,0,1;0rad)
  Shapes = -> [Box034,Fusion138]
FEATURE [Part::MultiFuse] Fusion132  label="removeToCreatePlugHousingBottomBit002"
  Shapes = -> [Fusion133,Fusion137]
FEATURE [Part::MultiFuse] Fusion136  label="removeToCreatePlugHousingBottomBit003"
  Shapes = -> [Fusion135,Fusion132]
FEATURE [Part::Cut] Cut058  label="bottomPlugHousingBit002"
  Base = -> Extrude063
  Placement = pos=(-0.09,0,0) rot=(0,0,1;0rad)
  Tool = -> Fusion136
FEATURE [Sketcher::SketchObject] Sketch073  label="bottomSketch003"
  FullyConstrained = true
  sketch-geometry (45):
    g0: LineSegment StartX=6.29999 StartY=8 StartZ=0 EndX=3.29999 EndY=8 EndZ=0
    g1: LineSegment StartX=3.29999 StartY=8 StartZ=0 EndX=3.29999 EndY=-6.03275e-07 EndZ=0
    g2: ArcOfCircle CenterX=8.29999 CenterY=5 CenterZ=0 NormalX=0 NormalY=0 NormalZ=1 AngleXU=0 Radius=2 StartAngle=3.14159 EndAngle=4.71239
    g3: LineSegment StartX=6.29999 StartY=8 StartZ=0 EndX=6.29999 EndY=5 EndZ=0
    g4: ArcOfCircle CenterX=105 CenterY=19 CenterZ=0 NormalX=0 NormalY=0 NormalZ=1 AngleXU=0 Radius=12.7 StartAngle=4.71239 EndAngle=5.94289
    g5-g11: Circle x7 (B-spline internal-alignment scaffolding for g12; pole/knot coordinates omitted)
    g12: BSplineCurve PolesCount=7 KnotsCount=5 Degree=3 IsPeriodic=0
    g13-g17: GeomPoint x5 (B-spline internal-alignment scaffolding for g12; pole/knot coordinates omitted)
    g18: ArcOfCircle CenterX=105 CenterY=19 CenterZ=0 NormalX=0 NormalY=0 NormalZ=1 AngleXU=0 Radius=15.7 StartAngle=5.81226 EndAngle=6.28319
    g19: BSplineCurve PolesCount=5 KnotsCount=3 Degree=3 IsPeriodic=0
    g20: LineSegment StartX=8.29999 StartY=3 StartZ=0 EndX=101.7 EndY=3 EndZ=0
    g21: LineSegment StartX=3.29999 StartY=-6.03275e-07 StartZ=0 EndX=105 EndY=-6.03275e-07 EndZ=0
    g22: LineSegment StartX=120.974 StartY=8.71251 StartZ=0 EndX=122.332 EndY=7.83778 EndZ=0
    g23: LineSegment StartX=105 StartY=-6.03274e-07 StartZ=0 EndX=113 EndY=-6.03274e-07 EndZ=0
    g24: ArcOfCircle CenterX=105 CenterY=19 CenterZ=0 NormalX=0 NormalY=0 NormalZ=1 AngleXU=0 Radius=20.6155 StartAngle=5.11091 EndAngle=5.71103
    g25: ArcOfCircle CenterX=117.7 CenterY=19 CenterZ=0 NormalX=0 NormalY=0 NormalZ=1 AngleXU=0 Radius=3 StartAngle=1.2e-15 EndAngle=2.10468
    g26: Circle CenterX=116.345 CenterY=16.3232 CenterZ=0 NormalX=0 NormalY=0 NormalZ=1 AngleXU=0 Radius=1
    g27: Circle CenterX=117.24 CenterY=15.7584 CenterZ=0 NormalX=0 NormalY=0 NormalZ=1 AngleXU=0 Radius=1
    g28: Circle CenterX=116.972 CenterY=14.7612 CenterZ=0 NormalX=0 NormalY=0 NormalZ=1 AngleXU=0 Radius=1
    g29: BSplineCurve PolesCount=3 KnotsCount=2 Degree=2 IsPeriodic=0
    g30: GeomPoint X=116.345 Y=16.3232 Z=0
    g31: GeomPoint X=116.972 Y=14.7612 Z=0
    g32: Circle CenterX=115.828 CenterY=17.157 CenterZ=0 NormalX=0 NormalY=0 NormalZ=1 AngleXU=0 Radius=1
    g33: Circle CenterX=115.841 CenterY=16.639 CenterZ=0 NormalX=0 NormalY=0 NormalZ=1 AngleXU=0 Radius=1
    g34: Circle CenterX=116.345 CenterY=16.3232 CenterZ=0 NormalX=0 NormalY=0 NormalZ=1 AngleXU=0 Radius=1
    g35: BSplineCurve PolesCount=3 KnotsCount=2 Degree=2 IsPeriodic=0
    g36: GeomPoint X=115.828 Y=17.157 Z=0
    g37: GeomPoint X=116.345 Y=16.3232 Z=0
    g38: LineSegment StartX=115.828 StartY=17.157 StartZ=0 EndX=115.828 EndY=20.8307 EndZ=0
    g39: Circle CenterX=115.828 CenterY=20.8307 CenterZ=0 NormalX=0 NormalY=0 NormalZ=1 AngleXU=0 Radius=1
    g40: Circle CenterX=115.831 CenterY=21.3396 CenterZ=0 NormalX=0 NormalY=0 NormalZ=1 AngleXU=0 Radius=1
    g41: Circle CenterX=116.173 CenterY=21.5825 CenterZ=0 NormalX=0 NormalY=0 NormalZ=1 AngleXU=0 Radius=1
    g42: BSplineCurve PolesCount=3 KnotsCount=2 Degree=2 IsPeriodic=0
    g43: GeomPoint X=115.828 Y=20.8307 Z=0
    g44: GeomPoint X=116.173 Y=21.5825 Z=0
  constraints (70):
    c: Horizontal(g0)
    c: Distance(g0) = 3
    c: Coincident(g1,g0)
    c: Vertical(g1)
    c: Block(g2)
    c: Block(g0)
    c: Coincident(g3,g0)
    c: Coincident(g3,g2)
    c: Vertical(g3)
    c: Block(g1)
    c: Block(g4)
    c: Coincident(g19,g4)
    c: Block(g19)
    c: Equal(g5, g6-g11) x6
    c: InternalAlignment(g5-g11 -> g12) x7
    c: InternalAlignment(g13-g17 -> g12) x5
    c: Block(g12)
    c: Coincident(g18,g12)
    c: Block(g18)
    c: Coincident(g20,g2)
    c: Coincident(g20,g19)
    c: Horizontal(g20)
    c: Distance(g20) = 93.4
    c: Coincident(g21,g1)
    c: Horizontal(g21)
    c: Distance(g21) = 101.7
    c: Horizontal(g23)
    c: Distance(g23) = 8
    c: Coincident(g24,g23)
    c: Block(g23)
    c: Coincident(g22,g24)
    c: Block(g24)
    c: Block(g22)
    c: Distance(g22) = 1.61553
    c: Coincident(g25,g18)
    c: Block(g25)
    c: Weight(g26) = 1
    c: Equal(g26,g27)
    c: Equal(g26,g28)
    c: Coincident(g29,g4)
    c: InternalAlignment(g26,g29)
    c: InternalAlignment(g27,g29)
    c: InternalAlignment(g28,g29)
    c: InternalAlignment(g30,g29)
    c: InternalAlignment(g31,g29)
    c: Block(g29)
    c: Weight(g32) = 1
    c: Equal(g32,g33)
    c: Equal(g32,g34)
    c: Coincident(g35,g29)
    c: InternalAlignment(g32,g35)
    c: InternalAlignment(g33,g35)
    c: InternalAlignment(g34,g35)
    c: InternalAlignment(g36,g35)
    c: InternalAlignment(g37,g35)
    c: Block(g35)
    c: Coincident(g38,g35)
    c: Vertical(g38)
    c: Block(g38)
    c: Coincident(g42,g38)
    c: Weight(g39) = 1
    c: Equal(g39,g40)
    c: Equal(g39,g41)
    c: Coincident(g42,g25)
    c: InternalAlignment(g39,g42)
    c: InternalAlignment(g40,g42)
    c: InternalAlignment(g41,g42)
    c: InternalAlignment(g43,g42)
    c: InternalAlignment(g44,g42)
    c: Block(g42)
FEATURE [Part::Extrusion] Extrude064  label="bottom016"
  Base = -> Sketch073
  Dir = (0,0,1)
  DirMode = 2
  FaceMakerClass = Part::FaceMakerBullseye
  LengthFwd = 71.4
  LengthRev = 0
  Placement = pos=(0,0,0.3) rot=(0,0,1;0rad)
  Solid = true
  Symmetric = false
FEATURE [Part::Revolution] Revolve157  label="removeToCreateScrewAndThreadedInsertHole063"
  Angle = 360
  Axis = (0,1,0)
  Base = (0,0,0)
  FaceMakerClass = Part::FaceMakerBullseye
  Placement = pos=(12.5,0,10) rot=(0,0,1;0rad)
  Solid = false
  Source = -> Face141
  Symmetric = false
FEATURE [Sketcher::SketchObject] Sketch074
  FullyConstrained = true
  Placement = pos=(117,19,0) rot=(0.57735,0.57735,0.57735;2.0944rad)
  sketch-geometry (48):
    g0: LineSegment StartX=-49.19 StartY=69.25 StartZ=0 EndX=-49.19 EndY=66.25 EndZ=0
    g1: LineSegment StartX=-49.19 StartY=63.5 StartZ=0 EndX=-49.19 EndY=60.5 EndZ=0
    g2: LineSegment StartX=-49.19 StartY=57.75 StartZ=0 EndX=-49.19 EndY=54.75 EndZ=0
    g3: LineSegment StartX=-49.19 StartY=52 StartZ=0 EndX=-49.19 EndY=49 EndZ=0
    g4: LineSegment StartX=-49.19 StartY=46.25 StartZ=0 EndX=-49.19 EndY=43.25 EndZ=0
    g5: LineSegment StartX=-49.19 StartY=40.5 StartZ=0 EndX=-49.19 EndY=37.5 EndZ=0
    g6: LineSegment StartX=-49.19 StartY=34.5 StartZ=0 EndX=-49.19 EndY=31.5 EndZ=0
    g7: LineSegment StartX=-49.19 StartY=28.75 StartZ=0 EndX=-49.19 EndY=25.75 EndZ=0
    g8: LineSegment StartX=-49.19 StartY=23 StartZ=0 EndX=-49.19 EndY=20 EndZ=0
    g9: LineSegment StartX=-49.19 StartY=17.25 StartZ=0 EndX=-49.19 EndY=14.25 EndZ=0
    g10: LineSegment StartX=-49.19 StartY=11.5 StartZ=0 EndX=-49.19 EndY=8.5 EndZ=0
    g11: LineSegment StartX=-49.19 StartY=5.75 StartZ=0 EndX=-49.19 EndY=2.75 EndZ=0
    g12: ArcOfCircle CenterX=-1.5 CenterY=67.75 CenterZ=0 NormalX=0 NormalY=0 NormalZ=1 AngleXU=0 Radius=1.5 StartAngle=4.71239 EndAngle=7.85398
    g13: ArcOfCircle CenterX=-1.5 CenterY=62 CenterZ=0 NormalX=0 NormalY=0 NormalZ=1 AngleXU=0 Radius=1.5 StartAngle=4.71239 EndAngle=7.85398
    g14: ArcOfCircle CenterX=-1.5 CenterY=56.25 CenterZ=0 NormalX=0 NormalY=0 NormalZ=1 AngleXU=0 Radius=1.5 StartAngle=4.71239 EndAngle=7.85398
    g15: ArcOfCircle CenterX=-11.49 CenterY=50.5 CenterZ=0 NormalX=0 NormalY=0 NormalZ=1 AngleXU=0 Radius=1.5 StartAngle=4.71239 EndAngle=7.85398
    g16: ArcOfCircle CenterX=-16.28 CenterY=44.75 CenterZ=0 NormalX=0 NormalY=0 NormalZ=1 AngleXU=0 Radius=1.5 StartAngle=4.71239 EndAngle=7.85398
    g17: ArcOfCircle CenterX=-18.2337 CenterY=39 CenterZ=0 NormalX=0 NormalY=0 NormalZ=1 AngleXU=0 Radius=1.5 StartAngle=4.71485 EndAngle=7.85398
    g18: ArcOfCircle CenterX=-16.2837 CenterY=27.25 CenterZ=0 NormalX=0 NormalY=0 NormalZ=1 AngleXU=0 Radius=1.5 StartAngle=4.71485 EndAngle=7.85398
    g19: ArcOfCircle CenterX=-18.2337 CenterY=33 CenterZ=0 NormalX=0 NormalY=0 NormalZ=1 AngleXU=0 Radius=1.5 StartAngle=4.71485 EndAngle=7.85398
    g20: ArcOfCircle CenterX=-11.49 CenterY=21.5 CenterZ=0 NormalX=0 NormalY=0 NormalZ=1 AngleXU=0 Radius=1.5 StartAngle=4.71239 EndAngle=7.85398
    g21: ArcOfCircle CenterX=-1.5 CenterY=4.25 CenterZ=0 NormalX=0 NormalY=0 NormalZ=1 AngleXU=0 Radius=1.5 StartAngle=4.71239 EndAngle=7.85398
    g22: ArcOfCircle CenterX=-1.5 CenterY=10 CenterZ=0 NormalX=0 NormalY=0 NormalZ=1 AngleXU=0 Radius=1.5 StartAngle=4.71239 EndAngle=7.85398
    g23: ArcOfCircle CenterX=-1.5 CenterY=15.75 CenterZ=0 NormalX=0 NormalY=0 NormalZ=1 AngleXU=0 Radius=1.5 StartAngle=4.71239 EndAngle=7.85398
    g24: LineSegment StartX=-49.19 StartY=69.25 StartZ=0 EndX=-1.5 EndY=69.25 EndZ=0
    g25: LineSegment StartX=-49.19 StartY=66.25 StartZ=0 EndX=-1.5 EndY=66.25 EndZ=0
    g26: LineSegment StartX=-49.19 StartY=63.5 StartZ=0 EndX=-1.5 EndY=63.5 EndZ=0
    g27: LineSegment StartX=-49.19 StartY=60.5 StartZ=0 EndX=-1.5 EndY=60.5 EndZ=0
    g28: LineSegment StartX=-49.19 StartY=57.75 StartZ=0 EndX=-1.5 EndY=57.75 EndZ=0
    g29: LineSegment StartX=-49.19 StartY=54.75 StartZ=0 EndX=-1.5 EndY=54.75 EndZ=0
    g30: LineSegment StartX=-49.19 StartY=52 StartZ=0 EndX=-11.49 EndY=52 EndZ=0
    g31: LineSegment StartX=-49.19 StartY=49 StartZ=0 EndX=-11.49 EndY=49 EndZ=0
    g32: LineSegment StartX=-49.19 StartY=46.25 StartZ=0 EndX=-16.28 EndY=46.25 EndZ=0
    g33: LineSegment StartX=-49.19 StartY=43.25 StartZ=0 EndX=-16.28 EndY=43.25 EndZ=0
    g34: LineSegment StartX=-49.19 StartY=40.5 StartZ=0 EndX=-18.2337 EndY=40.5 EndZ=0
    g35: LineSegment StartX=-49.19 StartY=37.5 StartZ=0 EndX=-18.23 EndY=37.5 EndZ=0
    g36: LineSegment StartX=-49.19 StartY=34.5 StartZ=0 EndX=-18.2337 EndY=34.5 EndZ=0
    g37: LineSegment StartX=-49.19 StartY=31.5 StartZ=0 EndX=-18.23 EndY=31.5 EndZ=0
    g38: LineSegment StartX=-49.19 StartY=28.75 StartZ=0 EndX=-16.2837 EndY=28.75 EndZ=0
    g39: LineSegment StartX=-49.19 StartY=25.75 StartZ=0 EndX=-16.28 EndY=25.75 EndZ=0
    g40: LineSegment StartX=-49.19 StartY=23 StartZ=0 EndX=-11.49 EndY=23 EndZ=0
    g41: LineSegment StartX=-49.19 StartY=20 StartZ=0 EndX=-11.49 EndY=20 EndZ=0
    g42: LineSegment StartX=-49.19 StartY=17.25 StartZ=0 EndX=-1.5 EndY=17.25 EndZ=0
    g43: LineSegment StartX=-49.19 StartY=14.25 StartZ=0 EndX=-1.5 EndY=14.25 EndZ=0
    g44: LineSegment StartX=-49.19 StartY=11.5 StartZ=0 EndX=-1.5 EndY=11.5 EndZ=0
    g45: LineSegment StartX=-49.19 StartY=8.5 StartZ=0 EndX=-1.5 EndY=8.5 EndZ=0
    g46: LineSegment StartX=-49.19 StartY=5.75 StartZ=0 EndX=-1.5 EndY=5.75 EndZ=0
    g47: LineSegment StartX=-49.19 StartY=2.75 StartZ=0 EndX=-1.5 EndY=2.75 EndZ=0
  constraints (120):
    c: Vertical(g0)
    c: Distance(g0) = 3
    c: Block(g0)
    c: Vertical(g1)
    c: Distance(g1) = 3
    c: Vertical(g2)
    c: Equal(g0,g2) = 3
    c: Block(g2)
    c: Vertical(g3)
    c: Equal(g1,g3) = 3
    c: Vertical(g4)
    c: Equal(g0,g4) = 3
    c: Block(g4)
    c: Vertical(g5)
    c: Equal(g1,g5) = 3
    c: Vertical(g6)
    c: Equal(g0,g6) = 3
    c: Block(g6)
    c: Vertical(g7)
    c: Equal(g1,g7) = 3
    c: Vertical(g8)
    c: Equal(g0,g8) = 3
    c: Block(g8)
    c: Vertical(g9)
    c: Equal(g1,g9) = 3
    c: Vertical(g10)
    c: Equal(g0,g10) = 3
    c: Block(g10)
    c: Vertical(g11)
    c: Equal(g1,g11) = 3
    c: Block(g12)
    c: Block(g13)
    c: Block(g14)
    c: Block(g15)
    c: Block(g16)
    c: Block(g17)
    c: Block(g18)
    c: Block(g19)
    c: Block(g20)
    c: Block(g21)
    c: Block(g22)
    c: Block(g23)
    c: Block(g11)
    c: Block(g9)
    c: Block(g7)
    c: Block(g5)
    c: Block(g3)
    c: Block(g1)
    c: Coincident(g24,g0)
    c: Coincident(g24,g12)
    c: Horizontal(g24)
    c: Coincident(g25,g0)
    c: Coincident(g25,g12)
    c: Horizontal(g25)
    c: Coincident(g26,g1)
    c: Coincident(g26,g13)
    c: Horizontal(g26)
    c: Coincident(g27,g1)
    c: Coincident(g27,g13)
    c: Horizontal(g27)
    c: Coincident(g28,g2)
    c: Coincident(g28,g14)
    c: Horizontal(g28)
    c: Coincident(g29,g2)
    c: Coincident(g29,g14)
    c: Horizontal(g29)
    c: Coincident(g30,g3)
    c: Coincident(g30,g15)
    c: Horizontal(g30)
    c: Coincident(g31,g3)
    c: Coincident(g31,g15)
    c: Horizontal(g31)
    c: Coincident(g32,g4)
    c: Coincident(g32,g16)
    c: Horizontal(g32)
    c: Coincident(g33,g4)
    c: Coincident(g33,g16)
    c: Horizontal(g33)
    c: Coincident(g34,g5)
    c: Coincident(g34,g17)
    c: Horizontal(g34)
    c: Coincident(g35,g5)
    c: Coincident(g35,g17)
    c: Horizontal(g35)
    c: Coincident(g36,g6)
    c: Coincident(g36,g19)
    c: Horizontal(g36)
    c: Coincident(g37,g6)
    c: Coincident(g37,g19)
    c: Horizontal(g37)
    c: Coincident(g38,g7)
    c: Coincident(g38,g18)
    c: Horizontal(g38)
    c: Coincident(g39,g7)
    c: Coincident(g39,g18)
    c: Horizontal(g39)
    c: Coincident(g40,g8)
    c: Coincident(g40,g20)
    c: Horizontal(g40)
    c: Coincident(g41,g8)
    c: Coincident(g41,g20)
    c: Horizontal(g41)
    c: Coincident(g42,g9)
    c: Coincident(g42,g23)
    c: Horizontal(g42)
    c: Coincident(g43,g9)
    c: Coincident(g43,g23)
    c: Horizontal(g43)
    c: Coincident(g44,g10)
    c: Coincident(g44,g22)
    c: Horizontal(g44)
    c: Coincident(g45,g10)
    c: Coincident(g45,g22)
    c: Horizontal(g45)
    c: Coincident(g46,g11)
    c: Coincident(g46,g21)
    c: Horizontal(g46)
    c: Coincident(g47,g11)
    c: Coincident(g47,g21)
    c: Horizontal(g47)
FEATURE [Part::Extrusion] Extrude065
  Base = -> Sketch074
  Dir = (1,0,0)
  DirMode = 2
  FaceMakerClass = Part::FaceMakerBullseye
  LengthFwd = 23
  LengthRev = 0
  Placement = pos=(-19,0,0) rot=(0,0,1;0rad)
  Solid = true
  Symmetric = false
FEATURE [Part::Fillet] Fillet056  label="removeToCreateVentalationHoles003"
  Base = -> Extrude065
  Edges = <same value as first occurrence — deduplicated (x6 in doc)>
  Placement = pos=(7,0.02,0) rot=(0,0,1;0rad)
FEATURE [Part::Revolution] Revolve158  label="removeToCreateScrewAndThreadedInsertHole065"
  Angle = 360
  Axis = (0,1,0)
  Base = (0,0,0)
  FaceMakerClass = Part::FaceMakerBullseye
  Placement = pos=(12.5,0,62) rot=(0,0,1;0rad)
  Solid = false
  Source = -> Face146
  Symmetric = false
FEATURE [Part::Revolution] Revolve159  label="removeToCreateScrewAndThreadedInsertHole066"
  Angle = 360
  Axis = (0,1,0)
  Base = (0,0,0)
  FaceMakerClass = Part::FaceMakerBullseye
  Placement = pos=(89.5,0,68.5) rot=(0,0,1;0rad)
  Solid = false
  Source = -> Face143
  Symmetric = false
FEATURE [Part::Revolution] Revolve160  label="removeToCreateScrewAndThreadedInsertHole067"
  Angle = 360
  Axis = (0,1,0)
  Base = (0,0,0)
  FaceMakerClass = Part::FaceMakerBullseye
  Placement = pos=(89.5,0,3.5) rot=(0,0,1;0rad)
  Solid = false
  Source = -> Face142
  Symmetric = false
FEATURE [Part::Revolution] Revolve161  label="removeToCreateScrewAndThreadedInsertHole068"
  Angle = 360
  Axis = (0,1,0)
  Base = (0,0,0)
  FaceMakerClass = Part::FaceMakerBullseye
  Placement = pos=(109.5,4.7,3.5) rot=(0,0,1;0rad)
  Solid = false
  Source = -> Face145
  Symmetric = false
FEATURE [Part::Revolution] Revolve162  label="removeToCreateScrewAndThreadedInsertHole069"
  Angle = 360
  Axis = (0,1,0)
  Base = (0,0,0)
  FaceMakerClass = Part::FaceMakerBullseye
  Placement = pos=(109.5,4.7,68.5) rot=(0,0,1;0rad)
  Solid = false
  Source = -> Face144
  Symmetric = false
FEATURE [Part::MultiFuse] Fusion141  label="removeToCreateScrewAndThreadedInsertHole064"
  Shapes = -> [Revolve162,Revolve161,Revolve160,Revolve159,Revolve158,Revolve157]
FEATURE [Part::Cylinder] Cylinder062
  Angle = 360
  AttacherType = Attacher::AttachEngine3D
  Height = 20
  Placement = pos=(0,0,36.15) rot=(0,0,1;0rad)
  Radius = 14
FEATURE [Part::Cylinder] Cylinder063
  Angle = 360
  AttacherType = Attacher::AttachEngine3D
  Height = 10
  Placement = pos=(0,0,36.15) rot=(0,0,1;0rad)
  Radius = 4
FEATURE [Part::MultiFuse] Fusion139  label="removeToCreteHoleForPlugHousing052"
  Placement = pos=(70,19,36) rot=(0,1,0;1.5708rad)
  Shapes = -> [Cylinder062,Cylinder063]
FEATURE [Part::Cut] Cut060  label="bottom017"
  Base = -> Extrude064
  Tool = -> Fusion139
FEATURE [Part::Cut] Cut061  label="bottom019"
  Base = -> Cut060
  Tool = -> Fusion141
FEATURE [Part::MultiFuse] Fusion140  label="bottom018"
  Shapes = -> [Cut061,Cut058]
FEATURE [Part::Cut] Cut059  label="bottom020"
  Base = -> Fusion140
  Tool = -> Fillet056
FEATURE [Part::Box] Box036  label="Cube021"
  AttacherType = Attacher::AttachEngine3D
  Height = 80
  Length = 26
  Placement = pos=(0,-1,-5) rot=(0,0,1;0rad)
  Width = 11
FEATURE [Part::Cut] Cut062  label="removeFromBottom002"
  Base = -> Cut057
  Tool = -> Box036
FEATURE [Part::Cut] Cut063
  Base = -> Cut059
  Tool = -> Cut062
FEATURE [Part::Cut] Cut064  label="pcbStands"
  Base = -> Fusion095
  Tool = -> Fusion127
FEATURE [Sketcher::SketchObject] Sketch075  label="topSketch022"
  FullyConstrained = true
  sketch-geometry (6):
    g0: LineSegment StartX=19 StartY=38 StartZ=0 EndX=117 EndY=38 EndZ=0
    g1: ArcOfCircle CenterX=19 CenterY=19 CenterZ=0 NormalX=0 NormalY=0 NormalZ=1 AngleXU=0 Radius=19 StartAngle=1.5708 EndAngle=3.14159
    g2: LineSegment StartX=117 StartY=38 StartZ=0 EndX=117 EndY=19 EndZ=0
    g3: LineSegment StartX=98 StartY=1.0161e-12 StartZ=0 EndX=5.22862e-06 EndY=1.0161e-12 EndZ=0
    g4: LineSegment StartX=5.22862e-06 StartY=19 StartZ=0 EndX=5.22862e-06 EndY=1.0161e-12 EndZ=0
    g5: ArcOfCircle CenterX=98 CenterY=19 CenterZ=0 NormalX=0 NormalY=0 NormalZ=1 AngleXU=0 Radius=19 StartAngle=4.71239 EndAngle=6.28319
  constraints (16):
    c: Horizontal(g0)
    c: Distance(g0) = 98
    c: Coincident(g1,g0)
    c: Block(g1)
    c: Coincident(g2,g0)
    c: Vertical(g2)
    c: Distance(g2) = 19
    c: Horizontal(g3)
    c: Coincident(g4,g1)
    c: Vertical(g4)
    c: Coincident(g3,g4)
    c: Block(g3)
    c: Coincident(g5,g2)
    c: Coincident(g5,g3)
    c: Block(g0)
    c: Block(g5)
FEATURE [Part::Extrusion] Extrude067  label="sideB003"
  Base = -> Sketch075
  Dir = (0,0,1)
  DirMode = 2
  FaceMakerClass = Part::FaceMakerBullseye
  LengthFwd = 3
  LengthRev = 0
  Placement = pos=(0,0,71.7) rot=(0,0,1;0rad)
  Solid = true
  Symmetric = false
FEATURE [Sketcher::SketchObject] Sketch076  label="topSketch023"
  FullyConstrained = true
  sketch-geometry (6):
    g0: LineSegment StartX=19 StartY=38 StartZ=0 EndX=117 EndY=38 EndZ=0
    g1: ArcOfCircle CenterX=19 CenterY=19 CenterZ=0 NormalX=0 NormalY=0 NormalZ=1 AngleXU=0 Radius=19 StartAngle=1.5708 EndAngle=3.14159
    g2: LineSegment StartX=117 StartY=38 StartZ=0 EndX=117 EndY=19 EndZ=0
    g3: LineSegment StartX=98 StartY=1.0161e-12 StartZ=0 EndX=5.22862e-06 EndY=1.0161e-12 EndZ=0
    g4: LineSegment StartX=5.22862e-06 StartY=19 StartZ=0 EndX=5.22862e-06 EndY=1.0161e-12 EndZ=0
    g5: ArcOfCircle CenterX=98 CenterY=19 CenterZ=0 NormalX=0 NormalY=0 NormalZ=1 AngleXU=0 Radius=19 StartAngle=4.71239 EndAngle=6.28319
  constraints (16):
    c: Horizontal(g0)
    c: Distance(g0) = 98
    c: Coincident(g1,g0)
    c: Block(g1)
    c: Coincident(g2,g0)
    c: Vertical(g2)
    c: Distance(g2) = 19
    c: Horizontal(g3)
    c: Coincident(g4,g1)
    c: Vertical(g4)
    c: Coincident(g3,g4)
    c: Block(g3)
    c: Coincident(g5,g2)
    c: Coincident(g5,g3)
    c: Block(g0)
    c: Block(g5)
FEATURE [Part::Extrusion] Extrude066  label="sideA003"
  Base = -> Sketch076
  Dir = (0,0,1)
  DirMode = 2
  FaceMakerClass = Part::FaceMakerBullseye
  LengthFwd = 3
  LengthRev = 0
  Placement = pos=(0,0,-2.7) rot=(0,0,1;0rad)
  Solid = true
  Symmetric = false
FEATURE [Part::MultiFuse] Fusion142  label="removeFromBottom003"
  Placement = pos=(2,0,0) rot=(0,0,1;0rad)
  Shapes = -> [Extrude066,Extrude067]
FEATURE [Part::Cut] Cut065  label="screwRetainers002"
  Base = -> Fusion096
  Tool = -> Fusion142
FEATURE [Sketcher::SketchObject] Sketch077
  FullyConstrained = true
  Placement = pos=(117,19,0) rot=(0.57735,0.57735,0.57735;2.0944rad)
  sketch-geometry (8):
    g0: LineSegment StartX=-49.19 StartY=63.5 StartZ=0 EndX=-49.19 EndY=60.5 EndZ=0
    g1: LineSegment StartX=-49.19 StartY=11.5 StartZ=0 EndX=-49.19 EndY=8.5 EndZ=0
    g2: ArcOfCircle CenterX=-1.5 CenterY=62 CenterZ=0 NormalX=0 NormalY=0 NormalZ=1 AngleXU=0 Radius=1.5 StartAngle=4.71239 EndAngle=7.85398
    g3: ArcOfCircle CenterX=-1.5 CenterY=10 CenterZ=0 NormalX=0 NormalY=0 NormalZ=1 AngleXU=0 Radius=1.5 StartAngle=4.71239 EndAngle=7.85398
    g4: LineSegment StartX=-49.19 StartY=63.5 StartZ=0 EndX=-1.5 EndY=63.5 EndZ=0
    g5: LineSegment StartX=-49.19 StartY=60.5 StartZ=0 EndX=-1.5 EndY=60.5 EndZ=0
    g6: LineSegment StartX=-49.19 StartY=11.5 StartZ=0 EndX=-1.5 EndY=11.5 EndZ=0
    g7: LineSegment StartX=-49.19 StartY=8.5 StartZ=0 EndX=-1.5 EndY=8.5 EndZ=0
  constraints (19):
    c: Vertical(g0)
    c: Distance(g0) = 3
    c: Vertical(g1)
    c: Block(g1)
    c: Block(g2)
    c: Block(g3)
    c: Block(g0)
    c: Coincident(g4,g0)
    c: Coincident(g4,g2)
    c: Horizontal(g4)
    c: Coincident(g5,g0)
    c: Coincident(g5,g2)
    c: Horizontal(g5)
    c: Coincident(g6,g1)
    c: Coincident(g6,g3)
    c: Horizontal(g6)
    c: Coincident(g7,g1)
    c: Coincident(g7,g3)
    c: Horizontal(g7)
FEATURE [Part::Extrusion] Extrude068
  Base = -> Sketch077
  Dir = (1,0,0)
  DirMode = 2
  FaceMakerClass = Part::FaceMakerBullseye
  LengthFwd = 10
  LengthRev = 0
  Solid = true
  Symmetric = false
FEATURE [Part::Fillet] Fillet057  label="removeFromtMoreFrontCaseScrewRetainers002"
  Base = -> Extrude068
  Edges = 4 edges r=1.49: [Edge6,Edge11,Edge18,Edge23]
  Placement = pos=(-12,0,0) rot=(0,0,1;0rad)
FEATURE [Sketcher::SketchObject] Sketch078
  FullyConstrained = true
  Placement = pos=(117,19,0) rot=(0.57735,0.57735,0.57735;2.0944rad)
  sketch-geometry (8):
    g0: LineSegment StartX=-49.19 StartY=69.25 StartZ=0 EndX=-49.19 EndY=66.25 EndZ=0
    g1: LineSegment StartX=-49.19 StartY=5.75 StartZ=0 EndX=-49.19 EndY=2.75 EndZ=0
    g2: ArcOfCircle CenterX=-1.5 CenterY=67.75 CenterZ=0 NormalX=0 NormalY=0 NormalZ=1 AngleXU=0 Radius=1.5 StartAngle=4.71239 EndAngle=7.85398
    g3: ArcOfCircle CenterX=-1.5 CenterY=4.25 CenterZ=0 NormalX=0 NormalY=0 NormalZ=1 AngleXU=0 Radius=1.5 StartAngle=4.71239 EndAngle=7.85398
    g4: LineSegment StartX=-49.19 StartY=69.25 StartZ=0 EndX=-1.5 EndY=69.25 EndZ=0
    g5: LineSegment StartX=-49.19 StartY=66.25 StartZ=0 EndX=-1.5 EndY=66.25 EndZ=0
    g6: LineSegment StartX=-49.19 StartY=5.75 StartZ=0 EndX=-1.5 EndY=5.75 EndZ=0
    g7: LineSegment StartX=-49.19 StartY=2.75 StartZ=0 EndX=-1.5 EndY=2.75 EndZ=0
  constraints (19):
    c: Vertical(g0)
    c: Distance(g0) = 3
    c: Block(g0)
    c: Vertical(g1)
    c: Block(g2)
    c: Block(g3)
    c: Block(g1)
    c: Coincident(g4,g0)
    c: Coincident(g4,g2)
    c: Horizontal(g4)
    c: Coincident(g5,g0)
    c: Coincident(g5,g2)
    c: Horizontal(g5)
    c: Coincident(g6,g1)
    c: Coincident(g6,g3)
    c: Horizontal(g6)
    c: Coincident(g7,g1)
    c: Coincident(g7,g3)
    c: Horizontal(g7)
FEATURE [Part::Extrusion] Extrude069
  Base = -> Sketch078
  Dir = (1,0,0)
  DirMode = 2
  FaceMakerClass = Part::FaceMakerBullseye
  LengthFwd = 10
  LengthRev = 0
  Solid = true
  Symmetric = false
FEATURE [Part::Fillet] Fillet058  label="removeFromtMoreFrontCaseScrewRetainers003"
  Base = -> Extrude069
  Edges = 4 edges r=1.49: [Edge6,Edge11,Edge18,Edge23]
  Placement = pos=(-4,0,0) rot=(0,0,1;0rad)
FEATURE [Part::Cut] Cut066
  Base = -> Cut065
  Tool = -> Fillet058
FEATURE [Part::Cut] Cut067  label="screwPillars"
  Base = -> Cut066
  Tool = -> Fillet057
FEATURE [Part::MultiFuse] Fusion143  label="bottom021"
  Shapes = -> [Cut031,Cut063]
FEATURE [Part::Cylinder] Cylinder
  Angle = 360
  AttacherType = Attacher::AttachEngine3D
  Height = 10
  Placement = pos=(20.65,12,4.68) rot=(1,0,0;1.5708rad)
  Radius = 2
FEATURE [Part::Cylinder] Cylinder064
  Angle = 360
  AttacherType = Attacher::AttachEngine3D
  Height = 10
  Placement = pos=(20.65,12,67.38) rot=(1,0,0;1.5708rad)
  Radius = 2
FEATURE [Part::Cylinder] Cylinder065
  Angle = 360
  AttacherType = Attacher::AttachEngine3D
  Height = 10
  Placement = pos=(77.15,12,67.38) rot=(1,0,0;1.5708rad)
  Radius = 2
FEATURE [Part::Cylinder] Cylinder066
  Angle = 360
  AttacherType = Attacher::AttachEngine3D
  Height = 10
  Placement = pos=(77.15,12,4.68) rot=(1,0,0;1.5708rad)
  Radius = 2
FEATURE [Part::MultiFuse] Fusion144  label="removeFromThreadedInsertHousing"
  Shapes = -> [Cylinder065,Cylinder064,Cylinder,Cylinder066]
FEATURE [Part::Cut] Cut068  label="pcbStands001"
  Base = -> Cut064
  Tool = -> Fusion144
FEATURE [Part::MultiFuse] Fusion145
  Shapes = -> [Cut068,Fusion143]
FEATURE [Part::MultiFuse] Fusion146
  Shapes = -> [Fusion145]
FEATURE [Part::MultiFuse] Fusion147  label="bottom022"
  Shapes = -> [Cut067,Fusion146]
FEATURE [Part::MultiFuse] Fusion148  label="casePillars005"
  Shapes = -> [Cut047,Fusion092]
FEATURE [Part::MultiFuse] Fusion149  label="bottom023"
  Shapes = -> [Fusion124,Fusion113,Fusion147]
FEATURE [Part::MultiFuse] Fusion150  label="topBits"
  Shapes = -> [Cut025,Fusion148,Cut030,Fillet034]
FEATURE [Part::Feature] Face149 .. Face152  x4 (patterned run collapsed; names and placements below)
  shape: bbox 3.2 x 1.5 x 2e-07 mm, 1 faces, 0 solids (baked)
FEATURE [Part::Feature] Face153
  shape: bbox 3.6 x 3.2 x 2e-07 mm, 1 faces, 0 solids (baked)
FEATURE [Part::Feature] Face154
  shape: bbox 3.6 x 3.2 x 2e-07 mm, 1 faces, 0 solids (baked)
FEATURE [Sketcher::SketchObject] Sketch079  label="topSketch024"
  FullyConstrained = true
  sketch-geometry (6):
    g0: LineSegment StartX=19 StartY=38 StartZ=0 EndX=117 EndY=38 EndZ=0
    g1: ArcOfCircle CenterX=19 CenterY=19 CenterZ=0 NormalX=0 NormalY=0 NormalZ=1 AngleXU=0 Radius=19 StartAngle=1.5708 EndAngle=3.14159
    g2: LineSegment StartX=117 StartY=38 StartZ=0 EndX=117 EndY=19 EndZ=0
    g3: LineSegment StartX=98 StartY=1.0161e-12 StartZ=0 EndX=5.22862e-06 EndY=1.0161e-12 EndZ=0
    g4: LineSegment StartX=5.22862e-06 StartY=19 StartZ=0 EndX=5.22862e-06 EndY=1.0161e-12 EndZ=0
    g5: ArcOfCircle CenterX=98 CenterY=19 CenterZ=0 NormalX=0 NormalY=0 NormalZ=1 AngleXU=0 Radius=19 StartAngle=4.71239 EndAngle=6.28319
  constraints (16):
    c: Horizontal(g0)
    c: Distance(g0) = 98
    c: Coincident(g1,g0)
    c: Block(g1)
    c: Coincident(g2,g0)
    c: Vertical(g2)
    c: Distance(g2) = 19
    c: Horizontal(g3)
    c: Coincident(g4,g1)
    c: Vertical(g4)
    c: Coincident(g3,g4)
    c: Block(g3)
    c: Coincident(g5,g2)
    c: Coincident(g5,g3)
    c: Block(g0)
    c: Block(g5)
FEATURE [Sketcher::SketchObject] Sketch080  label="topSketch025"
  FullyConstrained = true
  sketch-geometry (6):
    g0: LineSegment StartX=19 StartY=38 StartZ=0 EndX=117 EndY=38 EndZ=0
    g1: ArcOfCircle CenterX=19 CenterY=19 CenterZ=0 NormalX=0 NormalY=0 NormalZ=1 AngleXU=0 Radius=19 StartAngle=1.5708 EndAngle=3.14159
    g2: LineSegment StartX=117 StartY=38 StartZ=0 EndX=117 EndY=19 EndZ=0
    g3: LineSegment StartX=98 StartY=1.0161e-12 StartZ=0 EndX=5.22862e-06 EndY=1.0161e-12 EndZ=0
    g4: LineSegment StartX=5.22862e-06 StartY=19 StartZ=0 EndX=5.22862e-06 EndY=1.0161e-12 EndZ=0
    g5: ArcOfCircle CenterX=98 CenterY=19 CenterZ=0 NormalX=0 NormalY=0 NormalZ=1 AngleXU=0 Radius=19 StartAngle=4.71239 EndAngle=6.28319
  constraints (16):
    c: Horizontal(g0)
    c: Distance(g0) = 98
    c: Coincident(g1,g0)
    c: Block(g1)
    c: Coincident(g2,g0)
    c: Vertical(g2)
    c: Distance(g2) = 19
    c: Horizontal(g3)
    c: Coincident(g4,g1)
    c: Vertical(g4)
    c: Coincident(g3,g4)
    c: Block(g3)
    c: Coincident(g5,g2)
    c: Coincident(g5,g3)
    c: Block(g0)
    c: Block(g5)
FEATURE [Part::Extrusion] Extrude070  label="sideA004"
  Base = -> Sketch080
  Dir = (0,0,1)
  DirMode = 2
  FaceMakerClass = Part::FaceMakerBullseye
  LengthFwd = 3
  LengthRev = 0
  Placement = pos=(0,0,-2.7) rot=(0,0,1;0rad)
  Solid = true
  Symmetric = false
FEATURE [Sketcher::SketchObject] Sketch081
  FullyConstrained = true
  Placement = pos=(117,19,0) rot=(0.57735,0.57735,0.57735;2.0944rad)
  sketch-geometry (8):
    g0: LineSegment StartX=-49.19 StartY=63.5 StartZ=0 EndX=-49.19 EndY=60.5 EndZ=0
    g1: LineSegment StartX=-49.19 StartY=11.5 StartZ=0 EndX=-49.19 EndY=8.5 EndZ=0
    g2: ArcOfCircle CenterX=-1.5 CenterY=62 CenterZ=0 NormalX=0 NormalY=0 NormalZ=1 AngleXU=0 Radius=1.5 StartAngle=4.71239 EndAngle=7.85398
    g3: ArcOfCircle CenterX=-1.5 CenterY=10 CenterZ=0 NormalX=0 NormalY=0 NormalZ=1 AngleXU=0 Radius=1.5 StartAngle=4.71239 EndAngle=7.85398
    g4: LineSegment StartX=-49.19 StartY=63.5 StartZ=0 EndX=-1.5 EndY=63.5 EndZ=0
    g5: LineSegment StartX=-49.19 StartY=60.5 StartZ=0 EndX=-1.5 EndY=60.5 EndZ=0
    g6: LineSegment StartX=-49.19 StartY=11.5 StartZ=0 EndX=-1.5 EndY=11.5 EndZ=0
    g7: LineSegment StartX=-49.19 StartY=8.5 StartZ=0 EndX=-1.5 EndY=8.5 EndZ=0
  constraints (19):
    c: Vertical(g0)
    c: Distance(g0) = 3
    c: Vertical(g1)
    c: Block(g1)
    c: Block(g2)
    c: Block(g3)
    c: Block(g0)
    c: Coincident(g4,g0)
    c: Coincident(g4,g2)
    c: Horizontal(g4)
    c: Coincident(g5,g0)
    c: Coincident(g5,g2)
    c: Horizontal(g5)
    c: Coincident(g6,g1)
    c: Coincident(g6,g3)
    c: Horizontal(g6)
    c: Coincident(g7,g1)
    c: Coincident(g7,g3)
    c: Horizontal(g7)
FEATURE [Part::Extrusion] Extrude071  label="sideB004"
  Base = -> Sketch079
  Dir = (0,0,1)
  DirMode = 2
  FaceMakerClass = Part::FaceMakerBullseye
  LengthFwd = 3
  LengthRev = 0
  Placement = pos=(0,0,71.7) rot=(0,0,1;0rad)
  Solid = true
  Symmetric = false
FEATURE [Part::MultiFuse] Fusion152  label="removeFromBottom004"
  Placement = pos=(2,0,0) rot=(0,0,1;0rad)
  Shapes = -> [Extrude070,Extrude071]
FEATURE [Part::Extrusion] Extrude072
  Base = -> Sketch081
  Dir = (1,0,0)
  DirMode = 2
  FaceMakerClass = Part::FaceMakerBullseye
  LengthFwd = 10
  LengthRev = 0
  Solid = true
  Symmetric = false
FEATURE [Part::Fillet] Fillet059  label="removeFromtMoreFrontCaseScrewRetainers004"
  Base = -> Extrude072
  Edges = 4 edges r=1.49: [Edge6,Edge11,Edge18,Edge23]
  Placement = pos=(-12,0,0) rot=(0,0,1;0rad)
FEATURE [Sketcher::SketchObject] Sketch082
  FullyConstrained = true
  Placement = pos=(117,19,0) rot=(0.57735,0.57735,0.57735;2.0944rad)
  sketch-geometry (8):
    g0: LineSegment StartX=-49.19 StartY=69.25 StartZ=0 EndX=-49.19 EndY=66.25 EndZ=0
    g1: LineSegment StartX=-49.19 StartY=5.75 StartZ=0 EndX=-49.19 EndY=2.75 EndZ=0
    g2: ArcOfCircle CenterX=-1.5 CenterY=67.75 CenterZ=0 NormalX=0 NormalY=0 NormalZ=1 AngleXU=0 Radius=1.5 StartAngle=4.71239 EndAngle=7.85398
    g3: ArcOfCircle CenterX=-1.5 CenterY=4.25 CenterZ=0 NormalX=0 NormalY=0 NormalZ=1 AngleXU=0 Radius=1.5 StartAngle=4.71239 EndAngle=7.85398
    g4: LineSegment StartX=-49.19 StartY=69.25 StartZ=0 EndX=-1.5 EndY=69.25 EndZ=0
    g5: LineSegment StartX=-49.19 StartY=66.25 StartZ=0 EndX=-1.5 EndY=66.25 EndZ=0
    g6: LineSegment StartX=-49.19 StartY=5.75 StartZ=0 EndX=-1.5 EndY=5.75 EndZ=0
    g7: LineSegment StartX=-49.19 StartY=2.75 StartZ=0 EndX=-1.5 EndY=2.75 EndZ=0
  constraints (19):
    c: Vertical(g0)
    c: Distance(g0) = 3
    c: Block(g0)
    c: Vertical(g1)
    c: Block(g2)
    c: Block(g3)
    c: Block(g1)
    c: Coincident(g4,g0)
    c: Coincident(g4,g2)
    c: Horizontal(g4)
    c: Coincident(g5,g0)
    c: Coincident(g5,g2)
    c: Horizontal(g5)
    c: Coincident(g6,g1)
    c: Coincident(g6,g3)
    c: Horizontal(g6)
    c: Coincident(g7,g1)
    c: Coincident(g7,g3)
    c: Horizontal(g7)
FEATURE [Part::Extrusion] Extrude073
  Base = -> Sketch082
  Dir = (1,0,0)
  DirMode = 2
  FaceMakerClass = Part::FaceMakerBullseye
  LengthFwd = 10
  LengthRev = 0
  Solid = true
  Symmetric = false
FEATURE [Part::Fillet] Fillet060  label="removeFromtMoreFrontCaseScrewRetainers005"
  Base = -> Extrude073
  Edges = 4 edges r=1.49: [Edge6,Edge11,Edge18,Edge23]
  Placement = pos=(-4,0,0) rot=(0,0,1;0rad)
FEATURE [Part::Revolution] Revolve163  label="backCaseScrewRetainer004"
  Angle = 360
  Axis = (0,1,0)
  Base = (0,0,0)
  FaceMakerClass = Part::FaceMakerBullseye
  Placement = pos=(12.5,3,62) rot=(0,0,1;0rad)
  Solid = false
  Source = -> Face149
  Symmetric = false
FEATURE [Part::Revolution] Revolve164  label="frontCaseScrewRetainer006"
  Angle = 360
  Axis = (0,1,0)
  Base = (0,0,0)
  FaceMakerClass = Part::FaceMakerBullseye
  Placement = pos=(89.5,3,68.5) rot=(0,0,1;0rad)
  Solid = false
  Source = -> Face151
  Symmetric = false
FEATURE [Part::Revolution] Revolve165  label="frontCaseScrewRetainer007"
  Angle = 360
  Axis = (0,1,0)
  Base = (0,0,0)
  FaceMakerClass = Part::FaceMakerBullseye
  Placement = pos=(89.5,3,3.5) rot=(0,0,1;0rad)
  Solid = false
  Source = -> Face152
  Symmetric = false
FEATURE [Part::Revolution] Revolve166  label="backCaseScrewRetainer005"
  Angle = 360
  Axis = (0,1,0)
  Base = (0,0,0)
  FaceMakerClass = Part::FaceMakerBullseye
  Placement = pos=(12.5,3,10) rot=(0,0,1;0rad)
  Solid = false
  Source = -> Face150
  Symmetric = false
FEATURE [Part::Revolution] Revolve167  label="moreFrontCaseScrewRetainer006"
  Angle = 360
  Axis = (0,1,0)
  Base = (0,0,0)
  FaceMakerClass = Part::FaceMakerBullseye
  Placement = pos=(109.5,4.5,68.5) rot=(0,0,1;0rad)
  Solid = false
  Source = -> Face153
  Symmetric = false
FEATURE [Part::Revolution] Revolve168  label="moreFrontCaseScrewRetainer007"
  Angle = 360
  Axis = (0,1,0)
  Base = (0,0,0)
  FaceMakerClass = Part::FaceMakerBullseye
  Placement = pos=(109.5,4.5,3.5) rot=(0,0,1;0rad)
  Solid = false
  Source = -> Face154
  Symmetric = false
FEATURE [Part::MultiFuse] Fusion151  label="screwRetainers003"
  Shapes = -> [Revolve168,Revolve167,Revolve166,Revolve165,Revolve164,Revolve163]
FEATURE [Part::Cut] Cut069  label="screwRetainers004"
  Base = -> Fusion151
  Tool = -> Fusion152
FEATURE [Part::Cut] Cut070
  Base = -> Cut069
  Tool = -> Fillet060
FEATURE [Part::Cut] Cut071  label="screwPillars001"
  Base = -> Cut070
  Tool = -> Fillet059
FEATURE [Part::MultiFuse] Fusion153  label="bottom024"
  Shapes = -> [Fusion149,Cut071]
FEATURE [Part::Cylinder] Cylinder067
  Angle = 360
  AttacherType = Attacher::AttachEngine3D
  Height = 10
  Placement = pos=(20.65,12,4.68) rot=(1,0,0;1.5708rad)
  Radius = 2
FEATURE [Part::Cylinder] Cylinder068
  Angle = 360
  AttacherType = Attacher::AttachEngine3D
  Height = 10
  Placement = pos=(20.65,12,67.38) rot=(1,0,0;1.5708rad)
  Radius = 2
FEATURE [Part::Cylinder] Cylinder069
  Angle = 360
  AttacherType = Attacher::AttachEngine3D
  Height = 10
  Placement = pos=(77.15,12,67.38) rot=(1,0,0;1.5708rad)
  Radius = 2
FEATURE [Part::Cylinder] Cylinder070
  Angle = 360
  AttacherType = Attacher::AttachEngine3D
  Height = 10
  Placement = pos=(77.15,12,4.68) rot=(1,0,0;1.5708rad)
  Radius = 2
FEATURE [Part::MultiFuse] Fusion154  label="removeFromThreadedInsertHousing001"
  Shapes = -> [Cylinder069,Cylinder068,Cylinder067,Cylinder070]
FEATURE [Part::Cut] Cut072  label="bottom025"
  Base = -> Fusion153
  Tool = -> Fusion154
FEATURE [Image::ImagePlane] ImagePlane
  XSize = 339
  YSize = 72
FEATURE [Sketcher::SketchObject] Sketch083
  FullyConstrained = true
  MapMode = 5
  Support = -> [XY_Plane]
  sketch-geometry (338):
    g0: LineSegment StartX=-151.619 StartY=28.8932 StartZ=0 EndX=-140.819 EndY=28.8932 EndZ=0
    g1: LineSegment StartX=-151.619 StartY=24.0313 StartZ=0 EndX=-151.619 EndY=28.8932 EndZ=0
    g2: LineSegment StartX=-140.819 StartY=17.7713 StartZ=0 EndX=-151.619 EndY=17.7713 EndZ=0
    g3: LineSegment StartX=-151.619 StartY=17.7713 StartZ=0 EndX=-151.619 EndY=22.6313 EndZ=0
    g4: LineSegment StartX=-151.619 StartY=22.6313 StartZ=0 EndX=-145.128 EndY=22.6313 EndZ=0
    g5: LineSegment StartX=-145.128 StartY=24.0313 StartZ=0 EndX=-140.819 EndY=28.8932 EndZ=0
    g6: LineSegment StartX=-145.128 StartY=22.6313 StartZ=0 EndX=-140.819 EndY=17.7713 EndZ=0
    g7: ArcOfCircle CenterX=-155.157 CenterY=23.3323 CenterZ=0 NormalX=0 NormalY=0 NormalZ=1 AngleXU=0 Radius=6.92354 StartAngle=1.03434 EndAngle=5.24885
    g8: ArcOfCircle CenterX=-155.157 CenterY=23.3323 CenterZ=0 NormalX=0 NormalY=0 NormalZ=1 AngleXU=0 Radius=12.6269 StartAngle=1.28675 EndAngle=4.99643
    g9: LineSegment StartX=-151.619 StartY=35.4532 StartZ=0 EndX=-151.619 EndY=29.2832 EndZ=0
    g10: LineSegment StartX=-151.619 StartY=17.3813 StartZ=0 EndX=-151.619 EndY=11.2113 EndZ=0
    g11-g21: Circle x11 (B-spline internal-alignment scaffolding for g22; pole/knot coordinates omitted)
    g22: BSplineCurve PolesCount=11 KnotsCount=9 Degree=3 IsPeriodic=0
    g23-g31: GeomPoint x9 (B-spline internal-alignment scaffolding for g22; pole/knot coordinates omitted)
    g32-g49: Circle x18 (B-spline internal-alignment scaffolding for g50; pole/knot coordinates omitted)
    g50: BSplineCurve PolesCount=18 KnotsCount=16 Degree=3 IsPeriodic=0
    g51-g66: GeomPoint x16 (B-spline internal-alignment scaffolding for g50; pole/knot coordinates omitted)
    g67: LineSegment StartX=-117.124 StartY=30.093 StartZ=0 EndX=-117.603 EndY=26.5272 EndZ=0
    g68: LineSegment StartX=-117.603 StartY=17.8472 StartZ=0 EndX=-117.124 EndY=14.2659 EndZ=0
    g69: Ellipse CenterX=-109.671 CenterY=20.025 CenterZ=0 NormalX=0 NormalY=0 NormalZ=1 MajorRadius=3.34798 MinorRadius=2.71052 AngleXU=-1.56793
    g70: GeomPoint X=-109.666 Y=18.0598 Z=0
    g71: GeomPoint X=-109.677 Y=21.9902 Z=0
    g72: Ellipse CenterX=-109.671 CenterY=20.0123 CenterZ=0 NormalX=0 NormalY=0 NormalZ=1 MajorRadius=6.93002 MinorRadius=6.36273 AngleXU=-3.13976
    g73: GeomPoint X=-112.417 Y=20.0073 Z=0
    g74: GeomPoint X=-106.925 Y=20.0173 Z=0
    g75: Ellipse CenterX=-51.7682 CenterY=20.1463 CenterZ=0 NormalX=0 NormalY=0 NormalZ=1 MajorRadius=3.19279 MinorRadius=2.71052 AngleXU=-1.52774
    g76: GeomPoint X=-51.6955 Y=18.4606 Z=0
    g77: GeomPoint X=-51.8408 Y=21.832 Z=0
    g78: GeomPoint X=-54.5142 Y=20.1413 Z=0
    g79: GeomPoint X=-49.0221 Y=20.1513 Z=0
    g80: Ellipse CenterX=-51.7682 CenterY=20.1463 CenterZ=0 NormalX=0 NormalY=0 NormalZ=1 MajorRadius=6.93002 MinorRadius=6.36273 AngleXU=-3.13976
    g81: Ellipse CenterX=-22.8436 CenterY=20.1783 CenterZ=0 NormalX=0 NormalY=0 NormalZ=1 MajorRadius=3.31512 MinorRadius=2.71052 AngleXU=-1.60214
    g82: GeomPoint X=-22.9034 Y=18.2706 Z=0
    g83: GeomPoint X=-22.7838 Y=22.0861 Z=0
    g84: GeomPoint X=-25.5897 Y=20.1733 Z=0
    g85: GeomPoint X=-20.0976 Y=20.1833 Z=0
    g86: Ellipse CenterX=-22.8436 CenterY=20.1783 CenterZ=0 NormalX=0 NormalY=0 NormalZ=1 MajorRadius=6.93002 MinorRadius=6.36273 AngleXU=-3.13976
    g87: LineSegment StartX=-101.889 StartY=14.1107 StartZ=0 EndX=-97.7455 EndY=14.1107 EndZ=0
    g88: LineSegment StartX=-93.8155 StartY=14.1107 StartZ=0 EndX=-89.6755 EndY=14.1107 EndZ=0
    g89: LineSegment StartX=-85.7455 StartY=14.1107 StartZ=0 EndX=-81.6055 EndY=14.1107 EndZ=0
    g90: LineSegment StartX=-101.889 StartY=14.1107 StartZ=0 EndX=-101.889 EndY=25.9907 EndZ=0
    g91: LineSegment StartX=-101.889 StartY=25.9907 StartZ=0 EndX=-97.8594 EndY=25.9907 EndZ=0
    g92: LineSegment StartX=-97.8594 StartY=25.9907 StartZ=0 EndX=-97.8594 EndY=24.0907 EndZ=0
    g93: LineSegment StartX=-97.7455 StartY=14.1107 StartZ=0 EndX=-97.7455 EndY=19.9107 EndZ=0
    g94: LineSegment StartX=-89.6755 StartY=14.1107 StartZ=0 EndX=-89.6755 EndY=19.9107 EndZ=0
    g95: LineSegment StartX=-93.8155 StartY=14.1107 StartZ=0 EndX=-93.8155 EndY=21.0107 EndZ=0
    g96-g106: Circle x11 (B-spline internal-alignment scaffolding for g107; pole/knot coordinates omitted)
    g107: BSplineCurve PolesCount=11 KnotsCount=9 Degree=3 IsPeriodic=0
    g108-g116: GeomPoint x9 (B-spline internal-alignment scaffolding for g107; pole/knot coordinates omitted)
    g117: BSplineCurve PolesCount=11 KnotsCount=9 Degree=3 IsPeriodic=0
    g118-g125: Circle x8 (B-spline internal-alignment scaffolding for g126; pole/knot coordinates omitted)
    g126: BSplineCurve PolesCount=8 KnotsCount=6 Degree=3 IsPeriodic=0
    g127-g132: GeomPoint x6 (B-spline internal-alignment scaffolding for g126; pole/knot coordinates omitted)
    g133: BSplineCurve PolesCount=8 KnotsCount=6 Degree=3 IsPeriodic=0
    g134: LineSegment StartX=-85.7455 StartY=21.0107 StartZ=0 EndX=-85.7455 EndY=14.1107 EndZ=0
    g135: LineSegment StartX=-80.0879 StartY=14.1107 StartZ=0 EndX=-75.944 EndY=14.1107 EndZ=0
    g136: LineSegment StartX=-72.014 StartY=14.1107 StartZ=0 EndX=-67.874 EndY=14.1107 EndZ=0
    g137: LineSegment StartX=-63.944 StartY=14.1107 StartZ=0 EndX=-59.804 EndY=14.1107 EndZ=0
    g138: LineSegment StartX=-80.0879 StartY=14.1107 StartZ=0 EndX=-80.0879 EndY=25.9907 EndZ=0
    g139: LineSegment StartX=-80.0879 StartY=25.9907 StartZ=0 EndX=-76.0579 EndY=25.9907 EndZ=0
    g140: LineSegment StartX=-76.0579 StartY=25.9907 StartZ=0 EndX=-76.0579 EndY=24.0907 EndZ=0
    g141: LineSegment StartX=-75.944 StartY=14.1107 StartZ=0 EndX=-75.944 EndY=19.9107 EndZ=0
    g142: LineSegment StartX=-67.874 StartY=14.1107 StartZ=0 EndX=-67.874 EndY=19.9107 EndZ=0
    g143: LineSegment StartX=-72.014 StartY=14.1107 StartZ=0 EndX=-72.014 EndY=21.0107 EndZ=0
    g144-g148: Circle x5 (B-spline internal-alignment scaffolding for g149; pole/knot coordinates omitted)
    g149: BSplineCurve PolesCount=11 KnotsCount=9 Degree=3 IsPeriodic=0
    g150-g158: GeomPoint x9 (B-spline internal-alignment scaffolding for g149; pole/knot coordinates omitted)
    g159: BSplineCurve PolesCount=11 KnotsCount=9 Degree=3 IsPeriodic=0
    g160-g167: Circle x8 (B-spline internal-alignment scaffolding for g168; pole/knot coordinates omitted)
    g168: BSplineCurve PolesCount=8 KnotsCount=6 Degree=3 IsPeriodic=0
    g169-g174: GeomPoint x6 (B-spline internal-alignment scaffolding for g168; pole/knot coordinates omitted)
    g175: BSplineCurve PolesCount=8 KnotsCount=6 Degree=3 IsPeriodic=0
    g176: LineSegment StartX=-63.944 StartY=21.0107 StartZ=0 EndX=-63.944 EndY=14.1107 EndZ=0
    g177: LineSegment StartX=-59.804 StartY=14.1107 StartZ=0 EndX=-59.804 EndY=21.5868 EndZ=0
    g178: BSplineCurve PolesCount=4 KnotsCount=2 Degree=3 IsPeriodic=0
    g179: GeomPoint X=-59.804 Y=21.5868 Z=0
    g180: GeomPoint X=-60.2379 Y=24.0907 Z=0
    g181: LineSegment StartX=-81.6055 StartY=14.1107 StartZ=0 EndX=-81.6055 EndY=21.5868 EndZ=0
    g182: LineSegment StartX=-151.619 StartY=24.0313 StartZ=0 EndX=-145.128 EndY=24.0313 EndZ=0
    g183: Circle CenterX=-82.0394 CenterY=24.0907 CenterZ=0 NormalX=0 NormalY=0 NormalZ=1 AngleXU=0 Radius=1
    g184: Circle CenterX=-81.7131 CenterY=23.2736 CenterZ=0 NormalX=0 NormalY=0 NormalZ=1 AngleXU=0 Radius=1
    g185: Circle CenterX=-81.6055 CenterY=21.5868 CenterZ=0 NormalX=0 NormalY=0 NormalZ=1 AngleXU=0 Radius=1
    g186: BSplineCurve PolesCount=3 KnotsCount=2 Degree=2 IsPeriodic=0
    g187: GeomPoint X=-82.0394 Y=24.0907 Z=0
    g188: GeomPoint X=-81.6055 Y=21.5868 Z=0
    g189: Ellipse CenterX=-37.3522 CenterY=19.9515 CenterZ=0 NormalX=0 NormalY=0 NormalZ=1 MajorRadius=2.99755 MinorRadius=2.49 AngleXU=1.5708
    g190: GeomPoint X=-37.3522 Y=21.6203 Z=0
    g191: GeomPoint X=-37.3522 Y=18.2826 Z=0
    g192: ArcOfEllipse CenterX=-38.7647 CenterY=20.06 CenterZ=0 NormalX=0 NormalY=0 NormalZ=1 MajorRadius=6.30025 MinorRadius=5.3849 AngleXU=1.57276 StartAngle=5.50632 EndAngle=10.3035
    g193: GeomPoint X=-38.7711 Y=23.3304 Z=0
    g194: GeomPoint X=-38.7583 Y=16.7895 Z=0
    g195: LineSegment StartX=-34.6109 StartY=14.1107 StartZ=0 EndX=-30.8984 EndY=14.1107 EndZ=0
    g196: LineSegment StartX=-30.8984 StartY=14.1107 StartZ=0 EndX=-30.8984 EndY=31.1784 EndZ=0
    g197: LineSegment StartX=-30.8984 StartY=31.1784 StartZ=0 EndX=-34.9984 EndY=31.1784 EndZ=0
    g198: LineSegment StartX=-34.9984 StartY=24.5602 StartZ=0 EndX=-34.9984 EndY=31.1784 EndZ=0
    g199: LineSegment StartX=-34.6109 StartY=16.0476 StartZ=0 EndX=-34.6109 EndY=14.1107 EndZ=0
    g200: LineSegment StartX=-14.8781 StartY=14.1107 StartZ=0 EndX=-10.5106 EndY=14.1107 EndZ=0
    g201: LineSegment StartX=-14.8781 StartY=14.1107 StartZ=0 EndX=-14.8781 EndY=25.8504 EndZ=0
    g202: LineSegment StartX=-14.8781 StartY=25.8504 StartZ=0 EndX=-10.8534 EndY=25.8504 EndZ=0
    g203: LineSegment StartX=-10.8534 StartY=25.8504 StartZ=0 EndX=-10.8534 EndY=24.0923 EndZ=0
    g204: LineSegment StartX=-10.5106 StartY=14.1107 StartZ=0 EndX=-10.5106 EndY=19.7752 EndZ=0
    g205: LineSegment StartX=-5.96397 StartY=25.9304 StartZ=0 EndX=-5.96397 EndY=22.574 EndZ=0
    g206-g214: Circle x9 (B-spline internal-alignment scaffolding for g215; pole/knot coordinates omitted)
    g215: BSplineCurve PolesCount=9 KnotsCount=7 Degree=3 IsPeriodic=0
    g216-g222: GeomPoint x7 (B-spline internal-alignment scaffolding for g215; pole/knot coordinates omitted)
    g223-g232: Circle x10 (B-spline internal-alignment scaffolding for g233; pole/knot coordinates omitted)
    g233: BSplineCurve PolesCount=10 KnotsCount=8 Degree=3 IsPeriodic=0
    g234-g241: GeomPoint x8 (B-spline internal-alignment scaffolding for g233; pole/knot coordinates omitted)
    g242: LineSegment StartX=-1.58923 StartY=21.0696 StartZ=0 EndX=2.62034 EndY=21.0696 EndZ=0
    g243: LineSegment StartX=-1.55856 StartY=18.7342 StartZ=0 EndX=6.45946 EndY=18.7342 EndZ=0
    g244: LineSegment StartX=5.29231 StartY=17.386 StartZ=0 EndX=5.29231 EndY=14.3674 EndZ=0
    g245-g269: Circle x25 (B-spline internal-alignment scaffolding for g270; pole/knot coordinates omitted)
    g270: BSplineCurve PolesCount=25 KnotsCount=23 Degree=3 IsPeriodic=0
    g271-g293: GeomPoint x23 (B-spline internal-alignment scaffolding for g270; pole/knot coordinates omitted)
    g294-g304: Circle x11 (B-spline internal-alignment scaffolding for g305; pole/knot coordinates omitted)
    g305: BSplineCurve PolesCount=11 KnotsCount=9 Degree=3 IsPeriodic=0
    g306-g314: GeomPoint x9 (B-spline internal-alignment scaffolding for g305; pole/knot coordinates omitted)
    g315-g326: Circle x12 (B-spline internal-alignment scaffolding for g327; pole/knot coordinates omitted)
    g327: BSplineCurve PolesCount=12 KnotsCount=10 Degree=3 IsPeriodic=0
    g328-g337: GeomPoint x10 (B-spline internal-alignment scaffolding for g327; pole/knot coordinates omitted)
  constraints (252):
    c: Coincident(g1,g0)
    c: Horizontal(g0)
    c: Vertical(g1)
    c: Coincident(g2,g3)
    c: Coincident(g3,g4)
    c: Horizontal(g4)
    c: Horizontal(g2)
    c: Vertical(g3)
    c: Block(g1)
    c: Distance(g3) = 4.86
    c: Block(g4)
    c: Distance(g0) = 10.8
    c: Distance(g2) = 10.8
    c: Coincident(g5,g0)
    c: Coincident(g6,g4)
    c: Coincident(g6,g2)
    c: Block(g8)
    c: Block(g7)
    c: Coincident(g9,g8)
    c: Coincident(g9,g7)
    c: Vertical(g9)
    c: Coincident(g10,g7)
    c: Coincident(g10,g8)
    c: Vertical(g10)
    c: Weight(g11) = 1
    c: Equal(g11, g12-g21) x10
    c: InternalAlignment(g11-g21 -> g22) x11
    c: InternalAlignment(g23-g31 -> g22) x9
    c: Block(g22)
    c: Weight(g32) = 1
    c: Equal(g32, g33-g49) x17
    c: InternalAlignment(g32-g49 -> g50) x18
    c: InternalAlignment(g51-g66 -> g50) x16
    c: Block(g50)
    c: Coincident(g67,g50)
    c: Coincident(g67,g22)
    c: Coincident(g68,g22)
    c: Coincident(g68,g50)
    c: InternalAlignment(g70,g69)
    c: InternalAlignment(g71,g69)
    c: Block(g69)
    c: InternalAlignment(g73,g72)
    c: InternalAlignment(g74,g72)
    c: Block(g72)
    c: InternalAlignment(g76,g75)
    c: InternalAlignment(g77,g75)
    c: InternalAlignment(g78,g80)
    c: InternalAlignment(g79,g80)
    c: Block(g80)
    c: Coincident(g75,g80)
    c: Block(g75)
    c: InternalAlignment(g82,g81)
    c: InternalAlignment(g83,g81)
    c: InternalAlignment(g84,g86)
    c: InternalAlignment(g85,g86)
    c: Block(g86)
    c: Coincident(g81,g86)
    c: Block(g81)
    c: Horizontal(g87)
    c: Block(g87)
    c: Horizontal(g88)
    c: Distance(g88) = 4.14
    c: Horizontal(g89)
    c: Equal(g88,g89) = 4.14
    c: Block(g89)
    c: Block(g88)
    c: Coincident(g90,g87)
    c: Vertical(g90)
    c: Distance(g90) = 11.88
    c: Coincident(g91,g90)
    c: Horizontal(g91)
    c: Coincident(g92,g91)
    c: Vertical(g92)
    c: Distance(g91) = 4.03
    c: Distance(g92) = 1.9
    c: Coincident(g93,g87)
    c: Vertical(g93)
    c: Vertical(g94)
    c: Coincident(g94,g88)
    c: Distance(g93) = 5.8
    c: Distance(g94) = 5.8
    c: Vertical(g95)
    c: Coincident(g95,g88)
    c: Distance(g95) = 6.9
    c: Coincident(g107,g92)
    c: Weight(g96) = 1
    c: Equal(g96, g97-g106) x10
    c: InternalAlignment(g96-g106 -> g107) x11
    c: InternalAlignment(g108-g116 -> g107) x9
    c: Block(g107)
    c: Block(g117)
    c: Coincident(g126,g93)
    c: Weight(g118) = 1
    c: Equal(g118, g119-g125) x7
    c: Coincident(g126,g95)
    c: InternalAlignment(g118-g125 -> g126) x8
    c: InternalAlignment(g127-g132 -> g126) x6
    c: Coincident(g133,g94)
    c: Block(g126)
    c: Block(g133)
    c: Coincident(g134,g133)
    c: Coincident(g134,g89)
    c: Vertical(g134)
    c: Horizontal(g135)
    c: Block(g135)
    c: Horizontal(g136)
    c: Equal(g88,g136) = 4.14
    c: Horizontal(g137)
    c: Equal(g136,g137) = 4.14
    c: Block(g137)
    c: Block(g136)
    c: Coincident(g138,g135)
    c: Vertical(g138)
    c: Equal(g90,g138) = 11.88
    c: Coincident(g139,g138)
    c: Horizontal(g139)
    c: Coincident(g140,g139)
    c: Vertical(g140)
    c: Equal(g91,g139) = 4.03
    c: Equal(g92,g140) = 1.9
    c: Coincident(g141,g135)
    c: Vertical(g141)
    c: Vertical(g142)
    c: Coincident(g142,g136)
    c: Equal(g93,g141) = 5.8
    c: Equal(g94,g142) = 5.8
    c: Vertical(g143)
    c: Coincident(g143,g136)
    c: Equal(g95,g143) = 6.9
    c: Coincident(g149,g140)
    c: Equal(g96,g144) = 1
    c: Equal(g144, g145-g148) x4
    c: InternalAlignment(g144-g148 -> g149) x5
    c: InternalAlignment(g150-g158 -> g149) x9
    c: Block(g149)
    c: Block(g159)
    c: Coincident(g168,g141)
    c: Equal(g118,g160) = 1
    c: Equal(g160, g161-g167) x7
    c: Coincident(g168,g143)
    c: InternalAlignment(g160-g167 -> g168) x8
    c: InternalAlignment(g169-g174 -> g168) x6
    c: Coincident(g175,g142)
    c: Block(g168)
    c: Block(g175)
    c: Coincident(g176,g175)
    c: Coincident(g176,g137)
    c: Vertical(g176)
    c: Coincident(g177,g137)
    c: Vertical(g177)
    c: Coincident(g178,g177)
    c: Coincident(g178,g159)
    c: InternalAlignment(g179,g178)
    c: InternalAlignment(g180,g178)
    c: Block(g178)
    c: Vertical(g181)
    c: Coincident(g181,g89)
    c: Block(g5)
    c: Coincident(g182,g1)
    c: Coincident(g182,g5)
    c: Horizontal(g182)
    c: Coincident(g186,g117)
    c: Weight(g183) = 1
    c: Equal(g183,g184)
    c: Equal(g183,g185)
    c: Coincident(g186,g181)
    c: InternalAlignment(g183,g186)
    c: InternalAlignment(g184,g186)
    c: InternalAlignment(g185,g186)
    c: InternalAlignment(g187,g186)
    c: InternalAlignment(g188,g186)
    c: Block(g186)
    c: InternalAlignment(g190,g189)
    c: InternalAlignment(g191,g189)
    c: Block(g189)
    c: InternalAlignment(g193,g192)
    c: InternalAlignment(g194,g192)
    c: Block(g192)
    c: Horizontal(g195)
    c: Block(g195)
    c: Coincident(g196,g195)
    c: Vertical(g196)
    c: Block(g196)
    c: Distance(g195) = 3.71244
    c: Coincident(g197,g196)
    c: Horizontal(g197)
    c: Distance(g197) = 4.1
    c: Coincident(g198,g192)
    c: Coincident(g198,g197)
    c: Vertical(g198)
    c: Block(g198)
    c: Coincident(g199,g192)
    c: Coincident(g199,g195)
    c: Vertical(g199)
    c: Block(g199)
    c: Horizontal(g200)
    c: Block(g200)
    c: Coincident(g201,g200)
    c: Vertical(g201)
    c: Block(g201)
    c: Coincident(g202,g201)
    c: Horizontal(g202)
    c: Block(g202)
    c: Coincident(g203,g202)
    c: Vertical(g203)
    c: Block(g203)
    c: Coincident(g204,g200)
    c: Vertical(g204)
    c: Block(g204)
    c: Coincident(g215,g203)
    c: Weight(g206) = 1
    c: Equal(g206, g207-g214) x8
    c: Coincident(g215,g205)
    c: InternalAlignment(g206-g214 -> g215) x9
    c: InternalAlignment(g216-g222 -> g215) x7
    c: Coincident(g233,g204)
    c: Weight(g223) = 1
    c: Equal(g223, g224-g232) x9
    c: Coincident(g233,g205)
    c: InternalAlignment(g223-g232 -> g233) x10
    c: InternalAlignment(g234-g241 -> g233) x8
    c: Vertical(g205)
    c: Block(g205)
    c: Block(g215)
    c: Block(g233)
    c: Horizontal(g242)
    c: Horizontal(g243)
    c: Block(g242)
    c: Block(g243)
    c: Vertical(g244)
    c: Block(g244)
    c: Coincident(g270,g243)
    c: Weight(g245) = 1
    c: Equal(g245, g246-g269) x24
    c: Coincident(g270,g244)
    c: InternalAlignment(g245-g269 -> g270) x25
    c: InternalAlignment(g271-g293 -> g270) x23
    c: Coincident(g305,g242)
    c: Weight(g294) = 1
    c: Equal(g294, g295-g304) x10
    c: Coincident(g305,g242)
    c: InternalAlignment(g294-g304 -> g305) x11
    c: InternalAlignment(g306-g314 -> g305) x9
    c: Block(g305)
    c: Coincident(g327,g243)
    c: Weight(g315) = 1
    c: Equal(g315, g316-g326) x11
    c: Coincident(g327,g244)
    c: InternalAlignment(g315-g326 -> g327) x12
    c: InternalAlignment(g328-g337 -> g327) x10
    c: Block(g327)
    c: Block(g270)
FEATURE [PartDesign::Body] Body  label="CommodoreLogoAndText"
  Group = -> [Sketch083]
  Origin = -> Origin
FEATURE [Part::Extrusion] Extrude074  label="CommodoreLogoAndText001"
  Base = -> Sketch083
  Dir = (0,0,1)
  DirMode = 2
  FaceMakerClass = Part::FaceMakerBullseye
  LengthFwd = 10
  LengthRev = 0
  Solid = true
  Symmetric = false
FEATURE [Part::FeaturePython] Clone  label="CommodoreLogoAndTextScale"  # Draft clone (typed FeaturePython)
  AttacherType = Attacher::AttachEngine3D
  Fuse = false
  Objects = -> [Extrude074]
  Placement = pos=(111,5.37,-11.6) rot=(0,0,1;0rad)
  Scale = (0.62,0.62,1)
FEATURE [Part::Mirroring] Part__Mirroring  label="CommodoreLogoAndTextScale (Mirror #1)"
  Base = (0,0,0)
  Normal = (1,0,0)
  Placement = pos=(123.576,0,0) rot=(0,0,1;0rad)
  Source = -> Clone
FEATURE [Sketcher::SketchObject] Sketch084
  FullyConstrained = true
  MapMode = 5
  Support = -> [XY_Plane001]
  sketch-geometry (338):
    g0: LineSegment StartX=-151.619 StartY=28.8932 StartZ=0 EndX=-140.819 EndY=28.8932 EndZ=0
    g1: LineSegment StartX=-151.619 StartY=24.0313 StartZ=0 EndX=-151.619 EndY=28.8932 EndZ=0
    g2: LineSegment StartX=-140.819 StartY=17.7713 StartZ=0 EndX=-151.619 EndY=17.7713 EndZ=0
    g3: LineSegment StartX=-151.619 StartY=17.7713 StartZ=0 EndX=-151.619 EndY=22.6313 EndZ=0
    g4: LineSegment StartX=-151.619 StartY=22.6313 StartZ=0 EndX=-145.128 EndY=22.6313 EndZ=0
    g5: LineSegment StartX=-145.128 StartY=24.0313 StartZ=0 EndX=-140.819 EndY=28.8932 EndZ=0
    g6: LineSegment StartX=-145.128 StartY=22.6313 StartZ=0 EndX=-140.819 EndY=17.7713 EndZ=0
    g7: ArcOfCircle CenterX=-155.157 CenterY=23.3323 CenterZ=0 NormalX=0 NormalY=0 NormalZ=1 AngleXU=0 Radius=6.92354 StartAngle=1.03434 EndAngle=5.24885
    g8: ArcOfCircle CenterX=-155.157 CenterY=23.3323 CenterZ=0 NormalX=0 NormalY=0 NormalZ=1 AngleXU=0 Radius=12.6269 StartAngle=1.28675 EndAngle=4.99643
    g9: LineSegment StartX=-151.619 StartY=35.4532 StartZ=0 EndX=-151.619 EndY=29.2832 EndZ=0
    g10: LineSegment StartX=-151.619 StartY=17.3813 StartZ=0 EndX=-151.619 EndY=11.2113 EndZ=0
    g11-g21: Circle x11 (B-spline internal-alignment scaffolding for g22; pole/knot coordinates omitted)
    g22: BSplineCurve PolesCount=11 KnotsCount=9 Degree=3 IsPeriodic=0
    g23-g31: GeomPoint x9 (B-spline internal-alignment scaffolding for g22; pole/knot coordinates omitted)
    g32-g49: Circle x18 (B-spline internal-alignment scaffolding for g50; pole/knot coordinates omitted)
    g50: BSplineCurve PolesCount=18 KnotsCount=16 Degree=3 IsPeriodic=0
    g51-g66: GeomPoint x16 (B-spline internal-alignment scaffolding for g50; pole/knot coordinates omitted)
    g67: LineSegment StartX=-117.124 StartY=30.093 StartZ=0 EndX=-117.603 EndY=26.5272 EndZ=0
    g68: LineSegment StartX=-117.603 StartY=17.8472 StartZ=0 EndX=-117.124 EndY=14.2659 EndZ=0
    g69: Ellipse CenterX=-109.671 CenterY=20.025 CenterZ=0 NormalX=0 NormalY=0 NormalZ=1 MajorRadius=3.34798 MinorRadius=2.71052 AngleXU=-1.56793
    g70: GeomPoint X=-109.666 Y=18.0598 Z=0
    g71: GeomPoint X=-109.677 Y=21.9902 Z=0
    g72: Ellipse CenterX=-109.671 CenterY=20.0123 CenterZ=0 NormalX=0 NormalY=0 NormalZ=1 MajorRadius=6.93002 MinorRadius=6.36273 AngleXU=-3.13976
    g73: GeomPoint X=-112.417 Y=20.0073 Z=0
    g74: GeomPoint X=-106.925 Y=20.0173 Z=0
    g75: Ellipse CenterX=-51.7682 CenterY=20.1463 CenterZ=0 NormalX=0 NormalY=0 NormalZ=1 MajorRadius=3.19279 MinorRadius=2.71052 AngleXU=-1.52774
    g76: GeomPoint X=-51.6955 Y=18.4606 Z=0
    g77: GeomPoint X=-51.8408 Y=21.832 Z=0
    g78: GeomPoint X=-54.5142 Y=20.1413 Z=0
    g79: GeomPoint X=-49.0221 Y=20.1513 Z=0
    g80: Ellipse CenterX=-51.7682 CenterY=20.1463 CenterZ=0 NormalX=0 NormalY=0 NormalZ=1 MajorRadius=6.93002 MinorRadius=6.36273 AngleXU=-3.13976
    g81: Ellipse CenterX=-22.8436 CenterY=20.1783 CenterZ=0 NormalX=0 NormalY=0 NormalZ=1 MajorRadius=3.31512 MinorRadius=2.71052 AngleXU=-1.60214
    g82: GeomPoint X=-22.9034 Y=18.2706 Z=0
    g83: GeomPoint X=-22.7838 Y=22.0861 Z=0
    g84: GeomPoint X=-25.5897 Y=20.1733 Z=0
    g85: GeomPoint X=-20.0976 Y=20.1833 Z=0
    g86: Ellipse CenterX=-22.8436 CenterY=20.1783 CenterZ=0 NormalX=0 NormalY=0 NormalZ=1 MajorRadius=6.93002 MinorRadius=6.36273 AngleXU=-3.13976
    g87: LineSegment StartX=-101.889 StartY=14.1107 StartZ=0 EndX=-97.7455 EndY=14.1107 EndZ=0
    g88: LineSegment StartX=-93.8155 StartY=14.1107 StartZ=0 EndX=-89.6755 EndY=14.1107 EndZ=0
    g89: LineSegment StartX=-85.7455 StartY=14.1107 StartZ=0 EndX=-81.6055 EndY=14.1107 EndZ=0
    g90: LineSegment StartX=-101.889 StartY=14.1107 StartZ=0 EndX=-101.889 EndY=25.9907 EndZ=0
    g91: LineSegment StartX=-101.889 StartY=25.9907 StartZ=0 EndX=-97.8594 EndY=25.9907 EndZ=0
    g92: LineSegment StartX=-97.8594 StartY=25.9907 StartZ=0 EndX=-97.8594 EndY=24.0907 EndZ=0
    g93: LineSegment StartX=-97.7455 StartY=14.1107 StartZ=0 EndX=-97.7455 EndY=19.9107 EndZ=0
    g94: LineSegment StartX=-89.6755 StartY=14.1107 StartZ=0 EndX=-89.6755 EndY=19.9107 EndZ=0
    g95: LineSegment StartX=-93.8155 StartY=14.1107 StartZ=0 EndX=-93.8155 EndY=21.0107 EndZ=0
    g96-g106: Circle x11 (B-spline internal-alignment scaffolding for g107; pole/knot coordinates omitted)
    g107: BSplineCurve PolesCount=11 KnotsCount=9 Degree=3 IsPeriodic=0
    g108-g116: GeomPoint x9 (B-spline internal-alignment scaffolding for g107; pole/knot coordinates omitted)
    g117: BSplineCurve PolesCount=11 KnotsCount=9 Degree=3 IsPeriodic=0
    g118-g125: Circle x8 (B-spline internal-alignment scaffolding for g126; pole/knot coordinates omitted)
    g126: BSplineCurve PolesCount=8 KnotsCount=6 Degree=3 IsPeriodic=0
    g127-g132: GeomPoint x6 (B-spline internal-alignment scaffolding for g126; pole/knot coordinates omitted)
    g133: BSplineCurve PolesCount=8 KnotsCount=6 Degree=3 IsPeriodic=0
    g134: LineSegment StartX=-85.7455 StartY=21.0107 StartZ=0 EndX=-85.7455 EndY=14.1107 EndZ=0
    g135: LineSegment StartX=-80.0879 StartY=14.1107 StartZ=0 EndX=-75.944 EndY=14.1107 EndZ=0
    g136: LineSegment StartX=-72.014 StartY=14.1107 StartZ=0 EndX=-67.874 EndY=14.1107 EndZ=0
    g137: LineSegment StartX=-63.944 StartY=14.1107 StartZ=0 EndX=-59.804 EndY=14.1107 EndZ=0
    g138: LineSegment StartX=-80.0879 StartY=14.1107 StartZ=0 EndX=-80.0879 EndY=25.9907 EndZ=0
    g139: LineSegment StartX=-80.0879 StartY=25.9907 StartZ=0 EndX=-76.0579 EndY=25.9907 EndZ=0
    g140: LineSegment StartX=-76.0579 StartY=25.9907 StartZ=0 EndX=-76.0579 EndY=24.0907 EndZ=0
    g141: LineSegment StartX=-75.944 StartY=14.1107 StartZ=0 EndX=-75.944 EndY=19.9107 EndZ=0
    g142: LineSegment StartX=-67.874 StartY=14.1107 StartZ=0 EndX=-67.874 EndY=19.9107 EndZ=0
    g143: LineSegment StartX=-72.014 StartY=14.1107 StartZ=0 EndX=-72.014 EndY=21.0107 EndZ=0
    g144-g148: Circle x5 (B-spline internal-alignment scaffolding for g149; pole/knot coordinates omitted)
    g149: BSplineCurve PolesCount=11 KnotsCount=9 Degree=3 IsPeriodic=0
    g150-g158: GeomPoint x9 (B-spline internal-alignment scaffolding for g149; pole/knot coordinates omitted)
    g159: BSplineCurve PolesCount=11 KnotsCount=9 Degree=3 IsPeriodic=0
    g160-g167: Circle x8 (B-spline internal-alignment scaffolding for g168; pole/knot coordinates omitted)
    g168: BSplineCurve PolesCount=8 KnotsCount=6 Degree=3 IsPeriodic=0
    g169-g174: GeomPoint x6 (B-spline internal-alignment scaffolding for g168; pole/knot coordinates omitted)
    g175: BSplineCurve PolesCount=8 KnotsCount=6 Degree=3 IsPeriodic=0
    g176: LineSegment StartX=-63.944 StartY=21.0107 StartZ=0 EndX=-63.944 EndY=14.1107 EndZ=0
    g177: LineSegment StartX=-59.804 StartY=14.1107 StartZ=0 EndX=-59.804 EndY=21.5868 EndZ=0
    g178: BSplineCurve PolesCount=4 KnotsCount=2 Degree=3 IsPeriodic=0
    g179: GeomPoint X=-59.804 Y=21.5868 Z=0
    g180: GeomPoint X=-60.2379 Y=24.0907 Z=0
    g181: LineSegment StartX=-81.6055 StartY=14.1107 StartZ=0 EndX=-81.6055 EndY=21.5868 EndZ=0
    g182: LineSegment StartX=-151.619 StartY=24.0313 StartZ=0 EndX=-145.128 EndY=24.0313 EndZ=0
    g183: Circle CenterX=-82.0394 CenterY=24.0907 CenterZ=0 NormalX=0 NormalY=0 NormalZ=1 AngleXU=0 Radius=1
    g184: Circle CenterX=-81.7131 CenterY=23.2736 CenterZ=0 NormalX=0 NormalY=0 NormalZ=1 AngleXU=0 Radius=1
    g185: Circle CenterX=-81.6055 CenterY=21.5868 CenterZ=0 NormalX=0 NormalY=0 NormalZ=1 AngleXU=0 Radius=1
    g186: BSplineCurve PolesCount=3 KnotsCount=2 Degree=2 IsPeriodic=0
    g187: GeomPoint X=-82.0394 Y=24.0907 Z=0
    g188: GeomPoint X=-81.6055 Y=21.5868 Z=0
    g189: Ellipse CenterX=-37.3522 CenterY=19.9515 CenterZ=0 NormalX=0 NormalY=0 NormalZ=1 MajorRadius=2.99755 MinorRadius=2.49 AngleXU=1.5708
    g190: GeomPoint X=-37.3522 Y=21.6203 Z=0
    g191: GeomPoint X=-37.3522 Y=18.2826 Z=0
    g192: ArcOfEllipse CenterX=-38.7647 CenterY=20.06 CenterZ=0 NormalX=0 NormalY=0 NormalZ=1 MajorRadius=6.30025 MinorRadius=5.3849 AngleXU=1.57276 StartAngle=5.50632 EndAngle=10.3035
    g193: GeomPoint X=-38.7711 Y=23.3304 Z=0
    g194: GeomPoint X=-38.7583 Y=16.7895 Z=0
    g195: LineSegment StartX=-34.6109 StartY=14.1107 StartZ=0 EndX=-30.8984 EndY=14.1107 EndZ=0
    g196: LineSegment StartX=-30.8984 StartY=14.1107 StartZ=0 EndX=-30.8984 EndY=31.1784 EndZ=0
    g197: LineSegment StartX=-30.8984 StartY=31.1784 StartZ=0 EndX=-34.9984 EndY=31.1784 EndZ=0
    g198: LineSegment StartX=-34.9984 StartY=24.5602 StartZ=0 EndX=-34.9984 EndY=31.1784 EndZ=0
    g199: LineSegment StartX=-34.6109 StartY=16.0476 StartZ=0 EndX=-34.6109 EndY=14.1107 EndZ=0
    g200: LineSegment StartX=-14.8781 StartY=14.1107 StartZ=0 EndX=-10.5106 EndY=14.1107 EndZ=0
    g201: LineSegment StartX=-14.8781 StartY=14.1107 StartZ=0 EndX=-14.8781 EndY=25.8504 EndZ=0
    g202: LineSegment StartX=-14.8781 StartY=25.8504 StartZ=0 EndX=-10.8534 EndY=25.8504 EndZ=0
    g203: LineSegment StartX=-10.8534 StartY=25.8504 StartZ=0 EndX=-10.8534 EndY=24.0923 EndZ=0
    g204: LineSegment StartX=-10.5106 StartY=14.1107 StartZ=0 EndX=-10.5106 EndY=19.7752 EndZ=0
    g205: LineSegment StartX=-5.96397 StartY=25.9304 StartZ=0 EndX=-5.96397 EndY=22.574 EndZ=0
    g206-g214: Circle x9 (B-spline internal-alignment scaffolding for g215; pole/knot coordinates omitted)
    g215: BSplineCurve PolesCount=9 KnotsCount=7 Degree=3 IsPeriodic=0
    g216-g222: GeomPoint x7 (B-spline internal-alignment scaffolding for g215; pole/knot coordinates omitted)
    g223-g232: Circle x10 (B-spline internal-alignment scaffolding for g233; pole/knot coordinates omitted)
    g233: BSplineCurve PolesCount=10 KnotsCount=8 Degree=3 IsPeriodic=0
    g234-g241: GeomPoint x8 (B-spline internal-alignment scaffolding for g233; pole/knot coordinates omitted)
    g242: LineSegment StartX=-1.58923 StartY=21.0696 StartZ=0 EndX=2.62034 EndY=21.0696 EndZ=0
    g243: LineSegment StartX=-1.55856 StartY=18.7342 StartZ=0 EndX=6.45946 EndY=18.7342 EndZ=0
    g244: LineSegment StartX=5.29231 StartY=17.386 StartZ=0 EndX=5.29231 EndY=14.3674 EndZ=0
    g245-g269: Circle x25 (B-spline internal-alignment scaffolding for g270; pole/knot coordinates omitted)
    g270: BSplineCurve PolesCount=25 KnotsCount=23 Degree=3 IsPeriodic=0
    g271-g293: GeomPoint x23 (B-spline internal-alignment scaffolding for g270; pole/knot coordinates omitted)
    g294-g304: Circle x11 (B-spline internal-alignment scaffolding for g305; pole/knot coordinates omitted)
    g305: BSplineCurve PolesCount=11 KnotsCount=9 Degree=3 IsPeriodic=0
    g306-g314: GeomPoint x9 (B-spline internal-alignment scaffolding for g305; pole/knot coordinates omitted)
    g315-g326: Circle x12 (B-spline internal-alignment scaffolding for g327; pole/knot coordinates omitted)
    g327: BSplineCurve PolesCount=12 KnotsCount=10 Degree=3 IsPeriodic=0
    g328-g337: GeomPoint x10 (B-spline internal-alignment scaffolding for g327; pole/knot coordinates omitted)
  constraints (252):
    c: Coincident(g1,g0)
    c: Horizontal(g0)
    c: Vertical(g1)
    c: Coincident(g2,g3)
    c: Coincident(g3,g4)
    c: Horizontal(g4)
    c: Horizontal(g2)
    c: Vertical(g3)
    c: Block(g1)
    c: Distance(g3) = 4.86
    c: Block(g4)
    c: Distance(g0) = 10.8
    c: Distance(g2) = 10.8
    c: Coincident(g5,g0)
    c: Coincident(g6,g4)
    c: Coincident(g6,g2)
    c: Block(g8)
    c: Block(g7)
    c: Coincident(g9,g8)
    c: Coincident(g9,g7)
    c: Vertical(g9)
    c: Coincident(g10,g7)
    c: Coincident(g10,g8)
    c: Vertical(g10)
    c: Weight(g11) = 1
    c: Equal(g11, g12-g21) x10
    c: InternalAlignment(g11-g21 -> g22) x11
    c: InternalAlignment(g23-g31 -> g22) x9
    c: Block(g22)
    c: Weight(g32) = 1
    c: Equal(g32, g33-g49) x17
    c: InternalAlignment(g32-g49 -> g50) x18
    c: InternalAlignment(g51-g66 -> g50) x16
    c: Block(g50)
    c: Coincident(g67,g50)
    c: Coincident(g67,g22)
    c: Coincident(g68,g22)
    c: Coincident(g68,g50)
    c: InternalAlignment(g70,g69)
    c: InternalAlignment(g71,g69)
    c: Block(g69)
    c: InternalAlignment(g73,g72)
    c: InternalAlignment(g74,g72)
    c: Block(g72)
    c: InternalAlignment(g76,g75)
    c: InternalAlignment(g77,g75)
    c: InternalAlignment(g78,g80)
    c: InternalAlignment(g79,g80)
    c: Block(g80)
    c: Coincident(g75,g80)
    c: Block(g75)
    c: InternalAlignment(g82,g81)
    c: InternalAlignment(g83,g81)
    c: InternalAlignment(g84,g86)
    c: InternalAlignment(g85,g86)
    c: Block(g86)
    c: Coincident(g81,g86)
    c: Block(g81)
    c: Horizontal(g87)
    c: Block(g87)
    c: Horizontal(g88)
    c: Distance(g88) = 4.14
    c: Horizontal(g89)
    c: Equal(g88,g89) = 4.14
    c: Block(g89)
    c: Block(g88)
    c: Coincident(g90,g87)
    c: Vertical(g90)
    c: Distance(g90) = 11.88
    c: Coincident(g91,g90)
    c: Horizontal(g91)
    c: Coincident(g92,g91)
    c: Vertical(g92)
    c: Distance(g91) = 4.03
    c: Distance(g92) = 1.9
    c: Coincident(g93,g87)
    c: Vertical(g93)
    c: Vertical(g94)
    c: Coincident(g94,g88)
    c: Distance(g93) = 5.8
    c: Distance(g94) = 5.8
    c: Vertical(g95)
    c: Coincident(g95,g88)
    c: Distance(g95) = 6.9
    c: Coincident(g107,g92)
    c: Weight(g96) = 1
    c: Equal(g96, g97-g106) x10
    c: InternalAlignment(g96-g106 -> g107) x11
    c: InternalAlignment(g108-g116 -> g107) x9
    c: Block(g107)
    c: Block(g117)
    c: Coincident(g126,g93)
    c: Weight(g118) = 1
    c: Equal(g118, g119-g125) x7
    c: Coincident(g126,g95)
    c: InternalAlignment(g118-g125 -> g126) x8
    c: InternalAlignment(g127-g132 -> g126) x6
    c: Coincident(g133,g94)
    c: Block(g126)
    c: Block(g133)
    c: Coincident(g134,g133)
    c: Coincident(g134,g89)
    c: Vertical(g134)
    c: Horizontal(g135)
    c: Block(g135)
    c: Horizontal(g136)
    c: Equal(g88,g136) = 4.14
    c: Horizontal(g137)
    c: Equal(g136,g137) = 4.14
    c: Block(g137)
    c: Block(g136)
    c: Coincident(g138,g135)
    c: Vertical(g138)
    c: Equal(g90,g138) = 11.88
    c: Coincident(g139,g138)
    c: Horizontal(g139)
    c: Coincident(g140,g139)
    c: Vertical(g140)
    c: Equal(g91,g139) = 4.03
    c: Equal(g92,g140) = 1.9
    c: Coincident(g141,g135)
    c: Vertical(g141)
    c: Vertical(g142)
    c: Coincident(g142,g136)
    c: Equal(g93,g141) = 5.8
    c: Equal(g94,g142) = 5.8
    c: Vertical(g143)
    c: Coincident(g143,g136)
    c: Equal(g95,g143) = 6.9
    c: Coincident(g149,g140)
    c: Equal(g96,g144) = 1
    c: Equal(g144, g145-g148) x4
    c: InternalAlignment(g144-g148 -> g149) x5
    c: InternalAlignment(g150-g158 -> g149) x9
    c: Block(g149)
    c: Block(g159)
    c: Coincident(g168,g141)
    c: Equal(g118,g160) = 1
    c: Equal(g160, g161-g167) x7
    c: Coincident(g168,g143)
    c: InternalAlignment(g160-g167 -> g168) x8
    c: InternalAlignment(g169-g174 -> g168) x6
    c: Coincident(g175,g142)
    c: Block(g168)
    c: Block(g175)
    c: Coincident(g176,g175)
    c: Coincident(g176,g137)
    c: Vertical(g176)
    c: Coincident(g177,g137)
    c: Vertical(g177)
    c: Coincident(g178,g177)
    c: Coincident(g178,g159)
    c: InternalAlignment(g179,g178)
    c: InternalAlignment(g180,g178)
    c: Block(g178)
    c: Vertical(g181)
    c: Coincident(g181,g89)
    c: Block(g5)
    c: Coincident(g182,g1)
    c: Coincident(g182,g5)
    c: Horizontal(g182)
    c: Coincident(g186,g117)
    c: Weight(g183) = 1
    c: Equal(g183,g184)
    c: Equal(g183,g185)
    c: Coincident(g186,g181)
    c: InternalAlignment(g183,g186)
    c: InternalAlignment(g184,g186)
    c: InternalAlignment(g185,g186)
    c: InternalAlignment(g187,g186)
    c: InternalAlignment(g188,g186)
    c: Block(g186)
    c: InternalAlignment(g190,g189)
    c: InternalAlignment(g191,g189)
    c: Block(g189)
    c: InternalAlignment(g193,g192)
    c: InternalAlignment(g194,g192)
    c: Block(g192)
    c: Horizontal(g195)
    c: Block(g195)
    c: Coincident(g196,g195)
    c: Vertical(g196)
    c: Block(g196)
    c: Distance(g195) = 3.71244
    c: Coincident(g197,g196)
    c: Horizontal(g197)
    c: Distance(g197) = 4.1
    c: Coincident(g198,g192)
    c: Coincident(g198,g197)
    c: Vertical(g198)
    c: Block(g198)
    c: Coincident(g199,g192)
    c: Coincident(g199,g195)
    c: Vertical(g199)
    c: Block(g199)
    c: Horizontal(g200)
    c: Block(g200)
    c: Coincident(g201,g200)
    c: Vertical(g201)
    c: Block(g201)
    c: Coincident(g202,g201)
    c: Horizontal(g202)
    c: Block(g202)
    c: Coincident(g203,g202)
    c: Vertical(g203)
    c: Block(g203)
    c: Coincident(g204,g200)
    c: Vertical(g204)
    c: Block(g204)
    c: Coincident(g215,g203)
    c: Weight(g206) = 1
    c: Equal(g206, g207-g214) x8
    c: Coincident(g215,g205)
    c: InternalAlignment(g206-g214 -> g215) x9
    c: InternalAlignment(g216-g222 -> g215) x7
    c: Coincident(g233,g204)
    c: Weight(g223) = 1
    c: Equal(g223, g224-g232) x9
    c: Coincident(g233,g205)
    c: InternalAlignment(g223-g232 -> g233) x10
    c: InternalAlignment(g234-g241 -> g233) x8
    c: Vertical(g205)
    c: Block(g205)
    c: Block(g215)
    c: Block(g233)
    c: Horizontal(g242)
    c: Horizontal(g243)
    c: Block(g242)
    c: Block(g243)
    c: Vertical(g244)
    c: Block(g244)
    c: Coincident(g270,g243)
    c: Weight(g245) = 1
    c: Equal(g245, g246-g269) x24
    c: Coincident(g270,g244)
    c: InternalAlignment(g245-g269 -> g270) x25
    c: InternalAlignment(g271-g293 -> g270) x23
    c: Coincident(g305,g242)
    c: Weight(g294) = 1
    c: Equal(g294, g295-g304) x10
    c: Coincident(g305,g242)
    c: InternalAlignment(g294-g304 -> g305) x11
    c: InternalAlignment(g306-g314 -> g305) x9
    c: Block(g305)
    c: Coincident(g327,g243)
    c: Weight(g315) = 1
    c: Equal(g315, g316-g326) x11
    c: Coincident(g327,g244)
    c: InternalAlignment(g315-g326 -> g327) x12
    c: InternalAlignment(g328-g337 -> g327) x10
    c: Block(g327)
    c: Block(g270)
FEATURE [Part::Extrusion] Extrude075  label="CommodoreLogoAndText002"
  Base = -> Sketch084
  Dir = (0,0,1)
  DirMode = 2
  FaceMakerClass = Part::FaceMakerBullseye
  LengthFwd = 10
  LengthRev = 0
  Solid = true
  Symmetric = false
FEATURE [Part::FeaturePython] Clone001  label="CommodoreLogoAndTextScale001"  # Draft clone (typed FeaturePython)
  AttacherType = Attacher::AttachEngine3D
  Fuse = false
  Objects = -> [Extrude075]
  Placement = pos=(105,5.37,-11.6) rot=(0,0,1;0rad)
  Scale = (0.62,0.62,1)
